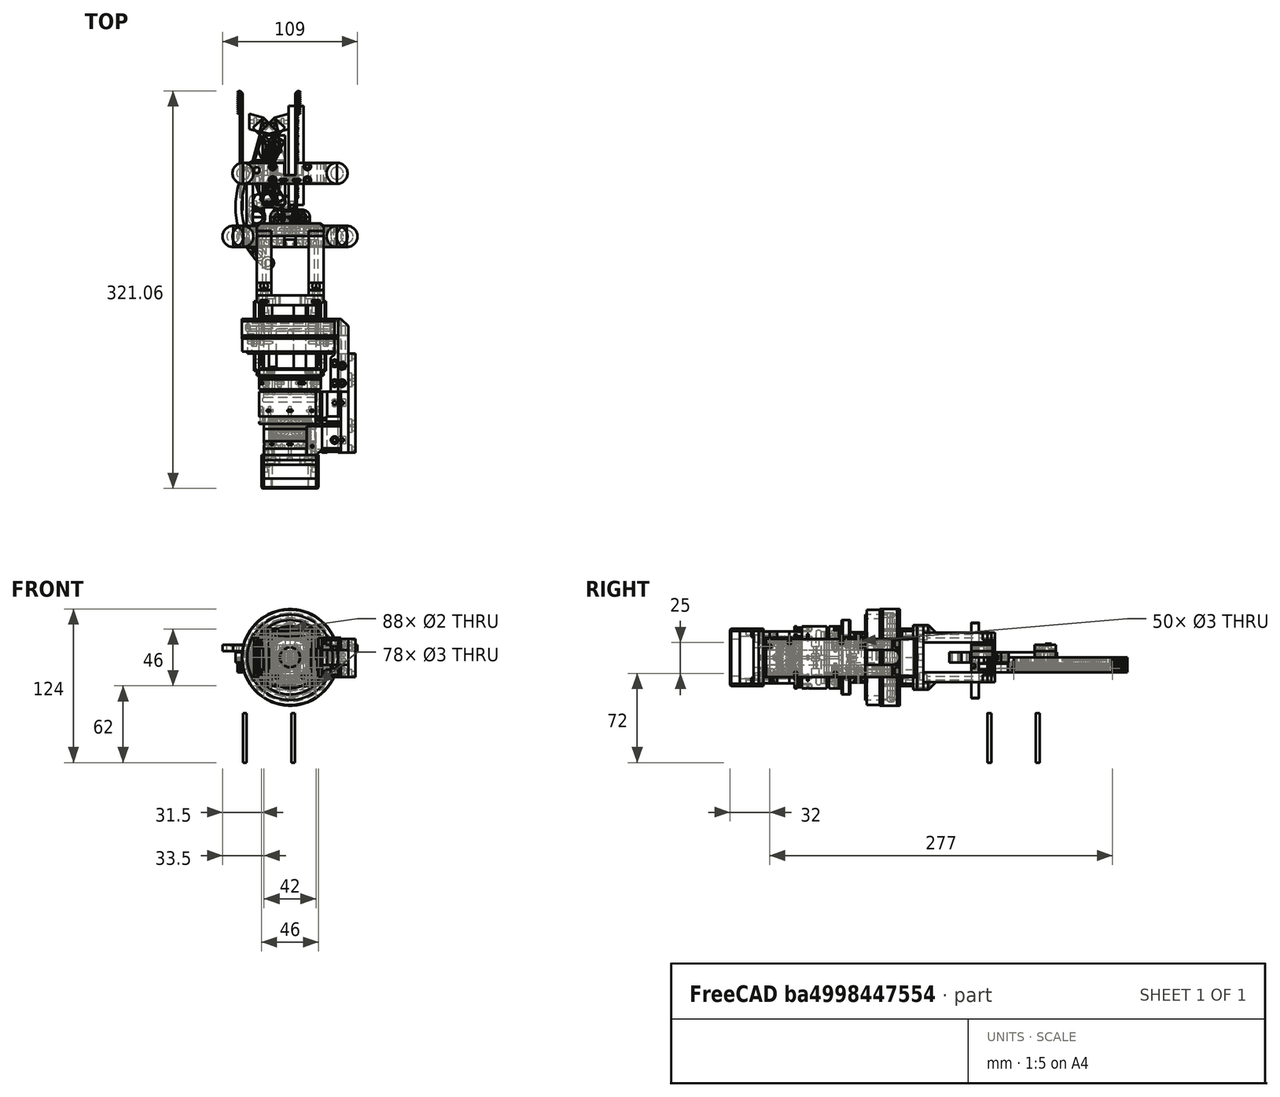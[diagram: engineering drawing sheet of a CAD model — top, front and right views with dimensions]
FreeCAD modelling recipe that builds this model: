
FCSTD DOCUMENT  (FreeCAD 0.19R24276 (Git))
Label: Wrist_001
License: All rights reserved
LicenseURL: http://en.wikipedia.org/wiki/All_rights_reserved
objects: Part::Cylinder×760, Part::Box×427, Part::Cut×422, Part::Compound×348, Part::Chamfer×68, Part::FeaturePython×42, Part::Fillet×32, Mesh::Feature×20, Part::Mirroring×8, Part::Torus×8, Part::Common×2
note: 2117 computed .brp shape members not serialized (recipe doc carries the construction recipe); baked Part::Feature solids carry a one-line shape summary decoded from their .brp

FEATURE [Part::Box] Box  label="Krychle"
  AttacherType = Attacher::AttachEngine3D
  Height = 10
  Length = 8
  Placement = pos=(-5,0,0) rot=(0,0,1;0rad)
  Width = 56
FEATURE [Part::Box] Box001  label="Krychle001"
  AttacherType = Attacher::AttachEngine3D
  Height = 10
  Length = 8
  Placement = pos=(5,0,0) rot=(0,0,1;0rad)
  Width = 56
FEATURE [Part::Box] Box002  label="Krychle002"
  AttacherType = Attacher::AttachEngine3D
  Height = 12
  Length = 16
  Placement = pos=(-13,24,-2) rot=(0,0,1;0rad)
  Width = 12
FEATURE [Part::Box] Box003  label="Krychle003"
  AttacherType = Attacher::AttachEngine3D
  Height = 12
  Length = 16
  Placement = pos=(-13,32,-2) rot=(0,0,-1;0.314159rad)
  Width = 30
FEATURE [Part::Box] Box004  label="Krychle004"
  AttacherType = Attacher::AttachEngine3D
  Height = 12
  Length = 30
  Placement = pos=(-13,24,-2) rot=(0,0,-1;1.25664rad)
  Width = 16
FEATURE [Part::Box] Box005  label="Krychle005"
  AttacherType = Attacher::AttachEngine3D
  Height = 12
  Length = 40
  Placement = pos=(-20,56,-2) rot=(0,0,1;0rad)
  Width = 20
FEATURE [Part::Cut] Cut
  Base = -> Box003
  Tool = -> Box005
FEATURE [Part::Box] Box006  label="Krychle006"
  AttacherType = Attacher::AttachEngine3D
  Height = 12
  Length = 40
  Placement = pos=(-20,-22,-2) rot=(0,0,1;0rad)
  Width = 20
FEATURE [Part::Cut] Cut001
  Base = -> Box004
  Tool = -> Box006
FEATURE [Part::Box] Box007  label="Krychle007"
  AttacherType = Attacher::AttachEngine3D
  Height = 12
  Length = 10
  Placement = pos=(5,-4,-2) rot=(0,0,1;0rad)
  Width = 56
FEATURE [Part::Box] Box008  label="Krychle008"
  AttacherType = Attacher::AttachEngine3D
  Height = 12
  Length = 8
  Placement = pos=(8,0,-2) rot=(0,0,1;0rad)
  Width = 56
FEATURE [Part::Cut] Cut002
  Base = -> Cut001
  Tool = -> Box007
FEATURE [Part::Cut] Cut003
  Base = -> Cut
  Tool = -> Box008
FEATURE [Part::Cylinder] Cylinder  label="Válec"
  Angle = 360
  AttacherType = Attacher::AttachEngine3D
  Height = 4
  Placement = pos=(-10,28,1) rot=(0,0,1;0rad)
  Radius = 5
FEATURE [Part::Cylinder] Cylinder001  label="Válec001"
  Angle = 360
  AttacherType = Attacher::AttachEngine3D
  Height = 5
  Placement = pos=(-10,28,5) rot=(0,0,1;0rad)
  Radius = 8
FEATURE [Part::Cut] Cut004
  Base = -> Cut003
  Tool = -> Cylinder
FEATURE [Part::Cylinder] Cylinder002  label="Válec002"
  Angle = 360
  AttacherType = Attacher::AttachEngine3D
  Height = 4
  Placement = pos=(-10,28,1) rot=(0,0,1;0rad)
  Radius = 5
FEATURE [Part::Cut] Cut005
  Base = -> Cut002
  Tool = -> Cylinder002
FEATURE [Part::Cylinder] Cylinder003  label="Válec003"
  Angle = 360
  AttacherType = Attacher::AttachEngine3D
  Height = 4
  Placement = pos=(-10,28,1) rot=(0,0,1;0rad)
  Radius = 5
FEATURE [Part::Cut] Cut006
  Base = -> Box002
  Tool = -> Cylinder003
FEATURE [Part::Box] Box009  label="Krychle009"
  AttacherType = Attacher::AttachEngine3D
  Height = 12
  Length = 8
  Placement = pos=(-4,16,-2) rot=(0,0,1;0rad)
  Width = 20
FEATURE [Part::Box] Box010  label="Krychle010"
  AttacherType = Attacher::AttachEngine3D
  Height = 12
  Length = 8
  Placement = pos=(-4,36,-2) rot=(0,0,-1;0.488692rad)
  Width = 10
FEATURE [Part::Box] Box011  label="Krychle011"
  AttacherType = Attacher::AttachEngine3D
  Height = 12
  Length = 8
  Placement = pos=(-4,40,-2) rot=(0,0,-1;0.558505rad)
  Width = 18
FEATURE [Part::Mirroring] mirror  label="Krychle011 (mirrored)"
  Base = (0,0,0)
  Normal = (1e-16,-1,0)
  Placement = pos=(0,56,0) rot=(0,0,1;0rad)
  Source = -> Box011
FEATURE [Part::Box] Box012  label="Krychle012"
  AttacherType = Attacher::AttachEngine3D
  Height = 12
  Length = 8
  Placement = pos=(2.5,35,-2) rot=(0,0,1;0.174533rad)
  Width = 10
FEATURE [Part::Box] Box013  label="Krychle013"
  AttacherType = Attacher::AttachEngine3D
  Height = 12
  Length = 8
  Placement = pos=(-4,16,-2) rot=(0,0,1;0rad)
  Width = 24
FEATURE [Part::Box] Box014  label="Krychle014"
  AttacherType = Attacher::AttachEngine3D
  Height = 12
  Length = 8
  Placement = pos=(-4,40,-2) rot=(0,0,-1;0.314159rad)
  Width = 10
FEATURE [Part::Box] Box015  label="Krychle015"
  AttacherType = Attacher::AttachEngine3D
  Height = 12
  Length = 8
  Placement = pos=(2.5,40,-2) rot=(0,0,1;0.349066rad)
  Width = 10
FEATURE [Part::Box] Box016  label="Krychle016"
  AttacherType = Attacher::AttachEngine3D
  Height = 12
  Length = 8
  Placement = pos=(-4,40,-2) rot=(0,0,-1;0.558505rad)
  Width = 18
FEATURE [Part::Mirroring] mirror001  label="Krychle011 (mirrored)001"
  Base = (0,0,0)
  Normal = (1e-16,-1,0)
  Placement = pos=(0,56,0) rot=(0,0,1;0rad)
  Source = -> Box016
FEATURE [Part::Compound] Compound
  Links = -> [Box013,Box014,mirror001,Box015,Box016]
FEATURE [Part::Cut] Cut007
  Base = -> Cut004
  Tool = -> Box009
FEATURE [Part::Cut] Cut008
  Base = -> Cut007
  Tool = -> Box010
FEATURE [Part::Cut] Cut009
  Base = -> Cut008
  Tool = -> Box012
FEATURE [Part::Box] Box017  label="Krychle017"
  AttacherType = Attacher::AttachEngine3D
  Height = 12
  Length = 8
  Placement = pos=(-4,40,-2) rot=(0,0,-1;0.698132rad)
  Width = 18
FEATURE [Part::Box] Box018  label="Krychle018"
  AttacherType = Attacher::AttachEngine3D
  Height = 12
  Length = 8
  Placement = pos=(2.5,40,-2) rot=(0,0,1;0.349066rad)
  Width = 10
FEATURE [Part::Box] Box019  label="Krychle019"
  AttacherType = Attacher::AttachEngine3D
  Height = 12
  Length = 8
  Placement = pos=(-4,40,-2) rot=(0,0,-1;0.314159rad)
  Width = 10
FEATURE [Part::Box] Box020  label="Krychle020"
  AttacherType = Attacher::AttachEngine3D
  Height = 12
  Length = 8
  Placement = pos=(-4,16,-2) rot=(0,0,1;0rad)
  Width = 24
FEATURE [Part::Mirroring] mirror002  label="Krychle011 (mirrored)002"
  Base = (0,0,0)
  Normal = (1e-16,-1,0)
  Placement = pos=(0,56,0) rot=(0,0,1;0rad)
  Source = -> Box017
FEATURE [Part::Cut] Cut010
  Base = -> Cut006
  Tool = -> Box020
FEATURE [Part::Cut] Cut011
  Base = -> Cut005
  Tool = -> mirror002
FEATURE [Part::Box] Box021  label="Krychle021"
  AttacherType = Attacher::AttachEngine3D
  Height = 12
  Length = 8
  Placement = pos=(-4,16,-2) rot=(0,0,1;0rad)
  Width = 24
FEATURE [Part::Cut] Cut012
  Base = -> Cut011
  Tool = -> Box021
FEATURE [Part::Box] Box022  label="Krychle022"
  AttacherType = Attacher::AttachEngine3D
  Height = 12
  Length = 8
  Placement = pos=(1,0,-2) rot=(0,0,1;0rad)
  Width = 40
FEATURE [Part::Cut] Cut013
  Base = -> Cut009
  Tool = -> Box022
FEATURE [Part::Cut] Cut014
  Base = -> Cut013
  Tool = -> Cylinder001
FEATURE [Part::Cylinder] Cylinder004  label="Válec004"
  Angle = 360
  AttacherType = Attacher::AttachEngine3D
  Height = 5
  Placement = pos=(-10,28,5) rot=(0,0,1;0rad)
  Radius = 8
FEATURE [Part::Cylinder] Cylinder005  label="Válec005"
  Angle = 360
  AttacherType = Attacher::AttachEngine3D
  Height = 5
  Placement = pos=(-10,28,5) rot=(0,0,1;0rad)
  Radius = 8
FEATURE [Part::Cut] Cut015
  Base = -> Cut012
  Tool = -> Cylinder004
FEATURE [Part::Cut] Cut016
  Base = -> Cut010
  Tool = -> Cylinder005
FEATURE [Part::Box] Box023  label="Krychle023"
  AttacherType = Attacher::AttachEngine3D
  Height = 5
  Length = 8
  Placement = pos=(-13,-2,5) rot=(0,0,1;0rad)
  Width = 24
FEATURE [Part::Cylinder] Cylinder006  label="Válec006"
  Angle = 360
  AttacherType = Attacher::AttachEngine3D
  Height = 20
  Placement = pos=(-10,28,1) rot=(0,0,1;0rad)
  Radius = 2.5
FEATURE [Part::Cut] Cut017
  Base = -> Cut015
  Tool = -> Box023
FEATURE [Part::Cylinder] Cylinder007  label="Válec007"
  Angle = 360
  AttacherType = Attacher::AttachEngine3D
  Height = 10
  Radius = 1.5
FEATURE [Part::Cylinder] Cylinder008  label="Válec008"
  Angle = 360
  AttacherType = Attacher::AttachEngine3D
  Height = 10
  Placement = pos=(0,50,3) rot=(0,1,0;1.5708rad)
  Radius = 1.5
FEATURE [Part::Box] Box024  label="Krychle024"
  AttacherType = Attacher::AttachEngine3D
  Height = 12
  Length = 13
  Placement = pos=(3,10,-2) rot=(0,0,1;0rad)
  Width = 32
FEATURE [Part::Cut] Cut018
  Base = -> Cut017
  Tool = -> Box024
FEATURE [Part::Cylinder] Cylinder009  label="Válec009"
  Angle = 360
  AttacherType = Attacher::AttachEngine3D
  Height = 4
  Placement = pos=(0,2,1) rot=(0,0,1;0rad)
  Radius = 5
FEATURE [Part::Cylinder] Cylinder010  label="Válec010"
  Angle = 360
  AttacherType = Attacher::AttachEngine3D
  Height = 5
  Placement = pos=(0,2,5) rot=(0,0,1;0rad)
  Radius = 7
FEATURE [Part::Cut] Cut019
  Base = -> Cut018
  Tool = -> Cylinder009
FEATURE [Part::Cut] Cut020
  Base = -> Cut019
  Tool = -> Cylinder010
FEATURE [Part::Cut] Cut021
  Base = -> Cut014
  Tool = -> Cylinder008
FEATURE [Part::Box] Box025  label="Krychle025"
  AttacherType = Attacher::AttachEngine3D
  Height = 12
  Length = 12
  Placement = pos=(-13,24,-2) rot=(0,0,1;0rad)
  Width = 12
FEATURE [Part::Cylinder] Cylinder011  label="Válec011"
  Angle = 360
  AttacherType = Attacher::AttachEngine3D
  Height = 4
  Placement = pos=(-10,30,1) rot=(0,0,1;0rad)
  Radius = 5
FEATURE [Part::Cylinder] Cylinder012  label="Válec012"
  Angle = 360
  AttacherType = Attacher::AttachEngine3D
  Height = 5
  Placement = pos=(-20,30,5) rot=(0,0,1;0rad)
  Radius = 16
FEATURE [Part::Compound] Compound001
  Links = -> [Cylinder011,Cylinder012]
FEATURE [Part::Cut] Cut022
  Base = -> Box025
  Tool = -> Compound001
FEATURE [Part::Box] Box026  label="Krychle026"
  AttacherType = Attacher::AttachEngine3D
  Height = 12
  Length = 12
  Placement = pos=(-13,36,-2) rot=(0,0,-1;0.261799rad)
  Width = 24
FEATURE [Part::Box] Box027  label="Krychle027"
  AttacherType = Attacher::AttachEngine3D
  Height = 12
  Length = 12
  Placement = pos=(-6.8,59.2,-2) rot=(0,0,-1;0.785398rad)
  Width = 16
FEATURE [Part::Box] Box028  label="Krychle028"
  AttacherType = Attacher::AttachEngine3D
  Height = 12
  Length = 12
  Placement = pos=(-4.1,-0.4,-2) rot=(0,0,1;0.349066rad)
  Width = 26
FEATURE [Part::Box] Box029  label="Krychle029"
  AttacherType = Attacher::AttachEngine3D
  Height = 12
  Length = 12
  Placement = pos=(4.5,70.5,-2) rot=(0,0,-1;1.309rad)
  Width = 12
FEATURE [Part::Box] Box030  label="Krychle030"
  AttacherType = Attacher::AttachEngine3D
  Height = 12
  Length = 12
  Placement = pos=(16,0,-2) rot=(0,0,1;0rad)
  Width = 80
FEATURE [Part::Cut] Cut023
  Base = -> Box029
  Tool = -> Box030
FEATURE [Part::Box] Box032  label="Krychle032"
  AttacherType = Attacher::AttachEngine3D
  Height = 12
  Length = 12
  Placement = pos=(16,0,-2) rot=(0,0,1;0rad)
  Width = 80
FEATURE [Part::Box] Box033  label="Krychle033"
  AttacherType = Attacher::AttachEngine3D
  Height = 12
  Length = 12
  Placement = pos=(11.4,-4.4,-2) rot=(0,0,1;1.309rad)
  Width = 18
FEATURE [Part::Cylinder] Cylinder013  label="Válec013"
  Angle = 360
  AttacherType = Attacher::AttachEngine3D
  Height = 7
  Placement = pos=(10,-10,-2) rot=(0,0,1;0rad)
  Radius = 7
FEATURE [Part::Box] Box034  label="Krychle034"
  AttacherType = Attacher::AttachEngine3D
  Height = 7
  Length = 12
  Placement = pos=(4,-10,-2) rot=(0,0,1;0rad)
  Width = 18
FEATURE [Part::Cylinder] Cylinder014  label="Válec014"
  Angle = 360
  AttacherType = Attacher::AttachEngine3D
  Height = 4
  Placement = pos=(10,-10,1) rot=(0,0,1;0rad)
  Radius = 5
FEATURE [Part::Cut] Cut024
  Base = -> Cylinder013
  Tool = -> Cylinder014
FEATURE [Part::Cylinder] Cylinder015  label="Válec015"
  Angle = 360
  AttacherType = Attacher::AttachEngine3D
  Height = 4
  Placement = pos=(10,-10,1) rot=(0,0,1;0rad)
  Radius = 5
FEATURE [Part::Cut] Cut025
  Base = -> Box034
  Tool = -> Cylinder015
FEATURE [Part::Fillet] Fillet
  Base = -> Cut025
  Edges = 1 edges r=4: [Edge16]
FEATURE [Part::Chamfer] Chamfer
  Base = -> Box033
  Edges = 2 edges r=4: [Edge1,Edge5]
FEATURE [Part::Cylinder] Cylinder016  label="Válec016"
  Angle = 360
  AttacherType = Attacher::AttachEngine3D
  Height = 5
  Placement = pos=(-20,30,5) rot=(0,0,1;0rad)
  Radius = 16
FEATURE [Part::Cylinder] Cylinder017  label="Válec017"
  Angle = 360
  AttacherType = Attacher::AttachEngine3D
  Height = 5
  Placement = pos=(-20,30,5) rot=(0,0,1;0rad)
  Radius = 16
FEATURE [Part::Cut] Cut026
  Base = -> Box028
  Tool = -> Cylinder016
FEATURE [Part::Cut] Cut027
  Base = -> Box026
  Tool = -> Cylinder017
FEATURE [Part::Fillet] Fillet001
  Base = -> Cut026
  Edges = 1 edges r=20: [Edge2]
FEATURE [Part::Fillet] Fillet002
  Base = -> Cut027
  Edges = 1 edges r=20: [Edge3]
FEATURE [Part::Fillet] Fillet004
  Base = -> Chamfer
  Edges = 1 edges r=4: [Edge4]
FEATURE [Part::Fillet] Fillet005
  Base = -> Fillet001
  Edges = 1 edges r=2: [Edge2]
FEATURE [Part::Fillet] Fillet006
  Base = -> Fillet004
  Edges = 1 edges r=3: [Edge2]
FEATURE [Part::Fillet] Fillet007
  Base = -> Fillet006
  Edges = 2 edges r=3: [Edge21,Edge23]
FEATURE [Part::Fillet] Fillet008
  Base = -> Fillet007
  Edges = 1 edges r=4: [Edge27]
FEATURE [Part::Box] Box037  label="Krychle037"
  AttacherType = Attacher::AttachEngine3D
  Height = 2
  Length = 6
  Placement = pos=(-2,11,4) rot=(0,0,1;0rad)
  Width = 6
FEATURE [Part::Cylinder] Cylinder020  label="Válec020"
  Angle = 360
  AttacherType = Attacher::AttachEngine3D
  Height = 12
  Placement = pos=(1,14,6) rot=(0,0,1;0rad)
  Radius = 1.5
FEATURE [Part::Cylinder] Cylinder021  label="Válec021"
  Angle = 360
  AttacherType = Attacher::AttachEngine3D
  Height = 4
  Placement = pos=(1,14,0) rot=(0,0,1;0rad)
  Radius = 1.5
FEATURE [Part::Compound] Compound002
  Links = -> [Box037,Cylinder020,Cylinder021]
  Placement = pos=(3.5,2,0) rot=(0,0,1;0.349066rad)
FEATURE [Part::Cylinder] Cylinder022  label="Válec022"
  Angle = 360
  AttacherType = Attacher::AttachEngine3D
  Height = 4
  Placement = pos=(1,14,0) rot=(0,0,1;0rad)
  Radius = 1.5
FEATURE [Part::Box] Box038  label="Krychle038"
  AttacherType = Attacher::AttachEngine3D
  Height = 2
  Length = 6
  Placement = pos=(-2,11,4) rot=(0,0,1;0rad)
  Width = 6
FEATURE [Part::Cylinder] Cylinder023  label="Válec023"
  Angle = 360
  AttacherType = Attacher::AttachEngine3D
  Height = 12
  Placement = pos=(1,14,6) rot=(0,0,1;0rad)
  Radius = 1.5
FEATURE [Part::Compound] Compound003
  Links = -> [Box038,Cylinder023,Cylinder022]
  Placement = pos=(-6.1,31,0) rot=(0,0,-1;0.261799rad)
FEATURE [Part::Cylinder] Cylinder024  label="Válec024"
  Angle = 360
  AttacherType = Attacher::AttachEngine3D
  Height = 4
  Placement = pos=(1,14,0) rot=(0,0,1;0rad)
  Radius = 1.5
FEATURE [Part::Box] Box039  label="Krychle039"
  AttacherType = Attacher::AttachEngine3D
  Height = 2
  Length = 6
  Placement = pos=(-2,11,4) rot=(0,0,1;0rad)
  Width = 6
FEATURE [Part::Cylinder] Cylinder025  label="Válec025"
  Angle = 360
  AttacherType = Attacher::AttachEngine3D
  Height = 12
  Placement = pos=(1,14,6) rot=(0,0,1;0rad)
  Radius = 1.5
FEATURE [Part::Compound] Compound004
  Links = -> [Box039,Cylinder025,Cylinder024]
  Placement = pos=(-2.9,-11.9,0) rot=(0,0,-1;0.261799rad)
FEATURE [Part::Cylinder] Cylinder026  label="Válec026"
  Angle = 360
  AttacherType = Attacher::AttachEngine3D
  Height = 4
  Placement = pos=(1,14,0) rot=(0,0,1;0rad)
  Radius = 1.5
FEATURE [Part::Box] Box040  label="Krychle040"
  AttacherType = Attacher::AttachEngine3D
  Height = 2
  Length = 6
  Placement = pos=(-2,11,4) rot=(0,0,1;0rad)
  Width = 6
FEATURE [Part::Cylinder] Cylinder027  label="Válec027"
  Angle = 360
  AttacherType = Attacher::AttachEngine3D
  Height = 12
  Placement = pos=(1,14,6) rot=(0,0,1;0rad)
  Radius = 1.5
FEATURE [Part::Compound] Compound005
  Links = -> [Box040,Cylinder027,Cylinder026]
  Placement = pos=(-2.9,-11.9,0) rot=(0,0,-1;0.261799rad)
FEATURE [Part::Cut] Cut028
  Base = -> Fillet008
  Tool = -> Compound004
FEATURE [Part::Cut] Cut029
  Base = -> Fillet005
  Tool = -> Compound002
FEATURE [Part::Cut] Cut030
  Base = -> Fillet002
  Tool = -> Compound003
FEATURE [Part::Cylinder] Cylinder028  label="Válec028"
  Angle = 360
  AttacherType = Attacher::AttachEngine3D
  Height = 4
  Placement = pos=(1,14,-0.1) rot=(0,0,1;0rad)
  Radius = 1.5
FEATURE [Part::Box] Box041  label="Krychle041"
  AttacherType = Attacher::AttachEngine3D
  Height = 2
  Length = 6
  Placement = pos=(-2,11,4) rot=(0,0,1;0rad)
  Width = 6
FEATURE [Part::Cylinder] Cylinder029  label="Válec029"
  Angle = 360
  AttacherType = Attacher::AttachEngine3D
  Height = 12
  Placement = pos=(1,14,6) rot=(0,0,1;0rad)
  Radius = 1.5
FEATURE [Part::Compound] Compound006
  Links = -> [Box041,Cylinder029,Cylinder028]
  Placement = pos=(12.1,54,0) rot=(0,0,1;0.785398rad)
FEATURE [Part::Cut] Cut031
  Base = -> Cut029
  Tool = -> Compound005
FEATURE [Part::Cylinder] Cylinder030  label="Válec030"
  Angle = 360
  AttacherType = Attacher::AttachEngine3D
  Height = 4
  Placement = pos=(1,14,-0.1) rot=(0,0,1;0rad)
  Radius = 1.5
FEATURE [Part::Box] Box042  label="Krychle042"
  AttacherType = Attacher::AttachEngine3D
  Height = 2
  Length = 6
  Placement = pos=(-2,11,4) rot=(0,0,1;0rad)
  Width = 6
FEATURE [Part::Cylinder] Cylinder031  label="Válec031"
  Angle = 360
  AttacherType = Attacher::AttachEngine3D
  Height = 12
  Placement = pos=(1,14,6) rot=(0,0,1;0rad)
  Radius = 1.5
FEATURE [Part::Compound] Compound007
  Links = -> [Box042,Cylinder031,Cylinder030]
  Placement = pos=(12.1,54,0) rot=(0,0,1;0.785398rad)
FEATURE [Part::Cut] Cut032
  Base = -> Cut023
  Tool = -> Compound006
FEATURE [Part::Cut] Cut033
  Base = -> Box027
  Tool = -> Compound007
FEATURE [Part::Cylinder] Cylinder032  label="Válec032"
  Angle = 360
  AttacherType = Attacher::AttachEngine3D
  Height = 12
  Placement = pos=(1,14,6) rot=(0,0,1;0rad)
  Radius = 1.5
FEATURE [Part::Box] Box043  label="Krychle043"
  AttacherType = Attacher::AttachEngine3D
  Height = 2
  Length = 6
  Placement = pos=(-2,11,4) rot=(0,0,1;0rad)
  Width = 6
FEATURE [Part::Cylinder] Cylinder033  label="Válec033"
  Angle = 360
  AttacherType = Attacher::AttachEngine3D
  Height = 4
  Placement = pos=(1,14,-0.1) rot=(0,0,1;0rad)
  Radius = 1.5
FEATURE [Part::Compound] Compound008
  Links = -> [Box043,Cylinder032,Cylinder033]
  Placement = pos=(6,53,2) rot=(0,1,0;1.5708rad)
FEATURE [Part::Box] Box044  label="Krychle044"
  AttacherType = Attacher::AttachEngine3D
  Height = 2
  Length = 6
  Placement = pos=(-2,11,4) rot=(0,0,1;0rad)
  Width = 6
FEATURE [Part::Cylinder] Cylinder034  label="Válec034"
  Angle = 360
  AttacherType = Attacher::AttachEngine3D
  Height = 4
  Placement = pos=(1,14,-0.1) rot=(0,0,1;0rad)
  Radius = 1.5
FEATURE [Part::Cylinder] Cylinder035  label="Válec035"
  Angle = 360
  AttacherType = Attacher::AttachEngine3D
  Height = 12
  Placement = pos=(1,14,6) rot=(0,0,1;0rad)
  Radius = 1.5
FEATURE [Part::Compound] Compound009
  Links = -> [Box044,Cylinder035,Cylinder034]
  Placement = pos=(6,53,2) rot=(0,1,0;1.5708rad)
FEATURE [Part::Cut] Cut034
  Base = -> Cut033
  Tool = -> Compound009
FEATURE [Part::Cut] Cut035
  Base = -> Cut032
  Tool = -> Compound008
FEATURE [Part::Cylinder] Cylinder036  label="Válec036"
  Angle = 360
  AttacherType = Attacher::AttachEngine3D
  Height = 5
  Placement = pos=(-20,30,5) rot=(0,0,1;0rad)
  Radius = 16
FEATURE [Part::Box] Box045  label="Krychle045"
  AttacherType = Attacher::AttachEngine3D
  Height = 12
  Length = 12
  Placement = pos=(-13,24,-2) rot=(0,0,1;0rad)
  Width = 12
FEATURE [Part::Cylinder] Cylinder037  label="Válec037"
  Angle = 360
  AttacherType = Attacher::AttachEngine3D
  Height = 4
  Placement = pos=(-10,30,1) rot=(0,0,1;0rad)
  Radius = 5
FEATURE [Part::Cylinder] Cylinder038  label="Válec038"
  Angle = 360
  AttacherType = Attacher::AttachEngine3D
  Height = 16
  Placement = pos=(1,14,1) rot=(0,0,1;0rad)
  Radius = 1.5
FEATURE [Part::Cylinder] Cylinder039  label="Válec039"
  Angle = 360
  AttacherType = Attacher::AttachEngine3D
  Height = 5
  Placement = pos=(-20,30,5) rot=(0,0,1;0rad)
  Radius = 16
FEATURE [Part::Box] Box046  label="Krychle046"
  AttacherType = Attacher::AttachEngine3D
  Height = 12
  Length = 12
  Placement = pos=(-6.8,59.2,-2) rot=(0,0,-1;0.785398rad)
  Width = 16
FEATURE [Part::Box] Box047  label="Krychle047"
  AttacherType = Attacher::AttachEngine3D
  Height = 2
  Length = 6
  Placement = pos=(-2,11,20) rot=(0,0,1;0rad)
  Width = 6
FEATURE [Part::Box] Box048  label="Krychle048"
  AttacherType = Attacher::AttachEngine3D
  Height = 12
  Length = 12
  Placement = pos=(-4.1,-0.4,-2) rot=(0,0,1;0.349066rad)
  Width = 26
FEATURE [Part::Box] Box049  label="Krychle049"
  AttacherType = Attacher::AttachEngine3D
  Height = 12
  Length = 12
  Placement = pos=(-13,36,-2) rot=(0,0,-1;0.261799rad)
  Width = 24
FEATURE [Part::Box] Box050  label="Krychle050"
  AttacherType = Attacher::AttachEngine3D
  Height = 12
  Length = 12
  Placement = pos=(4.5,70.5,-2) rot=(0,0,-1;1.309rad)
  Width = 12
FEATURE [Part::Cylinder] Cylinder040  label="Válec040"
  Angle = 360
  AttacherType = Attacher::AttachEngine3D
  Height = 4
  Placement = pos=(10,-10,1) rot=(0,0,1;0rad)
  Radius = 5
FEATURE [Part::Box] Box051  label="Krychle051"
  AttacherType = Attacher::AttachEngine3D
  Height = 12
  Length = 12
  Placement = pos=(11.4,-4.4,-2) rot=(0,0,1;1.309rad)
  Width = 18
FEATURE [Part::Chamfer] Chamfer001
  Base = -> Box051
  Edges = 2 edges r=4: [Edge1,Edge5]
FEATURE [Part::Fillet] Fillet010
  Base = -> Chamfer001
  Edges = 1 edges r=4: [Edge4]
FEATURE [Part::Box] Box052  label="Krychle052"
  AttacherType = Attacher::AttachEngine3D
  Height = 7
  Length = 12
  Placement = pos=(4,-10,-2) rot=(0,0,1;0rad)
  Width = 18
FEATURE [Part::Cylinder] Cylinder041  label="Válec041"
  Angle = 360
  AttacherType = Attacher::AttachEngine3D
  Height = 4
  Placement = pos=(10,-10,1) rot=(0,0,1;0rad)
  Radius = 5
FEATURE [Part::Cut] Cut036
  Base = -> Box052
  Tool = -> Cylinder041
FEATURE [Part::Box] Box053  label="Krychle053"
  AttacherType = Attacher::AttachEngine3D
  Height = 12
  Length = 12
  Placement = pos=(16,0,-2) rot=(0,0,1;0rad)
  Width = 80
FEATURE [Part::Cut] Cut037
  Base = -> Box050
  Tool = -> Box053
FEATURE [Part::Cylinder] Cylinder042  label="Válec042"
  Angle = 360
  AttacherType = Attacher::AttachEngine3D
  Height = 5
  Placement = pos=(-20,30,5) rot=(0,0,1;0rad)
  Radius = 16
FEATURE [Part::Cylinder] Cylinder043  label="Válec043"
  Angle = 360
  AttacherType = Attacher::AttachEngine3D
  Height = 7
  Placement = pos=(10,-10,-2) rot=(0,0,1;0rad)
  Radius = 7
FEATURE [Part::Cut] Cut038
  Base = -> Box048
  Tool = -> Cylinder042
FEATURE [Part::Fillet] Fillet011
  Base = -> Cut038
  Edges = 1 edges r=20: [Edge2]
FEATURE [Part::Cut] Cut039
  Base = -> Cylinder043
  Tool = -> Cylinder040
FEATURE [Part::Cut] Cut040
  Base = -> Box049
  Tool = -> Cylinder039
FEATURE [Part::Fillet] Fillet009
  Base = -> Cut040
  Edges = 1 edges r=20: [Edge3]
FEATURE [Part::Fillet] Fillet012
  Base = -> Cut036
  Edges = 1 edges r=4: [Edge16]
FEATURE [Part::Fillet] Fillet015
  Base = -> Fillet010
  Edges = 1 edges r=3: [Edge2]
FEATURE [Part::Fillet] Fillet014
  Base = -> Fillet015
  Edges = 2 edges r=3: [Edge21,Edge23]
FEATURE [Part::Fillet] Fillet013
  Base = -> Fillet014
  Edges = 1 edges r=4: [Edge27]
FEATURE [Part::Compound] Compound016
  Links = -> [Cylinder037,Cylinder036]
FEATURE [Part::Cut] Cut041
  Base = -> Box045
  Tool = -> Compound016
FEATURE [Part::Fillet] Fillet016
  Base = -> Fillet011
  Edges = 1 edges r=2: [Edge2]
FEATURE [Part::Cylinder] Cylinder044  label="Válec044"
  Angle = 360
  AttacherType = Attacher::AttachEngine3D
  Height = 3
  Placement = pos=(1,14,-2) rot=(0,0,1;0rad)
  Radius = 3
FEATURE [Part::Box] Box054  label="Krychle054"
  AttacherType = Attacher::AttachEngine3D
  Height = 2
  Length = 6
  Placement = pos=(-2,11,20) rot=(0,0,1;0rad)
  Width = 6
FEATURE [Part::Cylinder] Cylinder045  label="Válec045"
  Angle = 360
  AttacherType = Attacher::AttachEngine3D
  Height = 3
  Placement = pos=(1,14,-2) rot=(0,0,1;0rad)
  Radius = 3
FEATURE [Part::Cylinder] Cylinder046  label="Válec046"
  Angle = 360
  AttacherType = Attacher::AttachEngine3D
  Height = 3
  Placement = pos=(1,14,-2) rot=(0,0,1;0rad)
  Radius = 3
FEATURE [Part::Box] Box055  label="Krychle055"
  AttacherType = Attacher::AttachEngine3D
  Height = 2
  Length = 6
  Placement = pos=(-2,11,20) rot=(0,0,1;0rad)
  Width = 6
FEATURE [Part::Cylinder] Cylinder047  label="Válec047"
  Angle = 360
  AttacherType = Attacher::AttachEngine3D
  Height = 16
  Placement = pos=(1,14,1) rot=(0,0,1;0rad)
  Radius = 1.5
FEATURE [Part::Compound] Compound015
  Links = -> [Box055,Cylinder047,Cylinder045]
  Placement = pos=(-6.1,31,0) rot=(0,0,-1;0.261799rad)
FEATURE [Part::Cut] Cut043
  Base = -> Fillet009
  Tool = -> Compound015
FEATURE [Part::Cylinder] Cylinder048  label="Válec048"
  Angle = 360
  AttacherType = Attacher::AttachEngine3D
  Height = 3
  Placement = pos=(1,14,-2) rot=(0,0,1;0rad)
  Radius = 3
FEATURE [Part::Box] Box056  label="Krychle056"
  AttacherType = Attacher::AttachEngine3D
  Height = 2
  Length = 6
  Placement = pos=(-2,11,20) rot=(0,0,1;0rad)
  Width = 6
FEATURE [Part::Cylinder] Cylinder049  label="Válec049"
  Angle = 360
  AttacherType = Attacher::AttachEngine3D
  Height = 3
  Placement = pos=(1,14,-2) rot=(0,0,1;0rad)
  Radius = 3
FEATURE [Part::Box] Box057  label="Krychle057"
  AttacherType = Attacher::AttachEngine3D
  Height = 2
  Length = 6
  Placement = pos=(-2,11,20) rot=(0,0,1;0rad)
  Width = 6
FEATURE [Part::Cylinder] Cylinder050  label="Válec050"
  Angle = 360
  AttacherType = Attacher::AttachEngine3D
  Height = 16
  Placement = pos=(1,14,1) rot=(0,0,1;0rad)
  Radius = 1.5
FEATURE [Part::Compound] Compound011
  Links = -> [Box057,Cylinder050,Cylinder049]
  Placement = pos=(-2.9,-11.9,0) rot=(0,0,-1;0.261799rad)
FEATURE [Part::Cut] Cut044
  Base = -> Fillet013
  Tool = -> Compound011
FEATURE [Part::Cylinder] Cylinder051  label="Válec051"
  Angle = 360
  AttacherType = Attacher::AttachEngine3D
  Height = 16
  Placement = pos=(1,14,1) rot=(0,0,1;0rad)
  Radius = 1.5
FEATURE [Part::Compound] Compound014
  Links = -> [Box056,Cylinder051,Cylinder048]
  Placement = pos=(-2.9,-11.9,0) rot=(0,0,-1;0.261799rad)
FEATURE [Part::Cylinder] Cylinder052  label="Válec052"
  Angle = 360
  AttacherType = Attacher::AttachEngine3D
  Height = 16
  Placement = pos=(1,14,1) rot=(0,0,1;0rad)
  Radius = 1.5
FEATURE [Part::Compound] Compound012
  Links = -> [Box054,Cylinder052,Cylinder044]
  Placement = pos=(12.1,54,0) rot=(0,0,1;0.785398rad)
FEATURE [Part::Cylinder] Cylinder053  label="Válec053"
  Angle = 360
  AttacherType = Attacher::AttachEngine3D
  Height = 3
  Placement = pos=(1,14,-2) rot=(0,0,1;0rad)
  Radius = 3
FEATURE [Part::Box] Box058  label="Krychle058"
  AttacherType = Attacher::AttachEngine3D
  Height = 2
  Length = 6
  Placement = pos=(-2,11,20) rot=(0,0,1;0rad)
  Width = 6
FEATURE [Part::Cylinder] Cylinder054  label="Válec054"
  Angle = 360
  AttacherType = Attacher::AttachEngine3D
  Height = 16
  Placement = pos=(1,14,1) rot=(0,0,1;0rad)
  Radius = 1.5
FEATURE [Part::Compound] Compound013
  Links = -> [Box058,Cylinder054,Cylinder046]
  Placement = pos=(3.5,2,0) rot=(0,0,1;0.349066rad)
FEATURE [Part::Cut] Cut042
  Base = -> Fillet016
  Tool = -> Compound013
FEATURE [Part::Cut] Cut045
  Base = -> Cut042
  Tool = -> Compound014
FEATURE [Part::Cut] Cut047
  Base = -> Cut037
  Tool = -> Compound012
FEATURE [Part::Box] Box059  label="Krychle059"
  AttacherType = Attacher::AttachEngine3D
  Height = 2
  Length = 6
  Placement = pos=(-2,11,4) rot=(0,0,1;0rad)
  Width = 6
FEATURE [Part::Box] Box060  label="Krychle060"
  AttacherType = Attacher::AttachEngine3D
  Height = 2
  Length = 6
  Placement = pos=(-2,11,4) rot=(0,0,1;0rad)
  Width = 6
FEATURE [Part::Cylinder] Cylinder055  label="Válec055"
  Angle = 360
  AttacherType = Attacher::AttachEngine3D
  Height = 4
  Placement = pos=(1,14,-0.1) rot=(0,0,1;0rad)
  Radius = 1.5
FEATURE [Part::Cylinder] Cylinder056  label="Válec056"
  Angle = 360
  AttacherType = Attacher::AttachEngine3D
  Height = 4
  Placement = pos=(1,14,0) rot=(0,0,1;0rad)
  Radius = 1.5
FEATURE [Part::Cylinder] Cylinder057  label="Válec057"
  Angle = 360
  AttacherType = Attacher::AttachEngine3D
  Height = 12
  Placement = pos=(1,14,6) rot=(0,0,1;0rad)
  Radius = 1.5
FEATURE [Part::Cylinder] Cylinder058  label="Válec058"
  Angle = 360
  AttacherType = Attacher::AttachEngine3D
  Height = 12
  Placement = pos=(1,14,6) rot=(0,0,1;0rad)
  Radius = 1.5
FEATURE [Part::Compound] Compound018
  Links = -> [Box047,Cylinder038,Cylinder053]
  Placement = pos=(12.1,54,0) rot=(0,0,1;0.785398rad)
FEATURE [Part::Cut] Cut049
  Base = -> Box046
  Tool = -> Compound018
FEATURE [Part::Compound] Compound019
  Links = -> [Box060,Cylinder058,Cylinder055]
  Placement = pos=(6,53,2) rot=(0,1,0;1.5708rad)
FEATURE [Part::Cut] Cut048
  Base = -> Cut047
  Tool = -> Compound019
FEATURE [Part::Compound] Compound020
  Links = -> [Box059,Cylinder057,Cylinder056]
  Placement = pos=(6,53,2) rot=(0,1,0;1.5708rad)
FEATURE [Part::Cut] Cut046
  Base = -> Cut049
  Tool = -> Compound020
FEATURE [Part::Box] Box061  label="Krychle061"
  AttacherType = Attacher::AttachEngine3D
  Height = 2
  Length = 6
  Placement = pos=(-2,11,4) rot=(0,0,1;0rad)
  Width = 6
FEATURE [Part::Cylinder] Cylinder059  label="Válec059"
  Angle = 360
  AttacherType = Attacher::AttachEngine3D
  Height = 4
  Placement = pos=(1,14,-0.1) rot=(0,0,1;0rad)
  Radius = 1.5
FEATURE [Part::Cylinder] Cylinder060  label="Válec060"
  Angle = 360
  AttacherType = Attacher::AttachEngine3D
  Height = 12
  Placement = pos=(1,14,6) rot=(0,0,1;0rad)
  Radius = 1.5
FEATURE [Part::Compound] Compound022
  Links = -> [Box061,Cylinder060,Cylinder059]
  Placement = pos=(6,-14,2) rot=(0,1,0;1.5708rad)
FEATURE [Part::Cut] Cut050
  Base = -> Fillet
  Tool = -> Compound022
FEATURE [Part::Cylinder] Cylinder061  label="Válec061"
  Angle = 360
  AttacherType = Attacher::AttachEngine3D
  Height = 4
  Placement = pos=(1,14,-0.1) rot=(0,0,1;0rad)
  Radius = 1.5
FEATURE [Part::Cylinder] Cylinder062  label="Válec062"
  Angle = 360
  AttacherType = Attacher::AttachEngine3D
  Height = 12
  Placement = pos=(1,14,6) rot=(0,0,1;0rad)
  Radius = 1.5
FEATURE [Part::Box] Box062  label="Krychle062"
  AttacherType = Attacher::AttachEngine3D
  Height = 2
  Length = 6
  Placement = pos=(-2,11,4) rot=(0,0,1;0rad)
  Width = 6
FEATURE [Part::Compound] Compound023
  Links = -> [Box062,Cylinder062,Cylinder061]
  Placement = pos=(6,-14,2) rot=(0,1,0;1.5708rad)
FEATURE [Part::Cut] Cut051
  Base = -> Cut028
  Tool = -> Compound023
FEATURE [Part::Cylinder] Cylinder063  label="Válec063"
  Angle = 360
  AttacherType = Attacher::AttachEngine3D
  Height = 4
  Placement = pos=(1,14,-0.1) rot=(0,0,1;0rad)
  Radius = 1.5
FEATURE [Part::Cylinder] Cylinder064  label="Válec064"
  Angle = 360
  AttacherType = Attacher::AttachEngine3D
  Height = 12
  Placement = pos=(1,14,6) rot=(0,0,1;0rad)
  Radius = 1.5
FEATURE [Part::Box] Box063  label="Krychle063"
  AttacherType = Attacher::AttachEngine3D
  Height = 2
  Length = 6
  Placement = pos=(-2,11,4) rot=(0,0,1;0rad)
  Width = 6
FEATURE [Part::Compound] Compound024
  Links = -> [Box063,Cylinder064,Cylinder063]
  Placement = pos=(6,-14,2) rot=(0,1,0;1.5708rad)
FEATURE [Part::Compound] Compound025  label="revised_finger_lower"
  Links = -> [Cut051,Cut050,Cut035,Cut034,Cut031,Cut030,Cut024,Cut022]
FEATURE [Part::Cylinder] Cylinder065  label="Válec065"
  Angle = 360
  AttacherType = Attacher::AttachEngine3D
  Height = 12
  Placement = pos=(1,14,6) rot=(0,0,1;0rad)
  Radius = 1.5
FEATURE [Part::Box] Box064  label="Krychle064"
  AttacherType = Attacher::AttachEngine3D
  Height = 2
  Length = 6
  Placement = pos=(-2,11,4) rot=(0,0,1;0rad)
  Width = 6
FEATURE [Part::Cylinder] Cylinder066  label="Válec066"
  Angle = 360
  AttacherType = Attacher::AttachEngine3D
  Height = 4
  Placement = pos=(1,14,-0.1) rot=(0,0,1;0rad)
  Radius = 1.5
FEATURE [Part::Compound] Compound026
  Links = -> [Box064,Cylinder065,Cylinder066]
  Placement = pos=(6,-14,2) rot=(0,1,0;1.5708rad)
FEATURE [Part::Cut] Cut052
  Base = -> Fillet012
  Tool = -> Compound024
FEATURE [Part::Cut] Cut053
  Base = -> Cut044
  Tool = -> Compound026
FEATURE [Part::Compound] Compound027  label="revised_finger_upper"
  Links = -> [Cut039,Cut041,Cut043,Cut045,Cut046,Cut048,Cut052,Cut053]
FEATURE [Part::Cylinder] Cylinder067  label="Válec067"
  Angle = 360
  AttacherType = Attacher::AttachEngine3D
  Height = 8
  Placement = pos=(10,-10,6) rot=(0,0,1;0rad)
  Radius = 6
FEATURE [Part::Box] Box065  label="Krychle065"
  AttacherType = Attacher::AttachEngine3D
  Height = 4
  Length = 14
  Placement = pos=(10,-15,6) rot=(0,0,1;0rad)
  Width = 10
FEATURE [Part::Cylinder] Cylinder068  label="Válec068"
  Angle = 360
  AttacherType = Attacher::AttachEngine3D
  Height = 8
  Placement = pos=(24,-10,6) rot=(0,0,1;0rad)
  Radius = 5
FEATURE [Part::Box] Box066  label="Krychle066"
  AttacherType = Attacher::AttachEngine3D
  Height = 4
  Length = 14
  Placement = pos=(10,-15,10) rot=(0,0,1;0rad)
  Width = 10
FEATURE [Part::Box] Box067  label="Krychle067"
  AttacherType = Attacher::AttachEngine3D
  Height = 4
  Length = 12
  Placement = pos=(5,-24,6) rot=(0,0,1;0rad)
  Width = 14
FEATURE [Part::Box] Box068  label="Krychle068"
  AttacherType = Attacher::AttachEngine3D
  Height = 8
  Length = 26
  Placement = pos=(4,-15,6) rot=(0,0,1;0rad)
  Width = 5
FEATURE [Part::Box] Box069  label="Krychle069"
  AttacherType = Attacher::AttachEngine3D
  Height = 8
  Length = 54
  Placement = pos=(-10,-21,6) rot=(0,0,1;0rad)
  Width = 6
FEATURE [Part::Box] Box072  label="Krychle072"
  AttacherType = Attacher::AttachEngine3D
  Height = 8
  Length = 12
  Placement = pos=(-10,-73,22) rot=(0,0,1;0rad)
  Width = 52
FEATURE [Part::Box] Box073  label="Krychle073"
  AttacherType = Attacher::AttachEngine3D
  Height = 8
  Length = 12
  Placement = pos=(-10,-73,-10) rot=(0,0,1;0rad)
  Width = 52
FEATURE [Part::Box] Box074  label="Krychle074"
  AttacherType = Attacher::AttachEngine3D
  Height = 4
  Length = 12
  Placement = pos=(17,-24,10) rot=(0,0,1;0rad)
  Width = 14
FEATURE [Part::Box] Box075  label="Krychle075"
  AttacherType = Attacher::AttachEngine3D
  Height = 4
  Length = 12
  Placement = pos=(17,-24,6) rot=(0,0,1;0rad)
  Width = 14
FEATURE [Part::Box] Box076  label="Krychle076"
  AttacherType = Attacher::AttachEngine3D
  Height = 4
  Length = 14
  Placement = pos=(10,-15,6) rot=(0,0,1;0rad)
  Width = 10
FEATURE [Part::Cylinder] Cylinder069  label="Válec069"
  Angle = 360
  AttacherType = Attacher::AttachEngine3D
  Height = 8
  Placement = pos=(24,-10,6) rot=(0,0,1;0rad)
  Radius = 5
FEATURE [Part::Cut] Cut054
  Base = -> Box076
  Tool = -> Cylinder069
FEATURE [Part::Cut] Cut055
  Base = -> Cut054
  Tool = -> Box075
FEATURE [Part::Cylinder] Cylinder070  label="Válec070"
  Angle = 360
  AttacherType = Attacher::AttachEngine3D
  Height = 8
  Placement = pos=(24,-10,6) rot=(0,0,1;0rad)
  Radius = 6
FEATURE [Part::Box] Box077  label="Krychle077"
  AttacherType = Attacher::AttachEngine3D
  Height = 8
  Length = 14
  Placement = pos=(10,-15,6) rot=(0,0,1;0rad)
  Width = 11
FEATURE [Part::Box] Box078  label="Krychle078"
  AttacherType = Attacher::AttachEngine3D
  Height = 4
  Length = 4
  Placement = pos=(4,-14,8) rot=(0,0,1;0rad)
  Width = 1.4
FEATURE [Part::Cylinder] Cylinder071  label="Válec071"
  Angle = 360
  AttacherType = Attacher::AttachEngine3D
  Height = 12
  Placement = pos=(10,-10,4) rot=(0,0,1;0rad)
  Radius = 2.6
FEATURE [Part::Box] Box079  label="Krychle079"
  AttacherType = Attacher::AttachEngine3D
  Height = 4
  Length = 4
  Placement = pos=(15,-11,10) rot=(0,0,1;0rad)
  Width = 1.4
FEATURE [Part::Box] Box080  label="Krychle080"
  AttacherType = Attacher::AttachEngine3D
  Height = 4
  Length = 4
  Placement = pos=(15,-11,6) rot=(0,0,1;0rad)
  Width = 1.4
FEATURE [Part::Box] Box081  label="Krychle081"
  AttacherType = Attacher::AttachEngine3D
  Height = 4
  Length = 4
  Placement = pos=(26,-14,8) rot=(0,0,1;0rad)
  Width = 1.4
FEATURE [Part::Cylinder] Cylinder072  label="Válec072"
  Angle = 360
  AttacherType = Attacher::AttachEngine3D
  Height = 20
  Placement = pos=(3,-10,10) rot=(1,0,0;1.5708rad)
  Radius = 1
FEATURE [Part::Cylinder] Cylinder073  label="Válec073"
  Angle = 360
  AttacherType = Attacher::AttachEngine3D
  Height = 20
  Placement = pos=(31,-10,10) rot=(1,0,0;1.5708rad)
  Radius = 1
FEATURE [Part::Cylinder] Cylinder074  label="Válec074"
  Angle = 360
  AttacherType = Attacher::AttachEngine3D
  Height = 20
  Placement = pos=(17,-10,8) rot=(1,0,0;1.5708rad)
  Radius = 1
FEATURE [Part::Cylinder] Cylinder075  label="Válec075"
  Angle = 360
  AttacherType = Attacher::AttachEngine3D
  Height = 20
  Placement = pos=(17,-10,12) rot=(1,0,0;1.5708rad)
  Radius = 1
FEATURE [Part::Compound] Compound028
  Links = -> [Box072,Box073]
FEATURE [Part::Box] Box083  label="Krychle083"
  AttacherType = Attacher::AttachEngine3D
  Height = 8
  Length = 12
  Placement = pos=(-5,-73,-10) rot=(0,0,1;0rad)
  Width = 52
FEATURE [Part::Box] Box085  label="Krychle085"
  AttacherType = Attacher::AttachEngine3D
  Height = 8
  Length = 12
  Placement = pos=(-5,-73,22) rot=(0,0,1;0rad)
  Width = 52
FEATURE [Part::Compound] Compound029
  Links = -> [Box085,Box083]
  Placement = pos=(37,0,0) rot=(0,0,1;0rad)
FEATURE [Part::Cylinder] Cylinder076  label="Válec076"
  Angle = 360
  AttacherType = Attacher::AttachEngine3D
  Height = 2
  Placement = pos=(3,-10,10) rot=(1,0,0;1.5708rad)
  Radius = 2
FEATURE [Part::Cylinder] Cylinder077  label="Válec077"
  Angle = 360
  AttacherType = Attacher::AttachEngine3D
  Height = 2
  Placement = pos=(31,-10,10) rot=(1,0,0;1.5708rad)
  Radius = 2
FEATURE [Part::Cylinder] Cylinder078  label="Válec078"
  Angle = 360
  AttacherType = Attacher::AttachEngine3D
  Height = 2
  Placement = pos=(17,-10,8) rot=(1,0,0;1.5708rad)
  Radius = 2
FEATURE [Part::Cylinder] Cylinder079  label="Válec079"
  Angle = 360
  AttacherType = Attacher::AttachEngine3D
  Height = 2
  Placement = pos=(17,-10,12) rot=(1,0,0;1.5708rad)
  Radius = 2
FEATURE [Part::Compound] Compound030
  Links = -> [Cylinder072,Cylinder073,Cylinder074,Cylinder075]
FEATURE [Part::Compound] Compound031
  Links = -> [Cylinder076,Cylinder077,Cylinder078,Cylinder079]
  Placement = pos=(0,-9,0) rot=(0,0,1;0rad)
FEATURE [Part::Cut] Cut056
  Base = -> Box069
  Tool = -> Compound031
FEATURE [Part::Cut] Cut057
  Base = -> Cut056
  Tool = -> Compound030
FEATURE [Part::Compound] Compound033
  Links = -> [Compound028,Compound029]
FEATURE [Part::Cylinder] Cylinder084  label="Válec084"
  Angle = 360
  AttacherType = Attacher::AttachEngine3D
  Height = 10
  Placement = pos=(7,-10,-4) rot=(0,0,1;0rad)
  Radius = 8
FEATURE [Part::Cylinder] Cylinder085  label="Válec085"
  Angle = 360
  AttacherType = Attacher::AttachEngine3D
  Height = 10
  Placement = pos=(27,-10,-4) rot=(0,0,1;0rad)
  Radius = 8
FEATURE [Part::Box] Box086  label="Krychle086"
  AttacherType = Attacher::AttachEngine3D
  Height = 10
  Length = 54
  Placement = pos=(-10,-21,-4) rot=(0,0,1;0rad)
  Width = 6
FEATURE [Part::Box] Box087  label="Krychle087"
  AttacherType = Attacher::AttachEngine3D
  Height = 10
  Length = 54
  Placement = pos=(-10,-21,14) rot=(0,0,1;0rad)
  Width = 6
FEATURE [Part::Cylinder] Cylinder086  label="Válec086"
  Angle = 360
  AttacherType = Attacher::AttachEngine3D
  Height = 10
  Placement = pos=(7,-10,14) rot=(0,0,1;0rad)
  Radius = 8
FEATURE [Part::Cylinder] Cylinder087  label="Válec087"
  Angle = 360
  AttacherType = Attacher::AttachEngine3D
  Height = 10
  Placement = pos=(27,-10,14) rot=(0,0,1;0rad)
  Radius = 8
FEATURE [Part::Cut] Cut059
  Base = -> Box087
  Tool = -> Cylinder086
FEATURE [Part::Cut] Cut060
  Base = -> Cut059
  Tool = -> Cylinder087
FEATURE [Part::Cut] Cut061
  Base = -> Box086
  Tool = -> Cylinder084
FEATURE [Part::Cut] Cut062
  Base = -> Cut061
  Tool = -> Cylinder085
FEATURE [Part::Box] Box088  label="Krychle088"
  AttacherType = Attacher::AttachEngine3D
  Height = 6
  Length = 6
  Placement = pos=(-7,-41,-10) rot=(0,0,1;0rad)
  Width = 2
FEATURE [Part::Box] Box089  label="Krychle089"
  AttacherType = Attacher::AttachEngine3D
  Height = 6
  Length = 6
  Placement = pos=(35,-41,-10) rot=(0,0,1;0rad)
  Width = 2
FEATURE [Part::Box] Box090  label="Krychle090"
  AttacherType = Attacher::AttachEngine3D
  Height = 6
  Length = 6
  Placement = pos=(-7,-41,24) rot=(0,0,1;0rad)
  Width = 2
FEATURE [Part::Box] Box091  label="Krychle091"
  AttacherType = Attacher::AttachEngine3D
  Height = 6
  Length = 6
  Placement = pos=(35,-41,24) rot=(0,0,1;0rad)
  Width = 2
FEATURE [Part::Compound] Compound034
  Links = -> [Box088,Box089,Box090,Box091]
  Placement = pos=(0,-200,0) rot=(0,0,1;0rad)
FEATURE [Part::Cylinder] Cylinder088  label="Válec088"
  Angle = 360
  AttacherType = Attacher::AttachEngine3D
  Height = 20
  Placement = pos=(-5,-17,10) rot=(1,0,0;1.5708rad)
  Radius = 2.65
FEATURE [Part::Cylinder] Cylinder089  label="Válec089"
  Angle = 360
  AttacherType = Attacher::AttachEngine3D
  Height = 20
  Placement = pos=(39,-17,10) rot=(1,0,0;1.5708rad)
  Radius = 2.65
FEATURE [Part::Compound] Compound035
  Links = -> [Cylinder088,Cylinder089]
FEATURE [Part::Cut] Cut064
  Base = -> Cut057
  Tool = -> Compound035
FEATURE [Part::Cylinder] Cylinder090  label="Válec090"
  Angle = 360
  AttacherType = Attacher::AttachEngine3D
  Height = 50
  Placement = pos=(-5,-32,-7) rot=(1,0,0;1.5708rad)
  Radius = 1.5
FEATURE [Part::Cylinder] Cylinder091  label="Válec091"
  Angle = 360
  AttacherType = Attacher::AttachEngine3D
  Height = 50
  Placement = pos=(39,-32,27) rot=(1,0,0;1.5708rad)
  Radius = 1.5
FEATURE [Part::Cylinder] Cylinder092  label="Válec092"
  Angle = 360
  AttacherType = Attacher::AttachEngine3D
  Height = 50
  Placement = pos=(-5,-32,27) rot=(1,0,0;1.5708rad)
  Radius = 1.5
FEATURE [Part::Cylinder] Cylinder093  label="Válec093"
  Angle = 360
  AttacherType = Attacher::AttachEngine3D
  Height = 50
  Placement = pos=(39,-32,-7) rot=(1,0,0;1.5708rad)
  Radius = 1.5
FEATURE [Part::Compound] Compound036
  Links = -> [Cylinder092,Cylinder090,Cylinder091,Cylinder093]
  Placement = pos=(0,20,0) rot=(0,0,1;0rad)
FEATURE [Part::Compound] Compound037
  Links = -> [Cut060,Cut062]
FEATURE [Part::Cut] Cut065
  Base = -> Compound037
  Tool = -> Compound036
FEATURE [Part::Cylinder] Cylinder094  label="Válec094"
  Angle = 360
  AttacherType = Attacher::AttachEngine3D
  Height = 3
  Placement = pos=(-5,-32,-7) rot=(1,0,0;1.5708rad)
  Radius = 3
FEATURE [Part::Cylinder] Cylinder095  label="Válec095"
  Angle = 360
  AttacherType = Attacher::AttachEngine3D
  Height = 3
  Placement = pos=(39,-32,27) rot=(1,0,0;1.5708rad)
  Radius = 3
FEATURE [Part::Cylinder] Cylinder096  label="Válec096"
  Angle = 360
  AttacherType = Attacher::AttachEngine3D
  Height = 3
  Placement = pos=(39,-32,-7) rot=(1,0,0;1.5708rad)
  Radius = 3
FEATURE [Part::Cylinder] Cylinder097  label="Válec097"
  Angle = 360
  AttacherType = Attacher::AttachEngine3D
  Height = 3
  Placement = pos=(-5,-32,27) rot=(1,0,0;1.5708rad)
  Radius = 3
FEATURE [Part::Compound] Compound038
  Links = -> [Cylinder097,Cylinder094,Cylinder095,Cylinder096]
  Placement = pos=(0,17,0) rot=(0,0,1;0rad)
FEATURE [Part::Cut] Cut066
  Base = -> Cut065
  Tool = -> Compound038
FEATURE [Part::Cylinder] Cylinder098  label="Válec098"
  Angle = 360
  AttacherType = Attacher::AttachEngine3D
  Height = 3
  Placement = pos=(33,-32,0) rot=(1,0,0;1.5708rad)
  Radius = 3
FEATURE [Part::Cylinder] Cylinder099  label="Válec099"
  Angle = 360
  AttacherType = Attacher::AttachEngine3D
  Height = 3
  Placement = pos=(33,-32,20) rot=(1,0,0;1.5708rad)
  Radius = 3
FEATURE [Part::Cylinder] Cylinder100  label="Válec100"
  Angle = 360
  AttacherType = Attacher::AttachEngine3D
  Height = 3
  Placement = pos=(1,-32,0) rot=(1,0,0;1.5708rad)
  Radius = 3
FEATURE [Part::Cylinder] Cylinder101  label="Válec101"
  Angle = 360
  AttacherType = Attacher::AttachEngine3D
  Height = 3
  Placement = pos=(1,-32,20) rot=(1,0,0;1.5708rad)
  Radius = 3
FEATURE [Part::Compound] Compound039
  Links = -> [Cylinder101,Cylinder100,Cylinder099,Cylinder098]
  Placement = pos=(0,17,0) rot=(0,0,1;0rad)
FEATURE [Part::Cylinder] Cylinder102  label="Válec102"
  Angle = 360
  AttacherType = Attacher::AttachEngine3D
  Height = 12
  Placement = pos=(24,-10,4) rot=(0,0,1;0rad)
  Radius = 2.6
FEATURE [Part::Compound] Compound041
  Links = -> [Cylinder102,Cylinder071]
FEATURE [Part::Cylinder] Cylinder103  label="Válec103"
  Angle = 360
  AttacherType = Attacher::AttachEngine3D
  Height = 12
  Placement = pos=(10,-10,4) rot=(0,0,1;0rad)
  Radius = 2.6
FEATURE [Part::Cylinder] Cylinder104  label="Válec104"
  Angle = 360
  AttacherType = Attacher::AttachEngine3D
  Height = 12
  Placement = pos=(24,-10,4) rot=(0,0,1;0rad)
  Radius = 2.6
FEATURE [Part::Compound] Compound042
  Links = -> [Cylinder104,Cylinder103]
FEATURE [Part::Compound] Compound043
  Links = -> [Cylinder070,Cylinder067]
FEATURE [Part::Cut] Cut068
  Base = -> Compound043
  Tool = -> Compound042
FEATURE [Part::Cut] Cut069
  Base = -> Box077
  Tool = -> Compound041
FEATURE [Part::Compound] Compound044
  Links = -> [Box078,Box079,Box080,Box081]
FEATURE [Part::Box] Box092  label="Krychle092"
  AttacherType = Attacher::AttachEngine3D
  Height = 4
  Length = 4
  Placement = pos=(15,-11,10) rot=(0,0,1;0rad)
  Width = 1.4
FEATURE [Part::Box] Box093  label="Krychle093"
  AttacherType = Attacher::AttachEngine3D
  Height = 4
  Length = 4
  Placement = pos=(4,-14,8) rot=(0,0,1;0rad)
  Width = 1.4
FEATURE [Part::Box] Box094  label="Krychle094"
  AttacherType = Attacher::AttachEngine3D
  Height = 4
  Length = 4
  Placement = pos=(15,-11,6) rot=(0,0,1;0rad)
  Width = 1.4
FEATURE [Part::Box] Box095  label="Krychle095"
  AttacherType = Attacher::AttachEngine3D
  Height = 4
  Length = 4
  Placement = pos=(26,-14,8) rot=(0,0,1;0rad)
  Width = 1.4
FEATURE [Part::Compound] Compound045
  Links = -> [Box093,Box092,Box094,Box095]
FEATURE [Part::Cylinder] Cylinder105  label="Válec105"
  Angle = 360
  AttacherType = Attacher::AttachEngine3D
  Height = 20
  Placement = pos=(17,-6,8) rot=(1,0,0;1.5708rad)
  Radius = 1
FEATURE [Part::Cylinder] Cylinder106  label="Válec106"
  Angle = 360
  AttacherType = Attacher::AttachEngine3D
  Height = 20
  Placement = pos=(6,-10,10) rot=(1,0,0;1.5708rad)
  Radius = 1
FEATURE [Part::Cylinder] Cylinder107  label="Válec107"
  Angle = 360
  AttacherType = Attacher::AttachEngine3D
  Height = 20
  Placement = pos=(28,-10,10) rot=(1,0,0;1.5708rad)
  Radius = 1
FEATURE [Part::Cylinder] Cylinder108  label="Válec108"
  Angle = 360
  AttacherType = Attacher::AttachEngine3D
  Height = 20
  Placement = pos=(17,-6,12) rot=(1,0,0;1.5708rad)
  Radius = 1
FEATURE [Part::Compound] Compound046
  Links = -> [Cylinder106,Cylinder107,Cylinder105,Cylinder108]
FEATURE [Part::Cylinder] Cylinder109  label="Válec109"
  Angle = 360
  AttacherType = Attacher::AttachEngine3D
  Height = 20
  Placement = pos=(28,-10,10) rot=(1,0,0;1.5708rad)
  Radius = 1
FEATURE [Part::Cylinder] Cylinder110  label="Válec110"
  Angle = 360
  AttacherType = Attacher::AttachEngine3D
  Height = 20
  Placement = pos=(17,-10,12) rot=(1,0,0;1.5708rad)
  Radius = 1
FEATURE [Part::Cylinder] Cylinder111  label="Válec111"
  Angle = 360
  AttacherType = Attacher::AttachEngine3D
  Height = 20
  Placement = pos=(17,-10,8) rot=(1,0,0;1.5708rad)
  Radius = 1
FEATURE [Part::Cylinder] Cylinder112  label="Válec112"
  Angle = 360
  AttacherType = Attacher::AttachEngine3D
  Height = 20
  Placement = pos=(6,-10,10) rot=(1,0,0;1.5708rad)
  Radius = 1
FEATURE [Part::Compound] Compound047
  Links = -> [Cylinder112,Cylinder109,Cylinder111,Cylinder110]
FEATURE [Part::Cut] Cut070
  Base = -> Cut069
  Tool = -> Compound046
FEATURE [Part::Cut] Cut071
  Base = -> Cut068
  Tool = -> Compound047
FEATURE [Part::Cut] Cut072
  Base = -> Cut071
  Tool = -> Compound045
FEATURE [Part::Cut] Cut073
  Base = -> Cut070
  Tool = -> Compound044
FEATURE [Part::Cylinder] Cylinder113  label="Válec113"
  Angle = 360
  AttacherType = Attacher::AttachEngine3D
  Height = 20
  Placement = pos=(28,-10,10) rot=(1,0,0;1.5708rad)
  Radius = 1
FEATURE [Part::Cylinder] Cylinder114  label="Válec114"
  Angle = 360
  AttacherType = Attacher::AttachEngine3D
  Height = 20
  Placement = pos=(17,-6,12) rot=(1,0,0;1.5708rad)
  Radius = 1
FEATURE [Part::Cylinder] Cylinder115  label="Válec115"
  Angle = 360
  AttacherType = Attacher::AttachEngine3D
  Height = 20
  Placement = pos=(17,-6,8) rot=(1,0,0;1.5708rad)
  Radius = 1
FEATURE [Part::Cylinder] Cylinder116  label="Válec116"
  Angle = 360
  AttacherType = Attacher::AttachEngine3D
  Height = 20
  Placement = pos=(6,-10,10) rot=(1,0,0;1.5708rad)
  Radius = 1
FEATURE [Part::Compound] Compound048
  Links = -> [Cylinder116,Cylinder113,Cylinder115,Cylinder114]
FEATURE [Part::Box] Box096  label="Krychle096"
  AttacherType = Attacher::AttachEngine3D
  Height = 4
  Length = 4
  Placement = pos=(15,-11,10) rot=(0,0,1;0rad)
  Width = 1.4
FEATURE [Part::Box] Box097  label="Krychle097"
  AttacherType = Attacher::AttachEngine3D
  Height = 4
  Length = 4
  Placement = pos=(4,-14,8) rot=(0,0,1;0rad)
  Width = 1.4
FEATURE [Part::Box] Box098  label="Krychle098"
  AttacherType = Attacher::AttachEngine3D
  Height = 4
  Length = 4
  Placement = pos=(15,-11,6) rot=(0,0,1;0rad)
  Width = 1.4
FEATURE [Part::Box] Box099  label="Krychle099"
  AttacherType = Attacher::AttachEngine3D
  Height = 4
  Length = 4
  Placement = pos=(26,-14,8) rot=(0,0,1;0rad)
  Width = 1.4
FEATURE [Part::Compound] Compound049
  Links = -> [Box097,Box096,Box098,Box099]
FEATURE [Part::Cylinder] Cylinder117  label="Válec117"
  Angle = 360
  AttacherType = Attacher::AttachEngine3D
  Height = 12
  Placement = pos=(10,-10,4) rot=(0,0,1;0rad)
  Radius = 2.6
FEATURE [Part::Cylinder] Cylinder118  label="Válec118"
  Angle = 360
  AttacherType = Attacher::AttachEngine3D
  Height = 12
  Placement = pos=(24,-10,4) rot=(0,0,1;0rad)
  Radius = 2.6
FEATURE [Part::Compound] Compound050
  Links = -> [Cylinder118,Cylinder117]
FEATURE [Part::Cut] Cut074
  Base = -> Box068
  Tool = -> Compound050
FEATURE [Part::Cut] Cut075
  Base = -> Cut074
  Tool = -> Compound049
FEATURE [Part::Cut] Cut076
  Base = -> Cut075
  Tool = -> Compound048
FEATURE [Part::Box] Box100  label="Krychle100"
  AttacherType = Attacher::AttachEngine3D
  Height = 8
  Length = 26
  Placement = pos=(4,-21,6) rot=(0,0,1;0rad)
  Width = 6
FEATURE [Part::Cut] Cut077
  Base = -> Cut072
  Tool = -> Box100
FEATURE [Part::Compound] Compound051  label="wrist_holdo"
  Links = -> [Cut073,Cut076,Cut077]
FEATURE [Mesh::Feature] Mesh001  label="wrist_holdo (Meshed)"
FEATURE [Part::Cylinder] Cylinder119  label="Válec119"
  Angle = 360
  AttacherType = Attacher::AttachEngine3D
  Height = 4
  Placement = pos=(10,-10,1) rot=(0,0,1;0rad)
  Radius = 5
FEATURE [Part::Cylinder] Cylinder120  label="Válec120"
  Angle = 360
  AttacherType = Attacher::AttachEngine3D
  Height = 4
  Placement = pos=(-10,30,1) rot=(0,0,1;0rad)
  Radius = 5
FEATURE [Part::Cylinder] Cylinder121  label="Válec121"
  Angle = 360
  AttacherType = Attacher::AttachEngine3D
  Height = 5
  Placement = pos=(-20,30,5) rot=(0,0,1;0rad)
  Radius = 16
FEATURE [Part::Compound] Compound052
  Links = -> [Cylinder120,Cylinder121]
FEATURE [Part::Box] Box101  label="Krychle101"
  AttacherType = Attacher::AttachEngine3D
  Height = 12
  Length = 12
  Placement = pos=(-13,36,-2) rot=(0,0,-1;0.261799rad)
  Width = 24
FEATURE [Part::Box] Box102  label="Krychle102"
  AttacherType = Attacher::AttachEngine3D
  Height = 12
  Length = 12
  Placement = pos=(-13,24,-2) rot=(0,0,1;0rad)
  Width = 12
FEATURE [Part::Cut] Cut083
  Base = -> Box102
  Tool = -> Compound052
FEATURE [Part::Box] Box103  label="Krychle103"
  AttacherType = Attacher::AttachEngine3D
  Height = 12
  Length = 12
  Placement = pos=(-4.1,-0.4,-2) rot=(0,0,1;0.349066rad)
  Width = 26
FEATURE [Part::Box] Box104  label="Krychle104"
  AttacherType = Attacher::AttachEngine3D
  Height = 12
  Length = 12
  Placement = pos=(4.5,70.5,-2) rot=(0,0,-1;1.309rad)
  Width = 12
FEATURE [Part::Box] Box105  label="Krychle105"
  AttacherType = Attacher::AttachEngine3D
  Height = 12
  Length = 12
  Placement = pos=(-6.8,59.2,-2) rot=(0,0,-1;0.785398rad)
  Width = 16
FEATURE [Part::Box] Box106  label="Krychle106"
  AttacherType = Attacher::AttachEngine3D
  Height = 12
  Length = 12
  Placement = pos=(16,0,-2) rot=(0,0,1;0rad)
  Width = 80
FEATURE [Part::Cut] Cut084
  Base = -> Box104
  Tool = -> Box106
FEATURE [Part::Box] Box107  label="Krychle107"
  AttacherType = Attacher::AttachEngine3D
  Height = 12
  Length = 12
  Placement = pos=(11.4,-4.4,-2) rot=(0,0,1;1.309rad)
  Width = 18
FEATURE [Part::Chamfer] Chamfer008
  Base = -> Box107
  Edges = 2 edges r=4: [Edge1,Edge5]
FEATURE [Part::Fillet] Fillet022
  Base = -> Chamfer008
  Edges = 1 edges r=4: [Edge4]
FEATURE [Part::Fillet] Fillet017
  Base = -> Fillet022
  Edges = 1 edges r=3: [Edge2]
FEATURE [Part::Fillet] Fillet018
  Base = -> Fillet017
  Edges = 2 edges r=3: [Edge21,Edge23]
FEATURE [Part::Fillet] Fillet019
  Base = -> Fillet018
  Edges = 1 edges r=4: [Edge27]
FEATURE [Part::Cylinder] Cylinder122  label="Válec122"
  Angle = 360
  AttacherType = Attacher::AttachEngine3D
  Height = 7
  Placement = pos=(10,-10,-2) rot=(0,0,1;0rad)
  Radius = 7
FEATURE [Part::Box] Box108  label="Krychle108"
  AttacherType = Attacher::AttachEngine3D
  Height = 7
  Length = 12
  Placement = pos=(4,-10,-2) rot=(0,0,1;0rad)
  Width = 18
FEATURE [Part::Cut] Cut085
  Base = -> Box108
  Tool = -> Cylinder119
FEATURE [Part::Fillet] Fillet023
  Base = -> Cut085
  Edges = 1 edges r=4: [Edge16]
FEATURE [Part::Cylinder] Cylinder123  label="Válec123"
  Angle = 360
  AttacherType = Attacher::AttachEngine3D
  Height = 4
  Placement = pos=(10,-10,1) rot=(0,0,1;0rad)
  Radius = 5
FEATURE [Part::Cut] Cut080
  Base = -> Cylinder122
  Tool = -> Cylinder123
FEATURE [Part::Cylinder] Cylinder124  label="Válec124"
  Angle = 360
  AttacherType = Attacher::AttachEngine3D
  Height = 12
  Placement = pos=(1,14,6) rot=(0,0,1;0rad)
  Radius = 1.5
FEATURE [Part::Box] Box109  label="Krychle109"
  AttacherType = Attacher::AttachEngine3D
  Height = 2
  Length = 6
  Placement = pos=(-2,11,4) rot=(0,0,1;0rad)
  Width = 6
FEATURE [Part::Cylinder] Cylinder125  label="Válec125"
  Angle = 360
  AttacherType = Attacher::AttachEngine3D
  Height = 4
  Placement = pos=(1,14,0) rot=(0,0,1;0rad)
  Radius = 1.5
FEATURE [Part::Box] Box110  label="Krychle110"
  AttacherType = Attacher::AttachEngine3D
  Height = 2
  Length = 6
  Placement = pos=(-2,11,4) rot=(0,0,1;0rad)
  Width = 6
FEATURE [Part::Cylinder] Cylinder126  label="Válec126"
  Angle = 360
  AttacherType = Attacher::AttachEngine3D
  Height = 4
  Placement = pos=(1,14,-0.1) rot=(0,0,1;0rad)
  Radius = 1.5
FEATURE [Part::Cylinder] Cylinder127  label="Válec127"
  Angle = 360
  AttacherType = Attacher::AttachEngine3D
  Height = 12
  Placement = pos=(1,14,6) rot=(0,0,1;0rad)
  Radius = 1.5
FEATURE [Part::Cylinder] Cylinder128  label="Válec128"
  Angle = 360
  AttacherType = Attacher::AttachEngine3D
  Height = 4
  Placement = pos=(1,14,0) rot=(0,0,1;0rad)
  Radius = 1.5
FEATURE [Part::Cylinder] Cylinder129  label="Válec129"
  Angle = 360
  AttacherType = Attacher::AttachEngine3D
  Height = 12
  Placement = pos=(1,14,6) rot=(0,0,1;0rad)
  Radius = 1.5
FEATURE [Part::Box] Box111  label="Krychle111"
  AttacherType = Attacher::AttachEngine3D
  Height = 2
  Length = 6
  Placement = pos=(-2,11,4) rot=(0,0,1;0rad)
  Width = 6
FEATURE [Part::Cylinder] Cylinder130  label="Válec130"
  Angle = 360
  AttacherType = Attacher::AttachEngine3D
  Height = 4
  Placement = pos=(1,14,0) rot=(0,0,1;0rad)
  Radius = 1.5
FEATURE [Part::Cylinder] Cylinder131  label="Válec131"
  Angle = 360
  AttacherType = Attacher::AttachEngine3D
  Height = 12
  Placement = pos=(1,14,6) rot=(0,0,1;0rad)
  Radius = 1.5
FEATURE [Part::Box] Box112  label="Krychle112"
  AttacherType = Attacher::AttachEngine3D
  Height = 2
  Length = 6
  Placement = pos=(-2,11,4) rot=(0,0,1;0rad)
  Width = 6
FEATURE [Part::Cylinder] Cylinder132  label="Válec132"
  Angle = 360
  AttacherType = Attacher::AttachEngine3D
  Height = 4
  Placement = pos=(1,14,0) rot=(0,0,1;0rad)
  Radius = 1.5
FEATURE [Part::Cylinder] Cylinder133  label="Válec133"
  Angle = 360
  AttacherType = Attacher::AttachEngine3D
  Height = 5
  Placement = pos=(-20,30,5) rot=(0,0,1;0rad)
  Radius = 16
FEATURE [Part::Cut] Cut088
  Base = -> Box103
  Tool = -> Cylinder133
FEATURE [Part::Fillet] Fillet020
  Base = -> Cut088
  Edges = 1 edges r=20: [Edge2]
FEATURE [Part::Fillet] Fillet024
  Base = -> Fillet020
  Edges = 1 edges r=2: [Edge2]
FEATURE [Part::Box] Box113  label="Krychle113"
  AttacherType = Attacher::AttachEngine3D
  Height = 2
  Length = 6
  Placement = pos=(-2,11,4) rot=(0,0,1;0rad)
  Width = 6
FEATURE [Part::Cylinder] Cylinder134  label="Válec134"
  Angle = 360
  AttacherType = Attacher::AttachEngine3D
  Height = 5
  Placement = pos=(-20,30,5) rot=(0,0,1;0rad)
  Radius = 16
FEATURE [Part::Cut] Cut086
  Base = -> Box101
  Tool = -> Cylinder134
FEATURE [Part::Fillet] Fillet021
  Base = -> Cut086
  Edges = 1 edges r=20: [Edge3]
FEATURE [Part::Compound] Compound053
  Links = -> [Box113,Cylinder124,Cylinder132]
  Placement = pos=(-2.9,-11.9,0) rot=(0,0,-1;0.261799rad)
FEATURE [Part::Cut] Cut078
  Base = -> Fillet019
  Tool = -> Compound053
FEATURE [Part::Compound] Compound054
  Links = -> [Box110,Cylinder127,Cylinder125]
  Placement = pos=(-6.1,31,0) rot=(0,0,-1;0.261799rad)
FEATURE [Part::Cut] Cut081
  Base = -> Fillet021
  Tool = -> Compound054
FEATURE [Part::Compound] Compound057
  Links = -> [Box111,Cylinder129,Cylinder130]
  Placement = pos=(3.5,2,0) rot=(0,0,1;0.349066rad)
FEATURE [Part::Cut] Cut079
  Base = -> Fillet024
  Tool = -> Compound057
FEATURE [Part::Compound] Compound059
  Links = -> [Box109,Cylinder131,Cylinder128]
  Placement = pos=(-2.9,-11.9,0) rot=(0,0,-1;0.261799rad)
FEATURE [Part::Cut] Cut082
  Base = -> Cut079
  Tool = -> Compound059
FEATURE [Part::Cylinder] Cylinder135  label="Válec135"
  Angle = 360
  AttacherType = Attacher::AttachEngine3D
  Height = 12
  Placement = pos=(1,14,6) rot=(0,0,1;0rad)
  Radius = 1.5
FEATURE [Part::Cylinder] Cylinder136  label="Válec136"
  Angle = 360
  AttacherType = Attacher::AttachEngine3D
  Height = 4
  Placement = pos=(1,14,-0.1) rot=(0,0,1;0rad)
  Radius = 1.5
FEATURE [Part::Cylinder] Cylinder137  label="Válec137"
  Angle = 360
  AttacherType = Attacher::AttachEngine3D
  Height = 4
  Placement = pos=(1,14,-0.1) rot=(0,0,1;0rad)
  Radius = 1.5
FEATURE [Part::Cylinder] Cylinder138  label="Válec138"
  Angle = 360
  AttacherType = Attacher::AttachEngine3D
  Height = 12
  Placement = pos=(1,14,6) rot=(0,0,1;0rad)
  Radius = 1.5
FEATURE [Part::Box] Box114  label="Krychle114"
  AttacherType = Attacher::AttachEngine3D
  Height = 2
  Length = 6
  Placement = pos=(-2,11,4) rot=(0,0,1;0rad)
  Width = 6
FEATURE [Part::Cylinder] Cylinder139  label="Válec139"
  Angle = 360
  AttacherType = Attacher::AttachEngine3D
  Height = 12
  Placement = pos=(1,14,6) rot=(0,0,1;0rad)
  Radius = 1.5
FEATURE [Part::Compound] Compound058
  Links = -> [Box112,Cylinder139,Cylinder126]
  Placement = pos=(12.1,54,0) rot=(0,0,1;0.785398rad)
FEATURE [Part::Cut] Cut087
  Base = -> Cut084
  Tool = -> Compound058
FEATURE [Part::Cylinder] Cylinder140  label="Válec140"
  Angle = 360
  AttacherType = Attacher::AttachEngine3D
  Height = 12
  Placement = pos=(1,14,6) rot=(0,0,1;0rad)
  Radius = 1.5
FEATURE [Part::Box] Box115  label="Krychle115"
  AttacherType = Attacher::AttachEngine3D
  Height = 2
  Length = 6
  Placement = pos=(-2,11,4) rot=(0,0,1;0rad)
  Width = 6
FEATURE [Part::Compound] Compound060
  Links = -> [Box115,Cylinder135,Cylinder137]
  Placement = pos=(6,53,2) rot=(0,1,0;1.5708rad)
FEATURE [Part::Cylinder] Cylinder141  label="Válec141"
  Angle = 360
  AttacherType = Attacher::AttachEngine3D
  Height = 4
  Placement = pos=(1,14,-0.1) rot=(0,0,1;0rad)
  Radius = 1.5
FEATURE [Part::Compound] Compound055
  Links = -> [Box114,Cylinder140,Cylinder141]
  Placement = pos=(12.1,54,0) rot=(0,0,1;0.785398rad)
FEATURE [Part::Box] Box116  label="Krychle116"
  AttacherType = Attacher::AttachEngine3D
  Height = 2
  Length = 6
  Placement = pos=(-2,11,4) rot=(0,0,1;0rad)
  Width = 6
FEATURE [Part::Compound] Compound056
  Links = -> [Box116,Cylinder138,Cylinder136]
  Placement = pos=(6,53,2) rot=(0,1,0;1.5708rad)
FEATURE [Part::Cut] Cut090
  Base = -> Cut087
  Tool = -> Compound060
FEATURE [Part::Cut] Cut093
  Base = -> Box105
  Tool = -> Compound055
FEATURE [Part::Cut] Cut089
  Base = -> Cut093
  Tool = -> Compound056
FEATURE [Part::Cylinder] Cylinder142  label="Válec142"
  Angle = 360
  AttacherType = Attacher::AttachEngine3D
  Height = 4
  Placement = pos=(1,14,-0.1) rot=(0,0,1;0rad)
  Radius = 1.5
FEATURE [Part::Cylinder] Cylinder143  label="Válec143"
  Angle = 360
  AttacherType = Attacher::AttachEngine3D
  Height = 12
  Placement = pos=(1,14,6) rot=(0,0,1;0rad)
  Radius = 1.5
FEATURE [Part::Cylinder] Cylinder144  label="Válec144"
  Angle = 360
  AttacherType = Attacher::AttachEngine3D
  Height = 12
  Placement = pos=(1,14,6) rot=(0,0,1;0rad)
  Radius = 1.5
FEATURE [Part::Box] Box117  label="Krychle117"
  AttacherType = Attacher::AttachEngine3D
  Height = 2
  Length = 6
  Placement = pos=(-2,11,4) rot=(0,0,1;0rad)
  Width = 6
FEATURE [Part::Box] Box118  label="Krychle118"
  AttacherType = Attacher::AttachEngine3D
  Height = 2
  Length = 6
  Placement = pos=(-2,11,4) rot=(0,0,1;0rad)
  Width = 6
FEATURE [Part::Cylinder] Cylinder145  label="Válec145"
  Angle = 360
  AttacherType = Attacher::AttachEngine3D
  Height = 4
  Placement = pos=(1,14,-0.1) rot=(0,0,1;0rad)
  Radius = 1.5
FEATURE [Part::Compound] Compound062
  Links = -> [Box118,Cylinder144,Cylinder142]
  Placement = pos=(6,-14,2) rot=(0,1,0;1.5708rad)
FEATURE [Part::Cut] Cut091
  Base = -> Fillet023
  Tool = -> Compound062
FEATURE [Part::Compound] Compound063
  Links = -> [Box117,Cylinder143,Cylinder145]
  Placement = pos=(6,-14,2) rot=(0,1,0;1.5708rad)
FEATURE [Part::Cut] Cut092
  Base = -> Cut078
  Tool = -> Compound063
FEATURE [Part::Compound] Compound061  label="revised_finger_lower001"
  Links = -> [Cut092,Cut091,Cut090,Cut089,Cut082,Cut081,Cut080,Cut083]
FEATURE [Part::Mirroring] mirror003  label="revised_finger_lower_opposite"
  Base = (0,0,0)
  Normal = (1,0,0)
  Source = -> Compound061
FEATURE [Part::Box] Box119  label="Krychle119"
  AttacherType = Attacher::AttachEngine3D
  Height = 12
  Length = 12
  Placement = pos=(-13,24,-2) rot=(0,0,1;0rad)
  Width = 12
FEATURE [Part::Cylinder] Cylinder146  label="Válec146"
  Angle = 360
  AttacherType = Attacher::AttachEngine3D
  Height = 4
  Placement = pos=(-10,30,1) rot=(0,0,1;0rad)
  Radius = 5
FEATURE [Part::Cylinder] Cylinder147  label="Válec147"
  Angle = 360
  AttacherType = Attacher::AttachEngine3D
  Height = 5
  Placement = pos=(-20,30,5) rot=(0,0,1;0rad)
  Radius = 16
FEATURE [Part::Compound] Compound067
  Links = -> [Cylinder146,Cylinder147]
FEATURE [Part::Cylinder] Cylinder148  label="Válec148"
  Angle = 360
  AttacherType = Attacher::AttachEngine3D
  Height = 16
  Placement = pos=(1,14,1) rot=(0,0,1;0rad)
  Radius = 1.5
FEATURE [Part::Cylinder] Cylinder149  label="Válec149"
  Angle = 360
  AttacherType = Attacher::AttachEngine3D
  Height = 5
  Placement = pos=(-20,30,5) rot=(0,0,1;0rad)
  Radius = 16
FEATURE [Part::Box] Box120  label="Krychle120"
  AttacherType = Attacher::AttachEngine3D
  Height = 12
  Length = 12
  Placement = pos=(-6.8,59.2,-2) rot=(0,0,-1;0.785398rad)
  Width = 16
FEATURE [Part::Cut] Cut109
  Base = -> Box119
  Tool = -> Compound067
FEATURE [Part::Cylinder] Cylinder150  label="Válec150"
  Angle = 360
  AttacherType = Attacher::AttachEngine3D
  Height = 4
  Placement = pos=(10,-10,1) rot=(0,0,1;0rad)
  Radius = 5
FEATURE [Part::Box] Box121  label="Krychle121"
  AttacherType = Attacher::AttachEngine3D
  Height = 7
  Length = 12
  Placement = pos=(4,-10,-2) rot=(0,0,1;0rad)
  Width = 18
FEATURE [Part::Cut] Cut098
  Base = -> Box121
  Tool = -> Cylinder150
FEATURE [Part::Fillet] Fillet025
  Base = -> Cut098
  Edges = 1 edges r=4: [Edge16]
FEATURE [Part::Box] Box122  label="Krychle122"
  AttacherType = Attacher::AttachEngine3D
  Height = 12
  Length = 12
  Placement = pos=(4.5,70.5,-2) rot=(0,0,-1;1.309rad)
  Width = 12
FEATURE [Part::Cylinder] Cylinder151  label="Válec151"
  Angle = 360
  AttacherType = Attacher::AttachEngine3D
  Height = 3
  Placement = pos=(1,14,-2) rot=(0,0,1;0rad)
  Radius = 3
FEATURE [Part::Cylinder] Cylinder152  label="Válec152"
  Angle = 360
  AttacherType = Attacher::AttachEngine3D
  Height = 3
  Placement = pos=(1,14,-2) rot=(0,0,1;0rad)
  Radius = 3
FEATURE [Part::Cylinder] Cylinder153  label="Válec153"
  Angle = 360
  AttacherType = Attacher::AttachEngine3D
  Height = 7
  Placement = pos=(10,-10,-2) rot=(0,0,1;0rad)
  Radius = 7
FEATURE [Part::Box] Box123  label="Krychle123"
  AttacherType = Attacher::AttachEngine3D
  Height = 2
  Length = 6
  Placement = pos=(-2,11,20) rot=(0,0,1;0rad)
  Width = 6
FEATURE [Part::Box] Box124  label="Krychle124"
  AttacherType = Attacher::AttachEngine3D
  Height = 12
  Length = 12
  Placement = pos=(16,0,-2) rot=(0,0,1;0rad)
  Width = 80
FEATURE [Part::Cut] Cut108
  Base = -> Box122
  Tool = -> Box124
FEATURE [Part::Box] Box125  label="Krychle125"
  AttacherType = Attacher::AttachEngine3D
  Height = 2
  Length = 6
  Placement = pos=(-2,11,20) rot=(0,0,1;0rad)
  Width = 6
FEATURE [Part::Cylinder] Cylinder154  label="Válec154"
  Angle = 360
  AttacherType = Attacher::AttachEngine3D
  Height = 5
  Placement = pos=(-20,30,5) rot=(0,0,1;0rad)
  Radius = 16
FEATURE [Part::Box] Box126  label="Krychle126"
  AttacherType = Attacher::AttachEngine3D
  Height = 12
  Length = 12
  Placement = pos=(-13,36,-2) rot=(0,0,-1;0.261799rad)
  Width = 24
FEATURE [Part::Cut] Cut105
  Base = -> Box126
  Tool = -> Cylinder149
FEATURE [Part::Fillet] Fillet030
  Base = -> Cut105
  Edges = 1 edges r=20: [Edge3]
FEATURE [Part::Cylinder] Cylinder155  label="Válec155"
  Angle = 360
  AttacherType = Attacher::AttachEngine3D
  Height = 4
  Placement = pos=(10,-10,1) rot=(0,0,1;0rad)
  Radius = 5
FEATURE [Part::Cut] Cut107
  Base = -> Cylinder153
  Tool = -> Cylinder155
FEATURE [Part::Box] Box127  label="Krychle127"
  AttacherType = Attacher::AttachEngine3D
  Height = 12
  Length = 12
  Placement = pos=(11.4,-4.4,-2) rot=(0,0,1;1.309rad)
  Width = 18
FEATURE [Part::Chamfer] Chamfer009
  Base = -> Box127
  Edges = 2 edges r=4: [Edge1,Edge5]
FEATURE [Part::Fillet] Fillet028
  Base = -> Chamfer009
  Edges = 1 edges r=4: [Edge4]
FEATURE [Part::Fillet] Fillet027
  Base = -> Fillet028
  Edges = 1 edges r=3: [Edge2]
FEATURE [Part::Fillet] Fillet026
  Base = -> Fillet027
  Edges = 2 edges r=3: [Edge21,Edge23]
FEATURE [Part::Fillet] Fillet031
  Base = -> Fillet026
  Edges = 1 edges r=4: [Edge27]
FEATURE [Part::Cylinder] Cylinder156  label="Válec156"
  Angle = 360
  AttacherType = Attacher::AttachEngine3D
  Height = 3
  Placement = pos=(1,14,-2) rot=(0,0,1;0rad)
  Radius = 3
FEATURE [Part::Box] Box128  label="Krychle128"
  AttacherType = Attacher::AttachEngine3D
  Height = 2
  Length = 6
  Placement = pos=(-2,11,20) rot=(0,0,1;0rad)
  Width = 6
FEATURE [Part::Box] Box129  label="Krychle129"
  AttacherType = Attacher::AttachEngine3D
  Height = 12
  Length = 12
  Placement = pos=(-4.1,-0.4,-2) rot=(0,0,1;0.349066rad)
  Width = 26
FEATURE [Part::Cut] Cut094
  Base = -> Box129
  Tool = -> Cylinder154
FEATURE [Part::Fillet] Fillet032
  Base = -> Cut094
  Edges = 1 edges r=20: [Edge2]
FEATURE [Part::Fillet] Fillet029
  Base = -> Fillet032
  Edges = 1 edges r=2: [Edge2]
FEATURE [Part::Cylinder] Cylinder157  label="Válec157"
  Angle = 360
  AttacherType = Attacher::AttachEngine3D
  Height = 16
  Placement = pos=(1,14,1) rot=(0,0,1;0rad)
  Radius = 1.5
FEATURE [Part::Compound] Compound068
  Links = -> [Box123,Cylinder157,Cylinder151]
  Placement = pos=(12.1,54,0) rot=(0,0,1;0.785398rad)
FEATURE [Part::Cut] Cut100
  Base = -> Cut108
  Tool = -> Compound068
FEATURE [Part::Cylinder] Cylinder158  label="Válec158"
  Angle = 360
  AttacherType = Attacher::AttachEngine3D
  Height = 4
  Placement = pos=(1,14,-0.1) rot=(0,0,1;0rad)
  Radius = 1.5
FEATURE [Part::Cylinder] Cylinder159  label="Válec159"
  Angle = 360
  AttacherType = Attacher::AttachEngine3D
  Height = 3
  Placement = pos=(1,14,-2) rot=(0,0,1;0rad)
  Radius = 3
FEATURE [Part::Box] Box130  label="Krychle130"
  AttacherType = Attacher::AttachEngine3D
  Height = 2
  Length = 6
  Placement = pos=(-2,11,20) rot=(0,0,1;0rad)
  Width = 6
FEATURE [Part::Cylinder] Cylinder160  label="Válec160"
  Angle = 360
  AttacherType = Attacher::AttachEngine3D
  Height = 16
  Placement = pos=(1,14,1) rot=(0,0,1;0rad)
  Radius = 1.5
FEATURE [Part::Cylinder] Cylinder161  label="Válec161"
  Angle = 360
  AttacherType = Attacher::AttachEngine3D
  Height = 12
  Placement = pos=(1,14,6) rot=(0,0,1;0rad)
  Radius = 1.5
FEATURE [Part::Box] Box131  label="Krychle131"
  AttacherType = Attacher::AttachEngine3D
  Height = 2
  Length = 6
  Placement = pos=(-2,11,20) rot=(0,0,1;0rad)
  Width = 6
FEATURE [Part::Cylinder] Cylinder162  label="Válec162"
  Angle = 360
  AttacherType = Attacher::AttachEngine3D
  Height = 16
  Placement = pos=(1,14,1) rot=(0,0,1;0rad)
  Radius = 1.5
FEATURE [Part::Compound] Compound066
  Links = -> [Box131,Cylinder162,Cylinder159]
  Placement = pos=(-2.9,-11.9,0) rot=(0,0,-1;0.261799rad)
FEATURE [Part::Cylinder] Cylinder163  label="Válec163"
  Angle = 360
  AttacherType = Attacher::AttachEngine3D
  Height = 3
  Placement = pos=(1,14,-2) rot=(0,0,1;0rad)
  Radius = 3
FEATURE [Part::Compound] Compound070
  Links = -> [Box125,Cylinder148,Cylinder163]
  Placement = pos=(12.1,54,0) rot=(0,0,1;0.785398rad)
FEATURE [Part::Cut] Cut102
  Base = -> Box120
  Tool = -> Compound070
FEATURE [Part::Cylinder] Cylinder164  label="Válec164"
  Angle = 360
  AttacherType = Attacher::AttachEngine3D
  Height = 16
  Placement = pos=(1,14,1) rot=(0,0,1;0rad)
  Radius = 1.5
FEATURE [Part::Compound] Compound065
  Links = -> [Box128,Cylinder164,Cylinder152]
  Placement = pos=(-6.1,31,0) rot=(0,0,-1;0.261799rad)
FEATURE [Part::Cut] Cut095
  Base = -> Fillet030
  Tool = -> Compound065
FEATURE [Part::Box] Box132  label="Krychle132"
  AttacherType = Attacher::AttachEngine3D
  Height = 2
  Length = 6
  Placement = pos=(-2,11,20) rot=(0,0,1;0rad)
  Width = 6
FEATURE [Part::Compound] Compound064
  Links = -> [Box132,Cylinder160,Cylinder156]
  Placement = pos=(3.5,2,0) rot=(0,0,1;0.349066rad)
FEATURE [Part::Cut] Cut096
  Base = -> Fillet029
  Tool = -> Compound064
FEATURE [Part::Cut] Cut099
  Base = -> Cut096
  Tool = -> Compound066
FEATURE [Part::Box] Box133  label="Krychle133"
  AttacherType = Attacher::AttachEngine3D
  Height = 2
  Length = 6
  Placement = pos=(-2,11,4) rot=(0,0,1;0rad)
  Width = 6
FEATURE [Part::Box] Box134  label="Krychle134"
  AttacherType = Attacher::AttachEngine3D
  Height = 2
  Length = 6
  Placement = pos=(-2,11,4) rot=(0,0,1;0rad)
  Width = 6
FEATURE [Part::Cylinder] Cylinder165  label="Válec165"
  Angle = 360
  AttacherType = Attacher::AttachEngine3D
  Height = 4
  Placement = pos=(1,14,0) rot=(0,0,1;0rad)
  Radius = 1.5
FEATURE [Part::Cylinder] Cylinder166  label="Válec166"
  Angle = 360
  AttacherType = Attacher::AttachEngine3D
  Height = 3
  Placement = pos=(1,14,-2) rot=(0,0,1;0rad)
  Radius = 3
FEATURE [Part::Cylinder] Cylinder167  label="Válec167"
  Angle = 360
  AttacherType = Attacher::AttachEngine3D
  Height = 16
  Placement = pos=(1,14,1) rot=(0,0,1;0rad)
  Radius = 1.5
FEATURE [Part::Compound] Compound069
  Links = -> [Box130,Cylinder167,Cylinder166]
  Placement = pos=(-2.9,-11.9,0) rot=(0,0,-1;0.261799rad)
FEATURE [Part::Cut] Cut097
  Base = -> Fillet031
  Tool = -> Compound069
FEATURE [Part::Box] Box135  label="Krychle135"
  AttacherType = Attacher::AttachEngine3D
  Height = 2
  Length = 6
  Placement = pos=(-2,11,4) rot=(0,0,1;0rad)
  Width = 6
FEATURE [Part::Cylinder] Cylinder168  label="Válec168"
  Angle = 360
  AttacherType = Attacher::AttachEngine3D
  Height = 12
  Placement = pos=(1,14,6) rot=(0,0,1;0rad)
  Radius = 1.5
FEATURE [Part::Cylinder] Cylinder169  label="Válec169"
  Angle = 360
  AttacherType = Attacher::AttachEngine3D
  Height = 12
  Placement = pos=(1,14,6) rot=(0,0,1;0rad)
  Radius = 1.5
FEATURE [Part::Cylinder] Cylinder170  label="Válec170"
  Angle = 360
  AttacherType = Attacher::AttachEngine3D
  Height = 12
  Placement = pos=(1,14,6) rot=(0,0,1;0rad)
  Radius = 1.5
FEATURE [Part::Cylinder] Cylinder171  label="Válec171"
  Angle = 360
  AttacherType = Attacher::AttachEngine3D
  Height = 4
  Placement = pos=(1,14,-0.1) rot=(0,0,1;0rad)
  Radius = 1.5
FEATURE [Part::Box] Box136  label="Krychle136"
  AttacherType = Attacher::AttachEngine3D
  Height = 2
  Length = 6
  Placement = pos=(-2,11,4) rot=(0,0,1;0rad)
  Width = 6
FEATURE [Part::Cylinder] Cylinder172  label="Válec172"
  Angle = 360
  AttacherType = Attacher::AttachEngine3D
  Height = 4
  Placement = pos=(1,14,-0.1) rot=(0,0,1;0rad)
  Radius = 1.5
FEATURE [Part::Compound] Compound072
  Links = -> [Box134,Cylinder169,Cylinder158]
  Placement = pos=(6,53,2) rot=(0,1,0;1.5708rad)
FEATURE [Part::Cut] Cut101
  Base = -> Cut100
  Tool = -> Compound072
FEATURE [Part::Compound] Compound073
  Links = -> [Box133,Cylinder161,Cylinder165]
  Placement = pos=(6,53,2) rot=(0,1,0;1.5708rad)
FEATURE [Part::Cut] Cut104
  Base = -> Cut102
  Tool = -> Compound073
FEATURE [Part::Compound] Compound074
  Links = -> [Box136,Cylinder168,Cylinder172]
  Placement = pos=(6,-14,2) rot=(0,1,0;1.5708rad)
FEATURE [Part::Cut] Cut106
  Base = -> Cut097
  Tool = -> Compound074
FEATURE [Part::Compound] Compound075
  Links = -> [Box135,Cylinder170,Cylinder171]
  Placement = pos=(6,-14,2) rot=(0,1,0;1.5708rad)
FEATURE [Part::Cut] Cut103
  Base = -> Fillet025
  Tool = -> Compound075
FEATURE [Part::Compound] Compound071  label="revised_finger_upper001"
  Links = -> [Cut107,Cut109,Cut095,Cut099,Cut104,Cut101,Cut103,Cut106]
FEATURE [Part::Mirroring] mirror004  label="revised_finger_upper_opposite"
  Base = (0,0,0)
  Normal = (1,0,0)
  Source = -> Compound071
FEATURE [Mesh::Feature] Mesh002  label="revised_finger_lower_opposite (Meshed)"
FEATURE [Mesh::Feature] Mesh003  label="revised_finger_upper_opposite (Meshed)"
FEATURE [Mesh::Feature] Mesh  label="revised_finger_upper (Meshed)"
FEATURE [Mesh::Feature] Mesh004  label="revised_finger_lower (Meshed)"
FEATURE [Part::Box] Box137  label="Krychle137"
  AttacherType = Attacher::AttachEngine3D
  Height = 8
  Length = 5
  Placement = pos=(-18,-33,6) rot=(0,0,1;0rad)
  Width = 63
FEATURE [Part::Cylinder] Cylinder173  label="Válec173"
  Angle = 360
  AttacherType = Attacher::AttachEngine3D
  Height = 8
  Placement = pos=(-10,30,6) rot=(0,0,1;0rad)
  Radius = 5
FEATURE [Part::Cylinder] Cylinder174  label="Válec174"
  Angle = 360
  AttacherType = Attacher::AttachEngine3D
  Height = 12
  Placement = pos=(-13,30,4) rot=(0,0,1;0rad)
  Radius = 2.65
FEATURE [Part::Cylinder] Cylinder175  label="Válec175"
  Angle = 360
  AttacherType = Attacher::AttachEngine3D
  Height = 8
  Placement = pos=(-13,-25,6) rot=(0,0,1;0rad)
  Radius = 5
FEATURE [Part::Cylinder] Cylinder176  label="Válec176"
  Angle = 360
  AttacherType = Attacher::AttachEngine3D
  Height = 12
  Placement = pos=(-13,-33,4) rot=(0,0,1;0rad)
  Radius = 2.65
FEATURE [Part::Cylinder] Cylinder177  label="Válec177"
  Angle = 360
  AttacherType = Attacher::AttachEngine3D
  Height = 12
  Placement = pos=(-13,-25,4) rot=(0,0,1;0rad)
  Radius = 2.65
FEATURE [Part::Cylinder] Cylinder178  label="Válec178"
  Angle = 360
  AttacherType = Attacher::AttachEngine3D
  Height = 12
  Placement = pos=(-10,30,4) rot=(0,0,1;0rad)
  Radius = 2.65
FEATURE [Part::Cut] Cut110
  Base = -> Box137
  Tool = -> Cylinder174
FEATURE [Part::Cut] Cut111
  Base = -> Cylinder173
  Placement = pos=(-3,0,0) rot=(0,0,1;0rad)
  Tool = -> Cylinder178
FEATURE [Part::Cut] Cut112
  Base = -> Cylinder175
  Placement = pos=(0,-8,0) rot=(0,0,1;0rad)
  Tool = -> Cylinder177
FEATURE [Part::Cut] Cut113
  Base = -> Cut110
  Tool = -> Cylinder176
FEATURE [Part::Compound] Compound076  label="tahlo_lefto1"
  Links = -> [Cut111,Cut112]
FEATURE [Part::Cylinder] Cylinder180  label="Válec180"
  Angle = 360
  AttacherType = Attacher::AttachEngine3D
  Height = 4
  Placement = pos=(-13,-25,1) rot=(0,0,1;0rad)
  Radius = 5
FEATURE [Part::Cylinder] Cylinder181  label="Válec181"
  Angle = 360
  AttacherType = Attacher::AttachEngine3D
  Height = 4
  Placement = pos=(-29,-25.5,15) rot=(0,0,1;0rad)
  Radius = 5
FEATURE [Part::Cylinder] Cylinder182  label="Válec182"
  Angle = 360
  AttacherType = Attacher::AttachEngine3D
  Height = 5
  Placement = pos=(-29,-25.5,15) rot=(0,0,1;0rad)
  Radius = 8.5
FEATURE [Part::Cylinder] Cylinder183  label="Válec183"
  Angle = 360
  AttacherType = Attacher::AttachEngine3D
  Height = 5
  Placement = pos=(-13,-25,0) rot=(0,0,1;0rad)
  Radius = 7
FEATURE [Part::Box] Box138  label="Krychle138"
  AttacherType = Attacher::AttachEngine3D
  Height = 5
  Length = 92
  Placement = pos=(-29,-34,15) rot=(0,0,1;0rad)
  Width = 17
FEATURE [Part::Cylinder] Cylinder184  label="Válec184"
  Angle = 360
  AttacherType = Attacher::AttachEngine3D
  Height = 5
  Placement = pos=(63,-25.5,15) rot=(0,0,1;0rad)
  Radius = 8.5
FEATURE [Part::Box] Box139  label="Krychle139"
  AttacherType = Attacher::AttachEngine3D
  Height = 5
  Length = 72
  Placement = pos=(-19,-34,10) rot=(0,0,1;0rad)
  Width = 17
FEATURE [Part::Cylinder] Cylinder185  label="Válec185"
  Angle = 360
  AttacherType = Attacher::AttachEngine3D
  Height = 20
  Placement = pos=(-13,-17,10) rot=(1,0,0;1.5708rad)
  Radius = 5
FEATURE [Part::Cylinder] Cylinder186  label="Válec186"
  Angle = 360
  AttacherType = Attacher::AttachEngine3D
  Height = 20
  Placement = pos=(47,-17,10) rot=(1,0,0;1.5708rad)
  Radius = 5
FEATURE [Part::Compound] Compound077
  Links = -> [Cylinder185,Cylinder186]
FEATURE [Part::Cylinder] Cylinder187  label="Válec187"
  Angle = 360
  AttacherType = Attacher::AttachEngine3D
  Height = 17
  Placement = pos=(-13,-17,10) rot=(1,0,0;1.5708rad)
  Radius = 7
FEATURE [Part::Cylinder] Cylinder188  label="Válec188"
  Angle = 360
  AttacherType = Attacher::AttachEngine3D
  Height = 17
  Placement = pos=(47,-17,10) rot=(1,0,0;1.5708rad)
  Radius = 7
FEATURE [Part::Cylinder] Cylinder189  label="Válec189"
  Angle = 360
  AttacherType = Attacher::AttachEngine3D
  Height = 4
  Placement = pos=(63,-25.5,15) rot=(0,0,1;0rad)
  Radius = 5
FEATURE [Part::Cut] Cut114
  Base = -> Cylinder182
  Tool = -> Cylinder181
FEATURE [Part::Cut] Cut115
  Base = -> Cylinder184
  Tool = -> Cylinder189
FEATURE [Part::Cylinder] Cylinder190  label="Válec190"
  Angle = 360
  AttacherType = Attacher::AttachEngine3D
  Height = 4
  Placement = pos=(-29,-25.5,15) rot=(0,0,1;0rad)
  Radius = 5
FEATURE [Part::Cylinder] Cylinder191  label="Válec191"
  Angle = 360
  AttacherType = Attacher::AttachEngine3D
  Height = 4
  Placement = pos=(63,-25.5,15) rot=(0,0,1;0rad)
  Radius = 5
FEATURE [Part::Cut] Cut116
  Base = -> Box138
  Tool = -> Cylinder190
FEATURE [Part::Cut] Cut117
  Base = -> Cut116
  Tool = -> Cylinder191
FEATURE [Part::Cylinder] Cylinder192  label="Válec192"
  Angle = 360
  AttacherType = Attacher::AttachEngine3D
  Height = 20
  Placement = pos=(-13,-17,10) rot=(1,0,0;1.5708rad)
  Radius = 5
FEATURE [Part::Cylinder] Cylinder193  label="Válec193"
  Angle = 360
  AttacherType = Attacher::AttachEngine3D
  Height = 20
  Placement = pos=(47,-17,10) rot=(1,0,0;1.5708rad)
  Radius = 5
FEATURE [Part::Compound] Compound078
  Links = -> [Cylinder187,Cylinder188]
FEATURE [Part::Cut] Cut118
  Base = -> Compound078
  Tool = -> Compound077
FEATURE [Part::Compound] Compound079
  Links = -> [Cylinder192,Cylinder193]
FEATURE [Part::Cut] Cut119
  Base = -> Box139
  Tool = -> Compound079
FEATURE [Part::Box] Box140  label="Krychle140"
  AttacherType = Attacher::AttachEngine3D
  Height = 10
  Length = 80
  Placement = pos=(-20,-36,0) rot=(0,0,1;0rad)
  Width = 20
FEATURE [Part::Cut] Cut120
  Base = -> Cut118
  Tool = -> Box140
FEATURE [Part::Box] Box141  label="Krychle141"
  AttacherType = Attacher::AttachEngine3D
  Height = 5
  Length = 4
  Placement = pos=(-20,-34,10) rot=(0,0,1;0rad)
  Width = 17
FEATURE [Part::Box] Box142  label="Krychle142"
  AttacherType = Attacher::AttachEngine3D
  Height = 5
  Length = 4
  Placement = pos=(50,-34,10) rot=(0,0,1;0rad)
  Width = 17
FEATURE [Part::Compound] Compound080
  Links = -> [Box141,Box142]
FEATURE [Part::Cylinder] Cylinder194  label="Válec194"
  Angle = 360
  AttacherType = Attacher::AttachEngine3D
  Height = 20
  Placement = pos=(47,-17,10) rot=(1,0,0;1.5708rad)
  Radius = 5
FEATURE [Part::Cylinder] Cylinder195  label="Válec195"
  Angle = 360
  AttacherType = Attacher::AttachEngine3D
  Height = 20
  Placement = pos=(-13,-17,10) rot=(1,0,0;1.5708rad)
  Radius = 5
FEATURE [Part::Compound] Compound081
  Links = -> [Cylinder195,Cylinder194]
FEATURE [Part::Cut] Cut121
  Base = -> Compound080
  Tool = -> Compound081
FEATURE [Part::Cylinder] Cylinder196  label="Válec196"
  Angle = 360
  AttacherType = Attacher::AttachEngine3D
  Height = 15
  Placement = pos=(1,-18,10) rot=(1,0,0;1.5708rad)
  Radius = 5
FEATURE [Part::FeaturePython] Tube  # WARN: FeaturePython — macro-defined, semantics opaque (R4)
  AttacherType = Attacher::AttachEngine3D
  Height = 1
  InnerRadius = 3
  OuterRadius = 5
  Placement = pos=(-13,-17,10) rot=(1,0,0;1.5708rad)
FEATURE [Part::FeaturePython] Tube001  # WARN: FeaturePython — macro-defined, semantics opaque (R4)
  AttacherType = Attacher::AttachEngine3D
  Height = 1
  InnerRadius = 3
  OuterRadius = 5
  Placement = pos=(-13,-33,10) rot=(1,0,0;1.5708rad)
FEATURE [Part::FeaturePython] Tube002  # WARN: FeaturePython — macro-defined, semantics opaque (R4)
  AttacherType = Attacher::AttachEngine3D
  Height = 1
  InnerRadius = 3
  OuterRadius = 5
  Placement = pos=(47,-17,10) rot=(1,0,0;1.5708rad)
FEATURE [Part::FeaturePython] Tube003  # WARN: FeaturePython — macro-defined, semantics opaque (R4)
  AttacherType = Attacher::AttachEngine3D
  Height = 1
  InnerRadius = 3
  OuterRadius = 5
  Placement = pos=(47,-33,10) rot=(1,0,0;1.5708rad)
FEATURE [Part::Cylinder] Cylinder197  label="Válec197"
  Angle = 360
  AttacherType = Attacher::AttachEngine3D
  Height = 15
  Placement = pos=(-13,-18,10) rot=(1,0,0;1.5708rad)
  Radius = 5
FEATURE [Part::Box] Box143  label="Krychle143"
  AttacherType = Attacher::AttachEngine3D
  Height = 10
  Length = 80
  Placement = pos=(-20,-36,0) rot=(0,0,1;0rad)
  Width = 20
FEATURE [Part::Compound] Compound082
  Links = -> [Tube,Tube001,Tube002,Tube003]
FEATURE [Part::Cut] Cut122
  Base = -> Compound082
  Tool = -> Box143
FEATURE [Part::Box] Box144  label="Krychle144"
  AttacherType = Attacher::AttachEngine3D
  Height = 2
  Length = 6
  Placement = pos=(-6,-34,13) rot=(0,0,1;0rad)
  Width = 6
FEATURE [Part::Box] Box145  label="Krychle145"
  AttacherType = Attacher::AttachEngine3D
  Height = 2
  Length = 6
  Placement = pos=(-6,-23,13) rot=(0,0,1;0rad)
  Width = 6
FEATURE [Part::Box] Box146  label="Krychle146"
  AttacherType = Attacher::AttachEngine3D
  Height = 2
  Length = 6
  Placement = pos=(34,-34,13) rot=(0,0,1;0rad)
  Width = 6
FEATURE [Part::Box] Box147  label="Krychle147"
  AttacherType = Attacher::AttachEngine3D
  Height = 2
  Length = 6
  Placement = pos=(34,-23,13) rot=(0,0,1;0rad)
  Width = 6
FEATURE [Part::Cylinder] Cylinder198  label="Válec198"
  Angle = 360
  AttacherType = Attacher::AttachEngine3D
  Height = 10
  Placement = pos=(-3,-20,9) rot=(0,0,1;0rad)
  Radius = 1.5
FEATURE [Part::Cylinder] Cylinder199  label="Válec199"
  Angle = 360
  AttacherType = Attacher::AttachEngine3D
  Height = 10
  Placement = pos=(-3,-31,9) rot=(0,0,1;0rad)
  Radius = 1.5
FEATURE [Part::Cylinder] Cylinder200  label="Válec200"
  Angle = 360
  AttacherType = Attacher::AttachEngine3D
  Height = 10
  Placement = pos=(37,-20,9) rot=(0,0,1;0rad)
  Radius = 1.5
FEATURE [Part::Cylinder] Cylinder201  label="Válec201"
  Angle = 360
  AttacherType = Attacher::AttachEngine3D
  Height = 10
  Placement = pos=(37,-31,9) rot=(0,0,1;0rad)
  Radius = 1.5
FEATURE [Part::Compound] Compound083
  Links = -> [Cylinder198,Cylinder199,Cylinder200,Cylinder201]
FEATURE [Part::Compound] Compound084
  Links = -> [Box144,Box145,Box146,Box147]
FEATURE [Part::Box] Box148  label="Krychle148"
  AttacherType = Attacher::AttachEngine3D
  Height = 2
  Length = 6
  Placement = pos=(34,-34,13) rot=(0,0,1;0rad)
  Width = 6
FEATURE [Part::Box] Box149  label="Krychle149"
  AttacherType = Attacher::AttachEngine3D
  Height = 2
  Length = 6
  Placement = pos=(-6,-23,13) rot=(0,0,1;0rad)
  Width = 6
FEATURE [Part::Box] Box150  label="Krychle150"
  AttacherType = Attacher::AttachEngine3D
  Height = 2
  Length = 6
  Placement = pos=(-6,-34,13) rot=(0,0,1;0rad)
  Width = 6
FEATURE [Part::Box] Box151  label="Krychle151"
  AttacherType = Attacher::AttachEngine3D
  Height = 2
  Length = 6
  Placement = pos=(34,-23,13) rot=(0,0,1;0rad)
  Width = 6
FEATURE [Part::Compound] Compound085
  Links = -> [Box150,Box149,Box148,Box151]
FEATURE [Part::Cylinder] Cylinder202  label="Válec202"
  Angle = 360
  AttacherType = Attacher::AttachEngine3D
  Height = 10
  Placement = pos=(-3,-31,9) rot=(0,0,1;0rad)
  Radius = 1.5
FEATURE [Part::Cylinder] Cylinder203  label="Válec203"
  Angle = 360
  AttacherType = Attacher::AttachEngine3D
  Height = 10
  Placement = pos=(-3,-20,9) rot=(0,0,1;0rad)
  Radius = 1.5
FEATURE [Part::Cylinder] Cylinder204  label="Válec204"
  Angle = 360
  AttacherType = Attacher::AttachEngine3D
  Height = 10
  Placement = pos=(37,-20,9) rot=(0,0,1;0rad)
  Radius = 1.5
FEATURE [Part::Cylinder] Cylinder205  label="Válec205"
  Angle = 360
  AttacherType = Attacher::AttachEngine3D
  Height = 10
  Placement = pos=(37,-31,9) rot=(0,0,1;0rad)
  Radius = 1.5
FEATURE [Part::Compound] Compound086
  Links = -> [Cylinder203,Cylinder202,Cylinder204,Cylinder205]
FEATURE [Part::Cut] Cut123
  Base = -> Cut119
  Tool = -> Compound086
FEATURE [Part::Cut] Cut124
  Base = -> Cut117
  Tool = -> Compound083
FEATURE [Part::Cut] Cut125
  Base = -> Cut123
  Tool = -> Compound085
FEATURE [Part::Compound] Compound087  label="siroke_kluzno"
  Links = -> [Cut125,Cut124,Cut122,Cut121,Cut120,Cut115,Cut114]
FEATURE [Mesh::Feature] Mesh006  label="siroke_kluzno (Meshed)"
FEATURE [Part::Cylinder] Cylinder206  label="Válec206"
  Angle = 360
  AttacherType = Attacher::AttachEngine3D
  Height = 10
  Placement = pos=(17,-24,10) rot=(1,0,0;1.5708rad)
  Radius = 11
FEATURE [Part::Cylinder] Cylinder207  label="Válec207"
  Angle = 360
  AttacherType = Attacher::AttachEngine3D
  Height = 4
  Placement = pos=(-21,-25.5,15) rot=(0,0,1;0rad)
  Radius = 5
FEATURE [Part::Cylinder] Cylinder208  label="Válec208"
  Angle = 360
  AttacherType = Attacher::AttachEngine3D
  Height = 5
  Placement = pos=(-21,-25.5,15) rot=(0,0,1;0rad)
  Radius = 8.5
FEATURE [Part::Box] Box152  label="Krychle152"
  AttacherType = Attacher::AttachEngine3D
  Height = 5
  Length = 76
  Placement = pos=(-21,-34,15) rot=(0,0,1;0rad)
  Width = 17
FEATURE [Part::Cylinder] Cylinder209  label="Válec209"
  Angle = 360
  AttacherType = Attacher::AttachEngine3D
  Height = 5
  Placement = pos=(55,-25.5,15) rot=(0,0,1;0rad)
  Radius = 8.5
FEATURE [Part::Box] Box153  label="Krychle153"
  AttacherType = Attacher::AttachEngine3D
  Height = 5
  Length = 56
  Placement = pos=(-11,-34,10) rot=(0,0,1;0rad)
  Width = 17
FEATURE [Part::Cylinder] Cylinder210  label="Válec210"
  Angle = 360
  AttacherType = Attacher::AttachEngine3D
  Height = 20
  Placement = pos=(-5,-17,10) rot=(1,0,0;1.5708rad)
  Radius = 5.1
FEATURE [Part::Cylinder] Cylinder211  label="Válec211"
  Angle = 360
  AttacherType = Attacher::AttachEngine3D
  Height = 20
  Placement = pos=(39,-17,10) rot=(1,0,0;1.5708rad)
  Radius = 5.1
FEATURE [Part::Cylinder] Cylinder212  label="Válec212"
  Angle = 360
  AttacherType = Attacher::AttachEngine3D
  Height = 17
  Placement = pos=(-5,-17,10) rot=(1,0,0;1.5708rad)
  Radius = 7
FEATURE [Part::Cylinder] Cylinder213  label="Válec213"
  Angle = 360
  AttacherType = Attacher::AttachEngine3D
  Height = 17
  Placement = pos=(39,-17,10) rot=(1,0,0;1.5708rad)
  Radius = 7
FEATURE [Part::Cylinder] Cylinder214  label="Válec214"
  Angle = 360
  AttacherType = Attacher::AttachEngine3D
  Height = 4
  Placement = pos=(55,-25.5,15) rot=(0,0,1;0rad)
  Radius = 5
FEATURE [Part::Cylinder] Cylinder215  label="Válec215"
  Angle = 360
  AttacherType = Attacher::AttachEngine3D
  Height = 4
  Placement = pos=(-21,-25.5,15) rot=(0,0,1;0rad)
  Radius = 5
FEATURE [Part::Cylinder] Cylinder216  label="Válec216"
  Angle = 360
  AttacherType = Attacher::AttachEngine3D
  Height = 4
  Placement = pos=(55,-25.5,15) rot=(0,0,1;0rad)
  Radius = 5
FEATURE [Part::Cylinder] Cylinder217  label="Válec217"
  Angle = 360
  AttacherType = Attacher::AttachEngine3D
  Height = 20
  Placement = pos=(-5,-17,10) rot=(1,0,0;1.5708rad)
  Radius = 5.1
FEATURE [Part::Cylinder] Cylinder218  label="Válec218"
  Angle = 360
  AttacherType = Attacher::AttachEngine3D
  Height = 20
  Placement = pos=(39,-17,10) rot=(1,0,0;1.5708rad)
  Radius = 5.1
FEATURE [Part::Box] Box154  label="Krychle154"
  AttacherType = Attacher::AttachEngine3D
  Height = 10
  Length = 80
  Placement = pos=(-20,-36,0) rot=(0,0,1;0rad)
  Width = 20
FEATURE [Part::Box] Box155  label="Krychle155"
  AttacherType = Attacher::AttachEngine3D
  Height = 5
  Length = 4
  Placement = pos=(-12,-34,10) rot=(0,0,1;0rad)
  Width = 17
FEATURE [Part::Box] Box156  label="Krychle156"
  AttacherType = Attacher::AttachEngine3D
  Height = 5
  Length = 4
  Placement = pos=(42,-34,10) rot=(0,0,1;0rad)
  Width = 17
FEATURE [Part::Cylinder] Cylinder219  label="Válec219"
  Angle = 360
  AttacherType = Attacher::AttachEngine3D
  Height = 20
  Placement = pos=(39,-17,10) rot=(1,0,0;1.5708rad)
  Radius = 5.1
FEATURE [Part::Cylinder] Cylinder220  label="Válec220"
  Angle = 360
  AttacherType = Attacher::AttachEngine3D
  Height = 20
  Placement = pos=(-5,-17,10) rot=(1,0,0;1.5708rad)
  Radius = 5.1
FEATURE [Part::Compound] Compound088
  Links = -> [Cylinder210,Cylinder211]
FEATURE [Part::Compound] Compound089
  Links = -> [Cylinder212,Cylinder213]
FEATURE [Part::Compound] Compound090
  Links = -> [Cylinder217,Cylinder218]
FEATURE [Part::Compound] Compound091
  Links = -> [Box155,Box156]
FEATURE [Part::FeaturePython] Tube004  # WARN: FeaturePython — macro-defined, semantics opaque (R4)
  AttacherType = Attacher::AttachEngine3D
  Height = 1
  InnerRadius = 3
  OuterRadius = 5.1
  Placement = pos=(-5,-17,10) rot=(1,0,0;1.5708rad)
FEATURE [Part::FeaturePython] Tube005  # WARN: FeaturePython — macro-defined, semantics opaque (R4)
  AttacherType = Attacher::AttachEngine3D
  Height = 1
  InnerRadius = 3
  OuterRadius = 5.1
  Placement = pos=(-5,-33,10) rot=(1,0,0;1.5708rad)
FEATURE [Part::FeaturePython] Tube006  # WARN: FeaturePython — macro-defined, semantics opaque (R4)
  AttacherType = Attacher::AttachEngine3D
  Height = 1
  InnerRadius = 3
  OuterRadius = 5.1
  Placement = pos=(39,-17,10) rot=(1,0,0;1.5708rad)
FEATURE [Part::FeaturePython] Tube007  # WARN: FeaturePython — macro-defined, semantics opaque (R4)
  AttacherType = Attacher::AttachEngine3D
  Height = 1
  InnerRadius = 3
  OuterRadius = 5.1
  Placement = pos=(39,-33,10) rot=(1,0,0;1.5708rad)
FEATURE [Part::Cut] Cut126
  Base = -> Cylinder208
  Tool = -> Cylinder207
FEATURE [Part::Cut] Cut127
  Base = -> Cylinder209
  Tool = -> Cylinder214
FEATURE [Part::Cut] Cut128
  Base = -> Box152
  Tool = -> Cylinder215
FEATURE [Part::Cut] Cut129
  Base = -> Cut128
  Tool = -> Cylinder216
FEATURE [Part::Cut] Cut130
  Base = -> Compound089
  Tool = -> Compound088
FEATURE [Part::Cut] Cut131
  Base = -> Box153
  Tool = -> Compound090
FEATURE [Part::Cut] Cut132
  Base = -> Cut130
  Tool = -> Box154
FEATURE [Part::Compound] Compound092
  Links = -> [Cylinder220,Cylinder219]
FEATURE [Part::Cut] Cut133
  Base = -> Compound091
  Tool = -> Compound092
FEATURE [Part::Compound] Compound093
  Links = -> [Tube004,Tube005,Tube006,Tube007]
FEATURE [Part::Box] Box157  label="Krychle157"
  AttacherType = Attacher::AttachEngine3D
  Height = 10
  Length = 80
  Placement = pos=(-20,-36,0) rot=(0,0,1;0rad)
  Width = 20
FEATURE [Part::Cut] Cut134
  Base = -> Compound093
  Tool = -> Box157
FEATURE [Part::Cylinder] Cylinder221  label="Válec221"
  Angle = 360
  AttacherType = Attacher::AttachEngine3D
  Height = 10
  Placement = pos=(3,-20,9) rot=(0,0,1;0rad)
  Radius = 1.5
FEATURE [Part::Cylinder] Cylinder222  label="Válec222"
  Angle = 360
  AttacherType = Attacher::AttachEngine3D
  Height = 10
  Placement = pos=(3,-31,9) rot=(0,0,1;0rad)
  Radius = 1.5
FEATURE [Part::Cylinder] Cylinder223  label="Válec223"
  Angle = 360
  AttacherType = Attacher::AttachEngine3D
  Height = 10
  Placement = pos=(31,-20,9) rot=(0,0,1;0rad)
  Radius = 1.5
FEATURE [Part::Cylinder] Cylinder224  label="Válec224"
  Angle = 360
  AttacherType = Attacher::AttachEngine3D
  Height = 10
  Placement = pos=(31,-31,9) rot=(0,0,1;0rad)
  Radius = 1.5
FEATURE [Part::Compound] Compound094
  Links = -> [Cylinder221,Cylinder222,Cylinder223,Cylinder224]
FEATURE [Part::Box] Box158  label="Krychle158"
  AttacherType = Attacher::AttachEngine3D
  Height = 2
  Length = 6
  Placement = pos=(28,-34,13) rot=(0,0,1;0rad)
  Width = 6
FEATURE [Part::Box] Box159  label="Krychle159"
  AttacherType = Attacher::AttachEngine3D
  Height = 2
  Length = 6
  Placement = pos=(0,-23,13) rot=(0,0,1;0rad)
  Width = 6
FEATURE [Part::Box] Box160  label="Krychle160"
  AttacherType = Attacher::AttachEngine3D
  Height = 2
  Length = 6
  Placement = pos=(0,-34,13) rot=(0,0,1;0rad)
  Width = 6
FEATURE [Part::Box] Box161  label="Krychle161"
  AttacherType = Attacher::AttachEngine3D
  Height = 2
  Length = 6
  Placement = pos=(28,-23,13) rot=(0,0,1;0rad)
  Width = 6
FEATURE [Part::Compound] Compound095
  Links = -> [Box160,Box159,Box158,Box161]
FEATURE [Part::Cylinder] Cylinder225  label="Válec225"
  Angle = 360
  AttacherType = Attacher::AttachEngine3D
  Height = 10
  Placement = pos=(3,-31,9) rot=(0,0,1;0rad)
  Radius = 1.5
FEATURE [Part::Cylinder] Cylinder226  label="Válec226"
  Angle = 360
  AttacherType = Attacher::AttachEngine3D
  Height = 10
  Placement = pos=(3,-20,9) rot=(0,0,1;0rad)
  Radius = 1.5
FEATURE [Part::Cylinder] Cylinder227  label="Válec227"
  Angle = 360
  AttacherType = Attacher::AttachEngine3D
  Height = 10
  Placement = pos=(31,-20,9) rot=(0,0,1;0rad)
  Radius = 1.5
FEATURE [Part::Cylinder] Cylinder228  label="Válec228"
  Angle = 360
  AttacherType = Attacher::AttachEngine3D
  Height = 10
  Placement = pos=(31,-31,9) rot=(0,0,1;0rad)
  Radius = 1.5
FEATURE [Part::Compound] Compound096
  Links = -> [Cylinder226,Cylinder225,Cylinder227,Cylinder228]
FEATURE [Part::Cut] Cut135
  Base = -> Cut131
  Tool = -> Compound096
FEATURE [Part::Cut] Cut136
  Base = -> Cut129
  Tool = -> Compound094
FEATURE [Part::Cut] Cut137
  Base = -> Cut135
  Tool = -> Compound095
FEATURE [Part::Cylinder] Cylinder229  label="Válec229"
  Angle = 360
  AttacherType = Attacher::AttachEngine3D
  Height = 10
  Placement = pos=(3,-31,9) rot=(0,0,1;0rad)
  Radius = 1.5
FEATURE [Part::Cylinder] Cylinder230  label="Válec230"
  Angle = 360
  AttacherType = Attacher::AttachEngine3D
  Height = 10
  Placement = pos=(3,-20,9) rot=(0,0,1;0rad)
  Radius = 1.5
FEATURE [Part::Cylinder] Cylinder231  label="Válec231"
  Angle = 360
  AttacherType = Attacher::AttachEngine3D
  Height = 10
  Placement = pos=(31,-20,9) rot=(0,0,1;0rad)
  Radius = 1.5
FEATURE [Part::Cylinder] Cylinder232  label="Válec232"
  Angle = 360
  AttacherType = Attacher::AttachEngine3D
  Height = 10
  Placement = pos=(31,-31,9) rot=(0,0,1;0rad)
  Radius = 1.5
FEATURE [Part::Compound] Compound098
  Links = -> [Cylinder230,Cylinder229,Cylinder231,Cylinder232]
FEATURE [Part::Box] Box162  label="Krychle162"
  AttacherType = Attacher::AttachEngine3D
  Height = 2
  Length = 6
  Placement = pos=(28,-34,13) rot=(0,0,1;0rad)
  Width = 6
FEATURE [Part::Box] Box163  label="Krychle163"
  AttacherType = Attacher::AttachEngine3D
  Height = 2
  Length = 6
  Placement = pos=(0,-23,13) rot=(0,0,1;0rad)
  Width = 6
FEATURE [Part::Box] Box164  label="Krychle164"
  AttacherType = Attacher::AttachEngine3D
  Height = 2
  Length = 6
  Placement = pos=(0,-34,13) rot=(0,0,1;0rad)
  Width = 6
FEATURE [Part::Box] Box165  label="Krychle165"
  AttacherType = Attacher::AttachEngine3D
  Height = 2
  Length = 6
  Placement = pos=(28,-23,13) rot=(0,0,1;0rad)
  Width = 6
FEATURE [Part::Compound] Compound099
  Links = -> [Box164,Box163,Box162,Box165]
FEATURE [Part::Cut] Cut138
  Base = -> Cut132
  Tool = -> Compound098
FEATURE [Part::Cut] Cut139
  Base = -> Cut138
  Tool = -> Compound099
FEATURE [Part::Cylinder] Cylinder233  label="Válec233"
  Angle = 360
  AttacherType = Attacher::AttachEngine3D
  Height = 30
  Placement = pos=(11.5,-19,4.5) rot=(1,0,0;1.5708rad)
  Radius = 1.5
FEATURE [Part::Cylinder] Cylinder234  label="Válec234"
  Angle = 360
  AttacherType = Attacher::AttachEngine3D
  Height = 30
  Placement = pos=(22.5,-19,4.5) rot=(1,0,0;1.5708rad)
  Radius = 1.5
FEATURE [Part::Cylinder] Cylinder235  label="Válec235"
  Angle = 360
  AttacherType = Attacher::AttachEngine3D
  Height = 30
  Placement = pos=(11.5,-19,15.5) rot=(1,0,0;1.5708rad)
  Radius = 1.5
FEATURE [Part::Cylinder] Cylinder236  label="Válec236"
  Angle = 360
  AttacherType = Attacher::AttachEngine3D
  Height = 30
  Placement = pos=(22.5,-19,15.5) rot=(1,0,0;1.5708rad)
  Radius = 1.5
FEATURE [Part::Compound] Compound100
  Links = -> [Cylinder233,Cylinder234,Cylinder235,Cylinder236]
  Placement = pos=(0,9,0) rot=(0,0,1;0rad)
FEATURE [Part::Box] Box166  label="Krychle166"
  AttacherType = Attacher::AttachEngine3D
  Height = 8
  Length = 6
  Placement = pos=(8.5,-21,12) rot=(0,0,1;0rad)
  Width = 2
FEATURE [Part::Box] Box167  label="Krychle167"
  AttacherType = Attacher::AttachEngine3D
  Height = 8
  Length = 6
  Placement = pos=(19.5,-21,12) rot=(0,0,1;0rad)
  Width = 2
FEATURE [Part::Box] Box168  label="Krychle168"
  AttacherType = Attacher::AttachEngine3D
  Height = 8
  Length = 6
  Placement = pos=(8.5,-21,1) rot=(0,0,1;0rad)
  Width = 2
FEATURE [Part::Box] Box169  label="Krychle169"
  AttacherType = Attacher::AttachEngine3D
  Height = 8
  Length = 6
  Placement = pos=(19.5,-21,1) rot=(0,0,1;0rad)
  Width = 2
FEATURE [Part::Compound] Compound101
  Links = -> [Box166,Box167,Box168,Box169]
FEATURE [Part::Cylinder] Cylinder237  label="Válec237"
  Angle = 360
  AttacherType = Attacher::AttachEngine3D
  Height = 10
  Placement = pos=(17,-24,10) rot=(1,0,0;1.5708rad)
  Radius = 11
FEATURE [Part::Cut] Cut140
  Base = -> Cut137
  Tool = -> Cylinder206
FEATURE [Part::Cut] Cut141
  Base = -> Cut136
  Tool = -> Cylinder237
FEATURE [Part::Cylinder] Cylinder238  label="Válec238"
  Angle = 360
  AttacherType = Attacher::AttachEngine3D
  Height = 30
  Placement = pos=(22.5,-19,15.5) rot=(1,0,0;1.5708rad)
  Radius = 1.5
FEATURE [Part::Cylinder] Cylinder239  label="Válec239"
  Angle = 360
  AttacherType = Attacher::AttachEngine3D
  Height = 30
  Placement = pos=(22.5,-19,4.5) rot=(1,0,0;1.5708rad)
  Radius = 1.5
FEATURE [Part::Cylinder] Cylinder240  label="Válec240"
  Angle = 360
  AttacherType = Attacher::AttachEngine3D
  Height = 30
  Placement = pos=(11.5,-19,4.5) rot=(1,0,0;1.5708rad)
  Radius = 1.5
FEATURE [Part::Cylinder] Cylinder241  label="Válec241"
  Angle = 360
  AttacherType = Attacher::AttachEngine3D
  Height = 30
  Placement = pos=(11.5,-19,15.5) rot=(1,0,0;1.5708rad)
  Radius = 1.5
FEATURE [Part::Compound] Compound102
  Links = -> [Cylinder240,Cylinder239,Cylinder241,Cylinder238]
  Placement = pos=(0,9,0) rot=(0,0,1;0rad)
FEATURE [Part::Box] Box170  label="Krychle170"
  AttacherType = Attacher::AttachEngine3D
  Height = 8
  Length = 6
  Placement = pos=(8.5,-21,12) rot=(0,0,1;0rad)
  Width = 2
FEATURE [Part::Box] Box171  label="Krychle171"
  AttacherType = Attacher::AttachEngine3D
  Height = 8
  Length = 6
  Placement = pos=(19.5,-21,12) rot=(0,0,1;0rad)
  Width = 2
FEATURE [Part::Box] Box172  label="Krychle172"
  AttacherType = Attacher::AttachEngine3D
  Height = 8
  Length = 6
  Placement = pos=(19.5,-21,1) rot=(0,0,1;0rad)
  Width = 2
FEATURE [Part::Box] Box173  label="Krychle173"
  AttacherType = Attacher::AttachEngine3D
  Height = 8
  Length = 6
  Placement = pos=(8.5,-21,1) rot=(0,0,1;0rad)
  Width = 2
FEATURE [Part::Compound] Compound103
  Links = -> [Box170,Box171,Box173,Box172]
FEATURE [Part::Cut] Cut142
  Base = -> Cut140
  Tool = -> Compound101
FEATURE [Part::Cut] Cut143
  Base = -> Cut142
  Tool = -> Compound100
FEATURE [Part::Cut] Cut144
  Base = -> Cut141
  Tool = -> Compound102
FEATURE [Part::Cut] Cut145
  Base = -> Cut144
  Tool = -> Compound103
FEATURE [Part::Cut] Cut146
  Base = -> Cut144
  Tool = -> Compound103
FEATURE [Mesh::Feature] Mesh007  label="uzko_kluzno (Meshed)"
FEATURE [Part::Cylinder] Cylinder242  label="Válec242"
  Angle = 360
  AttacherType = Attacher::AttachEngine3D
  Height = 10
  Placement = pos=(17,-24,10) rot=(1,0,0;1.5708rad)
  Radius = 11
FEATURE [Part::Cylinder] Cylinder243  label="Válec243"
  Angle = 360
  AttacherType = Attacher::AttachEngine3D
  Height = 5
  Placement = pos=(55,-25.5,15) rot=(0,0,1;0rad)
  Radius = 8.5
FEATURE [Part::Cylinder] Cylinder244  label="Válec244"
  Angle = 360
  AttacherType = Attacher::AttachEngine3D
  Height = 5
  Placement = pos=(-21,-25.5,15) rot=(0,0,1;0rad)
  Radius = 8.5
FEATURE [Part::Cylinder] Cylinder245  label="Válec245"
  Angle = 360
  AttacherType = Attacher::AttachEngine3D
  Height = 4
  Placement = pos=(-21,-25.5,15) rot=(0,0,1;0rad)
  Radius = 5
FEATURE [Part::Box] Box174  label="Krychle174"
  AttacherType = Attacher::AttachEngine3D
  Height = 5
  Length = 76
  Placement = pos=(-21,-34,15) rot=(0,0,1;0rad)
  Width = 17
FEATURE [Part::Box] Box175  label="Krychle175"
  AttacherType = Attacher::AttachEngine3D
  Height = 5
  Length = 56
  Placement = pos=(-11,-34,10) rot=(0,0,1;0rad)
  Width = 17
FEATURE [Part::Cylinder] Cylinder246  label="Válec246"
  Angle = 360
  AttacherType = Attacher::AttachEngine3D
  Height = 20
  Placement = pos=(-5,-17,10) rot=(1,0,0;1.5708rad)
  Radius = 5
FEATURE [Part::Cylinder] Cylinder247  label="Válec247"
  Angle = 360
  AttacherType = Attacher::AttachEngine3D
  Height = 20
  Placement = pos=(39,-17,10) rot=(1,0,0;1.5708rad)
  Radius = 5
FEATURE [Part::Cylinder] Cylinder248  label="Válec248"
  Angle = 360
  AttacherType = Attacher::AttachEngine3D
  Height = 17
  Placement = pos=(-5,-17,10) rot=(1,0,0;1.5708rad)
  Radius = 7
FEATURE [Part::Cylinder] Cylinder249  label="Válec249"
  Angle = 360
  AttacherType = Attacher::AttachEngine3D
  Height = 17
  Placement = pos=(39,-17,10) rot=(1,0,0;1.5708rad)
  Radius = 7
FEATURE [Part::Cylinder] Cylinder250  label="Válec250"
  Angle = 360
  AttacherType = Attacher::AttachEngine3D
  Height = 4
  Placement = pos=(55,-25.5,15) rot=(0,0,1;0rad)
  Radius = 5
FEATURE [Part::Cylinder] Cylinder251  label="Válec251"
  Angle = 360
  AttacherType = Attacher::AttachEngine3D
  Height = 4
  Placement = pos=(55,-25.5,15) rot=(0,0,1;0rad)
  Radius = 5
FEATURE [Part::Cylinder] Cylinder252  label="Válec252"
  Angle = 360
  AttacherType = Attacher::AttachEngine3D
  Height = 20
  Placement = pos=(-5,-17,10) rot=(1,0,0;1.5708rad)
  Radius = 5
FEATURE [Part::Cylinder] Cylinder253  label="Válec253"
  Angle = 360
  AttacherType = Attacher::AttachEngine3D
  Height = 4
  Placement = pos=(-21,-25.5,15) rot=(0,0,1;0rad)
  Radius = 5
FEATURE [Part::Compound] Compound105
  Links = -> [Cylinder246,Cylinder247]
FEATURE [Part::Compound] Compound111
  Links = -> [Cylinder248,Cylinder249]
FEATURE [Part::Cut] Cut147
  Base = -> Cylinder244
  Tool = -> Cylinder245
FEATURE [Part::Cut] Cut148
  Base = -> Cylinder243
  Tool = -> Cylinder250
FEATURE [Part::Cut] Cut150
  Base = -> Compound111
  Tool = -> Compound105
FEATURE [Part::Cut] Cut153
  Base = -> Box174
  Tool = -> Cylinder253
FEATURE [Part::Cut] Cut149
  Base = -> Cut153
  Tool = -> Cylinder251
FEATURE [Part::Cylinder] Cylinder254  label="Válec254"
  Angle = 360
  AttacherType = Attacher::AttachEngine3D
  Height = 10
  Placement = pos=(31,-20,9) rot=(0,0,1;0rad)
  Radius = 1.5
FEATURE [Part::Box] Box176  label="Krychle176"
  AttacherType = Attacher::AttachEngine3D
  Height = 2
  Length = 6
  Placement = pos=(0,-23,13) rot=(0,0,1;0rad)
  Width = 6
FEATURE [Part::Box] Box177  label="Krychle177"
  AttacherType = Attacher::AttachEngine3D
  Height = 10
  Length = 80
  Placement = pos=(-20,-36,0) rot=(0,0,1;0rad)
  Width = 20
FEATURE [Part::Cylinder] Cylinder255  label="Válec255"
  Angle = 360
  AttacherType = Attacher::AttachEngine3D
  Height = 10
  Placement = pos=(3,-20,9) rot=(0,0,1;0rad)
  Radius = 1.5
FEATURE [Part::Cylinder] Cylinder256  label="Válec256"
  Angle = 360
  AttacherType = Attacher::AttachEngine3D
  Height = 10
  Placement = pos=(31,-20,9) rot=(0,0,1;0rad)
  Radius = 1.5
FEATURE [Part::Cylinder] Cylinder257  label="Válec257"
  Angle = 360
  AttacherType = Attacher::AttachEngine3D
  Height = 10
  Placement = pos=(3,-31,9) rot=(0,0,1;0rad)
  Radius = 1.5
FEATURE [Part::Cylinder] Cylinder258  label="Válec258"
  Angle = 360
  AttacherType = Attacher::AttachEngine3D
  Height = 10
  Placement = pos=(31,-20,9) rot=(0,0,1;0rad)
  Radius = 1.5
FEATURE [Part::Cylinder] Cylinder259  label="Válec259"
  Angle = 360
  AttacherType = Attacher::AttachEngine3D
  Height = 10
  Placement = pos=(3,-31,9) rot=(0,0,1;0rad)
  Radius = 1.5
FEATURE [Part::Cylinder] Cylinder260  label="Válec260"
  Angle = 360
  AttacherType = Attacher::AttachEngine3D
  Height = 20
  Placement = pos=(-5,-17,10) rot=(1,0,0;1.5708rad)
  Radius = 5
FEATURE [Part::Cylinder] Cylinder261  label="Válec261"
  Angle = 360
  AttacherType = Attacher::AttachEngine3D
  Height = 10
  Placement = pos=(3,-31,9) rot=(0,0,1;0rad)
  Radius = 1.5
FEATURE [Part::Cylinder] Cylinder262  label="Válec262"
  Angle = 360
  AttacherType = Attacher::AttachEngine3D
  Height = 10
  Placement = pos=(31,-31,9) rot=(0,0,1;0rad)
  Radius = 1.5
FEATURE [Part::Compound] Compound110
  Links = -> [Cylinder255,Cylinder261,Cylinder254,Cylinder262]
FEATURE [Part::Box] Box178  label="Krychle178"
  AttacherType = Attacher::AttachEngine3D
  Height = 5
  Length = 4
  Placement = pos=(42,-34,10) rot=(0,0,1;0rad)
  Width = 17
FEATURE [Part::Box] Box179  label="Krychle179"
  AttacherType = Attacher::AttachEngine3D
  Height = 10
  Length = 80
  Placement = pos=(-20,-36,0) rot=(0,0,1;0rad)
  Width = 20
FEATURE [Part::Cut] Cut152
  Base = -> Cut150
  Tool = -> Box179
FEATURE [Part::Box] Box180  label="Krychle180"
  AttacherType = Attacher::AttachEngine3D
  Height = 5
  Length = 4
  Placement = pos=(-12,-34,10) rot=(0,0,1;0rad)
  Width = 17
FEATURE [Part::Compound] Compound107
  Links = -> [Box180,Box178]
FEATURE [Part::Cylinder] Cylinder263  label="Válec263"
  Angle = 360
  AttacherType = Attacher::AttachEngine3D
  Height = 20
  Placement = pos=(39,-17,10) rot=(1,0,0;1.5708rad)
  Radius = 5
FEATURE [Part::Compound] Compound106
  Links = -> [Cylinder252,Cylinder263]
FEATURE [Part::Cut] Cut151
  Base = -> Box175
  Tool = -> Compound106
FEATURE [Part::Cylinder] Cylinder264  label="Válec264"
  Angle = 360
  AttacherType = Attacher::AttachEngine3D
  Height = 20
  Placement = pos=(39,-17,10) rot=(1,0,0;1.5708rad)
  Radius = 5
FEATURE [Part::Compound] Compound112
  Links = -> [Cylinder260,Cylinder264]
FEATURE [Part::Box] Box181  label="Krychle181"
  AttacherType = Attacher::AttachEngine3D
  Height = 2
  Length = 6
  Placement = pos=(28,-34,13) rot=(0,0,1;0rad)
  Width = 6
FEATURE [Part::Box] Box182  label="Krychle182"
  AttacherType = Attacher::AttachEngine3D
  Height = 2
  Length = 6
  Placement = pos=(26,-23,13) rot=(0,0,1;0rad)
  Width = 6
FEATURE [Part::Cylinder] Cylinder265  label="Válec265"
  Angle = 360
  AttacherType = Attacher::AttachEngine3D
  Height = 10
  Placement = pos=(3,-20,9) rot=(0,0,1;0rad)
  Radius = 1.5
FEATURE [Part::Box] Box183  label="Krychle183"
  AttacherType = Attacher::AttachEngine3D
  Height = 2
  Length = 6
  Placement = pos=(0,-34,13) rot=(0,0,1;0rad)
  Width = 6
FEATURE [Part::Compound] Compound109
  Links = -> [Box183,Box176,Box181,Box182]
  Placement = pos=(0,-100,0) rot=(0,0,1;0rad)
FEATURE [Part::Cylinder] Cylinder266  label="Válec266"
  Angle = 360
  AttacherType = Attacher::AttachEngine3D
  Height = 10
  Placement = pos=(31,-31,9) rot=(0,0,1;0rad)
  Radius = 1.5
FEATURE [Part::Cylinder] Cylinder267  label="Válec267"
  Angle = 360
  AttacherType = Attacher::AttachEngine3D
  Height = 10
  Placement = pos=(3,-20,9) rot=(0,0,1;0rad)
  Radius = 1.5
FEATURE [Part::Box] Box184  label="Krychle184"
  AttacherType = Attacher::AttachEngine3D
  Height = 2
  Length = 6
  Placement = pos=(0,-23,13) rot=(0,0,1;0rad)
  Width = 6
FEATURE [Part::Box] Box185  label="Krychle185"
  AttacherType = Attacher::AttachEngine3D
  Height = 2
  Length = 6
  Placement = pos=(28,-34,13) rot=(0,0,1;0rad)
  Width = 6
FEATURE [Part::Box] Box186  label="Krychle186"
  AttacherType = Attacher::AttachEngine3D
  Height = 2
  Length = 6
  Placement = pos=(26,-23,13) rot=(0,0,1;0rad)
  Width = 6
FEATURE [Part::Cylinder] Cylinder268  label="Válec268"
  Angle = 360
  AttacherType = Attacher::AttachEngine3D
  Height = 10
  Placement = pos=(31,-31,9) rot=(0,0,1;0rad)
  Radius = 1.5
FEATURE [Part::Box] Box187  label="Krychle187"
  AttacherType = Attacher::AttachEngine3D
  Height = 2
  Length = 6
  Placement = pos=(0,-34,13) rot=(0,0,1;0rad)
  Width = 6
FEATURE [Part::FeaturePython] Tube008  # WARN: FeaturePython — macro-defined, semantics opaque (R4)
  AttacherType = Attacher::AttachEngine3D
  Height = 1
  InnerRadius = 3
  OuterRadius = 5
  Placement = pos=(-5,-33,10) rot=(1,0,0;1.5708rad)
FEATURE [Part::FeaturePython] Tube009  # WARN: FeaturePython — macro-defined, semantics opaque (R4)
  AttacherType = Attacher::AttachEngine3D
  Height = 1
  InnerRadius = 3
  OuterRadius = 5
  Placement = pos=(39,-17,10) rot=(1,0,0;1.5708rad)
FEATURE [Part::FeaturePython] Tube010  # WARN: FeaturePython — macro-defined, semantics opaque (R4)
  AttacherType = Attacher::AttachEngine3D
  Height = 1
  InnerRadius = 3
  OuterRadius = 5
  Placement = pos=(39,-33,10) rot=(1,0,0;1.5708rad)
FEATURE [Part::FeaturePython] Tube011  # WARN: FeaturePython — macro-defined, semantics opaque (R4)
  AttacherType = Attacher::AttachEngine3D
  Height = 1
  InnerRadius = 3
  OuterRadius = 5
  Placement = pos=(-5,-17,10) rot=(1,0,0;1.5708rad)
FEATURE [Part::Compound] Compound108
  Links = -> [Tube011,Tube008,Tube009,Tube010]
FEATURE [Part::Cut] Cut156
  Base = -> Cut149
  Tool = -> Compound110
FEATURE [Part::Cut] Cut157
  Base = -> Compound107
  Tool = -> Compound112
FEATURE [Part::Cut] Cut158
  Base = -> Compound108
  Tool = -> Box177
FEATURE [Part::Compound] Compound113
  Links = -> [Cylinder265,Cylinder259,Cylinder256,Cylinder266]
FEATURE [Part::Cut] Cut160
  Base = -> Cut151
  Tool = -> Compound113
FEATURE [Part::Cut] Cut155
  Base = -> Cut160
  Tool = -> Compound109
FEATURE [Part::Compound] Compound114
  Links = -> [Box187,Box184,Box185,Box186]
  Placement = pos=(0,-100,0) rot=(0,0,1;0rad)
FEATURE [Part::Compound] Compound115
  Links = -> [Cylinder267,Cylinder257,Cylinder258,Cylinder268]
FEATURE [Part::Cut] Cut159
  Base = -> Cut152
  Tool = -> Compound115
FEATURE [Part::Cut] Cut154
  Base = -> Cut159
  Tool = -> Compound114
FEATURE [Part::Box] Box188  label="Krychle188"
  AttacherType = Attacher::AttachEngine3D
  Height = 8
  Length = 6
  Placement = pos=(8.5,-21,12) rot=(0,0,1;0rad)
  Width = 2
FEATURE [Part::Cylinder] Cylinder269  label="Válec269"
  Angle = 360
  AttacherType = Attacher::AttachEngine3D
  Height = 30
  Placement = pos=(22.5,-19,15.5) rot=(1,0,0;1.5708rad)
  Radius = 1.5
FEATURE [Part::Box] Box189  label="Krychle189"
  AttacherType = Attacher::AttachEngine3D
  Height = 8
  Length = 6
  Placement = pos=(19.5,-21,1) rot=(0,0,1;0rad)
  Width = 2
FEATURE [Part::Box] Box190  label="Krychle190"
  AttacherType = Attacher::AttachEngine3D
  Height = 8
  Length = 6
  Placement = pos=(8.5,-21,12) rot=(0,0,1;0rad)
  Width = 2
FEATURE [Part::Box] Box191  label="Krychle191"
  AttacherType = Attacher::AttachEngine3D
  Height = 8
  Length = 6
  Placement = pos=(19.5,-21,12) rot=(0,0,1;0rad)
  Width = 2
FEATURE [Part::Cylinder] Cylinder270  label="Válec270"
  Angle = 360
  AttacherType = Attacher::AttachEngine3D
  Height = 30
  Placement = pos=(22.5,-19,4.5) rot=(1,0,0;1.5708rad)
  Radius = 1.5
FEATURE [Part::Cylinder] Cylinder271  label="Válec271"
  Angle = 360
  AttacherType = Attacher::AttachEngine3D
  Height = 30
  Placement = pos=(11.5,-19,4.5) rot=(1,0,0;1.5708rad)
  Radius = 1.5
FEATURE [Part::Box] Box192  label="Krychle192"
  AttacherType = Attacher::AttachEngine3D
  Height = 8
  Length = 6
  Placement = pos=(19.5,-21,12) rot=(0,0,1;0rad)
  Width = 2
FEATURE [Part::Cylinder] Cylinder272  label="Válec272"
  Angle = 360
  AttacherType = Attacher::AttachEngine3D
  Height = 10
  Placement = pos=(17,-24,10) rot=(1,0,0;1.5708rad)
  Radius = 11
FEATURE [Part::Cylinder] Cylinder273  label="Válec273"
  Angle = 360
  AttacherType = Attacher::AttachEngine3D
  Height = 30
  Placement = pos=(11.5,-19,4.5) rot=(1,0,0;1.5708rad)
  Radius = 1.5
FEATURE [Part::Cylinder] Cylinder274  label="Válec274"
  Angle = 360
  AttacherType = Attacher::AttachEngine3D
  Height = 30
  Placement = pos=(11.5,-19,15.5) rot=(1,0,0;1.5708rad)
  Radius = 1.5
FEATURE [Part::Compound] Compound116
  Links = -> [Cylinder273,Cylinder270,Cylinder274,Cylinder269]
  Placement = pos=(0,9,0) rot=(0,0,1;0rad)
FEATURE [Part::Box] Box193  label="Krychle193"
  AttacherType = Attacher::AttachEngine3D
  Height = 8
  Length = 6
  Placement = pos=(19.5,-21,1) rot=(0,0,1;0rad)
  Width = 2
FEATURE [Part::Cylinder] Cylinder275  label="Válec275"
  Angle = 360
  AttacherType = Attacher::AttachEngine3D
  Height = 30
  Placement = pos=(11.5,-19,15.5) rot=(1,0,0;1.5708rad)
  Radius = 1.5
FEATURE [Part::Cylinder] Cylinder276  label="Válec276"
  Angle = 360
  AttacherType = Attacher::AttachEngine3D
  Height = 30
  Placement = pos=(22.5,-19,4.5) rot=(1,0,0;1.5708rad)
  Radius = 1.5
FEATURE [Part::Box] Box194  label="Krychle194"
  AttacherType = Attacher::AttachEngine3D
  Height = 8
  Length = 6
  Placement = pos=(8.5,-21,1) rot=(0,0,1;0rad)
  Width = 2
FEATURE [Part::Compound] Compound118
  Links = -> [Box188,Box191,Box194,Box193]
FEATURE [Part::Cylinder] Cylinder277  label="Válec277"
  Angle = 360
  AttacherType = Attacher::AttachEngine3D
  Height = 30
  Placement = pos=(22.5,-19,15.5) rot=(1,0,0;1.5708rad)
  Radius = 1.5
FEATURE [Part::Compound] Compound117
  Links = -> [Cylinder271,Cylinder276,Cylinder275,Cylinder277]
  Placement = pos=(0,9,0) rot=(0,0,1;0rad)
FEATURE [Part::Box] Box195  label="Krychle195"
  AttacherType = Attacher::AttachEngine3D
  Height = 8
  Length = 6
  Placement = pos=(8.5,-21,1) rot=(0,0,1;0rad)
  Width = 2
FEATURE [Part::Cut] Cut163
  Base = -> Cut156
  Tool = -> Cylinder272
FEATURE [Part::Cut] Cut164
  Base = -> Cut163
  Tool = -> Compound117
FEATURE [Part::Cut] Cut166
  Base = -> Cut155
  Tool = -> Cylinder242
FEATURE [Part::Cut] Cut161
  Base = -> Cut166
  Tool = -> Compound118
FEATURE [Part::Cut] Cut165
  Base = -> Cut161
  Tool = -> Compound116
FEATURE [Part::Compound] Compound120
  Links = -> [Box190,Box192,Box195,Box189]
FEATURE [Part::Cut] Cut162
  Base = -> Cut164
  Tool = -> Compound120
FEATURE [Part::Cut] Cut167
  Base = -> Cut164
  Tool = -> Compound120
FEATURE [Part::Cylinder] Cylinder278  label="Válec278"
  Angle = 360
  AttacherType = Attacher::AttachEngine3D
  Height = 3
  Placement = pos=(31,-20,9) rot=(0,0,1;0rad)
  Radius = 3
FEATURE [Part::Cylinder] Cylinder279  label="Válec279"
  Angle = 360
  AttacherType = Attacher::AttachEngine3D
  Height = 3
  Placement = pos=(3,-31,9) rot=(0,0,1;0rad)
  Radius = 3
FEATURE [Part::Cylinder] Cylinder280  label="Válec280"
  Angle = 360
  AttacherType = Attacher::AttachEngine3D
  Height = 3
  Placement = pos=(3,-20,9) rot=(0,0,1;0rad)
  Radius = 3
FEATURE [Part::Cylinder] Cylinder281  label="Válec281"
  Angle = 360
  AttacherType = Attacher::AttachEngine3D
  Height = 3
  Placement = pos=(31,-31,9) rot=(0,0,1;0rad)
  Radius = 3
FEATURE [Part::Compound] Compound121
  Links = -> [Cylinder280,Cylinder279,Cylinder278,Cylinder281]
  Placement = pos=(0,0,8) rot=(0,0,1;0rad)
FEATURE [Part::Cylinder] Cylinder282  label="Válec282"
  Angle = 360
  AttacherType = Attacher::AttachEngine3D
  Height = 20
  Placement = pos=(17,-14,10) rot=(1,0,0;1.5708rad)
  Radius = 5
FEATURE [Part::Cylinder] Cylinder283  label="Válec283"
  Angle = 360
  AttacherType = Attacher::AttachEngine3D
  Height = 20
  Placement = pos=(17,-14,10) rot=(1,0,0;1.5708rad)
  Radius = 5
FEATURE [Part::Cut] Cut168
  Base = -> Cut143
  Tool = -> Cylinder282
FEATURE [Part::Cylinder] Cylinder284  label="Válec284"
  Angle = 360
  AttacherType = Attacher::AttachEngine3D
  Height = 2
  Placement = pos=(17,-22,10) rot=(1,0,0;1.5708rad)
  Radius = 5.25
FEATURE [Part::Cylinder] Cylinder285  label="Válec285"
  Angle = 360
  AttacherType = Attacher::AttachEngine3D
  Height = 2
  Placement = pos=(17,-22,10) rot=(1,0,0;1.5708rad)
  Radius = 5.25
FEATURE [Part::Cut] Cut169
  Base = -> Cut168
  Tool = -> Cylinder284
FEATURE [Part::Cut] Cut170
  Base = -> Cut145
  Tool = -> Cylinder285
FEATURE [Part::Cut] Cut171
  Base = -> Cut162
  Tool = -> Compound121
FEATURE [Part::Cylinder] Cylinder286  label="Válec286"
  Angle = 360
  AttacherType = Attacher::AttachEngine3D
  Height = 2
  Placement = pos=(17,-22,10) rot=(1,0,0;1.5708rad)
  Radius = 5.25
FEATURE [Part::Cut] Cut172
  Base = -> Cut165
  Tool = -> Cylinder283
FEATURE [Part::Cylinder] Cylinder287  label="Válec287"
  Angle = 360
  AttacherType = Attacher::AttachEngine3D
  Height = 2
  Placement = pos=(17,-22,10) rot=(1,0,0;1.5708rad)
  Radius = 5.25
FEATURE [Part::Cut] Cut173
  Base = -> Cut172
  Tool = -> Cylinder287
FEATURE [Part::Cut] Cut174
  Base = -> Cut171
  Tool = -> Cylinder286
FEATURE [Part::Compound] Compound124  label="oppo_uzko"
  Links = -> [Cut173,Cut174,Cut157,Cut158,Cut147,Cut148,Cut154]
FEATURE [Part::Mirroring] mirror005  label="uzko_kluzno_oppo"
  Base = (0,0,0)
  Normal = (1e-16,-1,0)
  Source = -> Compound124
FEATURE [Mesh::Feature] Mesh009  label="uzko_kluzno_oppo (Meshed)"
FEATURE [Part::Compound] Compound125  label="tahlo_lefto"
  Links = -> [Cut113,Compound076]
FEATURE [Mesh::Feature] Mesh010  label="tahlo_lefto (Meshed)"
FEATURE [Part::FeaturePython] Tube012  # WARN: FeaturePython — macro-defined, semantics opaque (R4)
  AttacherType = Attacher::AttachEngine3D
  Height = 8
  InnerRadius = 59
  OuterRadius = 64
  Placement = pos=(37,-1.5,6) rot=(0,0,1;0rad)
FEATURE [Part::Cylinder] Cylinder288  label="Válec288"
  Angle = 360
  AttacherType = Attacher::AttachEngine3D
  Height = 12
  Placement = pos=(-13,30,4) rot=(0,0,1;0rad)
  Radius = 2.65
FEATURE [Part::Cylinder] Cylinder289  label="Válec289"
  Angle = 360
  AttacherType = Attacher::AttachEngine3D
  Height = 12
  Placement = pos=(-13,-33,4) rot=(0,0,1;0rad)
  Radius = 2.65
FEATURE [Part::Compound] Compound126
  Links = -> [Cylinder288,Cylinder289]
FEATURE [Part::Cut] Cut175
  Base = -> Tube012
  Tool = -> Compound126
FEATURE [Part::Cylinder] Cylinder290  label="Válec290"
  Angle = 360
  AttacherType = Attacher::AttachEngine3D
  Height = 8
  Placement = pos=(-10,30,6) rot=(0,0,1;0rad)
  Radius = 5
FEATURE [Part::Cylinder] Cylinder291  label="Válec291"
  Angle = 360
  AttacherType = Attacher::AttachEngine3D
  Height = 8
  Placement = pos=(-13,-25,6) rot=(0,0,1;0rad)
  Radius = 5
FEATURE [Part::Cylinder] Cylinder292  label="Válec292"
  Angle = 360
  AttacherType = Attacher::AttachEngine3D
  Height = 12
  Placement = pos=(-10,30,4) rot=(0,0,1;0rad)
  Radius = 2.65
FEATURE [Part::Cut] Cut176
  Base = -> Cylinder290
  Placement = pos=(-3,0,0) rot=(0,0,1;0rad)
  Tool = -> Cylinder292
FEATURE [Part::Cylinder] Cylinder293  label="Válec293"
  Angle = 360
  AttacherType = Attacher::AttachEngine3D
  Height = 12
  Placement = pos=(-13,-25,4) rot=(0,0,1;0rad)
  Radius = 2.65
FEATURE [Part::Cut] Cut177
  Base = -> Cylinder291
  Placement = pos=(0,-8,0) rot=(0,0,1;0rad)
  Tool = -> Cylinder293
FEATURE [Part::Compound] Compound127  label="tahlo_lefto002"
  Links = -> [Cut176,Cut177]
FEATURE [Part::Box] Box196  label="Krychle196"
  AttacherType = Attacher::AttachEngine3D
  Height = 20
  Length = 100
  Placement = pos=(36,0,0) rot=(0,0,1;1.01229rad)
  Width = 100
FEATURE [Part::Box] Box197  label="Krychle197"
  AttacherType = Attacher::AttachEngine3D
  Height = 20
  Length = 100
  Placement = pos=(36,0,0) rot=(0,0,1;3.73501rad)
  Width = 100
FEATURE [Part::Box] Box198  label="Krychle198"
  AttacherType = Attacher::AttachEngine3D
  Height = 20
  Length = 100
  Placement = pos=(36,0,0) rot=(0,0,-1;1.16937rad)
  Width = 100
FEATURE [Part::Box] Box199  label="Krychle199"
  AttacherType = Attacher::AttachEngine3D
  Height = 20
  Length = 100
  Placement = pos=(36,0,0) rot=(0,0,-1;0.401426rad)
  Width = 100
FEATURE [Part::Cut] Cut178
  Base = -> Cut175
  Tool = -> Box196
FEATURE [Part::Cut] Cut179
  Base = -> Cut178
  Tool = -> Box199
FEATURE [Part::Cut] Cut180
  Base = -> Cut179
  Tool = -> Box198
FEATURE [Part::Cut] Cut181
  Base = -> Cut180
  Tool = -> Box197
FEATURE [Part::Compound] Compound128  label="tahlo_pruzo"
  Links = -> [Cut181,Compound127]
FEATURE [Part::FeaturePython] Tube013  # WARN: FeaturePython — macro-defined, semantics opaque (R4)
  AttacherType = Attacher::AttachEngine3D
  Height = 8
  InnerRadius = 59
  OuterRadius = 64
  Placement = pos=(37,-1.5,6) rot=(0,0,1;0rad)
FEATURE [Part::Box] Box200  label="Krychle200"
  AttacherType = Attacher::AttachEngine3D
  Height = 20
  Length = 100
  Placement = pos=(36,0,0) rot=(0,0,-1;1.16937rad)
  Width = 100
FEATURE [Part::Cylinder] Cylinder294  label="Válec294"
  Angle = 360
  AttacherType = Attacher::AttachEngine3D
  Height = 8
  Placement = pos=(-10,30,6) rot=(0,0,1;0rad)
  Radius = 5
FEATURE [Part::Box] Box201  label="Krychle201"
  AttacherType = Attacher::AttachEngine3D
  Height = 20
  Length = 100
  Placement = pos=(36,0,0) rot=(0,0,1;3.89208rad)
  Width = 100
FEATURE [Part::Cylinder] Cylinder295  label="Válec295"
  Angle = 360
  AttacherType = Attacher::AttachEngine3D
  Height = 8
  Placement = pos=(-13,-25,6) rot=(0,0,1;0rad)
  Radius = 5
FEATURE [Part::Box] Box202  label="Krychle202"
  AttacherType = Attacher::AttachEngine3D
  Height = 20
  Length = 100
  Placement = pos=(36,0,0) rot=(0,0,-1;0.401426rad)
  Width = 100
FEATURE [Part::Cylinder] Cylinder296  label="Válec296"
  Angle = 360
  AttacherType = Attacher::AttachEngine3D
  Height = 12
  Placement = pos=(-10,30,4) rot=(0,0,1;0rad)
  Radius = 2.65
FEATURE [Part::Cylinder] Cylinder297  label="Válec297"
  Angle = 360
  AttacherType = Attacher::AttachEngine3D
  Height = 12
  Placement = pos=(-13,-25,4) rot=(0,0,1;0rad)
  Radius = 2.65
FEATURE [Part::Box] Box203  label="Krychle203"
  AttacherType = Attacher::AttachEngine3D
  Height = 20
  Length = 100
  Placement = pos=(36,0,0) rot=(0,0,1;1.01229rad)
  Width = 100
FEATURE [Part::Cylinder] Cylinder298  label="Válec298"
  Angle = 360
  AttacherType = Attacher::AttachEngine3D
  Height = 12
  Placement = pos=(-13,30,4) rot=(0,0,1;0rad)
  Radius = 2.65
FEATURE [Part::Cylinder] Cylinder299  label="Válec299"
  Angle = 360
  AttacherType = Attacher::AttachEngine3D
  Height = 12
  Placement = pos=(-8,-40,4) rot=(0,0,1;0rad)
  Radius = 2.65
FEATURE [Part::Compound] Compound129
  Links = -> [Cylinder298,Cylinder299]
FEATURE [Part::Cut] Cut183
  Base = -> Tube013
  Tool = -> Compound129
FEATURE [Part::Cut] Cut182
  Base = -> Cut183
  Tool = -> Box203
FEATURE [Part::Cut] Cut184
  Base = -> Cylinder294
  Placement = pos=(-3,0,0) rot=(0,0,1;0rad)
  Tool = -> Cylinder296
FEATURE [Part::Cut] Cut185
  Base = -> Cut182
  Tool = -> Box202
FEATURE [Part::Cut] Cut186
  Base = -> Cut185
  Tool = -> Box200
FEATURE [Part::Cut] Cut187
  Base = -> Cut186
  Tool = -> Box201
FEATURE [Part::Cut] Cut188
  Base = -> Cylinder295
  Placement = pos=(5,-15,0) rot=(0,0,1;0rad)
  Tool = -> Cylinder297
FEATURE [Part::Compound] Compound131  label="tahlo_lefto003"
  Links = -> [Cut184,Cut188]
FEATURE [Part::Compound] Compound130  label="tahlo_pruzo_delso"
  Links = -> [Cut187,Compound131]
FEATURE [Mesh::Feature] Mesh011  label="tahlo_pruzo_delso (Meshed)"
FEATURE [Part::Box] Box204  label="Krychle204"
  AttacherType = Attacher::AttachEngine3D
  Height = 6
  Length = 54
  Placement = pos=(-10,-25,24) rot=(0,0,1;0rad)
  Width = 10
FEATURE [Part::Box] Box205  label="Krychle205"
  AttacherType = Attacher::AttachEngine3D
  Height = 6
  Length = 54
  Placement = pos=(-10,-25,-10) rot=(0,0,1;0rad)
  Width = 10
FEATURE [Part::Cylinder] Cylinder080  label="Válec080"
  Angle = 360
  AttacherType = Attacher::AttachEngine3D
  Height = 50
  Placement = pos=(1,-32,20) rot=(1,0,0;1.5708rad)
  Radius = 1.5
FEATURE [Part::Cylinder] Cylinder081  label="Válec081"
  Angle = 360
  AttacherType = Attacher::AttachEngine3D
  Height = 50
  Placement = pos=(1,-32,0) rot=(1,0,0;1.5708rad)
  Radius = 1.5
FEATURE [Part::Cylinder] Cylinder082  label="Válec082"
  Angle = 360
  AttacherType = Attacher::AttachEngine3D
  Height = 50
  Placement = pos=(33,-32,20) rot=(1,0,0;1.5708rad)
  Radius = 1.5
FEATURE [Part::Cylinder] Cylinder083  label="Válec083"
  Angle = 360
  AttacherType = Attacher::AttachEngine3D
  Height = 50
  Placement = pos=(33,-32,0) rot=(1,0,0;1.5708rad)
  Radius = 1.5
FEATURE [Part::Compound] Compound032
  Links = -> [Cylinder080,Cylinder081,Cylinder082,Cylinder083]
  Placement = pos=(0,20,0) rot=(0,0,1;0rad)
FEATURE [Part::Cut] Cut058
  Base = -> Compound033
  Tool = -> Compound032
FEATURE [Part::Cut] Cut063
  Base = -> Cut058
  Tool = -> Compound034
FEATURE [Part::Cut] Cut067
  Base = -> Cut063
  Tool = -> Compound039
FEATURE [Part::Cylinder] Cylinder300  label="Válec300"
  Angle = 360
  AttacherType = Attacher::AttachEngine3D
  Height = 80
  Placement = pos=(38,-32,-7) rot=(1,0,0;1.5708rad)
  Radius = 1.5
FEATURE [Part::Cylinder] Cylinder301  label="Válec301"
  Angle = 360
  AttacherType = Attacher::AttachEngine3D
  Height = 80
  Placement = pos=(-4,-32,27) rot=(1,0,0;1.5708rad)
  Radius = 1.5
FEATURE [Part::Cylinder] Cylinder302  label="Válec302"
  Angle = 360
  AttacherType = Attacher::AttachEngine3D
  Height = 80
  Placement = pos=(-4,-32,-7) rot=(1,0,0;1.5708rad)
  Radius = 1.5
FEATURE [Part::Cylinder] Cylinder303  label="Válec303"
  Angle = 360
  AttacherType = Attacher::AttachEngine3D
  Height = 80
  Placement = pos=(38,-32,27) rot=(1,0,0;1.5708rad)
  Radius = 1.5
FEATURE [Part::Compound] Compound132
  Links = -> [Cylinder301,Cylinder302,Cylinder303,Cylinder300]
  Placement = pos=(0,20,0) rot=(0,0,1;0rad)
FEATURE [Part::Cut] Cut189
  Base = -> Cut067
  Tool = -> Compound132
FEATURE [Part::Cylinder] Cylinder304  label="Válec304"
  Angle = 360
  AttacherType = Attacher::AttachEngine3D
  Height = 3
  Placement = pos=(38,-32,27) rot=(1,0,0;1.5708rad)
  Radius = 3
FEATURE [Part::Cylinder] Cylinder305  label="Válec305"
  Angle = 360
  AttacherType = Attacher::AttachEngine3D
  Height = 3
  Placement = pos=(-4,-32,-7) rot=(1,0,0;1.5708rad)
  Radius = 3
FEATURE [Part::Cylinder] Cylinder306  label="Válec306"
  Angle = 360
  AttacherType = Attacher::AttachEngine3D
  Height = 3
  Placement = pos=(-4,-32,27) rot=(1,0,0;1.5708rad)
  Radius = 3
FEATURE [Part::Cylinder] Cylinder307  label="Válec307"
  Angle = 360
  AttacherType = Attacher::AttachEngine3D
  Height = 3
  Placement = pos=(38,-32,-7) rot=(1,0,0;1.5708rad)
  Radius = 3
FEATURE [Part::Compound] Compound133
  Links = -> [Cylinder306,Cylinder305,Cylinder304,Cylinder307]
  Placement = pos=(0,17,0) rot=(0,0,1;0rad)
FEATURE [Part::Cylinder] Cylinder308  label="Válec308"
  Angle = 360
  AttacherType = Attacher::AttachEngine3D
  Height = 50
  Placement = pos=(38,-32,-7) rot=(1,0,0;1.5708rad)
  Radius = 1.5
FEATURE [Part::Cylinder] Cylinder309  label="Válec309"
  Angle = 360
  AttacherType = Attacher::AttachEngine3D
  Height = 50
  Placement = pos=(-4,-32,27) rot=(1,0,0;1.5708rad)
  Radius = 1.5
FEATURE [Part::Cylinder] Cylinder310  label="Válec310"
  Angle = 360
  AttacherType = Attacher::AttachEngine3D
  Height = 50
  Placement = pos=(-4,-32,-7) rot=(1,0,0;1.5708rad)
  Radius = 1.5
FEATURE [Part::Cylinder] Cylinder311  label="Válec311"
  Angle = 360
  AttacherType = Attacher::AttachEngine3D
  Height = 50
  Placement = pos=(38,-32,27) rot=(1,0,0;1.5708rad)
  Radius = 1.5
FEATURE [Part::Compound] Compound134
  Links = -> [Cylinder309,Cylinder310,Cylinder311,Cylinder308]
  Placement = pos=(0,20,0) rot=(0,0,1;0rad)
FEATURE [Part::Compound] Compound135
  Links = -> [Box204,Box205]
FEATURE [Part::Cut] Cut190
  Base = -> Compound135
  Tool = -> Compound134
FEATURE [Part::Cut] Cut191
  Base = -> Cut190
  Tool = -> Compound133
FEATURE [Part::Chamfer] Chamfer013
  Base = -> Cut066
  Edges = 2 edges r=4: [Edge25,Edge53]
FEATURE [Part::Chamfer] Chamfer014
  Base = -> Cut064
  Edges = 1 edges r=4: [Edge22]
FEATURE [Part::Chamfer] Chamfer015
  Base = -> Chamfer013
  Edges = 2 edges r=4: [Edge23,Edge57]
FEATURE [Part::Chamfer] Chamfer016
  Base = -> Chamfer014
  Edges = 1 edges r=4: [Edge9]
FEATURE [Part::FeaturePython] Tube014  # WARN: FeaturePython — macro-defined, semantics opaque (R4)
  AttacherType = Attacher::AttachEngine3D
  Height = 8
  InnerRadius = 59
  OuterRadius = 64
  Placement = pos=(37,-1.5,6) rot=(0,0,1;0rad)
FEATURE [Part::Cylinder] Cylinder312  label="Válec312"
  Angle = 360
  AttacherType = Attacher::AttachEngine3D
  Height = 8
  Placement = pos=(-13,-25,6) rot=(0,0,1;0rad)
  Radius = 5
FEATURE [Part::Cylinder] Cylinder313  label="Válec313"
  Angle = 360
  AttacherType = Attacher::AttachEngine3D
  Height = 12
  Placement = pos=(-13,-25,4) rot=(0,0,1;0rad)
  Radius = 2.65
FEATURE [Part::Cut] Cut198
  Base = -> Cylinder312
  Placement = pos=(12,-22,0) rot=(0,0,1;0rad)
  Tool = -> Cylinder313
FEATURE [Part::Cylinder] Cylinder314  label="Válec314"
  Angle = 360
  AttacherType = Attacher::AttachEngine3D
  Height = 12
  Placement = pos=(-10,30,4) rot=(0,0,1;0rad)
  Radius = 2.65
FEATURE [Part::Box] Box206  label="Krychle206"
  AttacherType = Attacher::AttachEngine3D
  Height = 20
  Length = 100
  Placement = pos=(36,0,0) rot=(0,0,1;1.01229rad)
  Width = 100
FEATURE [Part::Box] Box207  label="Krychle207"
  AttacherType = Attacher::AttachEngine3D
  Height = 20
  Length = 100
  Placement = pos=(36,0,0) rot=(0,0,-1;1.16937rad)
  Width = 100
FEATURE [Part::Cylinder] Cylinder315  label="Válec315"
  Angle = 360
  AttacherType = Attacher::AttachEngine3D
  Height = 12
  Placement = pos=(-1,-47,4) rot=(0,0,1;0rad)
  Radius = 2.65
FEATURE [Part::Box] Box208  label="Krychle208"
  AttacherType = Attacher::AttachEngine3D
  Height = 20
  Length = 100
  Placement = pos=(36,0,0) rot=(0,0,1;4.04916rad)
  Width = 100
FEATURE [Part::Box] Box209  label="Krychle209"
  AttacherType = Attacher::AttachEngine3D
  Height = 20
  Length = 100
  Placement = pos=(36,0,0) rot=(0,0,-1;0.401426rad)
  Width = 100
FEATURE [Part::Cylinder] Cylinder316  label="Válec316"
  Angle = 360
  AttacherType = Attacher::AttachEngine3D
  Height = 12
  Placement = pos=(-13,30,4) rot=(0,0,1;0rad)
  Radius = 2.65
FEATURE [Part::Compound] Compound139
  Links = -> [Cylinder316,Cylinder315]
FEATURE [Part::Cut] Cut196
  Base = -> Tube014
  Tool = -> Compound139
FEATURE [Part::Cut] Cut193
  Base = -> Cut196
  Tool = -> Box206
FEATURE [Part::Cut] Cut194
  Base = -> Cut193
  Tool = -> Box209
FEATURE [Part::Cut] Cut192
  Base = -> Cut194
  Tool = -> Box207
FEATURE [Part::Cut] Cut195
  Base = -> Cut192
  Tool = -> Box208
FEATURE [Part::Cylinder] Cylinder317  label="Válec317"
  Angle = 360
  AttacherType = Attacher::AttachEngine3D
  Height = 8
  Placement = pos=(-10,30,6) rot=(0,0,1;0rad)
  Radius = 5
FEATURE [Part::Cut] Cut197
  Base = -> Cylinder317
  Placement = pos=(-3,0,0) rot=(0,0,1;0rad)
  Tool = -> Cylinder314
FEATURE [Part::Compound] Compound137  label="tahlo_lefto004"
  Links = -> [Cut197,Cut198]
FEATURE [Part::Compound] Compound138  label="tahlo_pruzo_superdelso"
  Links = -> [Cut195,Compound137]
FEATURE [Mesh::Feature] Mesh013  label="tahlo_pruzo_superdelso (Meshed)"
FEATURE [Part::FeaturePython] Tube015  # WARN: FeaturePython — macro-defined, semantics opaque (R4)
  AttacherType = Attacher::AttachEngine3D
  Height = 8
  InnerRadius = 58
  OuterRadius = 64
  Placement = pos=(37,-1.5,6) rot=(0,0,1;0rad)
FEATURE [Part::Cylinder] Cylinder318  label="Válec318"
  Angle = 360
  AttacherType = Attacher::AttachEngine3D
  Height = 8
  Placement = pos=(-13,-25,6) rot=(0,0,1;0rad)
  Radius = 5
FEATURE [Part::Cylinder] Cylinder319  label="Válec319"
  Angle = 360
  AttacherType = Attacher::AttachEngine3D
  Height = 12
  Placement = pos=(-13,-25,4) rot=(0,0,1;0rad)
  Radius = 2.65
FEATURE [Part::Cut] Cut205
  Base = -> Cylinder318
  Placement = pos=(5,-15,0) rot=(0,0,1;0rad)
  Tool = -> Cylinder319
FEATURE [Part::Cylinder] Cylinder320  label="Válec320"
  Angle = 360
  AttacherType = Attacher::AttachEngine3D
  Height = 12
  Placement = pos=(-10,30,4) rot=(0,0,1;0rad)
  Radius = 2.65
FEATURE [Part::Box] Box210  label="Krychle210"
  AttacherType = Attacher::AttachEngine3D
  Height = 20
  Length = 100
  Placement = pos=(36,0,0) rot=(0,0,1;1.01229rad)
  Width = 100
FEATURE [Part::Box] Box211  label="Krychle211"
  AttacherType = Attacher::AttachEngine3D
  Height = 20
  Length = 100
  Placement = pos=(36,0,0) rot=(0,0,-1;1.16937rad)
  Width = 100
FEATURE [Part::Cylinder] Cylinder321  label="Válec321"
  Angle = 360
  AttacherType = Attacher::AttachEngine3D
  Height = 12
  Placement = pos=(-8,-40,4) rot=(0,0,1;0rad)
  Radius = 2.65
FEATURE [Part::Box] Box212  label="Krychle212"
  AttacherType = Attacher::AttachEngine3D
  Height = 20
  Length = 100
  Placement = pos=(36,0,0) rot=(0,0,1;3.89208rad)
  Width = 100
FEATURE [Part::Box] Box213  label="Krychle213"
  AttacherType = Attacher::AttachEngine3D
  Height = 20
  Length = 100
  Placement = pos=(36,0,0) rot=(0,0,-1;0.401426rad)
  Width = 100
FEATURE [Part::Cylinder] Cylinder322  label="Válec322"
  Angle = 360
  AttacherType = Attacher::AttachEngine3D
  Height = 12
  Placement = pos=(-13,30,4) rot=(0,0,1;0rad)
  Radius = 2.65
FEATURE [Part::Compound] Compound142
  Links = -> [Cylinder322,Cylinder321]
FEATURE [Part::Cut] Cut203
  Base = -> Tube015
  Tool = -> Compound142
FEATURE [Part::Cut] Cut200
  Base = -> Cut203
  Tool = -> Box210
FEATURE [Part::Cut] Cut201
  Base = -> Cut200
  Tool = -> Box213
FEATURE [Part::Cut] Cut199
  Base = -> Cut201
  Tool = -> Box211
FEATURE [Part::Cut] Cut202
  Base = -> Cut199
  Tool = -> Box212
FEATURE [Part::Cylinder] Cylinder323  label="Válec323"
  Angle = 360
  AttacherType = Attacher::AttachEngine3D
  Height = 8
  Placement = pos=(-10,30,6) rot=(0,0,1;0rad)
  Radius = 5
FEATURE [Part::Cut] Cut204
  Base = -> Cylinder323
  Placement = pos=(-3,0,0) rot=(0,0,1;0rad)
  Tool = -> Cylinder320
FEATURE [Part::Compound] Compound140  label="tahlo_lefto005"
  Links = -> [Cut204,Cut205]
FEATURE [Part::Compound] Compound141  label="tahlo_pruzo_delso_silo"
  Links = -> [Cut202,Compound140]
FEATURE [Mesh::Feature] Mesh014  label="tahlo_pruzo_delso_silo (Meshed)"
FEATURE [Part::Cylinder] Cylinder324  label="Válec324"
  Angle = 360
  AttacherType = Attacher::AttachEngine3D
  Height = 20
  Placement = pos=(39,-17,10) rot=(1,0,0;1.5708rad)
  Radius = 5.1
FEATURE [Part::Cylinder] Cylinder325  label="Válec325"
  Angle = 360
  AttacherType = Attacher::AttachEngine3D
  Height = 20
  Placement = pos=(-5,-17,10) rot=(1,0,0;1.5708rad)
  Radius = 5.1
FEATURE [Part::Compound] Compound143
  Links = -> [Cylinder325,Cylinder324]
FEATURE [Part::Cut] Cut206
  Base = -> Cut146
  Tool = -> Compound143
FEATURE [Part::Compound] Compound144  label="uzko_kluzno_modi"
  Links = -> [Cut167,Cut126,Cut127,Cut133,Cut134,Cut206,Cut169]
FEATURE [Mesh::Feature] Mesh015  label="uzko_kluzno_modi (Meshed)"
FEATURE [Part::Chamfer] Chamfer017
  Base = -> Cut191
  Edges = 2 edges r=3: [Edge3,Edge43]
FEATURE [Part::Chamfer] Chamfer018
  Base = -> Chamfer017
  Edges = 2 edges r=3: [Edge28,Edge73]
FEATURE [Part::Box] Box084  label="Krychle084"
  AttacherType = Attacher::AttachEngine3D
  Height = 2
  Length = 8
  Placement = pos=(18.5,20.5,-55) rot=(0,0,1;0rad)
  Width = 6
FEATURE [Part::Box] Box214  label="Krychle214"
  AttacherType = Attacher::AttachEngine3D
  Height = 2
  Length = 8
  Placement = pos=(-24.5,-22.5,-55) rot=(0,0,1;0rad)
  Width = 6
FEATURE [Part::Box] Box215  label="Krychle215"
  AttacherType = Attacher::AttachEngine3D
  Height = 2
  Length = 8
  Placement = pos=(-26.5,20.5,-55) rot=(0,0,1;0rad)
  Width = 6
FEATURE [Part::Box] Box082  label="Krychle082"
  AttacherType = Attacher::AttachEngine3D
  Height = 2
  Length = 8
  Placement = pos=(16.5,-22.5,-55) rot=(0,0,1;0rad)
  Width = 6
FEATURE [Part::Box] Box216  label="Krychle216"
  AttacherType = Attacher::AttachEngine3D
  Height = 11
  Length = 34
  Placement = pos=(-17,-17,-73) rot=(0,0,1;0rad)
  Width = 34
FEATURE [Part::Cylinder] Cylinder326  label="Válec326"
  Angle = 360
  AttacherType = Attacher::AttachEngine3D
  Height = 3
  Placement = pos=(15.5,-15.5,-54) rot=(0,0,1;0rad)
  Radius = 3
FEATURE [Part::Cylinder] Cylinder327  label="Válec327"
  Angle = 360
  AttacherType = Attacher::AttachEngine3D
  Height = 20
  Placement = pos=(15.5,-15.5,-68) rot=(0,0,1;0rad)
  Radius = 1.5
FEATURE [Part::Box] Box217  label="Krychle217"
  AttacherType = Attacher::AttachEngine3D
  Height = 8
  Length = 42.3
  Placement = pos=(-21.15,-21.15,-70) rot=(0,0,1;0rad)
  Width = 42.3
FEATURE [Part::Cylinder] Cylinder328  label="Válec328"
  Angle = 360
  AttacherType = Attacher::AttachEngine3D
  Height = 20
  Placement = pos=(10.48,15.75,-50) rot=(0,0,1;0rad)
  Radius = 1.5
FEATURE [Part::Box] Box218  label="Krychle218"
  AttacherType = Attacher::AttachEngine3D
  Height = 11
  Length = 46.3
  Placement = pos=(-23.15,-23.15,-73) rot=(0,0,1;0rad)
  Width = 46.3
FEATURE [Part::Cylinder] Cylinder329  label="Válec329"
  Angle = 360
  AttacherType = Attacher::AttachEngine3D
  Height = 3
  Placement = pos=(15.5,15.5,-54) rot=(0,0,1;0rad)
  Radius = 3
FEATURE [Part::Cylinder] Cylinder330  label="Válec330"
  Angle = 360
  AttacherType = Attacher::AttachEngine3D
  Height = 20
  Placement = pos=(-10.48,15.75,-50) rot=(0,0,1;0rad)
  Radius = 1.5
FEATURE [Part::Cylinder] Cylinder331  label="Válec331"
  Angle = 360
  AttacherType = Attacher::AttachEngine3D
  Height = 20
  Placement = pos=(15.5,-15.5,-68) rot=(0,0,1;0rad)
  Radius = 1.5
FEATURE [Part::Box] Box219  label="Krychle219"
  AttacherType = Attacher::AttachEngine3D
  Height = 8
  Length = 54
  Placement = pos=(-27,-26,-24) rot=(0,0,1;0rad)
  Width = 52
FEATURE [Part::Cylinder] Cylinder332  label="Válec332"
  Angle = 360
  AttacherType = Attacher::AttachEngine3D
  Height = 3
  Placement = pos=(-15.5,15.5,-54) rot=(0,0,1;0rad)
  Radius = 3
FEATURE [Part::Box] Box220  label="Krychle220"
  AttacherType = Attacher::AttachEngine3D
  Height = 2
  Length = 8
  Placement = pos=(-24.5,-22.5,-55) rot=(0,0,1;0rad)
  Width = 6
FEATURE [Part::Cut] Cut211
  Base = -> Box218
  Placement = pos=(0,0,7) rot=(0,0,1;0rad)
  Tool = -> Box216
FEATURE [Part::Compound] Compound147
  Links = -> [Cylinder330,Cylinder328]
  Placement = pos=(0,0,-10) rot=(0,0,1;0rad)
FEATURE [Part::Compound] Compound150
  Links = -> [Box084,Box215,Box082,Box214]
  Placement = pos=(0,0,-200) rot=(0,0,1;0rad)
FEATURE [Part::Box] Box221  label="Krychle221"
  AttacherType = Attacher::AttachEngine3D
  Height = 20
  Length = 29
  Placement = pos=(-14.5,0,-75) rot=(0,0,1;0rad)
  Width = 45.5
FEATURE [Part::Cylinder] Cylinder333  label="Válec333"
  Angle = 360
  AttacherType = Attacher::AttachEngine3D
  Height = 20
  Placement = pos=(-15.5,15.5,-68) rot=(0,0,1;0rad)
  Radius = 1.5
FEATURE [Part::Cylinder] Cylinder334  label="Válec334"
  Angle = 360
  AttacherType = Attacher::AttachEngine3D
  Height = 20
  Placement = pos=(15.5,15.5,-68) rot=(0,0,1;0rad)
  Radius = 1.5
FEATURE [Part::Cylinder] Cylinder335  label="Válec335"
  Angle = 360
  AttacherType = Attacher::AttachEngine3D
  Height = 3
  Placement = pos=(-15.5,-15.5,-54) rot=(0,0,1;0rad)
  Radius = 3
FEATURE [Part::Compound] Compound097
  Links = -> [Cylinder335,Cylinder326,Cylinder332,Cylinder329]
FEATURE [Part::Cylinder] Cylinder336  label="Válec336"
  Angle = 360
  AttacherType = Attacher::AttachEngine3D
  Height = 20
  Placement = pos=(-21,23,-28) rot=(0,0,1;0rad)
  Radius = 1.5
FEATURE [Part::Box] Box222  label="Krychle222"
  AttacherType = Attacher::AttachEngine3D
  Height = 8
  Length = 46.3
  Placement = pos=(-23.15,-23.15,-70) rot=(0,0,1;0rad)
  Width = 46.3
FEATURE [Part::Cut] Cut207
  Base = -> Box222
  Placement = pos=(0,0,-4) rot=(0,0,1;0rad)
  Tool = -> Box217
FEATURE [Part::Cut] Cut212
  Base = -> Cut207
  Tool = -> Box221
FEATURE [Part::Cylinder] Cylinder337  label="Válec337"
  Angle = 360
  AttacherType = Attacher::AttachEngine3D
  Height = 20
  Placement = pos=(21,23,-28) rot=(0,0,1;0rad)
  Radius = 1.5
FEATURE [Part::Box] Box223  label="Krychle223"
  AttacherType = Attacher::AttachEngine3D
  Height = 2
  Length = 8
  Placement = pos=(16.5,-22.5,-55) rot=(0,0,1;0rad)
  Width = 6
FEATURE [Part::Box] Box224  label="Krychle224"
  AttacherType = Attacher::AttachEngine3D
  Height = 2
  Length = 8
  Placement = pos=(16.5,16.5,-55) rot=(0,0,1;0rad)
  Width = 6
FEATURE [Part::Cylinder] Cylinder338  label="Válec338"
  Angle = 360
  AttacherType = Attacher::AttachEngine3D
  Height = 20
  Placement = pos=(15.5,15.5,-68) rot=(0,0,1;0rad)
  Radius = 1.5
FEATURE [Part::Box] Box225  label="Krychle225"
  AttacherType = Attacher::AttachEngine3D
  Height = 20
  Length = 29
  Placement = pos=(-14.5,0,-75) rot=(0,0,1;0rad)
  Width = 45.5
FEATURE [Part::Box] Box226  label="Krychle226"
  AttacherType = Attacher::AttachEngine3D
  Height = 2
  Length = 8
  Placement = pos=(-24.5,16.5,-55) rot=(0,0,1;0rad)
  Width = 6
FEATURE [Part::Compound] Compound146
  Links = -> [Box224,Box226,Box223,Box220]
  Placement = pos=(0,0,10) rot=(0,0,1;0rad)
FEATURE [Part::Cylinder] Cylinder339  label="Válec339"
  Angle = 360
  AttacherType = Attacher::AttachEngine3D
  Height = 20
  Placement = pos=(-15.5,-15.5,-68) rot=(0,0,1;0rad)
  Radius = 1.5
FEATURE [Part::Cylinder] Cylinder340  label="Válec340"
  Angle = 360
  AttacherType = Attacher::AttachEngine3D
  Height = 20
  Placement = pos=(21,-23,-28) rot=(0,0,1;0rad)
  Radius = 1.5
FEATURE [Part::Cylinder] Cylinder341  label="Válec341"
  Angle = 360
  AttacherType = Attacher::AttachEngine3D
  Height = 20
  Placement = pos=(-15.5,-15.5,-68) rot=(0,0,1;0rad)
  Radius = 1.5
FEATURE [Part::Compound] Compound151
  Links = -> [Cylinder334,Cylinder333,Cylinder331,Cylinder341]
FEATURE [Part::Cut] Cut208
  Base = -> Cut211
  Tool = -> Compound151
FEATURE [Part::Cut] Cut209
  Base = -> Cut208
  Tool = -> Box225
FEATURE [Part::Cylinder] Cylinder342  label="Válec342"
  Angle = 360
  AttacherType = Attacher::AttachEngine3D
  Height = 20
  Placement = pos=(-15.5,15.5,-68) rot=(0,0,1;0rad)
  Radius = 1.5
FEATURE [Part::Compound] Compound153
  Links = -> [Cylinder338,Cylinder342,Cylinder327,Cylinder339]
  Placement = pos=(0,0,4) rot=(0,0,1;0rad)
FEATURE [Part::Cylinder] Cylinder343  label="Válec343"
  Angle = 360
  AttacherType = Attacher::AttachEngine3D
  Height = 8
  Placement = pos=(-15.15,15.15,-74) rot=(0,0,1;0rad)
  Radius = 6
FEATURE [Part::Box] Box227  label="Krychle227"
  AttacherType = Attacher::AttachEngine3D
  Height = 8
  Length = 7
  Placement = pos=(-22,15,-74) rot=(0,0,1;0rad)
  Width = 7
FEATURE [Part::Cylinder] Cylinder344  label="Válec344"
  Angle = 360
  AttacherType = Attacher::AttachEngine3D
  Height = 20
  Placement = pos=(19.5,19.5,-28) rot=(0,0,1;0rad)
  Radius = 1.5
FEATURE [Part::Cylinder] Cylinder345  label="Válec345"
  Angle = 360
  AttacherType = Attacher::AttachEngine3D
  Height = 50
  Placement = pos=(0,0,-29) rot=(0,0,1;0rad)
  Radius = 8
FEATURE [Part::Cut] Cut214
  Base = -> Box219
  Tool = -> Cylinder345
FEATURE [Part::Cylinder] Cylinder346  label="Válec346"
  Angle = 360
  AttacherType = Attacher::AttachEngine3D
  Height = 20
  Placement = pos=(-19.5,-19.5,-28) rot=(0,0,1;0rad)
  Radius = 1.5
FEATURE [Part::Cylinder] Cylinder347  label="Válec347"
  Angle = 360
  AttacherType = Attacher::AttachEngine3D
  Height = 20
  Placement = pos=(-19.5,19.5,-28) rot=(0,0,1;0rad)
  Radius = 1.5
FEATURE [Part::Cylinder] Cylinder348  label="Válec348"
  Angle = 360
  AttacherType = Attacher::AttachEngine3D
  Height = 20
  Placement = pos=(-21,-23,-28) rot=(0,0,1;0rad)
  Radius = 1.5
FEATURE [Part::Compound] Compound152
  Links = -> [Cylinder348,Cylinder337,Cylinder336,Cylinder340]
FEATURE [Part::Cut] Cut213
  Base = -> Cut214
  Tool = -> Compound152
FEATURE [Part::Compound] Compound155
  Links = -> [Cut213]
  Placement = pos=(0,0,-30) rot=(0,0,1;0rad)
FEATURE [Part::Cut] Cut215
  Base = -> Compound155
  Tool = -> Compound146
FEATURE [Part::Cut] Cut210
  Base = -> Cut215
  Tool = -> Compound147
FEATURE [Part::Cut] Cut216
  Base = -> Cut210
  Tool = -> Compound153
FEATURE [Part::Cylinder] Cylinder349  label="Válec349"
  Angle = 360
  AttacherType = Attacher::AttachEngine3D
  Height = 20
  Placement = pos=(19.5,-19.5,-28) rot=(0,0,1;0rad)
  Radius = 1.5
FEATURE [Part::Compound] Compound148
  Links = -> [Cylinder346,Cylinder347,Cylinder349,Cylinder344]
  Placement = pos=(0,0,-33) rot=(0,0,1;0rad)
FEATURE [Part::Cut] Cut217
  Base = -> Cut216
  Placement = pos=(17,-127,10) rot=(1,0,0;1.5708rad)
  Tool = -> Compound097
FEATURE [Part::Cut] Cut218
  Base = -> Box227
  Placement = pos=(0,0,0) rot=(0,0,1;3.14159rad)
  Tool = -> Cylinder343
FEATURE [Part::Cut] Cut219
  Base = -> Box227
  Placement = pos=(0,0,0) rot=(0,0,-1;1.5708rad)
  Tool = -> Cylinder343
FEATURE [Part::Cut] Cut220
  Base = -> Cut209
  Tool = -> Compound150
FEATURE [Part::Cut] Cut221
  Base = -> Box227
  Placement = pos=(0,0,0) rot=(0,0,1;1.5708rad)
  Tool = -> Cylinder343
FEATURE [Part::Cut] Cut222
  Base = -> Cut220
  Placement = pos=(17,-24,10) rot=(-1,0,0;1.5708rad)
  Tool = -> Compound148
FEATURE [Part::Cut] Cut223
  Base = -> Box227
  Tool = -> Cylinder343
FEATURE [Part::Compound] Compound149
  Links = -> [Cut223,Cut221,Cut218,Cut219]
FEATURE [Part::Cylinder] Cylinder350  label="Válec350"
  Angle = 360
  AttacherType = Attacher::AttachEngine3D
  Height = 40
  Placement = pos=(-19.5,19.5,-28) rot=(0,0,1;0rad)
  Radius = 1.5
FEATURE [Part::Cylinder] Cylinder351  label="Válec351"
  Angle = 360
  AttacherType = Attacher::AttachEngine3D
  Height = 40
  Placement = pos=(19.5,-19.5,-28) rot=(0,0,1;0rad)
  Radius = 1.5
FEATURE [Part::Cylinder] Cylinder352  label="Válec352"
  Angle = 360
  AttacherType = Attacher::AttachEngine3D
  Height = 40
  Placement = pos=(19.5,19.5,-28) rot=(0,0,1;0rad)
  Radius = 1.5
FEATURE [Part::Cylinder] Cylinder353  label="Válec353"
  Angle = 360
  AttacherType = Attacher::AttachEngine3D
  Height = 40
  Placement = pos=(-19.5,-19.5,-28) rot=(0,0,1;0rad)
  Radius = 1.5
FEATURE [Part::Compound] Compound156
  Links = -> [Cylinder353,Cylinder350,Cylinder351,Cylinder352]
  Placement = pos=(0,0,-47) rot=(0,0,1;0rad)
FEATURE [Part::Cylinder] Cylinder354  label="Válec354"
  Angle = 360
  AttacherType = Attacher::AttachEngine3D
  Height = 6
  Placement = pos=(21,23,-28) rot=(0,0,1;0rad)
  Radius = 3
FEATURE [Part::Cylinder] Cylinder355  label="Válec355"
  Angle = 360
  AttacherType = Attacher::AttachEngine3D
  Height = 6
  Placement = pos=(-21,23,-28) rot=(0,0,1;0rad)
  Radius = 3
FEATURE [Part::Cylinder] Cylinder356  label="Válec356"
  Angle = 360
  AttacherType = Attacher::AttachEngine3D
  Height = 6
  Placement = pos=(21,-23,-28) rot=(0,0,1;0rad)
  Radius = 3
FEATURE [Part::Cylinder] Cylinder357  label="Válec357"
  Angle = 360
  AttacherType = Attacher::AttachEngine3D
  Height = 6
  Placement = pos=(-21,-23,-28) rot=(0,0,1;0rad)
  Radius = 3
FEATURE [Part::Compound] Compound157
  Links = -> [Cylinder357,Cylinder354,Cylinder355,Cylinder356]
  Placement = pos=(17,-91,10) rot=(1,0,0;1.5708rad)
FEATURE [Part::Box] Box228  label="Krychle228"
  AttacherType = Attacher::AttachEngine3D
  Height = 6
  Length = 12
  Placement = pos=(-10,-73,-16) rot=(0,0,1;0rad)
  Width = 4
FEATURE [Part::Box] Box230  label="Krychle230"
  AttacherType = Attacher::AttachEngine3D
  Height = 6
  Length = 12
  Placement = pos=(-10,-69,-16) rot=(0,0,1;0rad)
  Width = 6
FEATURE [Part::Chamfer] Chamfer019
  Base = -> Box230
  Edges = 1 edges r=5.6: [Edge11]
FEATURE [Part::Compound] Compound158
  Links = -> [Box228,Chamfer019]
FEATURE [Part::Box] Box231  label="Krychle231"
  AttacherType = Attacher::AttachEngine3D
  Height = 6
  Length = 12
  Placement = pos=(-10,-73,-16) rot=(0,0,1;0rad)
  Width = 4
FEATURE [Part::Box] Box232  label="Krychle232"
  AttacherType = Attacher::AttachEngine3D
  Height = 6
  Length = 12
  Placement = pos=(-10,-69,-16) rot=(0,0,1;0rad)
  Width = 6
FEATURE [Part::Chamfer] Chamfer020
  Base = -> Box232
  Edges = 1 edges r=5.6: [Edge11]
FEATURE [Part::Compound] Compound159
  Links = -> [Box231,Chamfer020]
  Placement = pos=(42,0,0) rot=(0,0,1;0rad)
FEATURE [Part::Box] Box233  label="Krychle233"
  AttacherType = Attacher::AttachEngine3D
  Height = 6
  Length = 12
  Placement = pos=(-10,-73,30) rot=(0,0,1;0rad)
  Width = 4
FEATURE [Part::Box] Box234  label="Krychle234"
  AttacherType = Attacher::AttachEngine3D
  Height = 6
  Length = 12
  Placement = pos=(-10,-69,30) rot=(0,0,1;0rad)
  Width = 6
FEATURE [Part::Chamfer] Chamfer021
  Base = -> Box234
  Edges = 1 edges r=5.6: [Edge12]
FEATURE [Part::Compound] Compound160
  Links = -> [Box233,Chamfer021]
FEATURE [Part::Box] Box235  label="Krychle235"
  AttacherType = Attacher::AttachEngine3D
  Height = 6
  Length = 12
  Placement = pos=(-10,-69,30) rot=(0,0,1;0rad)
  Width = 6
FEATURE [Part::Box] Box236  label="Krychle236"
  AttacherType = Attacher::AttachEngine3D
  Height = 6
  Length = 12
  Placement = pos=(-10,-73,30) rot=(0,0,1;0rad)
  Width = 4
FEATURE [Part::Chamfer] Chamfer022
  Base = -> Box235
  Edges = 1 edges r=5.6: [Edge12]
FEATURE [Part::Compound] Compound161
  Links = -> [Box236,Chamfer022]
  Placement = pos=(42,0,0) rot=(0,0,1;0rad)
FEATURE [Part::Compound] Compound162
  Links = -> [Compound158,Compound161,Compound160,Compound159]
FEATURE [Part::Cut] Cut224
  Base = -> Compound162
  Tool = -> Compound157
FEATURE [Part::Cylinder] Cylinder358  label="Válec358"
  Angle = 360
  AttacherType = Attacher::AttachEngine3D
  Height = 10
  Placement = pos=(21,23,-28) rot=(0,0,1;0rad)
  Radius = 1.5
FEATURE [Part::Cylinder] Cylinder359  label="Válec359"
  Angle = 360
  AttacherType = Attacher::AttachEngine3D
  Height = 10
  Placement = pos=(-21,23,-28) rot=(0,0,1;0rad)
  Radius = 1.5
FEATURE [Part::Cylinder] Cylinder360  label="Válec360"
  Angle = 360
  AttacherType = Attacher::AttachEngine3D
  Height = 10
  Placement = pos=(21,-23,-28) rot=(0,0,1;0rad)
  Radius = 1.5
FEATURE [Part::Cylinder] Cylinder361  label="Válec361"
  Angle = 360
  AttacherType = Attacher::AttachEngine3D
  Height = 10
  Placement = pos=(-21,-23,-28) rot=(0,0,1;0rad)
  Radius = 1.5
FEATURE [Part::Compound] Compound163
  Links = -> [Cylinder361,Cylinder358,Cylinder359,Cylinder360]
  Placement = pos=(17,-95,10) rot=(1,0,0;1.5708rad)
FEATURE [Part::Cut] Cut225
  Base = -> Cut224
  Tool = -> Compound163
FEATURE [Part::Cylinder] Cylinder362  label="Válec362"
  Angle = 360
  AttacherType = Attacher::AttachEngine3D
  Height = 3
  Placement = pos=(38,-32,-7) rot=(1,0,0;1.5708rad)
  Radius = 3
FEATURE [Part::Cylinder] Cylinder363  label="Válec363"
  Angle = 360
  AttacherType = Attacher::AttachEngine3D
  Height = 3
  Placement = pos=(38,-32,27) rot=(1,0,0;1.5708rad)
  Radius = 3
FEATURE [Part::Cylinder] Cylinder364  label="Válec364"
  Angle = 360
  AttacherType = Attacher::AttachEngine3D
  Height = 3
  Placement = pos=(-4,-32,27) rot=(1,0,0;1.5708rad)
  Radius = 3
FEATURE [Part::Cylinder] Cylinder365  label="Válec365"
  Angle = 360
  AttacherType = Attacher::AttachEngine3D
  Height = 3
  Placement = pos=(-4,-32,-7) rot=(1,0,0;1.5708rad)
  Radius = 3
FEATURE [Part::Compound] Compound164
  Links = -> [Cylinder364,Cylinder365,Cylinder363,Cylinder362]
  Placement = pos=(0,-38,0) rot=(0,0,1;0rad)
FEATURE [Part::Cut] Cut226
  Base = -> Cut189
  Tool = -> Compound164
FEATURE [Part::Cylinder] Cylinder366  label="Válec366"
  Angle = 360
  AttacherType = Attacher::AttachEngine3D
  Height = 10
  Placement = pos=(21,23,-28) rot=(0,0,1;0rad)
  Radius = 1.5
FEATURE [Part::Cylinder] Cylinder367  label="Válec367"
  Angle = 360
  AttacherType = Attacher::AttachEngine3D
  Height = 10
  Placement = pos=(-21,23,-28) rot=(0,0,1;0rad)
  Radius = 1.5
FEATURE [Part::Cylinder] Cylinder368  label="Válec368"
  Angle = 360
  AttacherType = Attacher::AttachEngine3D
  Height = 10
  Placement = pos=(21,-23,-28) rot=(0,0,1;0rad)
  Radius = 1.5
FEATURE [Part::Cylinder] Cylinder369  label="Válec369"
  Angle = 360
  AttacherType = Attacher::AttachEngine3D
  Height = 10
  Placement = pos=(-21,-23,-28) rot=(0,0,1;0rad)
  Radius = 1.5
FEATURE [Part::Compound] Compound166
  Links = -> [Cylinder369,Cylinder366,Cylinder367,Cylinder368]
  Placement = pos=(17,-95,10) rot=(1,0,0;1.5708rad)
FEATURE [Part::Box] Box237  label="Krychle237"
  AttacherType = Attacher::AttachEngine3D
  Height = 2
  Length = 6
  Placement = pos=(25,19,-55) rot=(0,0,1;0rad)
  Width = 8
FEATURE [Part::Box] Box238  label="Krychle238"
  AttacherType = Attacher::AttachEngine3D
  Height = 2
  Length = 6
  Placement = pos=(-17,-25,-55) rot=(0,0,1;0rad)
  Width = 8
FEATURE [Part::Box] Box239  label="Krychle239"
  AttacherType = Attacher::AttachEngine3D
  Height = 2
  Length = 6
  Placement = pos=(-17,19,-55) rot=(0,0,1;0rad)
  Width = 8
FEATURE [Part::Box] Box240  label="Krychle240"
  AttacherType = Attacher::AttachEngine3D
  Height = 2
  Length = 6
  Placement = pos=(25,-25,-55) rot=(0,0,1;0rad)
  Width = 8
FEATURE [Part::Compound] Compound167
  Links = -> [Box237,Box239,Box240,Box238]
  Placement = pos=(10,-24,11) rot=(-1,0,0;1.5708rad)
FEATURE [Part::Compound] Compound168
  Links = -> [Compound149,Cut212]
  Placement = pos=(17,-24,10) rot=(-1,0,0;1.5708rad)
FEATURE [Part::Compound] Compound169
  Links = -> [Cut222,Compound168]
  Placement = pos=(34,-2,20) rot=(0,1,0;3.14159rad)
FEATURE [Part::Cut] Cut227
  Base = -> Cut217
  Tool = -> Compound167
FEATURE [Part::Chamfer] Chamfer023
  Base = -> Cut227
  Edges = 1 edges r=3: [Edge17]
FEATURE [Part::Chamfer] Chamfer024
  Base = -> Chamfer023
  Edges = 1 edges r=3: [Edge33]
FEATURE [Part::Cylinder] Cylinder370  label="Válec370"
  Angle = 360
  AttacherType = Attacher::AttachEngine3D
  Height = 6
  Placement = pos=(0,0,39) rot=(0,0,1;0rad)
  Radius = 30
FEATURE [Part::Box] Box241  label="Krychle241"
  AttacherType = Attacher::AttachEngine3D
  Height = 20
  Length = 42.3
  Placement = pos=(-21.15,-38.15,45) rot=(0,0,1;0rad)
  Width = 80
FEATURE [Part::Cylinder] Cylinder371  label="Válec371"
  Angle = 360
  AttacherType = Attacher::AttachEngine3D
  Height = 14
  Placement = pos=(0,0,45) rot=(0,0,1;0rad)
  Radius = 30
FEATURE [Part::Cut] Cut228
  Base = -> Cylinder371
  Placement = pos=(0,0,3) rot=(0,0,1;0rad)
  Tool = -> Box241
FEATURE [Part::Cylinder] Cylinder372  label="Válec372"
  Angle = 360
  AttacherType = Attacher::AttachEngine3D
  Height = 60
  Placement = pos=(-20.3253,-8.41904,34) rot=(0,0,1;1.96349rad)
  Radius = 1.5
FEATURE [Part::Cylinder] Cylinder373  label="Válec373"
  Angle = 360
  AttacherType = Attacher::AttachEngine3D
  Height = 60
  Placement = pos=(20.3253,8.41904,34) rot=(0,0,-1;1.1781rad)
  Radius = 1.5
FEATURE [Part::Cylinder] Cylinder374  label="Válec374"
  Angle = 360
  AttacherType = Attacher::AttachEngine3D
  Height = 60
  Placement = pos=(-8.41904,20.3253,34) rot=(0,0,1;0.392699rad)
  Radius = 1.5
FEATURE [Part::Cylinder] Cylinder375  label="Válec375"
  Angle = 360
  AttacherType = Attacher::AttachEngine3D
  Height = 60
  Placement = pos=(8.41904,-20.3253,34) rot=(0,0,1;3.53429rad)
  Radius = 1.5
FEATURE [Part::Compound] Compound170
  Links = -> [Cylinder374,Cylinder372,Cylinder375,Cylinder373]
  Placement = pos=(0,0,0) rot=(0,0,1;0.392699rad)
FEATURE [Part::Cylinder] Cylinder376  label="Válec376"
  Angle = 360
  AttacherType = Attacher::AttachEngine3D
  Height = 3
  Placement = pos=(-20.3253,-8.41904,34) rot=(0,0,1;1.96349rad)
  Radius = 3
FEATURE [Part::Cylinder] Cylinder377  label="Válec377"
  Angle = 360
  AttacherType = Attacher::AttachEngine3D
  Height = 3
  Placement = pos=(8.41904,-20.3253,34) rot=(0,0,1;3.53429rad)
  Radius = 3
FEATURE [Part::Cylinder] Cylinder378  label="Válec378"
  Angle = 360
  AttacherType = Attacher::AttachEngine3D
  Height = 3
  Placement = pos=(20.3253,8.41904,34) rot=(0,0,-1;1.1781rad)
  Radius = 3
FEATURE [Part::Cylinder] Cylinder379  label="Válec379"
  Angle = 360
  AttacherType = Attacher::AttachEngine3D
  Height = 3
  Placement = pos=(-8.41904,20.3253,34) rot=(0,0,1;0.392699rad)
  Radius = 3
FEATURE [Part::Compound] Compound171
  Links = -> [Cylinder379,Cylinder376,Cylinder377,Cylinder378]
  Placement = pos=(0,0,8) rot=(0,0,1;0.392699rad)
FEATURE [Part::Cut] Cut229
  Base = -> Cylinder370
  Placement = pos=(0,0,3) rot=(0,0,1;0rad)
  Tool = -> Compound171
FEATURE [Part::Cut] Cut230
  Base = -> Cut229
  Tool = -> Compound170
FEATURE [Part::Box] Box242  label="Krychle242"
  AttacherType = Attacher::AttachEngine3D
  Height = 20
  Length = 10
  Placement = pos=(-35,-38.15,45) rot=(0,0,1;0rad)
  Width = 80
FEATURE [Part::Box] Box243  label="Krychle243"
  AttacherType = Attacher::AttachEngine3D
  Height = 20
  Length = 10
  Placement = pos=(25,-38.15,45) rot=(0,0,1;0rad)
  Width = 80
FEATURE [Part::Compound] Compound104
  Links = -> [Box242,Box243]
FEATURE [Part::Cut] Cut231
  Base = -> Cut228
  Tool = -> Compound104
FEATURE [Part::Box] Box244  label="Krychle244"
  AttacherType = Attacher::AttachEngine3D
  Height = 6
  Length = 2
  Placement = pos=(-24,8,52) rot=(0,0,1;0rad)
  Width = 14
FEATURE [Part::Box] Box245  label="Krychle245"
  AttacherType = Attacher::AttachEngine3D
  Height = 6
  Length = 2
  Placement = pos=(-24,-22,52) rot=(0,0,1;0rad)
  Width = 14
FEATURE [Part::Box] Box246  label="Krychle246"
  AttacherType = Attacher::AttachEngine3D
  Height = 6
  Length = 2
  Placement = pos=(22,8,52) rot=(0,0,1;0rad)
  Width = 14
FEATURE [Part::Box] Box247  label="Krychle247"
  AttacherType = Attacher::AttachEngine3D
  Height = 6
  Length = 2
  Placement = pos=(22,-20,52) rot=(0,0,1;0rad)
  Width = 14
FEATURE [Part::Cylinder] Cylinder380  label="Válec380"
  Angle = 360
  AttacherType = Attacher::AttachEngine3D
  Height = 10
  Placement = pos=(-28,12,55) rot=(0,1,0;1.5708rad)
  Radius = 1.5
FEATURE [Part::Cylinder] Cylinder381  label="Válec381"
  Angle = 360
  AttacherType = Attacher::AttachEngine3D
  Height = 10
  Placement = pos=(-28,-12,55) rot=(0,1,0;1.5708rad)
  Radius = 1.5
FEATURE [Part::Cylinder] Cylinder382  label="Válec382"
  Angle = 360
  AttacherType = Attacher::AttachEngine3D
  Height = 10
  Placement = pos=(18,12,55) rot=(0,1,0;1.5708rad)
  Radius = 1.5
FEATURE [Part::Cylinder] Cylinder383  label="Válec383"
  Angle = 360
  AttacherType = Attacher::AttachEngine3D
  Height = 10
  Placement = pos=(18,-12,55) rot=(0,1,0;1.5708rad)
  Radius = 1.5
FEATURE [Part::Compound] Compound172
  Links = -> [Cylinder380,Cylinder381,Cylinder382,Cylinder383]
FEATURE [Part::Box] Box248  label="Krychle248"
  AttacherType = Attacher::AttachEngine3D
  Height = 20
  Length = 10
  Placement = pos=(-35,-38.15,45) rot=(0,0,1;0rad)
  Width = 80
FEATURE [Part::Box] Box249  label="Krychle249"
  AttacherType = Attacher::AttachEngine3D
  Height = 20
  Length = 10
  Placement = pos=(25,-38.15,45) rot=(0,0,1;0rad)
  Width = 80
FEATURE [Part::Cylinder] Cylinder384  label="Válec384"
  Angle = 360
  AttacherType = Attacher::AttachEngine3D
  Height = 20
  Placement = pos=(0,0,37) rot=(0,0,1;0rad)
  Radius = 16
FEATURE [Part::Compound] Compound173
  Links = -> [Box244,Box245,Box246,Box247]
FEATURE [Part::Compound] Compound174
  Links = -> [Box248,Box249]
  Placement = pos=(0,0,-8) rot=(0,0,1;0rad)
FEATURE [Part::Cut] Cut232
  Base = -> Cut230
  Tool = -> Compound174
FEATURE [Part::Cut] Cut233
  Base = -> Cut231
  Tool = -> Compound172
FEATURE [Part::Cut] Cut234
  Base = -> Cut233
  Tool = -> Compound173
FEATURE [Part::Compound] Compound175
  Links = -> [Cut232,Cut234]
FEATURE [Part::Chamfer] Chamfer025
  Base = -> Compound175
  Edges = 2 edges r=1.2: [Edge54,Edge89]
FEATURE [Part::Chamfer] Chamfer010
  Base = -> Chamfer025
  Edges = 2 edges r=1.2: [Edge8,Edge85]
FEATURE [Part::Cut] Cut235  label="gearovina-mini_aktuator-part-A"
  Base = -> Chamfer010
  Placement = pos=(17,-180,10) rot=(-1,0,0;1.5708rad)
  Tool = -> Cylinder384
FEATURE [Part::Box] Box250  label="Krychle250"
  AttacherType = Attacher::AttachEngine3D
  Height = 32
  Length = 4
  Placement = pos=(-12,-134,-6) rot=(0,0,1;0rad)
  Width = 56
FEATURE [Part::Cylinder] Cylinder385  label="Válec385"
  Angle = 360
  AttacherType = Attacher::AttachEngine3D
  Height = 16
  Placement = pos=(-28,12,55) rot=(0,1,0;1.5708rad)
  Radius = 1.5
FEATURE [Part::Cylinder] Cylinder386  label="Válec386"
  Angle = 360
  AttacherType = Attacher::AttachEngine3D
  Height = 16
  Placement = pos=(-28,-12,55) rot=(0,1,0;1.5708rad)
  Radius = 1.5
FEATURE [Part::Cylinder] Cylinder387  label="Válec387"
  Angle = 360
  AttacherType = Attacher::AttachEngine3D
  Height = 16
  Placement = pos=(18,12,55) rot=(0,1,0;1.5708rad)
  Radius = 1.5
FEATURE [Part::Cylinder] Cylinder388  label="Válec388"
  Angle = 360
  AttacherType = Attacher::AttachEngine3D
  Height = 16
  Placement = pos=(18,-12,55) rot=(0,1,0;1.5708rad)
  Radius = 1.5
FEATURE [Part::Compound] Compound176
  Links = -> [Cylinder385,Cylinder386,Cylinder387,Cylinder388]
  Placement = pos=(14,-71,10) rot=(1,0,0;1.5708rad)
FEATURE [Part::Box] Box251  label="Krychle251"
  AttacherType = Attacher::AttachEngine3D
  Height = 32
  Length = 2
  Placement = pos=(-8,-100,-6) rot=(0,0,1;0rad)
  Width = 20
FEATURE [Part::Box] Box252  label="Krychle252"
  AttacherType = Attacher::AttachEngine3D
  Height = 32
  Length = 2
  Placement = pos=(40,-100,-6) rot=(0,0,1;0rad)
  Width = 20
FEATURE [Part::Chamfer] Chamfer026
  Base = -> Compound169
  Edges = 2 edges r=2: [Edge3,Edge135]
FEATURE [Part::Chamfer] Chamfer027
  Base = -> Chamfer026
  Edges = 2 edges r=2: [Edge55,Edge110]
FEATURE [Part::Chamfer] Chamfer028
  Base = -> Chamfer027
  Edges = 4 edges r=2: [Edge27,Edge33,Edge93,Edge99]
FEATURE [Part::Cylinder] Cylinder389  label="Válec389"
  Angle = 360
  AttacherType = Attacher::AttachEngine3D
  Height = 20
  Placement = pos=(-5.5,-17,10) rot=(1,0,0;1.5708rad)
  Radius = 2.65
FEATURE [Part::Cylinder] Cylinder390  label="Válec390"
  Angle = 360
  AttacherType = Attacher::AttachEngine3D
  Height = 20
  Placement = pos=(39.5,-17,10) rot=(1,0,0;1.5708rad)
  Radius = 2.65
FEATURE [Part::Compound] Compound178
  Links = -> [Cylinder389,Cylinder390]
  Placement = pos=(0,-40,0) rot=(0,0,1;0rad)
FEATURE [Part::Cut] Cut236
  Base = -> Chamfer024
  Tool = -> Compound178
FEATURE [Part::Box] Box254  label="Krychle254"
  AttacherType = Attacher::AttachEngine3D
  Height = 10
  Length = 10
  Placement = pos=(20,-133,0) rot=(0,0,1;0rad)
  Width = 52
FEATURE [Part::FeaturePython] Tube016  label="podlozka_standard-5mm"  # WARN: FeaturePython — macro-defined, semantics opaque (R4)
  AttacherType = Attacher::AttachEngine3D
  Height = 1
  InnerRadius = 2.75
  OuterRadius = 4
  Placement = pos=(0,-200,0) rot=(0,0,1;0rad)
FEATURE [Part::Box] Box253  label="Krychle253"
  AttacherType = Attacher::AttachEngine3D
  Height = 32
  Length = 4
  Placement = pos=(42,-134,-6) rot=(0,0,1;0rad)
  Width = 56
FEATURE [Part::Compound] Compound177
  Links = -> [Box250,Box251,Box252,Box253]
FEATURE [Part::Cut] Cut237
  Base = -> Compound177
  Tool = -> Compound176
FEATURE [Part::Chamfer] Chamfer029
  Base = -> Cut237
  Edges = 1 edges r=2: [Edge4]
FEATURE [Part::Chamfer] Chamfer030
  Base = -> Chamfer029
  Edges = 1 edges r=2: [Edge59]
FEATURE [Part::Chamfer] Chamfer031
  Base = -> Chamfer030
  Edges = 2 edges r=3: [Edge16,Edge23]
FEATURE [Part::Chamfer] Chamfer032
  Base = -> Chamfer031
  Edges = 2 edges r=1: [Edge25,Edge27]
FEATURE [Part::Chamfer] Chamfer033
  Base = -> Chamfer032
  Edges = 2 edges r=1: [Edge33,Edge46]
FEATURE [Part::Compound] Compound179  label="grip_moto_hold"
  Links = -> [Chamfer033,Cut236,Chamfer028]
FEATURE [Part::Box] Box255  label="Krychle255"
  AttacherType = Attacher::AttachEngine3D
  Height = 2
  Length = 6
  Placement = pos=(-2,11,4) rot=(0,0,1;0rad)
  Width = 6
FEATURE [Part::Cylinder] Cylinder391  label="Válec391"
  Angle = 360
  AttacherType = Attacher::AttachEngine3D
  Height = 4
  Placement = pos=(1,14,-0.1) rot=(0,0,1;0rad)
  Radius = 1.5
FEATURE [Part::Cylinder] Cylinder392  label="Válec392"
  Angle = 360
  AttacherType = Attacher::AttachEngine3D
  Height = 12
  Placement = pos=(1,14,6) rot=(0,0,1;0rad)
  Radius = 1.5
FEATURE [Part::Compound] Compound180
  Links = -> [Box255,Cylinder392,Cylinder391]
  Placement = pos=(6,73,2) rot=(0,1,0;1.5708rad)
FEATURE [Part::Cylinder] Cylinder393  label="Válec393"
  Angle = 360
  AttacherType = Attacher::AttachEngine3D
  Height = 12
  Placement = pos=(1,14,6) rot=(0,0,1;0rad)
  Radius = 1.5
FEATURE [Part::Cylinder] Cylinder394  label="Válec394"
  Angle = 360
  AttacherType = Attacher::AttachEngine3D
  Height = 4
  Placement = pos=(1,14,-0.1) rot=(0,0,1;0rad)
  Radius = 1.5
FEATURE [Part::Box] Box256  label="Krychle256"
  AttacherType = Attacher::AttachEngine3D
  Height = 2
  Length = 6
  Placement = pos=(-2,11,4) rot=(0,0,1;0rad)
  Width = 6
FEATURE [Part::Compound] Compound181
  Links = -> [Box256,Cylinder393,Cylinder394]
  Placement = pos=(6,-14,2) rot=(0,1,0;1.5708rad)
FEATURE [Part::FeaturePython] involuterack  # WARN: FeaturePython — macro-defined, semantics opaque (R4)
  AttacherType = Attacher::AttachEngine3D
  Placement = pos=(23,6,-2) rot=(0,0,1;0rad)
  add_endings = true
  beta = 0
  clearance = 0.25
  double_helix = false
  head = 0
  height = 12
  module = 0.5
  pressure_angle = 20
  properties_from_tool = true
  simplified = false
  teeth = 44
  thickness = 1
  transverse_pitch = 1.5708
  version = 0.0.3
FEATURE [Part::Box] Box257  label="Krychle257"
  AttacherType = Attacher::AttachEngine3D
  Height = 12
  Length = 1
  Placement = pos=(21.4,-4.5,-2) rot=(0,0,1;0rad)
  Width = 10
FEATURE [Part::Box] Box258  label="Krychle258"
  AttacherType = Attacher::AttachEngine3D
  Height = 12
  Length = 1
  Placement = pos=(21.4,-4.5,-2) rot=(0,0,1;0rad)
  Width = 94
FEATURE [Part::Box] Box259  label="Krychle259"
  AttacherType = Attacher::AttachEngine3D
  Height = 12
  Length = 2
  Placement = pos=(21.4,80,-2) rot=(0,0,1;0rad)
  Width = 19
FEATURE [Part::Cut] Cut238
  Base = -> Box257
  Tool = -> Compound181
FEATURE [Part::Cut] Cut239
  Base = -> Box259
  Tool = -> Compound180
FEATURE [Part::Cylinder] Cylinder396  label="Válec396"
  Angle = 360
  AttacherType = Attacher::AttachEngine3D
  Height = 3
  Placement = pos=(1,14,6) rot=(0,0,1;0rad)
  Radius = 3
FEATURE [Part::Compound] Compound182
  Links = -> [Cylinder396]
  Placement = pos=(11,-14,2) rot=(0,1,0;1.5708rad)
FEATURE [Part::Cylinder] Cylinder397  label="Válec397"
  Angle = 360
  AttacherType = Attacher::AttachEngine3D
  Height = 3
  Placement = pos=(1,14,6) rot=(0,0,1;0rad)
  Radius = 3
FEATURE [Part::Compound] Compound183
  Links = -> [Cylinder397]
  Placement = pos=(16.5,73,2) rot=(0,1,0;1.5708rad)
FEATURE [Part::Cut] Cut240
  Base = -> Cut239
  Tool = -> Compound183
FEATURE [Part::FeaturePython] involuterack001  # WARN: FeaturePython — macro-defined, semantics opaque (R4)
  AttacherType = Attacher::AttachEngine3D
  Placement = pos=(25,81,-2) rot=(0,0,1;0rad)
  add_endings = true
  beta = 0
  clearance = 0.25
  double_helix = false
  head = 0
  height = 12
  module = 0.5
  pressure_angle = 20
  properties_from_tool = true
  simplified = false
  teeth = 12
  thickness = 1
  transverse_pitch = 1.5708
  version = 0.0.3
FEATURE [Part::Cylinder] Cylinder398  label="Válec398"
  Angle = 360
  AttacherType = Attacher::AttachEngine3D
  Height = 3
  Placement = pos=(1,14,6) rot=(0,0,1;0rad)
  Radius = 3
FEATURE [Part::Compound] Compound184
  Links = -> [Cylinder398]
  Placement = pos=(16.5,73,2) rot=(0,1,0;1.5708rad)
FEATURE [Part::Cut] Cut241
  Base = -> involuterack001
  Placement = pos=(0,-7,0) rot=(0,0,1;0rad)
  Tool = -> Compound184
FEATURE [Part::Chamfer] Chamfer034
  Base = -> Cut240
  Edges = 1 edges r=1.9: [Edge4]
  Placement = pos=(0,-7,0) rot=(0,0,1;0rad)
FEATURE [Part::Compound] Compound185  label="finger_zubo"
  Links = -> [Cut238,involuterack,Cut241,Chamfer034]
FEATURE [Part::Cylinder] Cylinder399  label="Válec399"
  Angle = 360
  AttacherType = Attacher::AttachEngine3D
  Height = 8
  Placement = pos=(7,-10,6) rot=(0,0,1;0rad)
  Radius = 6
FEATURE [Part::Box] Box260  label="Krychle260"
  AttacherType = Attacher::AttachEngine3D
  Height = 8
  Length = 32
  Placement = pos=(1,-16,6) rot=(0,0,1;0rad)
  Width = 6
FEATURE [Part::Cylinder] Cylinder400  label="Válec400"
  Angle = 360
  AttacherType = Attacher::AttachEngine3D
  Height = 8
  Placement = pos=(27,-10,6) rot=(0,0,1;0rad)
  Radius = 6
FEATURE [Part::Box] Box261  label="Krychle261"
  AttacherType = Attacher::AttachEngine3D
  Height = 4
  Length = 5
  Placement = pos=(1,-14,8) rot=(0,0,1;0rad)
  Width = 1.4
FEATURE [Part::Cylinder] Cylinder401  label="Válec401"
  Angle = 360
  AttacherType = Attacher::AttachEngine3D
  Height = 12
  Placement = pos=(7,-10,4) rot=(0,0,1;0rad)
  Radius = 2.65
FEATURE [Part::Box] Box262  label="Krychle262"
  AttacherType = Attacher::AttachEngine3D
  Height = 8
  Length = 20
  Placement = pos=(7,-16,6) rot=(0,0,1;0rad)
  Width = 12
FEATURE [Part::Box] Box263  label="Krychle263"
  AttacherType = Attacher::AttachEngine3D
  Height = 4
  Length = 4
  Placement = pos=(15,-11,10) rot=(0,0,1;0rad)
  Width = 1.4
FEATURE [Part::Box] Box264  label="Krychle264"
  AttacherType = Attacher::AttachEngine3D
  Height = 4
  Length = 5
  Placement = pos=(28,-14,8) rot=(0,0,1;0rad)
  Width = 1.4
FEATURE [Part::Box] Box265  label="Krychle265"
  AttacherType = Attacher::AttachEngine3D
  Height = 4
  Length = 4
  Placement = pos=(15,-11,6) rot=(0,0,1;0rad)
  Width = 1.4
FEATURE [Part::Compound] Compound187
  Links = -> [Box261,Box263,Box265,Box264]
FEATURE [Part::Compound] Compound190
  Links = -> [Cylinder400,Cylinder399]
FEATURE [Part::Cylinder] Cylinder402  label="Válec402"
  Angle = 360
  AttacherType = Attacher::AttachEngine3D
  Height = 20
  Placement = pos=(17,-6,8) rot=(1,0,0;1.5708rad)
  Radius = 1
FEATURE [Part::Cylinder] Cylinder403  label="Válec403"
  Angle = 360
  AttacherType = Attacher::AttachEngine3D
  Height = 20
  Placement = pos=(17,-10,12) rot=(1,0,0;1.5708rad)
  Radius = 1
FEATURE [Part::Box] Box266  label="Krychle266"
  AttacherType = Attacher::AttachEngine3D
  Height = 4
  Length = 5
  Placement = pos=(1,-14,8) rot=(0,0,1;0rad)
  Width = 1.4
FEATURE [Part::Box] Box267  label="Krychle267"
  AttacherType = Attacher::AttachEngine3D
  Height = 4
  Length = 5
  Placement = pos=(28,-14,8) rot=(0,0,1;0rad)
  Width = 1.4
FEATURE [Part::Cylinder] Cylinder404  label="Válec404"
  Angle = 360
  AttacherType = Attacher::AttachEngine3D
  Height = 12
  Placement = pos=(27,-10,4) rot=(0,0,1;0rad)
  Radius = 2.65
FEATURE [Part::Cylinder] Cylinder405  label="Válec405"
  Angle = 360
  AttacherType = Attacher::AttachEngine3D
  Height = 20
  Placement = pos=(17,-6,12) rot=(1,0,0;1.5708rad)
  Radius = 1
FEATURE [Part::Cylinder] Cylinder406  label="Válec406"
  Angle = 360
  AttacherType = Attacher::AttachEngine3D
  Height = 20
  Placement = pos=(3,-10,10) rot=(1,0,0;1.5708rad)
  Radius = 1
FEATURE [Part::Cylinder] Cylinder407  label="Válec407"
  Angle = 360
  AttacherType = Attacher::AttachEngine3D
  Height = 20
  Placement = pos=(17,-6,12) rot=(1,0,0;1.5708rad)
  Radius = 1
FEATURE [Part::Cylinder] Cylinder408  label="Válec408"
  Angle = 360
  AttacherType = Attacher::AttachEngine3D
  Height = 12
  Placement = pos=(7,-10,4) rot=(0,0,1;0rad)
  Radius = 2.65
FEATURE [Part::Compound] Compound196
  Links = -> [Cylinder404,Cylinder408]
FEATURE [Part::Cut] Cut244
  Base = -> Compound190
  Tool = -> Compound196
FEATURE [Part::Box] Box268  label="Krychle268"
  AttacherType = Attacher::AttachEngine3D
  Height = 4
  Length = 4
  Placement = pos=(15,-11,10) rot=(0,0,1;0rad)
  Width = 1.4
FEATURE [Part::Box] Box269  label="Krychle269"
  AttacherType = Attacher::AttachEngine3D
  Height = 4
  Length = 4
  Placement = pos=(15,-11,6) rot=(0,0,1;0rad)
  Width = 1.4
FEATURE [Part::Compound] Compound191
  Links = -> [Box266,Box268,Box269,Box267]
FEATURE [Part::Cylinder] Cylinder409  label="Válec409"
  Angle = 360
  AttacherType = Attacher::AttachEngine3D
  Height = 12
  Placement = pos=(27,-10,4) rot=(0,0,1;0rad)
  Radius = 2.65
FEATURE [Part::Compound] Compound189
  Links = -> [Cylinder409,Cylinder401]
FEATURE [Part::Cut] Cut247
  Base = -> Box262
  Tool = -> Compound189
FEATURE [Part::Cylinder] Cylinder410  label="Válec410"
  Angle = 360
  AttacherType = Attacher::AttachEngine3D
  Height = 20
  Placement = pos=(31,-10,10) rot=(1,0,0;1.5708rad)
  Radius = 1
FEATURE [Part::Compound] Compound192
  Links = -> [Cylinder406,Cylinder410,Cylinder402,Cylinder405]
FEATURE [Part::Cut] Cut249
  Base = -> Cut247
  Tool = -> Compound192
FEATURE [Part::Cut] Cut242
  Base = -> Cut249
  Tool = -> Compound187
FEATURE [Part::Cylinder] Cylinder411  label="Válec411"
  Angle = 360
  AttacherType = Attacher::AttachEngine3D
  Height = 20
  Placement = pos=(31,-10,10) rot=(1,0,0;1.5708rad)
  Radius = 1
FEATURE [Part::Cylinder] Cylinder412  label="Válec412"
  Angle = 360
  AttacherType = Attacher::AttachEngine3D
  Height = 20
  Placement = pos=(3,-10,10) rot=(1,0,0;1.5708rad)
  Radius = 1
FEATURE [Part::Box] Box270  label="Krychle270"
  AttacherType = Attacher::AttachEngine3D
  Height = 4
  Length = 5
  Placement = pos=(1,-14,8) rot=(0,0,1;0rad)
  Width = 1.4
FEATURE [Part::Cylinder] Cylinder413  label="Válec413"
  Angle = 360
  AttacherType = Attacher::AttachEngine3D
  Height = 20
  Placement = pos=(31,-10,10) rot=(1,0,0;1.5708rad)
  Radius = 1
FEATURE [Part::Box] Box271  label="Krychle271"
  AttacherType = Attacher::AttachEngine3D
  Height = 4
  Length = 4
  Placement = pos=(15,-11,6) rot=(0,0,1;0rad)
  Width = 1.4
FEATURE [Part::Cylinder] Cylinder414  label="Válec414"
  Angle = 360
  AttacherType = Attacher::AttachEngine3D
  Height = 20
  Placement = pos=(17,-10,8) rot=(1,0,0;1.5708rad)
  Radius = 1
FEATURE [Part::Compound] Compound193
  Links = -> [Cylinder412,Cylinder411,Cylinder414,Cylinder403]
FEATURE [Part::Cut] Cut248
  Base = -> Cut244
  Tool = -> Compound193
FEATURE [Part::Cut] Cut250
  Base = -> Cut248
  Tool = -> Compound191
FEATURE [Part::Cylinder] Cylinder415  label="Válec415"
  Angle = 360
  AttacherType = Attacher::AttachEngine3D
  Height = 20
  Placement = pos=(3,-10,10) rot=(1,0,0;1.5708rad)
  Radius = 1
FEATURE [Part::Box] Box272  label="Krychle272"
  AttacherType = Attacher::AttachEngine3D
  Height = 4
  Length = 4
  Placement = pos=(15,-11,10) rot=(0,0,1;0rad)
  Width = 1.4
FEATURE [Part::Box] Box273  label="Krychle273"
  AttacherType = Attacher::AttachEngine3D
  Height = 4
  Length = 5
  Placement = pos=(28,-14,8) rot=(0,0,1;0rad)
  Width = 1.4
FEATURE [Part::Compound] Compound188
  Links = -> [Box270,Box272,Box271,Box273]
FEATURE [Part::Cylinder] Cylinder416  label="Válec416"
  Angle = 360
  AttacherType = Attacher::AttachEngine3D
  Height = 12
  Placement = pos=(7,-10,4) rot=(0,0,1;0rad)
  Radius = 2.65
FEATURE [Part::Cylinder] Cylinder417  label="Válec417"
  Angle = 360
  AttacherType = Attacher::AttachEngine3D
  Height = 20
  Placement = pos=(17,-6,8) rot=(1,0,0;1.5708rad)
  Radius = 1
FEATURE [Part::Compound] Compound194
  Links = -> [Cylinder415,Cylinder413,Cylinder417,Cylinder407]
FEATURE [Part::Box] Box274  label="Krychle274"
  AttacherType = Attacher::AttachEngine3D
  Height = 8
  Length = 32
  Placement = pos=(1,-21,6) rot=(0,0,1;0rad)
  Width = 6
FEATURE [Part::Cut] Cut251
  Base = -> Cut250
  Tool = -> Box274
FEATURE [Part::Cylinder] Cylinder418  label="Válec418"
  Angle = 360
  AttacherType = Attacher::AttachEngine3D
  Height = 12
  Placement = pos=(27,-10,4) rot=(0,0,1;0rad)
  Radius = 2.65
FEATURE [Part::Compound] Compound195
  Links = -> [Cylinder418,Cylinder416]
FEATURE [Part::Cut] Cut245
  Base = -> Box260
  Tool = -> Compound195
FEATURE [Part::Cut] Cut246
  Base = -> Cut245
  Tool = -> Compound188
FEATURE [Part::Cut] Cut243
  Base = -> Cut246
  Tool = -> Compound194
FEATURE [Part::Compound] Compound186  label="wrist_holdo_wider"
  Links = -> [Cut242,Cut243,Cut251]
FEATURE [Part::Cylinder] Cylinder419  label="Válec419"
  Angle = 360
  AttacherType = Attacher::AttachEngine3D
  Height = 32
  Placement = pos=(7,-10,-6) rot=(0,0,1;0rad)
  Radius = 8
FEATURE [Part::Cylinder] Cylinder420  label="Válec420"
  Angle = 360
  AttacherType = Attacher::AttachEngine3D
  Height = 32
  Placement = pos=(27,-10,-6) rot=(0,0,1;0rad)
  Radius = 8
FEATURE [Part::Compound] Compound197
  Links = -> [Cylinder419,Cylinder420]
FEATURE [Part::Cut] Cut252
  Base = -> Chamfer018
  Tool = -> Compound197
FEATURE [Part::Box] Box275  label="Krychle275"
  AttacherType = Attacher::AttachEngine3D
  Height = 12
  Length = 1
  Placement = pos=(21.4,-4.5,-2) rot=(0,0,1;0rad)
  Width = 10
FEATURE [Part::Box] Box276  label="Krychle276"
  AttacherType = Attacher::AttachEngine3D
  Height = 12
  Length = 2
  Placement = pos=(21.4,80,-2) rot=(0,0,1;0rad)
  Width = 19
FEATURE [Part::Cylinder] Cylinder421  label="Válec421"
  Angle = 360
  AttacherType = Attacher::AttachEngine3D
  Height = 3
  Placement = pos=(1,14,6) rot=(0,0,1;0rad)
  Radius = 3
FEATURE [Part::Compound] Compound202
  Links = -> [Cylinder421]
  Placement = pos=(16.5,73,2) rot=(0,1,0;1.5708rad)
FEATURE [Part::Cylinder] Cylinder422  label="Válec422"
  Angle = 360
  AttacherType = Attacher::AttachEngine3D
  Height = 3
  Placement = pos=(1,14,6) rot=(0,0,1;0rad)
  Radius = 3
FEATURE [Part::Compound] Compound200
  Links = -> [Cylinder422]
  Placement = pos=(16.5,73,2) rot=(0,1,0;1.5708rad)
FEATURE [Part::Cylinder] Cylinder423  label="Válec423"
  Angle = 360
  AttacherType = Attacher::AttachEngine3D
  Height = 12
  Placement = pos=(1,14,6) rot=(0,0,1;0rad)
  Radius = 1.5
FEATURE [Part::Cylinder] Cylinder424  label="Válec424"
  Angle = 360
  AttacherType = Attacher::AttachEngine3D
  Height = 4
  Placement = pos=(1,14,-0.1) rot=(0,0,1;0rad)
  Radius = 1.5
FEATURE [Part::Cylinder] Cylinder425  label="Válec425"
  Angle = 360
  AttacherType = Attacher::AttachEngine3D
  Height = 4
  Placement = pos=(1,14,-0.1) rot=(0,0,1;0rad)
  Radius = 1.5
FEATURE [Part::Box] Box277  label="Krychle277"
  AttacherType = Attacher::AttachEngine3D
  Height = 2
  Length = 6
  Placement = pos=(-2,11,4) rot=(0,0,1;0rad)
  Width = 6
FEATURE [Part::Compound] Compound199
  Links = -> [Box277,Cylinder423,Cylinder425]
  Placement = pos=(6,73,2) rot=(0,1,0;1.5708rad)
FEATURE [Part::Cut] Cut256
  Base = -> Box276
  Tool = -> Compound199
FEATURE [Part::Cut] Cut253
  Base = -> Cut256
  Tool = -> Compound200
FEATURE [Part::Chamfer] Chamfer035
  Base = -> Cut253
  Edges = 1 edges r=1.9: [Edge4]
  Placement = pos=(0,-7,0) rot=(0,0,1;0rad)
FEATURE [Part::Cylinder] Cylinder426  label="Válec426"
  Angle = 360
  AttacherType = Attacher::AttachEngine3D
  Height = 12
  Placement = pos=(1,14,6) rot=(0,0,1;0rad)
  Radius = 1.5
FEATURE [Part::Box] Box278  label="Krychle278"
  AttacherType = Attacher::AttachEngine3D
  Height = 2
  Length = 6
  Placement = pos=(-2,11,4) rot=(0,0,1;0rad)
  Width = 6
FEATURE [Part::Compound] Compound201
  Links = -> [Box278,Cylinder426,Cylinder424]
  Placement = pos=(6,-14,2) rot=(0,1,0;1.5708rad)
FEATURE [Part::Cut] Cut255
  Base = -> Box275
  Tool = -> Compound201
FEATURE [Part::FeaturePython] involuterack002  # WARN: FeaturePython — macro-defined, semantics opaque (R4)
  AttacherType = Attacher::AttachEngine3D
  Placement = pos=(23,-44,-2) rot=(0,0,1;0rad)
  add_endings = true
  beta = 75
  clearance = 0.25
  double_helix = false
  head = 0
  height = 12
  module = 0.5
  pressure_angle = 20
  properties_from_tool = true
  simplified = false
  teeth = 44
  thickness = 1
  transverse_pitch = 6.06909
  version = 0.0.3
FEATURE [Part::FeaturePython] involuterack003  # WARN: FeaturePython — macro-defined, semantics opaque (R4)
  AttacherType = Attacher::AttachEngine3D
  Placement = pos=(25,81,-2) rot=(0,0,1;0rad)
  add_endings = true
  beta = 0
  clearance = 0.25
  double_helix = false
  head = 0
  height = 12
  module = 0.5
  pressure_angle = 20
  properties_from_tool = true
  simplified = false
  teeth = 12
  thickness = 1
  transverse_pitch = 1.5708
  version = 0.0.3
FEATURE [Part::Cut] Cut254
  Base = -> involuterack003
  Placement = pos=(0,-7,0) rot=(0,0,1;0rad)
  Tool = -> Compound202
FEATURE [Part::Box] Box279  label="Krychle279"
  AttacherType = Attacher::AttachEngine3D
  Height = 12
  Length = 6
  Placement = pos=(19.4,75.5,-2) rot=(0,0,1;0rad)
  Width = 200
FEATURE [Part::Box] Box280  label="Krychle280"
  AttacherType = Attacher::AttachEngine3D
  Height = 12
  Length = 6
  Placement = pos=(19.4,-84.5,-2) rot=(0,0,1;0rad)
  Width = 90
FEATURE [Part::Compound] Compound204
  Links = -> [Box279,Box280]
FEATURE [Part::Cut] Cut257
  Base = -> involuterack002
  Tool = -> Compound204
FEATURE [Part::Compound] Compound205  label="finger_zubo_sikmo"
  Links = -> [Chamfer035,Cut254,Cut255,Cut257]
FEATURE [Part::FeaturePython] involuterack004  # WARN: FeaturePython — macro-defined, semantics opaque (R4)
  AttacherType = Attacher::AttachEngine3D
  Placement = pos=(25,81,-2) rot=(0,0,1;0rad)
  add_endings = true
  beta = 0
  clearance = 0.25
  double_helix = false
  head = 0
  height = 12
  module = 0.5
  pressure_angle = 20
  properties_from_tool = true
  simplified = false
  teeth = 12
  thickness = 1
  transverse_pitch = 1.5708
  version = 0.0.3
FEATURE [Part::Box] Box281  label="Krychle281"
  AttacherType = Attacher::AttachEngine3D
  Height = 12
  Length = 2
  Placement = pos=(21.4,80,-2) rot=(0,0,1;0rad)
  Width = 19
FEATURE [Part::Cylinder] Cylinder427  label="Válec427"
  Angle = 360
  AttacherType = Attacher::AttachEngine3D
  Height = 12
  Placement = pos=(1,14,6) rot=(0,0,1;0rad)
  Radius = 1.5
FEATURE [Part::Box] Box282  label="Krychle282"
  AttacherType = Attacher::AttachEngine3D
  Height = 2
  Length = 6
  Placement = pos=(-2,11,4) rot=(0,0,1;0rad)
  Width = 6
FEATURE [Part::Cylinder] Cylinder428  label="Válec428"
  Angle = 360
  AttacherType = Attacher::AttachEngine3D
  Height = 4
  Placement = pos=(1,14,-0.1) rot=(0,0,1;0rad)
  Radius = 1.5
FEATURE [Part::Box] Box283  label="Krychle283"
  AttacherType = Attacher::AttachEngine3D
  Height = 12
  Length = 1
  Placement = pos=(21.4,-4.5,-2) rot=(0,0,1;0rad)
  Width = 10
FEATURE [Part::Cylinder] Cylinder429  label="Válec429"
  Angle = 360
  AttacherType = Attacher::AttachEngine3D
  Height = 3
  Placement = pos=(1,14,6) rot=(0,0,1;0rad)
  Radius = 3
FEATURE [Part::Cylinder] Cylinder430  label="Válec430"
  Angle = 360
  AttacherType = Attacher::AttachEngine3D
  Height = 3
  Placement = pos=(1,14,6) rot=(0,0,1;0rad)
  Radius = 3
FEATURE [Part::Cylinder] Cylinder431  label="Válec431"
  Angle = 360
  AttacherType = Attacher::AttachEngine3D
  Height = 4
  Placement = pos=(1,14,-0.1) rot=(0,0,1;0rad)
  Radius = 1.5
FEATURE [Part::Cylinder] Cylinder432  label="Válec432"
  Angle = 360
  AttacherType = Attacher::AttachEngine3D
  Height = 12
  Placement = pos=(1,14,6) rot=(0,0,1;0rad)
  Radius = 1.5
FEATURE [Part::Box] Box284  label="Krychle284"
  AttacherType = Attacher::AttachEngine3D
  Height = 2
  Length = 6
  Placement = pos=(-2,11,4) rot=(0,0,1;0rad)
  Width = 6
FEATURE [Part::Box] Box285  label="Krychle285"
  AttacherType = Attacher::AttachEngine3D
  Height = 12
  Length = 6
  Placement = pos=(19.4,75.5,-2) rot=(0,0,1;0rad)
  Width = 200
FEATURE [Part::Box] Box286  label="Krychle286"
  AttacherType = Attacher::AttachEngine3D
  Height = 12
  Length = 6
  Placement = pos=(19.4,-84.5,-2) rot=(0,0,1;0rad)
  Width = 90
FEATURE [Part::FeaturePython] involuterack005  # WARN: FeaturePython — macro-defined, semantics opaque (R4)
  AttacherType = Attacher::AttachEngine3D
  Placement = pos=(23,-44,-2) rot=(0,0,1;0rad)
  add_endings = true
  beta = 75
  clearance = 0.25
  double_helix = false
  head = 0
  height = 12
  module = 0.5
  pressure_angle = 20
  properties_from_tool = true
  simplified = false
  teeth = 44
  thickness = 1
  transverse_pitch = 6.06909
  version = 0.0.3
FEATURE [Part::Compound] Compound206
  Links = -> [Box285,Box286]
FEATURE [Part::Cut] Cut262
  Base = -> involuterack005
  Tool = -> Compound206
FEATURE [Part::Compound] Compound208
  Links = -> [Box284,Cylinder432,Cylinder428]
  Placement = pos=(6,-14,2) rot=(0,1,0;1.5708rad)
FEATURE [Part::Cut] Cut260
  Base = -> Box283
  Tool = -> Compound208
FEATURE [Part::Compound] Compound209
  Links = -> [Box282,Cylinder427,Cylinder431]
  Placement = pos=(6,73,2) rot=(0,1,0;1.5708rad)
FEATURE [Part::Cut] Cut261
  Base = -> Box281
  Tool = -> Compound209
FEATURE [Part::Compound] Compound210
  Links = -> [Cylinder430]
  Placement = pos=(16.5,73,2) rot=(0,1,0;1.5708rad)
FEATURE [Part::Cut] Cut258
  Base = -> Cut261
  Tool = -> Compound210
FEATURE [Part::Chamfer] Chamfer036
  Base = -> Cut258
  Edges = 1 edges r=1.9: [Edge4]
  Placement = pos=(0,-7,0) rot=(0,0,1;0rad)
FEATURE [Part::Compound] Compound211
  Links = -> [Cylinder429]
  Placement = pos=(16.5,73,2) rot=(0,1,0;1.5708rad)
FEATURE [Part::Cut] Cut259
  Base = -> involuterack004
  Placement = pos=(0,-7,0) rot=(0,0,1;0rad)
  Tool = -> Compound211
FEATURE [Part::Compound] Compound207  label="finger_zubo_sikmo001"
  Links = -> [Chamfer036,Cut259,Cut260,Cut262]
FEATURE [Part::Mirroring] mirror006  label="finger_zubo_sikmo_oppo"
  Base = (0,0,0)
  Normal = (1,0,0)
  Source = -> Compound207
FEATURE [Part::Box] Box287  label="Krychle287"
  AttacherType = Attacher::AttachEngine3D
  Height = 12
  Length = 1
  Placement = pos=(21.4,-4.5,-2) rot=(0,0,1;0rad)
  Width = 10
FEATURE [Part::Box] Box288  label="Krychle288"
  AttacherType = Attacher::AttachEngine3D
  Height = 12
  Length = 2
  Placement = pos=(21.4,80,-2) rot=(0,0,1;0rad)
  Width = 19
FEATURE [Part::Cylinder] Cylinder433  label="Válec433"
  Angle = 360
  AttacherType = Attacher::AttachEngine3D
  Height = 3
  Placement = pos=(1,14,6) rot=(0,0,1;0rad)
  Radius = 3
FEATURE [Part::Compound] Compound215
  Links = -> [Cylinder433]
  Placement = pos=(16.5,73,2) rot=(0,1,0;1.5708rad)
FEATURE [Part::Cylinder] Cylinder434  label="Válec434"
  Angle = 360
  AttacherType = Attacher::AttachEngine3D
  Height = 3
  Placement = pos=(1,14,6) rot=(0,0,1;0rad)
  Radius = 3
FEATURE [Part::Compound] Compound213
  Links = -> [Cylinder434]
  Placement = pos=(16.5,73,2) rot=(0,1,0;1.5708rad)
FEATURE [Part::Cylinder] Cylinder435  label="Válec435"
  Angle = 360
  AttacherType = Attacher::AttachEngine3D
  Height = 12
  Placement = pos=(1,14,6) rot=(0,0,1;0rad)
  Radius = 1.5
FEATURE [Part::Cylinder] Cylinder436  label="Válec436"
  Angle = 360
  AttacherType = Attacher::AttachEngine3D
  Height = 4
  Placement = pos=(1,14,-0.1) rot=(0,0,1;0rad)
  Radius = 1.5
FEATURE [Part::Cylinder] Cylinder437  label="Válec437"
  Angle = 360
  AttacherType = Attacher::AttachEngine3D
  Height = 4
  Placement = pos=(1,14,-0.1) rot=(0,0,1;0rad)
  Radius = 1.5
FEATURE [Part::Box] Box289  label="Krychle289"
  AttacherType = Attacher::AttachEngine3D
  Height = 2
  Length = 6
  Placement = pos=(-2,11,4) rot=(0,0,1;0rad)
  Width = 6
FEATURE [Part::Compound] Compound212
  Links = -> [Box289,Cylinder435,Cylinder437]
  Placement = pos=(6,73,2) rot=(0,1,0;1.5708rad)
FEATURE [Part::Cut] Cut266
  Base = -> Box288
  Tool = -> Compound212
FEATURE [Part::Cut] Cut263
  Base = -> Cut266
  Tool = -> Compound213
FEATURE [Part::Chamfer] Chamfer037
  Base = -> Cut263
  Edges = 1 edges r=1.9: [Edge4]
  Placement = pos=(0,-7,0) rot=(0,0,1;0rad)
FEATURE [Part::Cylinder] Cylinder438  label="Válec438"
  Angle = 360
  AttacherType = Attacher::AttachEngine3D
  Height = 12
  Placement = pos=(1,14,6) rot=(0,0,1;0rad)
  Radius = 1.5
FEATURE [Part::Box] Box290  label="Krychle290"
  AttacherType = Attacher::AttachEngine3D
  Height = 2
  Length = 6
  Placement = pos=(-2,11,4) rot=(0,0,1;0rad)
  Width = 6
FEATURE [Part::Compound] Compound214
  Links = -> [Box290,Cylinder438,Cylinder436]
  Placement = pos=(6,-14,2) rot=(0,1,0;1.5708rad)
FEATURE [Part::Cut] Cut265
  Base = -> Box287
  Tool = -> Compound214
FEATURE [Part::FeaturePython] involuterack006  # WARN: FeaturePython — macro-defined, semantics opaque (R4)
  AttacherType = Attacher::AttachEngine3D
  Placement = pos=(23,6,-2) rot=(0,0,1;0rad)
  add_endings = true
  beta = 0
  clearance = 0.25
  double_helix = false
  head = 0
  height = 12
  module = 0.5
  pressure_angle = 20
  properties_from_tool = true
  simplified = false
  teeth = 44
  thickness = 1
  transverse_pitch = 1.5708
  version = 0.0.3
FEATURE [Part::FeaturePython] involuterack007  # WARN: FeaturePython — macro-defined, semantics opaque (R4)
  AttacherType = Attacher::AttachEngine3D
  Placement = pos=(25,81,-2) rot=(0,0,1;0rad)
  add_endings = true
  beta = 0
  clearance = 0.25
  double_helix = false
  head = 0
  height = 12
  module = 0.5
  pressure_angle = 20
  properties_from_tool = true
  simplified = false
  teeth = 12
  thickness = 1
  transverse_pitch = 1.5708
  version = 0.0.3
FEATURE [Part::Cut] Cut264
  Base = -> involuterack007
  Placement = pos=(0,-7,0) rot=(0,0,1;0rad)
  Tool = -> Compound215
FEATURE [Part::Compound] Compound216  label="finger_zubo001"
  Links = -> [Cut265,involuterack006,Cut264,Chamfer037]
FEATURE [Part::Mirroring] mirror007  label="finger_zubo_oppo"
  Base = (0,0,0)
  Normal = (1,0,0)
  Source = -> Compound216
FEATURE [Mesh::Feature] Mesh020  label="finger_zubo_sikmo_oppo (Meshed)"
FEATURE [Mesh::Feature] Mesh021  label="wrist_holdo_wider (Meshed)"
FEATURE [Part::Cylinder] Cylinder439  label="Válec439"
  Angle = 360
  AttacherType = Attacher::AttachEngine3D
  Height = 20
  Placement = pos=(31,-10,10) rot=(1,0,0;1.5708rad)
  Radius = 1
FEATURE [Part::Box] Box291  label="Krychle291"
  AttacherType = Attacher::AttachEngine3D
  Height = 8
  Length = 54
  Placement = pos=(-10,-21,6) rot=(0,0,1;0rad)
  Width = 6
FEATURE [Part::Cylinder] Cylinder440  label="Válec440"
  Angle = 360
  AttacherType = Attacher::AttachEngine3D
  Height = 20
  Placement = pos=(3,-10,10) rot=(1,0,0;1.5708rad)
  Radius = 1
FEATURE [Part::Cylinder] Cylinder441  label="Válec441"
  Angle = 360
  AttacherType = Attacher::AttachEngine3D
  Height = 20
  Placement = pos=(17,-10,8) rot=(1,0,0;1.5708rad)
  Radius = 1
FEATURE [Part::Cylinder] Cylinder442  label="Válec442"
  Angle = 360
  AttacherType = Attacher::AttachEngine3D
  Height = 20
  Placement = pos=(17,-10,12) rot=(1,0,0;1.5708rad)
  Radius = 1
FEATURE [Part::Compound] Compound218
  Links = -> [Cylinder440,Cylinder439,Cylinder441,Cylinder442]
FEATURE [Part::Cylinder] Cylinder443  label="Válec443"
  Angle = 360
  AttacherType = Attacher::AttachEngine3D
  Height = 2
  Placement = pos=(31,-10,10) rot=(1,0,0;1.5708rad)
  Radius = 2
FEATURE [Part::Cylinder] Cylinder444  label="Válec444"
  Angle = 360
  AttacherType = Attacher::AttachEngine3D
  Height = 2
  Placement = pos=(17,-10,12) rot=(1,0,0;1.5708rad)
  Radius = 2
FEATURE [Part::Cylinder] Cylinder445  label="Válec445"
  Angle = 360
  AttacherType = Attacher::AttachEngine3D
  Height = 2
  Placement = pos=(3,-10,10) rot=(1,0,0;1.5708rad)
  Radius = 2
FEATURE [Part::Cylinder] Cylinder446  label="Válec446"
  Angle = 360
  AttacherType = Attacher::AttachEngine3D
  Height = 2
  Placement = pos=(17,-10,8) rot=(1,0,0;1.5708rad)
  Radius = 2
FEATURE [Part::Compound] Compound217
  Links = -> [Cylinder445,Cylinder443,Cylinder446,Cylinder444]
  Placement = pos=(0,-9,0) rot=(0,0,1;0rad)
FEATURE [Part::Cut] Cut267
  Base = -> Box291
  Tool = -> Compound217
FEATURE [Part::Cut] Cut268
  Base = -> Cut267
  Tool = -> Compound218
FEATURE [Part::Cylinder] Cylinder447  label="Válec447"
  Angle = 360
  AttacherType = Attacher::AttachEngine3D
  Height = 20
  Placement = pos=(-5,-17,10) rot=(1,0,0;1.5708rad)
  Radius = 2.65
FEATURE [Part::Cylinder] Cylinder448  label="Válec448"
  Angle = 360
  AttacherType = Attacher::AttachEngine3D
  Height = 20
  Placement = pos=(39,-17,10) rot=(1,0,0;1.5708rad)
  Radius = 2.65
FEATURE [Part::Compound] Compound219
  Links = -> [Cylinder447,Cylinder448]
FEATURE [Part::Cut] Cut269
  Base = -> Cut268
  Tool = -> Compound219
FEATURE [Part::Box] Box292  label="Krychle292"
  AttacherType = Attacher::AttachEngine3D
  Height = 10
  Length = 54
  Placement = pos=(-10,-21,14) rot=(0,0,1;0rad)
  Width = 6
FEATURE [Part::Cylinder] Cylinder449  label="Válec449"
  Angle = 360
  AttacherType = Attacher::AttachEngine3D
  Height = 10
  Placement = pos=(27,-10,-4) rot=(0,0,1;0rad)
  Radius = 8
FEATURE [Part::Cylinder] Cylinder450  label="Válec450"
  Angle = 360
  AttacherType = Attacher::AttachEngine3D
  Height = 10
  Placement = pos=(7,-10,14) rot=(0,0,1;0rad)
  Radius = 8
FEATURE [Part::Cut] Cut273
  Base = -> Box292
  Tool = -> Cylinder450
FEATURE [Part::Cylinder] Cylinder451  label="Válec451"
  Angle = 360
  AttacherType = Attacher::AttachEngine3D
  Height = 10
  Placement = pos=(7,-10,-4) rot=(0,0,1;0rad)
  Radius = 8
FEATURE [Part::Cylinder] Cylinder452  label="Válec452"
  Angle = 360
  AttacherType = Attacher::AttachEngine3D
  Height = 10
  Placement = pos=(27,-10,14) rot=(0,0,1;0rad)
  Radius = 8
FEATURE [Part::Cut] Cut271
  Base = -> Cut273
  Tool = -> Cylinder452
FEATURE [Part::Box] Box293  label="Krychle293"
  AttacherType = Attacher::AttachEngine3D
  Height = 10
  Length = 54
  Placement = pos=(-10,-21,-4) rot=(0,0,1;0rad)
  Width = 6
FEATURE [Part::Cut] Cut272
  Base = -> Box293
  Tool = -> Cylinder451
FEATURE [Part::Cut] Cut270
  Base = -> Cut272
  Tool = -> Cylinder449
FEATURE [Part::Compound] Compound222
  Links = -> [Cut271,Cut270]
FEATURE [Part::Cylinder] Cylinder453  label="Válec453"
  Angle = 360
  AttacherType = Attacher::AttachEngine3D
  Height = 50
  Placement = pos=(-5,-32,-7) rot=(1,0,0;1.5708rad)
  Radius = 1.5
FEATURE [Part::Cylinder] Cylinder454  label="Válec454"
  Angle = 360
  AttacherType = Attacher::AttachEngine3D
  Height = 3
  Placement = pos=(-5,-32,27) rot=(1,0,0;1.5708rad)
  Radius = 3
FEATURE [Part::Cylinder] Cylinder455  label="Válec455"
  Angle = 360
  AttacherType = Attacher::AttachEngine3D
  Height = 50
  Placement = pos=(39,-32,27) rot=(1,0,0;1.5708rad)
  Radius = 1.5
FEATURE [Part::Cylinder] Cylinder456  label="Válec456"
  Angle = 360
  AttacherType = Attacher::AttachEngine3D
  Height = 3
  Placement = pos=(-5,-32,-7) rot=(1,0,0;1.5708rad)
  Radius = 3
FEATURE [Part::Cylinder] Cylinder457  label="Válec457"
  Angle = 360
  AttacherType = Attacher::AttachEngine3D
  Height = 50
  Placement = pos=(39,-32,-7) rot=(1,0,0;1.5708rad)
  Radius = 1.5
FEATURE [Part::Cylinder] Cylinder458  label="Válec458"
  Angle = 360
  AttacherType = Attacher::AttachEngine3D
  Height = 3
  Placement = pos=(39,-32,27) rot=(1,0,0;1.5708rad)
  Radius = 3
FEATURE [Part::Cylinder] Cylinder459  label="Válec459"
  Angle = 360
  AttacherType = Attacher::AttachEngine3D
  Height = 3
  Placement = pos=(39,-32,-7) rot=(1,0,0;1.5708rad)
  Radius = 3
FEATURE [Part::Compound] Compound221
  Links = -> [Cylinder454,Cylinder456,Cylinder458,Cylinder459]
  Placement = pos=(0,17,0) rot=(0,0,1;0rad)
FEATURE [Part::Cylinder] Cylinder460  label="Válec460"
  Angle = 360
  AttacherType = Attacher::AttachEngine3D
  Height = 50
  Placement = pos=(-5,-32,27) rot=(1,0,0;1.5708rad)
  Radius = 1.5
FEATURE [Part::Compound] Compound220
  Links = -> [Cylinder460,Cylinder453,Cylinder455,Cylinder457]
  Placement = pos=(0,20,0) rot=(0,0,1;0rad)
FEATURE [Part::Cut] Cut275
  Base = -> Compound222
  Tool = -> Compound220
FEATURE [Part::Cut] Cut274
  Base = -> Cut275
  Tool = -> Compound221
FEATURE [Part::Chamfer] Chamfer038
  Base = -> Cut269
  Edges = 1 edges r=2: [Edge22]
FEATURE [Part::Chamfer] Chamfer039
  Base = -> Cut274
  Edges = 2 edges r=2: [Edge25,Edge53]
FEATURE [Part::Chamfer] Chamfer040
  Base = -> Chamfer038
  Edges = 1 edges r=2: [Edge9]
FEATURE [Part::Chamfer] Chamfer041
  Base = -> Chamfer038
  Edges = 1 edges r=2: [Edge9]
FEATURE [Part::Chamfer] Chamfer042
  Base = -> Chamfer039
  Edges = 2 edges r=2: [Edge23,Edge57]
FEATURE [Part::Compound] Compound223  label="tabular_wristo_wider"
  Links = -> [Chamfer040,Chamfer042,Cut252,Cut226,Cut225]
FEATURE [Part::Cylinder] Cylinder461  label="Válec461"
  Angle = 360
  AttacherType = Attacher::AttachEngine3D
  Height = 6
  Placement = pos=(17,-24,10) rot=(1,0,0;1.5708rad)
  Radius = 10
FEATURE [Part::Cylinder] Cylinder462  label="Válec462"
  Angle = 360
  AttacherType = Attacher::AttachEngine3D
  Height = 30
  Placement = pos=(11.5,-19,4.5) rot=(1,0,0;1.5708rad)
  Radius = 1.5
FEATURE [Part::Cylinder] Cylinder463  label="Válec463"
  Angle = 360
  AttacherType = Attacher::AttachEngine3D
  Height = 30
  Placement = pos=(11.5,-19,15.5) rot=(1,0,0;1.5708rad)
  Radius = 1.5
FEATURE [Part::Cylinder] Cylinder464  label="Válec464"
  Angle = 360
  AttacherType = Attacher::AttachEngine3D
  Height = 30
  Placement = pos=(22.5,-19,4.5) rot=(1,0,0;1.5708rad)
  Radius = 1.5
FEATURE [Part::Cylinder] Cylinder465  label="Válec465"
  Angle = 360
  AttacherType = Attacher::AttachEngine3D
  Height = 30
  Placement = pos=(22.5,-19,15.5) rot=(1,0,0;1.5708rad)
  Radius = 1.5
FEATURE [Part::Compound] Compound224
  Links = -> [Cylinder462,Cylinder464,Cylinder463,Cylinder465]
  Placement = pos=(0,9,0) rot=(0,0,1;0rad)
FEATURE [Part::Cylinder] Cylinder466  label="Válec466"
  Angle = 360
  AttacherType = Attacher::AttachEngine3D
  Height = 6
  Placement = pos=(17,-24,10) rot=(1,0,0;1.5708rad)
  Radius = 5.5
FEATURE [Part::Cylinder] Cylinder467  label="Válec467"
  Angle = 360
  AttacherType = Attacher::AttachEngine3D
  Height = 3
  Placement = pos=(11.5,-19,4.5) rot=(1,0,0;1.5708rad)
  Radius = 3
FEATURE [Part::Cylinder] Cylinder468  label="Válec468"
  Angle = 360
  AttacherType = Attacher::AttachEngine3D
  Height = 3
  Placement = pos=(22.5,-19,4.5) rot=(1,0,0;1.5708rad)
  Radius = 3
FEATURE [Part::Cylinder] Cylinder469  label="Válec469"
  Angle = 360
  AttacherType = Attacher::AttachEngine3D
  Height = 3
  Placement = pos=(11.5,-19,15.5) rot=(1,0,0;1.5708rad)
  Radius = 3
FEATURE [Part::Cylinder] Cylinder470  label="Válec470"
  Angle = 360
  AttacherType = Attacher::AttachEngine3D
  Height = 3
  Placement = pos=(22.5,-19,15.5) rot=(1,0,0;1.5708rad)
  Radius = 3
FEATURE [Part::Compound] Compound225
  Links = -> [Cylinder467,Cylinder468,Cylinder469,Cylinder470]
  Placement = pos=(0,-5,0) rot=(0,0,1;0rad)
FEATURE [Part::Box] Box294  label="Krychle294"
  AttacherType = Attacher::AttachEngine3D
  Height = 8
  Length = 26
  Placement = pos=(-17,-30,6) rot=(0,0,1;0rad)
  Width = 6
FEATURE [Part::Box] Box295  label="Krychle295"
  AttacherType = Attacher::AttachEngine3D
  Height = 8
  Length = 26
  Placement = pos=(25,-30,6) rot=(0,0,1;0rad)
  Width = 6
FEATURE [Part::Cylinder] Cylinder471  label="Válec471"
  Angle = 360
  AttacherType = Attacher::AttachEngine3D
  Height = 6
  Placement = pos=(17,-24,10) rot=(1,0,0;1.5708rad)
  Radius = 28
FEATURE [Part::Cut] Cut276
  Base = -> Cylinder461
  Tool = -> Cylinder466
FEATURE [Part::Cut] Cut277
  Base = -> Cut276
  Tool = -> Compound224
FEATURE [Part::Cut] Cut278
  Base = -> Cut277
  Tool = -> Compound225
FEATURE [Part::Cylinder] Cylinder472  label="Válec472"
  Angle = 360
  AttacherType = Attacher::AttachEngine3D
  Height = 6
  Placement = pos=(17,-24,10) rot=(1,0,0;1.5708rad)
  Radius = 33
FEATURE [Part::Common] Common
  Base = -> Box294
  Tool = -> Cylinder471
FEATURE [Part::Common] Common001
  Base = -> Box295
  Tool = -> Cylinder472
FEATURE [Part::Compound] Compound226  label="ufo_doraznik"
  Links = -> [Cut278,Common,Common001]
  Placement = pos=(27,-58,27) rot=(0.707107,0,-0.707107;3.14159rad)
FEATURE [Mesh::Feature] Mesh022  label="ufo_doraznik (Meshed)"
FEATURE [Mesh::Feature] Mesh023  label="grip_moto_hold (Meshed)"
FEATURE [Part::FeaturePython] Tube017  # WARN: FeaturePython — macro-defined, semantics opaque (R4)
  AttacherType = Attacher::AttachEngine3D
  Height = 12
  InnerRadius = 27
  OuterRadius = 34
  Placement = pos=(17,-92,10) rot=(1,0,0;1.5708rad)
FEATURE [Part::Box] Box296  label="Krychle296"
  AttacherType = Attacher::AttachEngine3D
  Height = 2
  Length = 8
  Placement = pos=(16.5,-22.5,-55) rot=(0,0,1;0rad)
  Width = 6
FEATURE [Part::Box] Box297  label="Krychle297"
  AttacherType = Attacher::AttachEngine3D
  Height = 2
  Length = 8
  Placement = pos=(18.5,20.5,-55) rot=(0,0,1;0rad)
  Width = 6
FEATURE [Part::Box] Box298  label="Krychle298"
  AttacherType = Attacher::AttachEngine3D
  Height = 2
  Length = 8
  Placement = pos=(-24.5,-22.5,-55) rot=(0,0,1;0rad)
  Width = 6
FEATURE [Part::Box] Box299  label="Krychle299"
  AttacherType = Attacher::AttachEngine3D
  Height = 2
  Length = 8
  Placement = pos=(-26.5,20.5,-55) rot=(0,0,1;0rad)
  Width = 6
FEATURE [Part::Box] Box300  label="Krychle300"
  AttacherType = Attacher::AttachEngine3D
  Height = 8
  Length = 42.3
  Placement = pos=(-21.15,-21.15,-70) rot=(0,0,1;0rad)
  Width = 42.3
FEATURE [Part::Cylinder] Cylinder473  label="Válec473"
  Angle = 360
  AttacherType = Attacher::AttachEngine3D
  Height = 3
  Placement = pos=(15.5,15.5,-54) rot=(0,0,1;0rad)
  Radius = 3
FEATURE [Part::Box] Box301  label="Krychle301"
  AttacherType = Attacher::AttachEngine3D
  Height = 20
  Length = 29
  Placement = pos=(-14.5,0,-75) rot=(0,0,1;0rad)
  Width = 45.5
FEATURE [Part::Box] Box302  label="Krychle302"
  AttacherType = Attacher::AttachEngine3D
  Height = 8
  Length = 54
  Placement = pos=(-27,-26,-24) rot=(0,0,1;0rad)
  Width = 52
FEATURE [Part::Box] Box303  label="Krychle303"
  AttacherType = Attacher::AttachEngine3D
  Height = 2
  Length = 8
  Placement = pos=(-24.5,-22.5,-55) rot=(0,0,1;0rad)
  Width = 6
FEATURE [Part::Cylinder] Cylinder474  label="Válec474"
  Angle = 360
  AttacherType = Attacher::AttachEngine3D
  Height = 20
  Placement = pos=(-15.5,15.5,-68) rot=(0,0,1;0rad)
  Radius = 1.5
FEATURE [Part::Cylinder] Cylinder475  label="Válec475"
  Angle = 360
  AttacherType = Attacher::AttachEngine3D
  Height = 20
  Placement = pos=(15.5,-15.5,-68) rot=(0,0,1;0rad)
  Radius = 1.5
FEATURE [Part::Box] Box304  label="Krychle304"
  AttacherType = Attacher::AttachEngine3D
  Height = 20
  Length = 29
  Placement = pos=(-14.5,0,-75) rot=(0,0,1;0rad)
  Width = 45.5
FEATURE [Part::Cylinder] Cylinder476  label="Válec476"
  Angle = 360
  AttacherType = Attacher::AttachEngine3D
  Height = 20
  Placement = pos=(21,23,-28) rot=(0,0,1;0rad)
  Radius = 1.5
FEATURE [Part::Cylinder] Cylinder477  label="Válec477"
  Angle = 360
  AttacherType = Attacher::AttachEngine3D
  Height = 3
  Placement = pos=(-15.5,15.5,-54) rot=(0,0,1;0rad)
  Radius = 3
FEATURE [Part::Cylinder] Cylinder478  label="Válec478"
  Angle = 360
  AttacherType = Attacher::AttachEngine3D
  Height = 3
  Placement = pos=(-15.5,-15.5,-54) rot=(0,0,1;0rad)
  Radius = 3
FEATURE [Part::Cylinder] Cylinder479  label="Válec479"
  Angle = 360
  AttacherType = Attacher::AttachEngine3D
  Height = 20
  Placement = pos=(15.5,-15.5,-68) rot=(0,0,1;0rad)
  Radius = 1.5
FEATURE [Part::Cylinder] Cylinder480  label="Válec480"
  Angle = 360
  AttacherType = Attacher::AttachEngine3D
  Height = 20
  Placement = pos=(10.48,15.75,-50) rot=(0,0,1;0rad)
  Radius = 1.5
FEATURE [Part::Cylinder] Cylinder481  label="Válec481"
  Angle = 360
  AttacherType = Attacher::AttachEngine3D
  Height = 20
  Placement = pos=(15.5,15.5,-68) rot=(0,0,1;0rad)
  Radius = 1.5
FEATURE [Part::Box] Box305  label="Krychle305"
  AttacherType = Attacher::AttachEngine3D
  Height = 11
  Length = 34
  Placement = pos=(-17,-17,-73) rot=(0,0,1;0rad)
  Width = 34
FEATURE [Part::Cylinder] Cylinder482  label="Válec482"
  Angle = 360
  AttacherType = Attacher::AttachEngine3D
  Height = 3
  Placement = pos=(15.5,-15.5,-54) rot=(0,0,1;0rad)
  Radius = 3
FEATURE [Part::Box] Box306  label="Krychle306"
  AttacherType = Attacher::AttachEngine3D
  Height = 11
  Length = 46.3
  Placement = pos=(-23.15,-23.15,-73) rot=(0,0,1;0rad)
  Width = 46.3
FEATURE [Part::Cylinder] Cylinder483  label="Válec483"
  Angle = 360
  AttacherType = Attacher::AttachEngine3D
  Height = 20
  Placement = pos=(-10.48,15.75,-50) rot=(0,0,1;0rad)
  Radius = 1.5
FEATURE [Part::Compound] Compound228
  Links = -> [Cylinder483,Cylinder480]
  Placement = pos=(0,0,-10) rot=(0,0,1;0rad)
FEATURE [Part::Box] Box307  label="Krychle307"
  AttacherType = Attacher::AttachEngine3D
  Height = 2
  Length = 8
  Placement = pos=(16.5,-22.5,-55) rot=(0,0,1;0rad)
  Width = 6
FEATURE [Part::Box] Box308  label="Krychle308"
  AttacherType = Attacher::AttachEngine3D
  Height = 8
  Length = 46.3
  Placement = pos=(-23.15,-23.15,-70) rot=(0,0,1;0rad)
  Width = 46.3
FEATURE [Part::Cylinder] Cylinder484  label="Válec484"
  Angle = 360
  AttacherType = Attacher::AttachEngine3D
  Height = 20
  Placement = pos=(15.5,15.5,-68) rot=(0,0,1;0rad)
  Radius = 1.5
FEATURE [Part::Cylinder] Cylinder485  label="Válec485"
  Angle = 360
  AttacherType = Attacher::AttachEngine3D
  Height = 20
  Placement = pos=(-21,23,-28) rot=(0,0,1;0rad)
  Radius = 1.5
FEATURE [Part::Box] Box309  label="Krychle309"
  AttacherType = Attacher::AttachEngine3D
  Height = 2
  Length = 8
  Placement = pos=(16.5,16.5,-55) rot=(0,0,1;0rad)
  Width = 6
FEATURE [Part::Box] Box310  label="Krychle310"
  AttacherType = Attacher::AttachEngine3D
  Height = 2
  Length = 8
  Placement = pos=(-24.5,16.5,-55) rot=(0,0,1;0rad)
  Width = 6
FEATURE [Part::Compound] Compound227
  Links = -> [Box309,Box310,Box307,Box303]
  Placement = pos=(0,0,10) rot=(0,0,1;0rad)
FEATURE [Part::Cylinder] Cylinder486  label="Válec486"
  Angle = 360
  AttacherType = Attacher::AttachEngine3D
  Height = 20
  Placement = pos=(-15.5,-15.5,-68) rot=(0,0,1;0rad)
  Radius = 1.5
FEATURE [Part::Cylinder] Cylinder487  label="Válec487"
  Angle = 360
  AttacherType = Attacher::AttachEngine3D
  Height = 20
  Placement = pos=(21,-23,-28) rot=(0,0,1;0rad)
  Radius = 1.5
FEATURE [Part::Cylinder] Cylinder488  label="Válec488"
  Angle = 360
  AttacherType = Attacher::AttachEngine3D
  Height = 20
  Placement = pos=(-15.5,-15.5,-68) rot=(0,0,1;0rad)
  Radius = 1.5
FEATURE [Part::Cylinder] Cylinder489  label="Válec489"
  Angle = 360
  AttacherType = Attacher::AttachEngine3D
  Height = 20
  Placement = pos=(-15.5,15.5,-68) rot=(0,0,1;0rad)
  Radius = 1.5
FEATURE [Part::Box] Box311  label="Krychle311"
  AttacherType = Attacher::AttachEngine3D
  Height = 8
  Length = 7
  Placement = pos=(-22,15,-74) rot=(0,0,1;0rad)
  Width = 7
FEATURE [Part::Cylinder] Cylinder490  label="Válec490"
  Angle = 360
  AttacherType = Attacher::AttachEngine3D
  Height = 8
  Placement = pos=(-15.15,15.15,-74) rot=(0,0,1;0rad)
  Radius = 6
FEATURE [Part::Cut] Cut282
  Base = -> Box311
  Placement = pos=(0,0,0) rot=(0,0,1;3.14159rad)
  Tool = -> Cylinder490
FEATURE [Part::Cut] Cut283
  Base = -> Box308
  Placement = pos=(0,0,-4) rot=(0,0,1;0rad)
  Tool = -> Box300
FEATURE [Part::Cut] Cut286
  Base = -> Cut283
  Tool = -> Box301
FEATURE [Part::Cut] Cut288
  Base = -> Box306
  Placement = pos=(0,0,7) rot=(0,0,1;0rad)
  Tool = -> Box305
FEATURE [Part::Cut] Cut294
  Base = -> Box311
  Placement = pos=(0,0,0) rot=(0,0,1;1.5708rad)
  Tool = -> Cylinder490
FEATURE [Part::Cut] Cut295
  Base = -> Box311
  Placement = pos=(0,0,0) rot=(0,0,-1;1.5708rad)
  Tool = -> Cylinder490
FEATURE [Part::Cut] Cut296
  Base = -> Box311
  Tool = -> Cylinder490
FEATURE [Part::Compound] Compound230
  Links = -> [Cylinder478,Cylinder482,Cylinder477,Cylinder473]
FEATURE [Part::Compound] Compound233
  Links = -> [Cut296,Cut294,Cut282,Cut295]
FEATURE [Part::Compound] Compound229
  Links = -> [Compound233,Cut286]
  Placement = pos=(17,-24,10) rot=(-1,0,0;1.5708rad)
FEATURE [Part::Compound] Compound234
  Links = -> [Cylinder484,Cylinder474,Cylinder475,Cylinder488]
FEATURE [Part::Cut] Cut279
  Base = -> Cut288
  Tool = -> Compound234
FEATURE [Part::Cut] Cut284
  Base = -> Cut279
  Tool = -> Box304
FEATURE [Part::Compound] Compound235
  Links = -> [Box297,Box299,Box296,Box298]
  Placement = pos=(0,0,-200) rot=(0,0,1;0rad)
FEATURE [Part::Cut] Cut293
  Base = -> Cut284
  Tool = -> Compound235
FEATURE [Part::Compound] Compound237
  Links = -> [Cylinder481,Cylinder489,Cylinder479,Cylinder486]
  Placement = pos=(0,0,4) rot=(0,0,1;0rad)
FEATURE [Part::Cylinder] Cylinder491  label="Válec491"
  Angle = 360
  AttacherType = Attacher::AttachEngine3D
  Height = 20
  Placement = pos=(19.5,19.5,-28) rot=(0,0,1;0rad)
  Radius = 1.5
FEATURE [Part::Cylinder] Cylinder492  label="Válec492"
  Angle = 360
  AttacherType = Attacher::AttachEngine3D
  Height = 20
  Placement = pos=(-19.5,19.5,-28) rot=(0,0,1;0rad)
  Radius = 1.5
FEATURE [Part::Cylinder] Cylinder493  label="Válec493"
  Angle = 360
  AttacherType = Attacher::AttachEngine3D
  Height = 20
  Placement = pos=(-19.5,-19.5,-28) rot=(0,0,1;0rad)
  Radius = 1.5
FEATURE [Part::Cylinder] Cylinder494  label="Válec494"
  Angle = 360
  AttacherType = Attacher::AttachEngine3D
  Height = 20
  Placement = pos=(19.5,-19.5,-28) rot=(0,0,1;0rad)
  Radius = 1.5
FEATURE [Part::Compound] Compound232
  Links = -> [Cylinder493,Cylinder492,Cylinder494,Cylinder491]
  Placement = pos=(0,0,-33) rot=(0,0,1;0rad)
FEATURE [Part::Cut] Cut292
  Base = -> Cut293
  Placement = pos=(17,-24,10) rot=(-1,0,0;1.5708rad)
  Tool = -> Compound232
FEATURE [Part::Compound] Compound239
  Links = -> [Cut292,Compound229]
  Placement = pos=(34,-2,20) rot=(0,1,0;3.14159rad)
FEATURE [Part::Chamfer] Chamfer046
  Base = -> Compound239
  Edges = 2 edges r=2: [Edge3,Edge135]
FEATURE [Part::Chamfer] Chamfer044
  Base = -> Chamfer046
  Edges = 2 edges r=2: [Edge55,Edge110]
FEATURE [Part::Chamfer] Chamfer045
  Base = -> Chamfer044
  Edges = 4 edges r=2: [Edge27,Edge33,Edge93,Edge99]
FEATURE [Part::Cylinder] Cylinder495  label="Válec495"
  Angle = 360
  AttacherType = Attacher::AttachEngine3D
  Height = 50
  Placement = pos=(0,0,-29) rot=(0,0,1;0rad)
  Radius = 8
FEATURE [Part::Cut] Cut280
  Base = -> Box302
  Tool = -> Cylinder495
FEATURE [Part::Cylinder] Cylinder496  label="Válec496"
  Angle = 360
  AttacherType = Attacher::AttachEngine3D
  Height = 20
  Placement = pos=(-21,-23,-28) rot=(0,0,1;0rad)
  Radius = 1.5
FEATURE [Part::Compound] Compound236
  Links = -> [Cylinder496,Cylinder476,Cylinder485,Cylinder487]
FEATURE [Part::Cut] Cut287
  Base = -> Cut280
  Tool = -> Compound236
FEATURE [Part::Compound] Compound231
  Links = -> [Cut287]
  Placement = pos=(0,0,-30) rot=(0,0,1;0rad)
FEATURE [Part::Cut] Cut289
  Base = -> Compound231
  Tool = -> Compound227
FEATURE [Part::Cut] Cut285
  Base = -> Cut289
  Tool = -> Compound228
FEATURE [Part::Cut] Cut281
  Base = -> Cut285
  Tool = -> Compound237
FEATURE [Part::Cut] Cut290
  Base = -> Cut281
  Placement = pos=(17,-127,10) rot=(1,0,0;1.5708rad)
  Tool = -> Compound230
FEATURE [Part::Box] Box312  label="Krychle312"
  AttacherType = Attacher::AttachEngine3D
  Height = 2
  Length = 6
  Placement = pos=(25,19,-55) rot=(0,0,1;0rad)
  Width = 8
FEATURE [Part::Box] Box313  label="Krychle313"
  AttacherType = Attacher::AttachEngine3D
  Height = 2
  Length = 6
  Placement = pos=(-17,-25,-55) rot=(0,0,1;0rad)
  Width = 8
FEATURE [Part::Box] Box314  label="Krychle314"
  AttacherType = Attacher::AttachEngine3D
  Height = 2
  Length = 6
  Placement = pos=(-17,19,-55) rot=(0,0,1;0rad)
  Width = 8
FEATURE [Part::Box] Box315  label="Krychle315"
  AttacherType = Attacher::AttachEngine3D
  Height = 2
  Length = 6
  Placement = pos=(25,-25,-55) rot=(0,0,1;0rad)
  Width = 8
FEATURE [Part::Compound] Compound238
  Links = -> [Box312,Box314,Box315,Box313]
  Placement = pos=(10,-24,11) rot=(-1,0,0;1.5708rad)
FEATURE [Part::Cut] Cut291
  Base = -> Cut290
  Tool = -> Compound238
FEATURE [Part::Chamfer] Chamfer043
  Base = -> Cut291
  Edges = 1 edges r=3: [Edge17]
FEATURE [Part::Chamfer] Chamfer048
  Base = -> Chamfer043
  Edges = 1 edges r=3: [Edge33]
FEATURE [Part::Cylinder] Cylinder501  label="Válec501"
  Angle = 360
  AttacherType = Attacher::AttachEngine3D
  Height = 20
  Placement = pos=(39.5,-17,10) rot=(1,0,0;1.5708rad)
  Radius = 2.65
FEATURE [Part::Cylinder] Cylinder502  label="Válec502"
  Angle = 360
  AttacherType = Attacher::AttachEngine3D
  Height = 20
  Placement = pos=(-5.5,-17,10) rot=(1,0,0;1.5708rad)
  Radius = 2.65
FEATURE [Part::Compound] Compound241
  Links = -> [Cylinder502,Cylinder501]
  Placement = pos=(0,-40,0) rot=(0,0,1;0rad)
FEATURE [Part::Cut] Cut297
  Base = -> Chamfer048
  Tool = -> Compound241
FEATURE [Part::Box] Box320  label="Krychle320"
  AttacherType = Attacher::AttachEngine3D
  Height = 32
  Length = 4
  Placement = pos=(-12,-134,-6) rot=(0,0,1;0rad)
  Width = 56
FEATURE [Part::Cylinder] Cylinder503  label="Válec503"
  Angle = 360
  AttacherType = Attacher::AttachEngine3D
  Height = 16
  Placement = pos=(-28,12,55) rot=(0,1,0;1.5708rad)
  Radius = 1.5
FEATURE [Part::Cylinder] Cylinder504  label="Válec504"
  Angle = 360
  AttacherType = Attacher::AttachEngine3D
  Height = 16
  Placement = pos=(-28,-12,55) rot=(0,1,0;1.5708rad)
  Radius = 1.5
FEATURE [Part::Cylinder] Cylinder505  label="Válec505"
  Angle = 360
  AttacherType = Attacher::AttachEngine3D
  Height = 16
  Placement = pos=(18,-12,55) rot=(0,1,0;1.5708rad)
  Radius = 1.5
FEATURE [Part::Box] Box321  label="Krychle321"
  AttacherType = Attacher::AttachEngine3D
  Height = 32
  Length = 2
  Placement = pos=(40,-100,-6) rot=(0,0,1;0rad)
  Width = 20
FEATURE [Part::Cylinder] Cylinder506  label="Válec506"
  Angle = 360
  AttacherType = Attacher::AttachEngine3D
  Height = 16
  Placement = pos=(18,12,55) rot=(0,1,0;1.5708rad)
  Radius = 1.5
FEATURE [Part::Compound] Compound244
  Links = -> [Cylinder503,Cylinder504,Cylinder506,Cylinder505]
  Placement = pos=(14,-71,10) rot=(1,0,0;1.5708rad)
FEATURE [Part::Box] Box322  label="Krychle322"
  AttacherType = Attacher::AttachEngine3D
  Height = 32
  Length = 4
  Placement = pos=(42,-134,-6) rot=(0,0,1;0rad)
  Width = 56
FEATURE [Part::Box] Box323  label="Krychle323"
  AttacherType = Attacher::AttachEngine3D
  Height = 32
  Length = 2
  Placement = pos=(-8,-100,-6) rot=(0,0,1;0rad)
  Width = 20
FEATURE [Part::Compound] Compound245
  Links = -> [Box320,Box323,Box321,Box322]
FEATURE [Part::Cut] Cut299
  Base = -> Compound245
  Tool = -> Compound244
FEATURE [Part::Box] Box324  label="Krychle324"
  AttacherType = Attacher::AttachEngine3D
  Height = 32
  Length = 5.85
  Placement = pos=(-10,-138,-6) rot=(0,0,1;0rad)
  Width = 60
FEATURE [Part::Box] Box325  label="Krychle325"
  AttacherType = Attacher::AttachEngine3D
  Height = 32
  Length = 5.85
  Placement = pos=(38.15,-138,-6) rot=(0,0,1;0rad)
  Width = 60
FEATURE [Part::Cylinder] Cylinder507  label="Válec507"
  Angle = 360
  AttacherType = Attacher::AttachEngine3D
  Height = 16
  Placement = pos=(18,-9,64) rot=(0,1,0;1.5708rad)
  Radius = 1.5
FEATURE [Part::Cylinder] Cylinder508  label="Válec508"
  Angle = 360
  AttacherType = Attacher::AttachEngine3D
  Height = 16
  Placement = pos=(18,9,64) rot=(0,1,0;1.5708rad)
  Radius = 1.5
FEATURE [Part::Cylinder] Cylinder509  label="Válec509"
  Angle = 360
  AttacherType = Attacher::AttachEngine3D
  Height = 16
  Placement = pos=(-28,9,64) rot=(0,1,0;1.5708rad)
  Radius = 1.5
FEATURE [Part::Cylinder] Cylinder510  label="Válec510"
  Angle = 360
  AttacherType = Attacher::AttachEngine3D
  Height = 16
  Placement = pos=(-28,-9,64) rot=(0,1,0;1.5708rad)
  Radius = 1.5
FEATURE [Part::Compound] Compound246
  Links = -> [Cylinder509,Cylinder510,Cylinder508,Cylinder507]
  Placement = pos=(14,-71,10) rot=(1,0,0;1.5708rad)
FEATURE [Part::Compound] Compound247
  Links = -> [Box324,Box325]
FEATURE [Part::Cut] Cut300
  Base = -> Compound247
  Tool = -> Compound246
FEATURE [Part::Box] Box326  label="Krychle326"
  AttacherType = Attacher::AttachEngine3D
  Height = 32
  Length = 5.85
  Placement = pos=(-10,-134,-6) rot=(0,0,1;0rad)
  Width = 56
FEATURE [Part::Box] Box327  label="Krychle327"
  AttacherType = Attacher::AttachEngine3D
  Height = 32
  Length = 5.85
  Placement = pos=(38.15,-134,-6) rot=(0,0,1;0rad)
  Width = 56
FEATURE [Part::Compound] Compound248
  Links = -> [Box326,Box327]
FEATURE [Part::Chamfer] Chamfer049
  Base = -> Cut300
  Edges = 2 edges r=2: [Edge29,Edge31]
FEATURE [Part::Chamfer] Chamfer050
  Base = -> Chamfer049
  Edges = 2 edges r=2: [Edge26,Edge28]
FEATURE [Part::Chamfer] Chamfer051
  Base = -> Compound248
  Edges = 2 edges r=2: [Edge2,Edge4]
FEATURE [Part::Chamfer] Chamfer052
  Base = -> Chamfer051
  Edges = 2 edges r=2: [Edge24,Edge26]
FEATURE [Part::Cut] Cut301
  Base = -> Tube017
  Tool = -> Chamfer052
FEATURE [Part::Box] Box328  label="Krychle328"
  AttacherType = Attacher::AttachEngine3D
  Height = 20
  Length = 29
  Placement = pos=(-14.5,0,-75) rot=(0,0,1;0rad)
  Width = 45.5
FEATURE [Part::Box] Box329  label="Krychle329"
  AttacherType = Attacher::AttachEngine3D
  Height = 8
  Length = 42.3
  Placement = pos=(-21.15,-21.15,-70) rot=(0,0,1;0rad)
  Width = 42.3
FEATURE [Part::Box] Box330  label="Krychle330"
  AttacherType = Attacher::AttachEngine3D
  Height = 8
  Length = 46.3
  Placement = pos=(-23.15,-23.15,-70) rot=(0,0,1;0rad)
  Width = 46.3
FEATURE [Part::Box] Box331  label="Krychle331"
  AttacherType = Attacher::AttachEngine3D
  Height = 8
  Length = 7
  Placement = pos=(-22,15,-74) rot=(0,0,1;0rad)
  Width = 7
FEATURE [Part::Cylinder] Cylinder511  label="Válec511"
  Angle = 360
  AttacherType = Attacher::AttachEngine3D
  Height = 8
  Placement = pos=(-15.15,15.15,-74) rot=(0,0,1;0rad)
  Radius = 6
FEATURE [Part::Cut] Cut302
  Base = -> Box331
  Placement = pos=(0,0,0) rot=(0,0,1;1.5708rad)
  Tool = -> Cylinder511
FEATURE [Part::Cut] Cut303
  Base = -> Box330
  Placement = pos=(0,0,-4) rot=(0,0,1;0rad)
  Tool = -> Box329
FEATURE [Part::Cut] Cut304
  Base = -> Box331
  Placement = pos=(0,0,0) rot=(0,0,-1;1.5708rad)
  Tool = -> Cylinder511
FEATURE [Part::Cut] Cut305
  Base = -> Box331
  Tool = -> Cylinder511
FEATURE [Part::Cut] Cut306
  Base = -> Cut303
  Tool = -> Box328
FEATURE [Part::Cut] Cut307
  Base = -> Box331
  Placement = pos=(0,0,0) rot=(0,0,1;3.14159rad)
  Tool = -> Cylinder511
FEATURE [Part::Compound] Compound250
  Links = -> [Cut305,Cut302,Cut307,Cut304]
FEATURE [Part::Compound] Compound249
  Links = -> [Compound250,Cut306]
  Placement = pos=(17,-24,10) rot=(-1,0,0;1.5708rad)
FEATURE [Part::Box] Box332  label="Krychle332"
  AttacherType = Attacher::AttachEngine3D
  Height = 12
  Length = 46.3
  Placement = pos=(-23.15,-23.15,-70) rot=(0,0,1;0rad)
  Width = 46.3
FEATURE [Part::Box] Box333  label="Krychle333"
  AttacherType = Attacher::AttachEngine3D
  Height = 12
  Length = 42.3
  Placement = pos=(-21.15,-21.15,-70) rot=(0,0,1;0rad)
  Width = 42.3
FEATURE [Part::Cut] Cut308
  Base = -> Box332
  Placement = pos=(17,-32,10) rot=(-1,0,0;1.5708rad)
  Tool = -> Box333
FEATURE [Part::Box] Box334  label="Krychle334"
  AttacherType = Attacher::AttachEngine3D
  Height = 12
  Length = 7
  Placement = pos=(-22,15,-74) rot=(0,0,1;0rad)
  Width = 7
FEATURE [Part::Cylinder] Cylinder512  label="Válec512"
  Angle = 360
  AttacherType = Attacher::AttachEngine3D
  Height = 12
  Placement = pos=(-15.15,15.15,-74) rot=(0,0,1;0rad)
  Radius = 6
FEATURE [Part::Cut] Cut309
  Base = -> Box334
  Placement = pos=(0,0,0) rot=(0,0,1;1.5708rad)
  Tool = -> Cylinder512
FEATURE [Part::Cut] Cut310
  Base = -> Box334
  Placement = pos=(0,0,0) rot=(0,0,-1;1.5708rad)
  Tool = -> Cylinder512
FEATURE [Part::Cut] Cut311
  Base = -> Box334
  Tool = -> Cylinder512
FEATURE [Part::Cut] Cut312
  Base = -> Box334
  Placement = pos=(0,0,0) rot=(0,0,1;3.14159rad)
  Tool = -> Cylinder512
FEATURE [Part::Compound] Compound251
  Links = -> [Cut311,Cut309,Cut312,Cut310]
  Placement = pos=(17,-28,10) rot=(-1,0,0;1.5708rad)
FEATURE [Part::Box] Box335  label="Krychle335"
  AttacherType = Attacher::AttachEngine3D
  Height = 36
  Length = 7.85
  Placement = pos=(-10,-134,-8) rot=(0,0,1;0rad)
  Width = 56
FEATURE [Part::Box] Box336  label="Krychle336"
  AttacherType = Attacher::AttachEngine3D
  Height = 36
  Length = 7.85
  Placement = pos=(36.15,-134,-8) rot=(0,0,1;0rad)
  Width = 56
FEATURE [Part::Compound] Compound253
  Links = -> [Box335,Box336]
FEATURE [Part::Box] Box337  label="Krychle337"
  AttacherType = Attacher::AttachEngine3D
  Height = 36
  Length = 7.85
  Placement = pos=(36.15,-134,-8) rot=(0,0,1;0rad)
  Width = 56
FEATURE [Part::Box] Box338  label="Krychle338"
  AttacherType = Attacher::AttachEngine3D
  Height = 36
  Length = 7.85
  Placement = pos=(-10,-134,-8) rot=(0,0,1;0rad)
  Width = 56
FEATURE [Part::Compound] Compound254
  Links = -> [Box338,Box337]
FEATURE [Part::Cut] Cut313
  Base = -> Compound251
  Tool = -> Compound253
FEATURE [Part::Cut] Cut314
  Base = -> Cut308
  Tool = -> Compound254
FEATURE [Part::Compound] Compound255
  Links = -> [Cut313,Cut314]
  Placement = pos=(0,-2,0) rot=(0,0,1;0rad)
FEATURE [Part::Torus] Torus  label="Anuloid"
  Angle1 = -180
  Angle2 = 180
  Angle3 = 360
  AttacherType = Attacher::AttachEngine3D
  Placement = pos=(17,-98,10) rot=(1,0,0;1.5708rad)
  Radius1 = 33.8
  Radius2 = 2
FEATURE [Part::Cut] Cut315
  Base = -> Cut301
  Tool = -> Torus
FEATURE [Part::Torus] Torus001  label="Anuloid001"
  Angle1 = -180
  Angle2 = 180
  Angle3 = 360
  AttacherType = Attacher::AttachEngine3D
  Placement = pos=(17,-98,10) rot=(1,0,0;1.5708rad)
  Radius1 = 33.8
  Radius2 = 2
FEATURE [Part::Cut] Cut316
  Base = -> Compound255
  Placement = pos=(0,-2,0) rot=(0,0,1;0rad)
  Tool = -> Torus001
FEATURE [Part::FeaturePython] Tube018  # WARN: FeaturePython — macro-defined, semantics opaque (R4)
  AttacherType = Attacher::AttachEngine3D
  Height = 11.5
  InnerRadius = 34.5
  OuterRadius = 39
  Placement = pos=(17,-92,10) rot=(1,0,0;1.5708rad)
FEATURE [Part::Torus] Torus002  label="Anuloid002"
  Angle1 = -180
  Angle2 = 180
  Angle3 = 360
  AttacherType = Attacher::AttachEngine3D
  Placement = pos=(17,-98,10) rot=(1,0,0;1.5708rad)
  Radius1 = 34
  Radius2 = 2
FEATURE [Part::Cut] Cut317
  Base = -> Tube018
  Tool = -> Torus002
FEATURE [Part::Torus] Torus003  label="Anuloid003"
  Angle1 = -180
  Angle2 = 180
  Angle3 = 360
  AttacherType = Attacher::AttachEngine3D
  Placement = pos=(0,0,23.5) rot=(0,0,1;0rad)
  Radius1 = 20
  Radius2 = 2.2
FEATURE [Part::FeaturePython] Tube019  # WARN: FeaturePython — macro-defined, semantics opaque (R4)
  AttacherType = Attacher::AttachEngine3D
  Height = 20
  InnerRadius = 21
  OuterRadius = 25
  Placement = pos=(0,0,10) rot=(0,0,1;0rad)
FEATURE [Part::Cut] Cut322
  Base = -> Tube019
  Tool = -> Torus003
FEATURE [Part::Cylinder] Cylinder513  label="Válec513"
  Angle = 360
  AttacherType = Attacher::AttachEngine3D
  Height = 10
  Placement = pos=(-23,0,8) rot=(0,0,1;1.5708rad)
  Radius = 1
FEATURE [Part::Box] Box339  label="Krychle339"
  AttacherType = Attacher::AttachEngine3D
  Height = 1.4
  Length = 4
  Placement = pos=(16.2635,-13.435,14) rot=(0,0,1;3.92699rad)
  Width = 4
FEATURE [Part::Cylinder] Cylinder514  label="Válec514"
  Angle = 360
  AttacherType = Attacher::AttachEngine3D
  Height = 10
  Placement = pos=(23,1.1e-14,8) rot=(0,0,-1;1.5708rad)
  Radius = 1
FEATURE [Part::Cylinder] Cylinder515  label="Válec515"
  Angle = 360
  AttacherType = Attacher::AttachEngine3D
  Height = 10
  Placement = pos=(4e-15,-23,8) rot=(0,0,1;3.14159rad)
  Radius = 1
FEATURE [Part::Cylinder] Cylinder516  label="Válec516"
  Angle = 360
  AttacherType = Attacher::AttachEngine3D
  Height = 10
  Placement = pos=(0,23,8) rot=(0,0,1;0rad)
  Radius = 1
FEATURE [Part::Cylinder] Cylinder517  label="Válec517"
  Angle = 360
  AttacherType = Attacher::AttachEngine3D
  Height = 10
  Placement = pos=(16.26,16.26,8) rot=(0,0,-1;0.785398rad)
  Radius = 1
FEATURE [Part::Box] Box340  label="Krychle340"
  AttacherType = Attacher::AttachEngine3D
  Height = 1.4
  Length = 4
  Placement = pos=(2,-21,14) rot=(0,0,1;3.14159rad)
  Width = 4
FEATURE [Part::Cylinder] Cylinder518  label="Válec518"
  Angle = 360
  AttacherType = Attacher::AttachEngine3D
  Height = 10
  Placement = pos=(-16.26,-16.26,8) rot=(0,0,1;2.35619rad)
  Radius = 1
FEATURE [Part::Cylinder] Cylinder519  label="Válec519"
  Angle = 360
  AttacherType = Attacher::AttachEngine3D
  Height = 10
  Placement = pos=(16.26,-16.26,8) rot=(0,0,1;3.92699rad)
  Radius = 1
FEATURE [Part::Cylinder] Cylinder520  label="Válec520"
  Angle = 360
  AttacherType = Attacher::AttachEngine3D
  Height = 10
  Placement = pos=(20,0,23.5) rot=(0,0,1;0rad)
  Radius = 2.2
FEATURE [Part::Cylinder] Cylinder521  label="Válec521"
  Angle = 360
  AttacherType = Attacher::AttachEngine3D
  Height = 10
  Placement = pos=(-16.26,16.26,8) rot=(0,0,1;0.785398rad)
  Radius = 1
FEATURE [Part::Compound] Compound256
  Links = -> [Cylinder516,Cylinder517,Cylinder514,Cylinder515,Cylinder519,Cylinder518,Cylinder521,Cylinder513]
FEATURE [Part::Box] Box341  label="Krychle341"
  AttacherType = Attacher::AttachEngine3D
  Height = 1.4
  Length = 4
  Placement = pos=(-2,21,14) rot=(0,0,1;0rad)
  Width = 4
FEATURE [Part::Box] Box342  label="Krychle342"
  AttacherType = Attacher::AttachEngine3D
  Height = 1.4
  Length = 4
  Placement = pos=(-16.2635,13.435,14) rot=(0,0,1;0.785398rad)
  Width = 4
FEATURE [Part::Box] Box343  label="Krychle343"
  AttacherType = Attacher::AttachEngine3D
  Height = 1.4
  Length = 4
  Placement = pos=(-21,-2,14) rot=(0,0,1;1.5708rad)
  Width = 4
FEATURE [Part::Box] Box344  label="Krychle344"
  AttacherType = Attacher::AttachEngine3D
  Height = 1.4
  Length = 4
  Placement = pos=(-13.435,-16.2635,14) rot=(0,0,1;2.35619rad)
  Width = 4
FEATURE [Part::Box] Box345  label="Krychle345"
  AttacherType = Attacher::AttachEngine3D
  Height = 1.4
  Length = 4
  Placement = pos=(21,2,14) rot=(0,0,-1;1.5708rad)
  Width = 4
FEATURE [Part::Box] Box346  label="Krychle346"
  AttacherType = Attacher::AttachEngine3D
  Height = 1.4
  Length = 4
  Placement = pos=(13.435,16.2635,14) rot=(0,0,-1;0.785398rad)
  Width = 4
FEATURE [Part::Compound] Compound269
  Links = -> [Box341,Box342,Box343,Box344,Box340,Box339,Box345,Box346]
FEATURE [Part::Cut] Cut321
  Base = -> Cut322
  Tool = -> Compound269
FEATURE [Part::Cut] Cut319
  Base = -> Cut321
  Tool = -> Compound256
FEATURE [Part::Cut] Cut318  label="gearovina-mini_loziskovina"
  Base = -> Cut319
  Tool = -> Cylinder520
FEATURE [Part::FeaturePython] Tube020  # WARN: FeaturePython — macro-defined, semantics opaque (R4)
  AttacherType = Attacher::AttachEngine3D
  Height = 6
  InnerRadius = 20
  OuterRadius = 25
  Placement = pos=(0,0,4) rot=(0,0,1;0rad)
FEATURE [Part::FeaturePython] Tube021  # WARN: FeaturePython — macro-defined, semantics opaque (R4)
  AttacherType = Attacher::AttachEngine3D
  Height = 6
  InnerRadius = 17
  OuterRadius = 21
  Placement = pos=(0,0,-16) rot=(0,0,1;0rad)
FEATURE [Part::Box] Box347  label="Krychle347"
  AttacherType = Attacher::AttachEngine3D
  Height = 6
  Length = 4
  Placement = pos=(10,17,5) rot=(0,0,1;0rad)
  Width = 1.4
FEATURE [Part::Box] Box348  label="Krychle348"
  AttacherType = Attacher::AttachEngine3D
  Height = 6
  Length = 4
  Placement = pos=(-14,17,5) rot=(0,0,1;0rad)
  Width = 1.4
FEATURE [Part::Compound] Compound268
  Links = -> [Box347,Box348]
FEATURE [Part::Cylinder] Cylinder522  label="Válec522"
  Angle = 360
  AttacherType = Attacher::AttachEngine3D
  Height = 10
  Placement = pos=(-16.2635,16.2635,4) rot=(0,0,1;0.785398rad)
  Radius = 1
FEATURE [Part::Cylinder] Cylinder523  label="Válec523"
  Angle = 360
  AttacherType = Attacher::AttachEngine3D
  Height = 10
  Placement = pos=(16.2635,16.2635,4) rot=(0,0,-1;0.785398rad)
  Radius = 1
FEATURE [Part::Cylinder] Cylinder524  label="Válec524"
  Angle = 360
  AttacherType = Attacher::AttachEngine3D
  Height = 10
  Placement = pos=(0,23,4) rot=(0,0,1;0rad)
  Radius = 1
FEATURE [Part::Cylinder] Cylinder525  label="Válec525"
  Angle = 360
  AttacherType = Attacher::AttachEngine3D
  Height = 10
  Placement = pos=(16.2635,-16.2635,4) rot=(0,0,1;3.92699rad)
  Radius = 1
FEATURE [Part::Cylinder] Cylinder526  label="Válec526"
  Angle = 360
  AttacherType = Attacher::AttachEngine3D
  Height = 10
  Placement = pos=(-23,-1e-15,4) rot=(0,0,1;1.5708rad)
  Radius = 1
FEATURE [Part::Cylinder] Cylinder527  label="Válec527"
  Angle = 360
  AttacherType = Attacher::AttachEngine3D
  Height = 10
  Placement = pos=(-16.2635,-16.2635,4) rot=(0,0,1;2.35619rad)
  Radius = 1
FEATURE [Part::Cylinder] Cylinder528  label="Válec528"
  Angle = 360
  AttacherType = Attacher::AttachEngine3D
  Height = 10
  Placement = pos=(12,25,8) rot=(1,0,0;1.5708rad)
  Radius = 1
FEATURE [Part::Cylinder] Cylinder529  label="Válec529"
  Angle = 360
  AttacherType = Attacher::AttachEngine3D
  Height = 2
  Placement = pos=(0,23,4) rot=(0,0,1;0rad)
  Radius = 2
FEATURE [Part::Cylinder] Cylinder530  label="Válec530"
  Angle = 360
  AttacherType = Attacher::AttachEngine3D
  Height = 2
  Placement = pos=(-16.2635,-16.2635,4) rot=(0,0,1;2.35619rad)
  Radius = 2
FEATURE [Part::Cylinder] Cylinder531  label="Válec531"
  Angle = 360
  AttacherType = Attacher::AttachEngine3D
  Height = 10
  Placement = pos=(23,1.1e-14,4) rot=(0,0,-1;1.5708rad)
  Radius = 1
FEATURE [Part::Cylinder] Cylinder532  label="Válec532"
  Angle = 360
  AttacherType = Attacher::AttachEngine3D
  Height = 2
  Placement = pos=(-23,-1e-15,4) rot=(0,0,1;1.5708rad)
  Radius = 2
FEATURE [Part::Cylinder] Cylinder533  label="Válec533"
  Angle = 360
  AttacherType = Attacher::AttachEngine3D
  Height = 10
  Placement = pos=(-12,25,8) rot=(1,0,0;1.5708rad)
  Radius = 1
FEATURE [Part::Compound] Compound267
  Links = -> [Cylinder528,Cylinder533]
FEATURE [Part::Cylinder] Cylinder534  label="Válec534"
  Angle = 360
  AttacherType = Attacher::AttachEngine3D
  Height = 2
  Placement = pos=(4e-15,-23,4) rot=(0,0,1;3.14159rad)
  Radius = 2
FEATURE [Part::Box] Box036  label="Krychle036"
  AttacherType = Attacher::AttachEngine3D
  Height = 1.4
  Length = 4
  Placement = pos=(-13.435,10.6066,-13) rot=(0,0,1;0.785398rad)
  Width = 4
FEATURE [Part::Box] Box035  label="Krychle035"
  AttacherType = Attacher::AttachEngine3D
  Height = 1.4
  Length = 4
  Placement = pos=(-2,17,-13) rot=(0,0,1;0rad)
  Width = 4
FEATURE [Part::Box] Box349  label="Krychle349"
  AttacherType = Attacher::AttachEngine3D
  Height = 1.4
  Length = 4
  Placement = pos=(10.6066,13.435,-13) rot=(0,0,-1;0.785398rad)
  Width = 4
FEATURE [Part::Cylinder] Cylinder535  label="Válec535"
  Angle = 360
  AttacherType = Attacher::AttachEngine3D
  Height = 2
  Placement = pos=(-16.2635,16.2635,4) rot=(0,0,1;0.785398rad)
  Radius = 2
FEATURE [Part::Box] Box350  label="Krychle350"
  AttacherType = Attacher::AttachEngine3D
  Height = 1.4
  Length = 4
  Placement = pos=(-10.6066,-13.435,-13) rot=(0,0,1;2.35619rad)
  Width = 4
FEATURE [Part::Cylinder] Cylinder536  label="Válec536"
  Angle = 360
  AttacherType = Attacher::AttachEngine3D
  Height = 10
  Placement = pos=(0,19,-20) rot=(0,0,1;0rad)
  Radius = 1
FEATURE [Part::Cylinder] Cylinder537  label="Válec537"
  Angle = 360
  AttacherType = Attacher::AttachEngine3D
  Height = 2
  Placement = pos=(23,1.1e-14,4) rot=(0,0,-1;1.5708rad)
  Radius = 2
FEATURE [Part::Box] Box351  label="Krychle351"
  AttacherType = Attacher::AttachEngine3D
  Height = 1.4
  Length = 4
  Placement = pos=(-17,-2,-13) rot=(0,0,1;1.5708rad)
  Width = 4
FEATURE [Part::Box] Box352  label="Krychle352"
  AttacherType = Attacher::AttachEngine3D
  Height = 1.4
  Length = 4
  Placement = pos=(13.435,-10.6066,-13) rot=(0,0,1;3.92699rad)
  Width = 4
FEATURE [Part::Cylinder] Cylinder538  label="Válec538"
  Angle = 360
  AttacherType = Attacher::AttachEngine3D
  Height = 10
  Placement = pos=(-13.435,13.435,-20) rot=(0,0,1;0.785398rad)
  Radius = 1
FEATURE [Part::Cylinder] Cylinder539  label="Válec539"
  Angle = 360
  AttacherType = Attacher::AttachEngine3D
  Height = 10
  Placement = pos=(-19,-1e-15,-20) rot=(0,0,1;1.5708rad)
  Radius = 1
FEATURE [Part::Cylinder] Cylinder540  label="Válec540"
  Angle = 360
  AttacherType = Attacher::AttachEngine3D
  Height = 2
  Placement = pos=(16.2635,-16.2635,4) rot=(0,0,1;3.92699rad)
  Radius = 2
FEATURE [Part::Cylinder] Cylinder541  label="Válec541"
  Angle = 360
  AttacherType = Attacher::AttachEngine3D
  Height = 2
  Placement = pos=(16.2635,16.2635,4) rot=(0,0,-1;0.785398rad)
  Radius = 2
FEATURE [Part::Compound] Compound264
  Links = -> [Cylinder529,Cylinder535,Cylinder532,Cylinder530,Cylinder534,Cylinder540,Cylinder537,Cylinder541]
FEATURE [Part::Cut] Cut320
  Base = -> Tube020
  Tool = -> Compound264
FEATURE [Part::Box] Box353  label="Krychle353"
  AttacherType = Attacher::AttachEngine3D
  Height = 1.4
  Length = 4
  Placement = pos=(2,-17,-13) rot=(0,0,1;3.14159rad)
  Width = 4
FEATURE [Part::Cylinder] Cylinder542  label="Válec542"
  Angle = 360
  AttacherType = Attacher::AttachEngine3D
  Height = 10
  Placement = pos=(4e-15,-23,4) rot=(0,0,1;3.14159rad)
  Radius = 1
FEATURE [Part::Compound] Compound257
  Links = -> [Cylinder524,Cylinder522,Cylinder526,Cylinder527,Cylinder542,Cylinder525,Cylinder531,Cylinder523]
FEATURE [Part::Cut] Cut327
  Base = -> Cut320
  Tool = -> Compound257
FEATURE [Part::Cut] Cut331
  Base = -> Cut327
  Tool = -> Compound268
FEATURE [Part::Cylinder] Cylinder543  label="Válec543"
  Angle = 360
  AttacherType = Attacher::AttachEngine3D
  Height = 16
  Placement = pos=(4,18,-14) rot=(0,1,0;1.5708rad)
  Radius = 1
FEATURE [Part::Box] Box354  label="Krychle354"
  AttacherType = Attacher::AttachEngine3D
  Height = 1.4
  Length = 4
  Placement = pos=(17,2,-13) rot=(0,0,-1;1.5708rad)
  Width = 4
FEATURE [Part::Compound] Compound260
  Links = -> [Box035,Box036,Box351,Box350,Box353,Box352,Box354,Box349]
FEATURE [Part::Cut] Cut328
  Base = -> Tube021
  Tool = -> Compound260
FEATURE [Part::Cylinder] Cylinder544  label="Válec544"
  Angle = 360
  AttacherType = Attacher::AttachEngine3D
  Height = 10
  Placement = pos=(-13.435,-13.435,-20) rot=(0,0,1;2.35619rad)
  Radius = 1
FEATURE [Part::Cylinder] Cylinder545  label="Válec545"
  Angle = 360
  AttacherType = Attacher::AttachEngine3D
  Height = 10
  Radius = 21
FEATURE [Part::Cylinder] Cylinder546  label="Válec546"
  Angle = 360
  AttacherType = Attacher::AttachEngine3D
  Height = 10
  Placement = pos=(19,8e-15,-20) rot=(0,0,-1;1.5708rad)
  Radius = 1
FEATURE [Part::Cylinder] Cylinder547  label="Válec547"
  Angle = 360
  AttacherType = Attacher::AttachEngine3D
  Height = 10
  Placement = pos=(-12,25,8) rot=(1,0,0;1.5708rad)
  Radius = 1
FEATURE [Part::Box] Box355  label="Krychle355"
  AttacherType = Attacher::AttachEngine3D
  Height = 6
  Length = 4
  Placement = pos=(-14,17,5) rot=(0,0,1;0rad)
  Width = 1.4
FEATURE [Part::Box] Box356  label="Krychle356"
  AttacherType = Attacher::AttachEngine3D
  Height = 4
  Length = 1.4
  Placement = pos=(-7.4,15,-16) rot=(0,0,1;0rad)
  Width = 6
FEATURE [Part::Cylinder] Cylinder548  label="Válec548"
  Angle = 360
  AttacherType = Attacher::AttachEngine3D
  Height = 10
  Placement = pos=(13.435,13.435,-20) rot=(0,0,-1;0.785398rad)
  Radius = 1
FEATURE [Part::Cylinder] Cylinder549  label="Válec549"
  Angle = 360
  AttacherType = Attacher::AttachEngine3D
  Height = 10
  Placement = pos=(6e-15,-19,-20) rot=(0,0,1;3.14159rad)
  Radius = 1
FEATURE [Part::Cylinder] Cylinder550  label="Válec550"
  Angle = 360
  AttacherType = Attacher::AttachEngine3D
  Height = 10
  Placement = pos=(13.435,-13.435,-20) rot=(0,0,1;3.92699rad)
  Radius = 1
FEATURE [Part::Compound] Compound265
  Links = -> [Cylinder536,Cylinder538,Cylinder539,Cylinder544,Cylinder549,Cylinder550,Cylinder546,Cylinder548]
FEATURE [Part::Cut] Cut326
  Base = -> Cut328
  Tool = -> Compound265
FEATURE [Part::Box] Box357  label="Krychle357"
  AttacherType = Attacher::AttachEngine3D
  Height = 6
  Length = 4
  Placement = pos=(10,17,5) rot=(0,0,1;0rad)
  Width = 1.4
FEATURE [Part::Compound] Compound259
  Links = -> [Box357,Box355]
FEATURE [Part::Cylinder] Cylinder551  label="Válec551"
  Angle = 360
  AttacherType = Attacher::AttachEngine3D
  Height = 10
  Placement = pos=(12,25,8) rot=(1,0,0;1.5708rad)
  Radius = 1
FEATURE [Part::Compound] Compound261
  Links = -> [Cylinder551,Cylinder547]
FEATURE [Part::Cut] Cut324
  Base = -> Cut331
  Tool = -> Compound261
FEATURE [Part::Cylinder] Cylinder552  label="Válec552"
  Angle = 360
  AttacherType = Attacher::AttachEngine3D
  Height = 10
  Radius = 21
FEATURE [Part::Cylinder] Cylinder553  label="Válec553"
  Angle = 360
  AttacherType = Attacher::AttachEngine3D
  Height = 16
  Placement = pos=(-20,18,-14) rot=(0,1,0;1.5708rad)
  Radius = 1
FEATURE [Part::Compound] Compound263
  Links = -> [Cylinder553,Cylinder543]
FEATURE [Part::Box] Box358  label="Krychle358"
  AttacherType = Attacher::AttachEngine3D
  Height = 4
  Length = 1.4
  Placement = pos=(6,15,-16) rot=(0,0,1;0rad)
  Width = 6
FEATURE [Part::Compound] Compound266
  Links = -> [Box356,Box358]
FEATURE [Part::Cut] Cut330
  Base = -> Cut326
  Tool = -> Compound266
FEATURE [Part::Cut] Cut333
  Base = -> Cut330
  Tool = -> Compound263
FEATURE [Part::FeaturePython] wormgear039  # WARN: FeaturePython — macro-defined, semantics opaque (R4)
  AttacherType = Attacher::AttachEngine3D
  Placement = pos=(0,0,0) rot=(0,0,1;1.13796rad)
  beta = 36.4444
  clearance = 0.25
  diameter = 32.5
  head = 0
  height = 12
  module = 0.8
  pressure_angle = 20
  reverse_pitch = false
  teeth = 30
  version = 0.0.3
FEATURE [Part::Cut] Cut329
  Base = -> Cylinder552
  Placement = pos=(0,0,-10) rot=(0,0,1;0rad)
  Tool = -> wormgear039
FEATURE [Part::FeaturePython] wormgear040  # WARN: FeaturePython — macro-defined, semantics opaque (R4)
  AttacherType = Attacher::AttachEngine3D
  Placement = pos=(0,0,0) rot=(0,0,1;1.13446rad)
  beta = 36.4444
  clearance = 0.25
  diameter = 32.5
  head = 0
  height = 12
  module = 0.8
  pressure_angle = 20
  reverse_pitch = true
  teeth = 30
  version = 0.0.3
FEATURE [Part::Cut] Cut323
  Base = -> Cylinder545
  Tool = -> wormgear040
FEATURE [Part::Compound] Compound258  label="gearovina-mini_okruh001"
  Links = -> [Cut329,Cut323]
FEATURE [Part::Cut] Cut325
  Base = -> Compound258
  Tool = -> Compound259
FEATURE [Part::Cut] Cut332
  Base = -> Cut325
  Tool = -> Compound267
FEATURE [Part::Compound] Compound262  label="gearovina-mini_superokruh"
  Links = -> [Cut324,Cut333,Cut332]
FEATURE [Part::FeaturePython] Tube032  # WARN: FeaturePython — macro-defined, semantics opaque (R4)
  AttacherType = Attacher::AttachEngine3D
  Height = 6
  InnerRadius = 17
  OuterRadius = 21
  Placement = pos=(0,0,-22) rot=(0,0,1;0rad)
FEATURE [Part::Cylinder] Cylinder554  label="Válec554"
  Angle = 360
  AttacherType = Attacher::AttachEngine3D
  Height = 10
  Placement = pos=(-13.44,13.44,-24) rot=(0,0,1;0.785398rad)
  Radius = 1
FEATURE [Part::Box] Box359  label="Krychle359"
  AttacherType = Attacher::AttachEngine3D
  Height = 4
  Length = 46.3
  Placement = pos=(-23.15,-23.15,-25) rot=(0,0,1;0rad)
  Width = 46.3
FEATURE [Part::Cylinder] Cylinder555  label="Válec555"
  Angle = 360
  AttacherType = Attacher::AttachEngine3D
  Height = 10
  Placement = pos=(19,8e-15,-24) rot=(0,0,-1;1.5708rad)
  Radius = 1
FEATURE [Part::Cylinder] Cylinder179  label="Válec179"
  Angle = 360
  AttacherType = Attacher::AttachEngine3D
  Height = 2
  Placement = pos=(-13.44,13.44,-22) rot=(0,0,1;0.785398rad)
  Radius = 2
FEATURE [Part::Cylinder] Cylinder556  label="Válec556"
  Angle = 360
  AttacherType = Attacher::AttachEngine3D
  Height = 10
  Placement = pos=(-19,0,-24) rot=(0,0,1;1.5708rad)
  Radius = 1
FEATURE [Part::Cylinder] Cylinder557  label="Válec557"
  Angle = 360
  AttacherType = Attacher::AttachEngine3D
  Height = 10
  Placement = pos=(-13.44,-13.44,-24) rot=(0,0,1;2.35619rad)
  Radius = 1
FEATURE [Part::Cylinder] Cylinder558  label="Válec558"
  Angle = 360
  AttacherType = Attacher::AttachEngine3D
  Height = 10
  Placement = pos=(0,19,-24) rot=(0,0,1;0rad)
  Radius = 1
FEATURE [Part::Cylinder] Cylinder559  label="Válec559"
  Angle = 360
  AttacherType = Attacher::AttachEngine3D
  Height = 10
  Placement = pos=(6e-15,-19,-24) rot=(0,0,1;3.14159rad)
  Radius = 1
FEATURE [Part::Cylinder] Cylinder560  label="Válec560"
  Angle = 360
  AttacherType = Attacher::AttachEngine3D
  Height = 10
  Placement = pos=(13.44,-13.44,-24) rot=(0,0,1;3.92699rad)
  Radius = 1
FEATURE [Part::Cylinder] Cylinder561  label="Válec561"
  Angle = 360
  AttacherType = Attacher::AttachEngine3D
  Height = 10
  Placement = pos=(13.44,13.44,-24) rot=(0,0,-1;0.785398rad)
  Radius = 1
FEATURE [Part::Compound] Compound278
  Links = -> [Cylinder558,Cylinder554,Cylinder556,Cylinder557,Cylinder559,Cylinder560,Cylinder555,Cylinder561]
FEATURE [Part::Cylinder] Cylinder562  label="Válec562"
  Angle = 360
  AttacherType = Attacher::AttachEngine3D
  Height = 2
  Placement = pos=(-19,0,-22) rot=(0,0,1;1.5708rad)
  Radius = 2
FEATURE [Part::Cylinder] Cylinder563  label="Válec563"
  Angle = 360
  AttacherType = Attacher::AttachEngine3D
  Height = 2
  Placement = pos=(6e-15,-19,-22) rot=(0,0,1;3.14159rad)
  Radius = 2
FEATURE [Part::Cylinder] Cylinder564  label="Válec564"
  Angle = 360
  AttacherType = Attacher::AttachEngine3D
  Height = 2
  Placement = pos=(0,19,-22) rot=(0,0,1;0rad)
  Radius = 2
FEATURE [Part::Cylinder] Cylinder565  label="Válec565"
  Angle = 360
  AttacherType = Attacher::AttachEngine3D
  Height = 2
  Placement = pos=(13.44,-13.44,-22) rot=(0,0,1;3.92699rad)
  Radius = 2
FEATURE [Part::Cylinder] Cylinder566  label="Válec566"
  Angle = 360
  AttacherType = Attacher::AttachEngine3D
  Height = 2
  Placement = pos=(13.44,13.44,-22) rot=(0,0,-1;0.785398rad)
  Radius = 2
FEATURE [Part::Cylinder] Cylinder567  label="Válec567"
  Angle = 360
  AttacherType = Attacher::AttachEngine3D
  Height = 2
  Placement = pos=(19,8e-15,-22) rot=(0,0,-1;1.5708rad)
  Radius = 2
FEATURE [Part::Cylinder] Cylinder568  label="Válec568"
  Angle = 360
  AttacherType = Attacher::AttachEngine3D
  Height = 2
  Placement = pos=(-13.44,-13.44,-22) rot=(0,0,1;2.35619rad)
  Radius = 2
FEATURE [Part::Compound] Compound279
  Links = -> [Cylinder564,Cylinder179,Cylinder562,Cylinder568,Cylinder563,Cylinder565,Cylinder567,Cylinder566]
  Placement = pos=(0,0,-3) rot=(0,0,1;0rad)
FEATURE [Part::Cut] Cut334
  Base = -> Box359
  Tool = -> Compound279
FEATURE [Part::Cut] Cut343
  Base = -> Cut334
  Tool = -> Compound278
FEATURE [Part::Cylinder] Cylinder569  label="Válec569"
  Angle = 360
  AttacherType = Attacher::AttachEngine3D
  Height = 10
  Placement = pos=(-19,0,-24) rot=(0,0,1;1.5708rad)
  Radius = 1
FEATURE [Part::FeaturePython] Tube033  # WARN: FeaturePython — macro-defined, semantics opaque (R4)
  AttacherType = Attacher::AttachEngine3D
  Height = 4
  InnerRadius = 17
  OuterRadius = 21
  Placement = pos=(0,0,28) rot=(0,0,1;0rad)
FEATURE [Part::FeaturePython] Tube034  # WARN: FeaturePython — macro-defined, semantics opaque (R4)
  AttacherType = Attacher::AttachEngine3D
  Height = 8
  InnerRadius = 17
  OuterRadius = 25
  Placement = pos=(0,0,32) rot=(0,0,1;0rad)
FEATURE [Part::Cylinder] Cylinder570  label="Válec570"
  Angle = 360
  AttacherType = Attacher::AttachEngine3D
  Height = 10
  Placement = pos=(6e-15,-19,-24) rot=(0,0,1;3.14159rad)
  Radius = 1
FEATURE [Part::Cylinder] Cylinder571  label="Válec571"
  Angle = 360
  AttacherType = Attacher::AttachEngine3D
  Height = 3
  Placement = pos=(19,19,-24) rot=(0,0,1;0rad)
  Radius = 3
FEATURE [Part::Cylinder] Cylinder572  label="Válec572"
  Angle = 360
  AttacherType = Attacher::AttachEngine3D
  Height = 10
  Placement = pos=(-13.44,13.44,-24) rot=(0,0,1;0.785398rad)
  Radius = 1
FEATURE [Part::Cylinder] Cylinder573  label="Válec573"
  Angle = 360
  AttacherType = Attacher::AttachEngine3D
  Height = 10
  Placement = pos=(-13.44,-13.44,-24) rot=(0,0,1;2.35619rad)
  Radius = 1
FEATURE [Part::Cylinder] Cylinder574  label="Válec574"
  Angle = 360
  AttacherType = Attacher::AttachEngine3D
  Height = 10
  Placement = pos=(13.44,-13.44,-24) rot=(0,0,1;3.92699rad)
  Radius = 1
FEATURE [Part::Cylinder] Cylinder575  label="Válec575"
  Angle = 360
  AttacherType = Attacher::AttachEngine3D
  Height = 10
  Placement = pos=(0,19,-24) rot=(0,0,1;0rad)
  Radius = 1
FEATURE [Part::Cylinder] Cylinder576  label="Válec576"
  Angle = 360
  AttacherType = Attacher::AttachEngine3D
  Height = 50
  Placement = pos=(0,0,-29) rot=(0,0,1;0rad)
  Radius = 8
FEATURE [Part::Cut] Cut337
  Base = -> Cut343
  Tool = -> Cylinder576
FEATURE [Part::Cylinder] Cylinder577  label="Válec577"
  Angle = 360
  AttacherType = Attacher::AttachEngine3D
  Height = 3
  Placement = pos=(-19,-19,-24) rot=(0,0,1;0rad)
  Radius = 3
FEATURE [Part::Cylinder] Cylinder578  label="Válec578"
  Angle = 360
  AttacherType = Attacher::AttachEngine3D
  Height = 10
  Placement = pos=(-19.5,-19.5,-28) rot=(0,0,1;0rad)
  Radius = 1.5
FEATURE [Part::Cylinder] Cylinder579  label="Válec579"
  Angle = 360
  AttacherType = Attacher::AttachEngine3D
  Height = 10
  Placement = pos=(13.44,13.44,-24) rot=(0,0,-1;0.785398rad)
  Radius = 1
FEATURE [Part::Cylinder] Cylinder580  label="Válec580"
  Angle = 360
  AttacherType = Attacher::AttachEngine3D
  Height = 10
  Placement = pos=(-19.5,19.5,-28) rot=(0,0,1;0rad)
  Radius = 1.5
FEATURE [Part::Cylinder] Cylinder581  label="Válec581"
  Angle = 360
  AttacherType = Attacher::AttachEngine3D
  Height = 10
  Placement = pos=(19.5,-19.5,-28) rot=(0,0,1;0rad)
  Radius = 1.5
FEATURE [Part::Cylinder] Cylinder582  label="Válec582"
  Angle = 360
  AttacherType = Attacher::AttachEngine3D
  Height = 10
  Placement = pos=(19.5,19.5,-28) rot=(0,0,1;0rad)
  Radius = 1.5
FEATURE [Part::Compound] Compound271
  Links = -> [Cylinder578,Cylinder580,Cylinder581,Cylinder582]
FEATURE [Part::Cut] Cut335
  Base = -> Cut337
  Tool = -> Compound271
FEATURE [Part::Cylinder] Cylinder583  label="Válec583"
  Angle = 360
  AttacherType = Attacher::AttachEngine3D
  Height = 10
  Placement = pos=(19,8e-15,-24) rot=(0,0,-1;1.5708rad)
  Radius = 1
FEATURE [Part::Compound] Compound270
  Links = -> [Cylinder575,Cylinder572,Cylinder569,Cylinder573,Cylinder570,Cylinder574,Cylinder583,Cylinder579]
FEATURE [Part::Cut] Cut339
  Base = -> Tube032
  Tool = -> Compound270
FEATURE [Part::Cylinder] Cylinder584  label="Válec584"
  Angle = 360
  AttacherType = Attacher::AttachEngine3D
  Height = 3
  Placement = pos=(19,-19,-24) rot=(0,0,1;0rad)
  Radius = 3
FEATURE [Part::Cylinder] Cylinder585  label="Válec585"
  Angle = 360
  AttacherType = Attacher::AttachEngine3D
  Height = 3
  Placement = pos=(-19,19,-24) rot=(0,0,1;0rad)
  Radius = 3
FEATURE [Part::Compound] Compound272
  Links = -> [Cylinder577,Cylinder584,Cylinder585,Cylinder571]
  Placement = pos=(0,0,4) rot=(0,0,1;0rad)
FEATURE [Part::Cut] Cut344
  Base = -> Cut335
  Tool = -> Compound272
FEATURE [Part::Compound] Compound273
  Links = -> [Cut344,Cut339]
FEATURE [Part::Chamfer] Chamfer053
  Base = -> Compound273
  Edges = 2 edges r=2: [Edge1,Edge3]
FEATURE [Part::Chamfer] Chamfer054  label="gearovina-mini_motor-holder-A"
  Base = -> Chamfer053
  Edges = 2 edges r=2: [Edge43,Edge44]
FEATURE [Part::Cylinder] Cylinder586  label="Válec586"
  Angle = 360
  AttacherType = Attacher::AttachEngine3D
  Height = 20
  Placement = pos=(13.08,-13.08,26) rot=(0,0,1;3.92699rad)
  Radius = 1
FEATURE [Part::Cylinder] Cylinder587  label="Válec587"
  Angle = 360
  AttacherType = Attacher::AttachEngine3D
  Height = 20
  Placement = pos=(13.08,-13.08,26) rot=(0,0,1;3.92699rad)
  Radius = 1
FEATURE [Part::Cylinder] Cylinder588  label="Válec588"
  Angle = 360
  AttacherType = Attacher::AttachEngine3D
  Height = 20
  Placement = pos=(-13.08,-13.08,26) rot=(0,0,1;2.35619rad)
  Radius = 1
FEATURE [Part::Cylinder] Cylinder589  label="Válec589"
  Angle = 360
  AttacherType = Attacher::AttachEngine3D
  Height = 20
  Placement = pos=(6e-15,-18.5,26) rot=(0,0,1;3.14159rad)
  Radius = 1
FEATURE [Part::Cylinder] Cylinder590  label="Válec590"
  Angle = 360
  AttacherType = Attacher::AttachEngine3D
  Height = 20
  Placement = pos=(-18.5,0,26) rot=(0,0,1;1.5708rad)
  Radius = 1
FEATURE [Part::Cylinder] Cylinder591  label="Válec591"
  Angle = 360
  AttacherType = Attacher::AttachEngine3D
  Height = 20
  Placement = pos=(-13.08,13.08,26) rot=(0,0,1;0.785398rad)
  Radius = 1
FEATURE [Part::Cylinder] Cylinder592  label="Válec592"
  Angle = 360
  AttacherType = Attacher::AttachEngine3D
  Height = 20
  Placement = pos=(0,18.5,26) rot=(0,0,1;0rad)
  Radius = 1
FEATURE [Part::Cylinder] Cylinder593  label="Válec593"
  Angle = 360
  AttacherType = Attacher::AttachEngine3D
  Height = 20
  Placement = pos=(-13.08,-13.08,26) rot=(0,0,1;2.35619rad)
  Radius = 1
FEATURE [Part::Cylinder] Cylinder594  label="Válec594"
  Angle = 360
  AttacherType = Attacher::AttachEngine3D
  Height = 20
  Placement = pos=(18.5,8e-15,26) rot=(0,0,-1;1.5708rad)
  Radius = 1
FEATURE [Part::Cylinder] Cylinder595  label="Válec595"
  Angle = 360
  AttacherType = Attacher::AttachEngine3D
  Height = 20
  Placement = pos=(13.08,13.08,26) rot=(0,0,-1;0.785398rad)
  Radius = 1
FEATURE [Part::Cylinder] Cylinder596  label="Válec596"
  Angle = 360
  AttacherType = Attacher::AttachEngine3D
  Height = 20
  Placement = pos=(0,18.5,26) rot=(0,0,1;0rad)
  Radius = 1
FEATURE [Part::Cylinder] Cylinder597  label="Válec597"
  Angle = 360
  AttacherType = Attacher::AttachEngine3D
  Height = 20
  Placement = pos=(13.08,13.08,26) rot=(0,0,-1;0.785398rad)
  Radius = 1
FEATURE [Part::Cylinder] Cylinder598  label="Válec598"
  Angle = 360
  AttacherType = Attacher::AttachEngine3D
  Height = 20
  Placement = pos=(-13.08,13.08,26) rot=(0,0,1;0.785398rad)
  Radius = 1
FEATURE [Part::Cylinder] Cylinder599  label="Válec599"
  Angle = 360
  AttacherType = Attacher::AttachEngine3D
  Height = 20
  Placement = pos=(18.5,8e-15,26) rot=(0,0,-1;1.5708rad)
  Radius = 1
FEATURE [Part::Compound] Compound274
  Links = -> [Cylinder592,Cylinder591,Cylinder590,Cylinder588,Cylinder589,Cylinder587,Cylinder599,Cylinder595]
FEATURE [Part::Cut] Cut340
  Base = -> Tube033
  Tool = -> Compound274
FEATURE [Part::Cylinder] Cylinder600  label="Válec600"
  Angle = 360
  AttacherType = Attacher::AttachEngine3D
  Height = 20
  Placement = pos=(6e-15,-18.5,26) rot=(0,0,1;3.14159rad)
  Radius = 1
FEATURE [Part::Cylinder] Cylinder601  label="Válec601"
  Angle = 360
  AttacherType = Attacher::AttachEngine3D
  Height = 20
  Placement = pos=(-18.5,0,26) rot=(0,0,1;1.5708rad)
  Radius = 1
FEATURE [Part::Compound] Compound275
  Links = -> [Cylinder596,Cylinder598,Cylinder601,Cylinder593,Cylinder600,Cylinder586,Cylinder594,Cylinder597]
FEATURE [Part::Cylinder] Cylinder602  label="Válec602"
  Angle = 360
  AttacherType = Attacher::AttachEngine3D
  Height = 2
  Placement = pos=(-18.5,0,26) rot=(0,0,1;1.5708rad)
  Radius = 2
FEATURE [Part::Cylinder] Cylinder603  label="Válec603"
  Angle = 360
  AttacherType = Attacher::AttachEngine3D
  Height = 2
  Placement = pos=(-13.08,13.08,26) rot=(0,0,1;0.785398rad)
  Radius = 2
FEATURE [Part::Cylinder] Cylinder604  label="Válec604"
  Angle = 360
  AttacherType = Attacher::AttachEngine3D
  Height = 2
  Placement = pos=(-13.08,-13.08,26) rot=(0,0,1;2.35619rad)
  Radius = 2
FEATURE [Part::Cylinder] Cylinder605  label="Válec605"
  Angle = 360
  AttacherType = Attacher::AttachEngine3D
  Height = 2
  Placement = pos=(13.08,13.08,26) rot=(0,0,-1;0.785398rad)
  Radius = 2
FEATURE [Part::Cylinder] Cylinder606  label="Válec606"
  Angle = 360
  AttacherType = Attacher::AttachEngine3D
  Height = 2
  Placement = pos=(6e-15,-18.5,26) rot=(0,0,1;3.14159rad)
  Radius = 2
FEATURE [Part::Cylinder] Cylinder607  label="Válec607"
  Angle = 360
  AttacherType = Attacher::AttachEngine3D
  Height = 2
  Placement = pos=(6e-15,-18.5,26) rot=(0,0,1;3.14159rad)
  Radius = 2
FEATURE [Part::Cylinder] Cylinder608  label="Válec608"
  Angle = 360
  AttacherType = Attacher::AttachEngine3D
  Height = 60
  Placement = pos=(-8.41904,20.3253,34) rot=(0,0,1;0.392699rad)
  Radius = 1.5
FEATURE [Part::Cylinder] Cylinder609  label="Válec609"
  Angle = 360
  AttacherType = Attacher::AttachEngine3D
  Height = 2
  Placement = pos=(-18.5,0,26) rot=(0,0,1;1.5708rad)
  Radius = 2
FEATURE [Part::Cylinder] Cylinder610  label="Válec610"
  Angle = 360
  AttacherType = Attacher::AttachEngine3D
  Height = 2
  Placement = pos=(13.08,13.08,26) rot=(0,0,-1;0.785398rad)
  Radius = 2
FEATURE [Part::Box] Box360  label="Krychle360"
  AttacherType = Attacher::AttachEngine3D
  Height = 2
  Length = 6
  Placement = pos=(-16.4057,-10.0426,36) rot=(0,0,1;1.96349rad)
  Width = 6
FEATURE [Part::Cylinder] Cylinder611  label="Válec611"
  Angle = 360
  AttacherType = Attacher::AttachEngine3D
  Height = 2
  Placement = pos=(18.5,8e-15,26) rot=(0,0,-1;1.5708rad)
  Radius = 2
FEATURE [Part::Cylinder] Cylinder612  label="Válec612"
  Angle = 360
  AttacherType = Attacher::AttachEngine3D
  Height = 60
  Placement = pos=(-8.41904,20.3253,34) rot=(0,0,1;0.392699rad)
  Radius = 1.5
FEATURE [Part::Cylinder] Cylinder613  label="Válec613"
  Angle = 360
  AttacherType = Attacher::AttachEngine3D
  Height = 2
  Placement = pos=(-13.08,13.08,26) rot=(0,0,1;0.785398rad)
  Radius = 2
FEATURE [Part::Cylinder] Cylinder614  label="Válec614"
  Angle = 360
  AttacherType = Attacher::AttachEngine3D
  Height = 2
  Placement = pos=(0,18.5,26) rot=(0,0,1;0rad)
  Radius = 2
FEATURE [Part::Cylinder] Cylinder615  label="Válec615"
  Angle = 360
  AttacherType = Attacher::AttachEngine3D
  Height = 2
  Placement = pos=(13.08,-13.08,26) rot=(0,0,1;3.92699rad)
  Radius = 2
FEATURE [Part::Cylinder] Cylinder616  label="Válec616"
  Angle = 360
  AttacherType = Attacher::AttachEngine3D
  Height = 2
  Placement = pos=(18.5,8e-15,26) rot=(0,0,-1;1.5708rad)
  Radius = 2
FEATURE [Part::Compound] Compound276
  Links = -> [Cylinder614,Cylinder603,Cylinder602,Cylinder604,Cylinder606,Cylinder615,Cylinder616,Cylinder605]
  Placement = pos=(0,0,14) rot=(0,0,1;0rad)
FEATURE [Part::Cut] Cut336
  Base = -> Tube034
  Tool = -> Compound276
FEATURE [Part::Cut] Cut338
  Base = -> Cut336
  Tool = -> Compound275
FEATURE [Part::Cylinder] Cylinder617  label="Válec617"
  Angle = 360
  AttacherType = Attacher::AttachEngine3D
  Height = 2
  Placement = pos=(0,0,40) rot=(0,0,1;0rad)
  Radius = 25
FEATURE [Part::Cylinder] Cylinder618  label="Válec618"
  Angle = 360
  AttacherType = Attacher::AttachEngine3D
  Height = 2
  Placement = pos=(0,18.5,26) rot=(0,0,1;0rad)
  Radius = 2
FEATURE [Part::Cylinder] Cylinder619  label="Válec619"
  Angle = 360
  AttacherType = Attacher::AttachEngine3D
  Height = 2
  Placement = pos=(13.08,-13.08,26) rot=(0,0,1;3.92699rad)
  Radius = 2
FEATURE [Part::Cylinder] Cylinder620  label="Válec620"
  Angle = 360
  AttacherType = Attacher::AttachEngine3D
  Height = 2
  Placement = pos=(-13.08,-13.08,26) rot=(0,0,1;2.35619rad)
  Radius = 2
FEATURE [Part::Compound] Compound277
  Links = -> [Cylinder618,Cylinder613,Cylinder609,Cylinder620,Cylinder607,Cylinder619,Cylinder611,Cylinder610]
  Placement = pos=(0,0,14) rot=(0,0,1;0rad)
FEATURE [Part::Cut] Cut341
  Base = -> Cylinder617
  Tool = -> Compound277
FEATURE [Part::Cylinder] Cylinder621  label="Válec621"
  Angle = 360
  AttacherType = Attacher::AttachEngine3D
  Height = 60
  Placement = pos=(8.41904,-20.3253,34) rot=(0,0,1;3.53429rad)
  Radius = 1.5
FEATURE [Part::Cylinder] Cylinder622  label="Válec622"
  Angle = 360
  AttacherType = Attacher::AttachEngine3D
  Height = 60
  Placement = pos=(20.3253,8.41904,34) rot=(0,0,-1;1.1781rad)
  Radius = 1.5
FEATURE [Part::Cylinder] Cylinder623  label="Válec623"
  Angle = 360
  AttacherType = Attacher::AttachEngine3D
  Height = 60
  Placement = pos=(-20.3253,-8.41904,34) rot=(0,0,1;1.96349rad)
  Radius = 1.5
FEATURE [Part::Box] Box361  label="Krychle361"
  AttacherType = Attacher::AttachEngine3D
  Height = 2
  Length = 6
  Placement = pos=(-10.0426,16.4057,36) rot=(0,0,1;0.392699rad)
  Width = 6
FEATURE [Part::Box] Box362  label="Krychle362"
  AttacherType = Attacher::AttachEngine3D
  Height = 2
  Length = 6
  Placement = pos=(10.0426,-16.4057,36) rot=(0,0,1;3.53429rad)
  Width = 6
FEATURE [Part::Box] Box363  label="Krychle363"
  AttacherType = Attacher::AttachEngine3D
  Height = 2
  Length = 6
  Placement = pos=(16.4057,10.0426,36) rot=(0,0,-1;1.1781rad)
  Width = 6
FEATURE [Part::Cylinder] Cylinder624  label="Válec624"
  Angle = 360
  AttacherType = Attacher::AttachEngine3D
  Height = 60
  Placement = pos=(20.3253,8.41904,34) rot=(0,0,-1;1.1781rad)
  Radius = 1.5
FEATURE [Part::Cylinder] Cylinder625  label="Válec625"
  Angle = 360
  AttacherType = Attacher::AttachEngine3D
  Height = 60
  Placement = pos=(-20.3253,-8.41904,34) rot=(0,0,1;1.96349rad)
  Radius = 1.5
FEATURE [Part::Cylinder] Cylinder626  label="Válec626"
  Angle = 360
  AttacherType = Attacher::AttachEngine3D
  Height = 60
  Placement = pos=(8.41904,-20.3253,34) rot=(0,0,1;3.53429rad)
  Radius = 1.5
FEATURE [Part::Compound] Compound280
  Links = -> [Cylinder608,Cylinder623,Cylinder621,Cylinder622]
FEATURE [Part::Cut] Cut342
  Base = -> Cut341
  Tool = -> Compound280
FEATURE [Part::Compound] Compound281
  Links = -> [Box363,Box362,Box360,Box361]
FEATURE [Part::Compound] Compound294
  Links = -> [Cylinder612,Cylinder625,Cylinder626,Cylinder624]
FEATURE [Part::Cut] Cut348
  Base = -> Cut338
  Tool = -> Compound294
FEATURE [Part::Cut] Cut349
  Base = -> Cut348
  Tool = -> Compound281
FEATURE [Part::Compound] Compound282  label="gearovina-mini_aktuarni-holder"
  Links = -> [Cut340,Cut342,Cut349]
FEATURE [Part::Cylinder] Cylinder627  label="Válec627"
  Angle = 360
  AttacherType = Attacher::AttachEngine3D
  Height = 3
  Placement = pos=(15.5,-15.5,-54) rot=(0,0,1;0rad)
  Radius = 3
FEATURE [Part::Box] Box364  label="Krychle364"
  AttacherType = Attacher::AttachEngine3D
  Height = 2
  Length = 8
  Placement = pos=(16.5,16.5,-55) rot=(0,0,1;0rad)
  Width = 6
FEATURE [Part::Cylinder] Cylinder628  label="Válec628"
  Angle = 360
  AttacherType = Attacher::AttachEngine3D
  Height = 3
  Placement = pos=(15.5,15.5,-54) rot=(0,0,1;0rad)
  Radius = 3
FEATURE [Part::Cylinder] Cylinder629  label="Válec629"
  Angle = 360
  AttacherType = Attacher::AttachEngine3D
  Height = 3
  Placement = pos=(-15.5,15.5,-54) rot=(0,0,1;0rad)
  Radius = 3
FEATURE [Part::Box] Box365  label="Krychle365"
  AttacherType = Attacher::AttachEngine3D
  Height = 2
  Length = 8
  Placement = pos=(16.5,-22.5,-55) rot=(0,0,1;0rad)
  Width = 6
FEATURE [Part::Box] Box366  label="Krychle366"
  AttacherType = Attacher::AttachEngine3D
  Height = 2
  Length = 8
  Placement = pos=(-24.5,16.5,-55) rot=(0,0,1;0rad)
  Width = 6
FEATURE [Part::Box] Box367  label="Krychle367"
  AttacherType = Attacher::AttachEngine3D
  Height = 2
  Length = 8
  Placement = pos=(-24.5,-22.5,-55) rot=(0,0,1;0rad)
  Width = 6
FEATURE [Part::Compound] Compound283
  Links = -> [Box364,Box366,Box365,Box367]
  Placement = pos=(0,0,-2) rot=(0,0,1;0rad)
FEATURE [Part::Box] Box368  label="Krychle368"
  AttacherType = Attacher::AttachEngine3D
  Height = 11
  Length = 34
  Placement = pos=(-17,-17,-73) rot=(0,0,1;0rad)
  Width = 34
FEATURE [Part::Box] Box369  label="Krychle369"
  AttacherType = Attacher::AttachEngine3D
  Height = 11
  Length = 46.3
  Placement = pos=(-23.15,-23.15,-73) rot=(0,0,1;0rad)
  Width = 46.3
FEATURE [Part::Cut] Cut345
  Base = -> Box369
  Placement = pos=(0,0,7) rot=(0,0,1;0rad)
  Tool = -> Box368
FEATURE [Part::Cylinder] Cylinder630  label="Válec630"
  Angle = 360
  AttacherType = Attacher::AttachEngine3D
  Height = 20
  Placement = pos=(-10.48,15.75,-50) rot=(0,0,1;0rad)
  Radius = 1.5
FEATURE [Part::Cylinder] Cylinder631  label="Válec631"
  Angle = 360
  AttacherType = Attacher::AttachEngine3D
  Height = 20
  Placement = pos=(10.48,15.75,-50) rot=(0,0,1;0rad)
  Radius = 1.5
FEATURE [Part::Compound] Compound288
  Links = -> [Cylinder630,Cylinder631]
  Placement = pos=(0,0,-10) rot=(0,0,1;0rad)
FEATURE [Part::Cylinder] Cylinder632  label="Válec632"
  Angle = 360
  AttacherType = Attacher::AttachEngine3D
  Height = 20
  Placement = pos=(15.5,-15.5,-68) rot=(0,0,1;0rad)
  Radius = 1.5
FEATURE [Part::Box] Box370  label="Krychle370"
  AttacherType = Attacher::AttachEngine3D
  Height = 8
  Length = 42.3
  Placement = pos=(-21.15,-21.15,-70) rot=(0,0,1;0rad)
  Width = 42.3
FEATURE [Part::Cylinder] Cylinder633  label="Válec633"
  Angle = 360
  AttacherType = Attacher::AttachEngine3D
  Height = 20
  Placement = pos=(15.5,-15.5,-68) rot=(0,0,1;0rad)
  Radius = 1.5
FEATURE [Part::Cylinder] Cylinder634  label="Válec634"
  Angle = 360
  AttacherType = Attacher::AttachEngine3D
  Height = 20
  Placement = pos=(-15.5,15.5,-68) rot=(0,0,1;0rad)
  Radius = 1.5
FEATURE [Part::Cylinder] Cylinder635  label="Válec635"
  Angle = 360
  AttacherType = Attacher::AttachEngine3D
  Height = 20
  Placement = pos=(15.5,15.5,-68) rot=(0,0,1;0rad)
  Radius = 1.5
FEATURE [Part::Cylinder] Cylinder636  label="Válec636"
  Angle = 360
  AttacherType = Attacher::AttachEngine3D
  Height = 20
  Placement = pos=(15.5,15.5,-68) rot=(0,0,1;0rad)
  Radius = 1.5
FEATURE [Part::Cylinder] Cylinder637  label="Válec637"
  Angle = 360
  AttacherType = Attacher::AttachEngine3D
  Height = 20
  Placement = pos=(-15.5,15.5,-68) rot=(0,0,1;0rad)
  Radius = 1.5
FEATURE [Part::Cylinder] Cylinder638  label="Válec638"
  Angle = 360
  AttacherType = Attacher::AttachEngine3D
  Height = 10
  Placement = pos=(19.5,19.5,-28) rot=(0,0,1;0rad)
  Radius = 1.5
FEATURE [Part::Box] Box371  label="Krychle371"
  AttacherType = Attacher::AttachEngine3D
  Height = 2
  Length = 8
  Placement = pos=(16.5,-22.5,-55) rot=(0,0,1;0rad)
  Width = 6
FEATURE [Part::Cylinder] Cylinder639  label="Válec639"
  Angle = 360
  AttacherType = Attacher::AttachEngine3D
  Height = 10
  Placement = pos=(-19.5,-19.5,-28) rot=(0,0,1;0rad)
  Radius = 1.5
FEATURE [Part::Box] Box372  label="Krychle372"
  AttacherType = Attacher::AttachEngine3D
  Height = 20
  Length = 29
  Placement = pos=(-14.5,0,-75) rot=(0,0,1;0rad)
  Width = 45.5
FEATURE [Part::Box] Box373  label="Krychle373"
  AttacherType = Attacher::AttachEngine3D
  Height = 20
  Length = 29
  Placement = pos=(-14.5,0,-75) rot=(0,0,1;0rad)
  Width = 45.5
FEATURE [Part::Cylinder] Cylinder640  label="Válec640"
  Angle = 360
  AttacherType = Attacher::AttachEngine3D
  Height = 20
  Placement = pos=(-15.5,-15.5,-68) rot=(0,0,1;0rad)
  Radius = 1.5
FEATURE [Part::Compound] Compound284
  Links = -> [Cylinder636,Cylinder634,Cylinder633,Cylinder640]
FEATURE [Part::Cut] Cut353
  Base = -> Cut345
  Tool = -> Compound284
FEATURE [Part::Box] Box374  label="Krychle374"
  AttacherType = Attacher::AttachEngine3D
  Height = 2
  Length = 8
  Placement = pos=(-24.5,-22.5,-55) rot=(0,0,1;0rad)
  Width = 6
FEATURE [Part::Box] Box375  label="Krychle375"
  AttacherType = Attacher::AttachEngine3D
  Height = 4
  Length = 46.3
  Placement = pos=(-23.15,-23.15,-25) rot=(0,0,1;0rad)
  Width = 46.3
FEATURE [Part::Cylinder] Cylinder641  label="Válec641"
  Angle = 360
  AttacherType = Attacher::AttachEngine3D
  Height = 10
  Placement = pos=(19.5,-19.5,-28) rot=(0,0,1;0rad)
  Radius = 1.5
FEATURE [Part::Box] Box376  label="Krychle376"
  AttacherType = Attacher::AttachEngine3D
  Height = 8
  Length = 46.3
  Placement = pos=(-23.15,-23.15,-70) rot=(0,0,1;0rad)
  Width = 46.3
FEATURE [Part::Cut] Cut352
  Base = -> Box376
  Placement = pos=(0,0,-4) rot=(0,0,1;0rad)
  Tool = -> Box370
FEATURE [Part::Cut] Cut350
  Base = -> Cut352
  Tool = -> Box373
FEATURE [Part::Cylinder] Cylinder642  label="Válec642"
  Angle = 360
  AttacherType = Attacher::AttachEngine3D
  Height = 10
  Placement = pos=(-19.5,19.5,-28) rot=(0,0,1;0rad)
  Radius = 1.5
FEATURE [Part::Compound] Compound285
  Links = -> [Cylinder639,Cylinder642,Cylinder641,Cylinder638]
FEATURE [Part::Box] Box377  label="Krychle377"
  AttacherType = Attacher::AttachEngine3D
  Height = 2
  Length = 8
  Placement = pos=(-24.5,16.5,-55) rot=(0,0,1;0rad)
  Width = 6
FEATURE [Part::Cylinder] Cylinder643  label="Válec643"
  Angle = 360
  AttacherType = Attacher::AttachEngine3D
  Height = 3
  Placement = pos=(-15.5,-15.5,-54) rot=(0,0,1;0rad)
  Radius = 3
FEATURE [Part::Compound] Compound291
  Links = -> [Cylinder643,Cylinder627,Cylinder629,Cylinder628]
FEATURE [Part::Box] Box378  label="Krychle378"
  AttacherType = Attacher::AttachEngine3D
  Height = 2
  Length = 8
  Placement = pos=(16.5,16.5,-55) rot=(0,0,1;0rad)
  Width = 6
FEATURE [Part::Compound] Compound287
  Links = -> [Box378,Box377,Box371,Box374]
  Placement = pos=(0,0,10) rot=(0,0,1;0rad)
FEATURE [Part::Cylinder] Cylinder644  label="Válec644"
  Angle = 360
  AttacherType = Attacher::AttachEngine3D
  Height = 20
  Placement = pos=(-15.5,-15.5,-68) rot=(0,0,1;0rad)
  Radius = 1.5
FEATURE [Part::Compound] Compound289
  Links = -> [Cylinder635,Cylinder637,Cylinder632,Cylinder644]
FEATURE [Part::Cylinder] Cylinder645  label="Válec645"
  Angle = 360
  AttacherType = Attacher::AttachEngine3D
  Height = 50
  Placement = pos=(0,0,-29) rot=(0,0,1;0rad)
  Radius = 8
FEATURE [Part::Cut] Cut346
  Base = -> Box375
  Tool = -> Cylinder645
FEATURE [Part::Cut] Cut354
  Base = -> Cut346
  Tool = -> Compound285
FEATURE [Part::Compound] Compound286
  Links = -> [Cut354]
  Placement = pos=(0,0,-30) rot=(0,0,1;0rad)
FEATURE [Part::Cut] Cut351
  Base = -> Compound286
  Tool = -> Compound287
FEATURE [Part::Cylinder] Cylinder646  label="Válec646"
  Angle = 360
  AttacherType = Attacher::AttachEngine3D
  Height = 20
  Placement = pos=(-19.5,19.5,-28) rot=(0,0,1;0rad)
  Radius = 1.5
FEATURE [Part::Cylinder] Cylinder647  label="Válec647"
  Angle = 360
  AttacherType = Attacher::AttachEngine3D
  Height = 20
  Placement = pos=(19.5,19.5,-28) rot=(0,0,1;0rad)
  Radius = 1.5
FEATURE [Part::Cylinder] Cylinder648  label="Válec648"
  Angle = 360
  AttacherType = Attacher::AttachEngine3D
  Height = 20
  Placement = pos=(-19.5,-19.5,-28) rot=(0,0,1;0rad)
  Radius = 1.5
FEATURE [Part::Cut] Cut367
  Base = -> Cut353
  Tool = -> Box372
FEATURE [Part::Cut] Cut355
  Base = -> Cut367
  Tool = -> Compound283
FEATURE [Part::Cut] Cut370
  Base = -> Cut351
  Tool = -> Compound288
FEATURE [Part::Cut] Cut347
  Base = -> Cut370
  Tool = -> Compound289
FEATURE [Part::Cut] Cut363
  Base = -> Cut347
  Tool = -> Compound291
FEATURE [Part::Cylinder] Cylinder649  label="Válec649"
  Angle = 360
  AttacherType = Attacher::AttachEngine3D
  Height = 3
  Placement = pos=(8.41904,-20.3253,34) rot=(0,0,1;3.53429rad)
  Radius = 3
FEATURE [Part::Box] Box379  label="Krychle379"
  AttacherType = Attacher::AttachEngine3D
  Height = 20
  Length = 10
  Placement = pos=(25,-38.15,45) rot=(0,0,1;0rad)
  Width = 80
FEATURE [Part::Cylinder] Cylinder650  label="Válec650"
  Angle = 360
  AttacherType = Attacher::AttachEngine3D
  Height = 60
  Placement = pos=(8.41904,-20.3253,34) rot=(0,0,1;3.53429rad)
  Radius = 1.5
FEATURE [Part::Box] Box380  label="Krychle380"
  AttacherType = Attacher::AttachEngine3D
  Height = 20
  Length = 10
  Placement = pos=(-35,-38.15,45) rot=(0,0,1;0rad)
  Width = 80
FEATURE [Part::Cylinder] Cylinder651  label="Válec651"
  Angle = 360
  AttacherType = Attacher::AttachEngine3D
  Height = 3
  Placement = pos=(-20.3253,-8.41904,34) rot=(0,0,1;1.96349rad)
  Radius = 3
FEATURE [Part::Cylinder] Cylinder652  label="Válec652"
  Angle = 360
  AttacherType = Attacher::AttachEngine3D
  Height = 10
  Placement = pos=(-28,12,55) rot=(0,1,0;1.5708rad)
  Radius = 1.5
FEATURE [Part::Box] Box381  label="Krychle381"
  AttacherType = Attacher::AttachEngine3D
  Height = 20
  Length = 42.3
  Placement = pos=(-21.15,-38.15,45) rot=(0,0,1;0rad)
  Width = 80
FEATURE [Part::Cylinder] Cylinder653  label="Válec653"
  Angle = 360
  AttacherType = Attacher::AttachEngine3D
  Height = 14
  Placement = pos=(0,0,45) rot=(0,0,1;0rad)
  Radius = 30
FEATURE [Part::Cut] Cut366
  Base = -> Cylinder653
  Placement = pos=(0,0,3) rot=(0,0,1;0rad)
  Tool = -> Box381
FEATURE [Part::Cylinder] Cylinder654  label="Válec654"
  Angle = 360
  AttacherType = Attacher::AttachEngine3D
  Height = 60
  Placement = pos=(-20.3253,-8.41904,34) rot=(0,0,1;1.96349rad)
  Radius = 1.5
FEATURE [Part::Cylinder] Cylinder655  label="Válec655"
  Angle = 360
  AttacherType = Attacher::AttachEngine3D
  Height = 6
  Placement = pos=(0,0,39) rot=(0,0,1;0rad)
  Radius = 30
FEATURE [Part::Cylinder] Cylinder656  label="Válec656"
  Angle = 360
  AttacherType = Attacher::AttachEngine3D
  Height = 60
  Placement = pos=(20.3253,8.41904,34) rot=(0,0,-1;1.1781rad)
  Radius = 1.5
FEATURE [Part::Cylinder] Cylinder657  label="Válec657"
  Angle = 360
  AttacherType = Attacher::AttachEngine3D
  Height = 20
  Placement = pos=(19.5,-19.5,-28) rot=(0,0,1;0rad)
  Radius = 1.5
FEATURE [Part::Compound] Compound290
  Links = -> [Cylinder648,Cylinder646,Cylinder657,Cylinder647]
  Placement = pos=(0,0,-33) rot=(0,0,1;0rad)
FEATURE [Part::Cut] Cut362
  Base = -> Cut355
  Tool = -> Compound290
FEATURE [Part::Cylinder] Cylinder658  label="Válec658"
  Angle = 360
  AttacherType = Attacher::AttachEngine3D
  Height = 60
  Placement = pos=(-8.41904,20.3253,34) rot=(0,0,1;0.392699rad)
  Radius = 1.5
FEATURE [Part::Cylinder] Cylinder659  label="Válec659"
  Angle = 360
  AttacherType = Attacher::AttachEngine3D
  Height = 3
  Placement = pos=(20.3253,8.41904,34) rot=(0,0,-1;1.1781rad)
  Radius = 3
FEATURE [Part::Box] Box382  label="Krychle382"
  AttacherType = Attacher::AttachEngine3D
  Height = 8
  Length = 7
  Placement = pos=(-22,15,-74) rot=(0,0,1;0rad)
  Width = 7
FEATURE [Part::Cylinder] Cylinder660  label="Válec660"
  Angle = 360
  AttacherType = Attacher::AttachEngine3D
  Height = 8
  Placement = pos=(-15.15,15.15,-74) rot=(0,0,1;0rad)
  Radius = 6
FEATURE [Part::Cut] Cut356
  Base = -> Box382
  Placement = pos=(0,0,0) rot=(0,0,1;3.14159rad)
  Tool = -> Cylinder660
FEATURE [Part::Cut] Cut360
  Base = -> Box382
  Placement = pos=(0,0,0) rot=(0,0,1;1.5708rad)
  Tool = -> Cylinder660
FEATURE [Part::Cut] Cut364
  Base = -> Box382
  Tool = -> Cylinder660
FEATURE [Part::Cut] Cut365
  Base = -> Box382
  Placement = pos=(0,0,0) rot=(0,0,-1;1.5708rad)
  Tool = -> Cylinder660
FEATURE [Part::Compound] Compound292
  Links = -> [Cut364,Cut360,Cut356,Cut365]
FEATURE [Part::Compound] Compound293
  Links = -> [Cut350,Cut363,Cut362,Compound292]
FEATURE [Part::Cylinder] Cylinder661  label="Válec661"
  Angle = 360
  AttacherType = Attacher::AttachEngine3D
  Height = 3
  Placement = pos=(-8.41904,20.3253,34) rot=(0,0,1;0.392699rad)
  Radius = 3
FEATURE [Part::Box] Box383  label="Krychle383"
  AttacherType = Attacher::AttachEngine3D
  Height = 6
  Length = 2
  Placement = pos=(-24,8,52) rot=(0,0,1;0rad)
  Width = 14
FEATURE [Part::Box] Box384  label="Krychle384"
  AttacherType = Attacher::AttachEngine3D
  Height = 6
  Length = 2
  Placement = pos=(-24,-22,52) rot=(0,0,1;0rad)
  Width = 14
FEATURE [Part::Box] Box385  label="Krychle385"
  AttacherType = Attacher::AttachEngine3D
  Height = 6
  Length = 2
  Placement = pos=(22,8,52) rot=(0,0,1;0rad)
  Width = 14
FEATURE [Part::Box] Box386  label="Krychle386"
  AttacherType = Attacher::AttachEngine3D
  Height = 6
  Length = 2
  Placement = pos=(22,-20,52) rot=(0,0,1;0rad)
  Width = 14
FEATURE [Part::Cylinder] Cylinder662  label="Válec662"
  Angle = 360
  AttacherType = Attacher::AttachEngine3D
  Height = 20
  Placement = pos=(0,0,37) rot=(0,0,1;0rad)
  Radius = 16
FEATURE [Part::Cylinder] Cylinder663  label="Válec663"
  Angle = 360
  AttacherType = Attacher::AttachEngine3D
  Height = 10
  Placement = pos=(18,12,55) rot=(0,1,0;1.5708rad)
  Radius = 1.5
FEATURE [Part::Box] Box387  label="Krychle387"
  AttacherType = Attacher::AttachEngine3D
  Height = 20
  Length = 10
  Placement = pos=(-35,-38.15,45) rot=(0,0,1;0rad)
  Width = 80
FEATURE [Part::Box] Box388  label="Krychle388"
  AttacherType = Attacher::AttachEngine3D
  Height = 20
  Length = 10
  Placement = pos=(25,-38.15,45) rot=(0,0,1;0rad)
  Width = 80
FEATURE [Part::Cylinder] Cylinder664  label="Válec664"
  Angle = 360
  AttacherType = Attacher::AttachEngine3D
  Height = 10
  Placement = pos=(-28,-12,55) rot=(0,1,0;1.5708rad)
  Radius = 1.5
FEATURE [Part::Cylinder] Cylinder665  label="Válec665"
  Angle = 360
  AttacherType = Attacher::AttachEngine3D
  Height = 10
  Placement = pos=(18,-12,55) rot=(0,1,0;1.5708rad)
  Radius = 1.5
FEATURE [Part::Compound] Compound295
  Links = -> [Cylinder652,Cylinder664,Cylinder663,Cylinder665]
FEATURE [Part::Compound] Compound296
  Links = -> [Box383,Box384,Box385,Box386]
FEATURE [Part::Compound] Compound297
  Links = -> [Cylinder658,Cylinder654,Cylinder650,Cylinder656]
  Placement = pos=(0,0,0) rot=(0,0,1;0.392699rad)
FEATURE [Part::Compound] Compound298
  Links = -> [Cylinder661,Cylinder651,Cylinder649,Cylinder659]
  Placement = pos=(0,0,8) rot=(0,0,1;0.392699rad)
FEATURE [Part::Cut] Cut357
  Base = -> Cylinder655
  Placement = pos=(0,0,3) rot=(0,0,1;0rad)
  Tool = -> Compound298
FEATURE [Part::Cut] Cut361
  Base = -> Cut357
  Tool = -> Compound297
FEATURE [Part::Compound] Compound300
  Links = -> [Box380,Box379]
FEATURE [Part::Cut] Cut368
  Base = -> Cut366
  Tool = -> Compound300
FEATURE [Part::Cut] Cut358
  Base = -> Cut368
  Tool = -> Compound295
FEATURE [Part::Cut] Cut371
  Base = -> Cut358
  Tool = -> Compound296
FEATURE [Part::Chamfer] Chamfer006
  Base = -> Compound293
  Edges = 9 edges r=2: [Edge1,Edge6,Edge29,Edge37,Edge42,Edge58,Edge105,Edge162,Edge181]
FEATURE [Part::Chamfer] Chamfer007
  Base = -> Chamfer006
  Edges = 3 edges r=2: [Edge4,Edge49,Edge115]
FEATURE [Part::Chamfer] Chamfer056  label="gearovina-mini_motor-holder-B"
  Base = -> Chamfer007
  Edges = 5 edges r=0.9: [Edge3,Edge24,Edge25,Edge27,Edge29]
  Placement = pos=(0,0,26) rot=(0,0,1;0rad)
FEATURE [Part::Compound] Compound301
  Links = -> [Box387,Box388]
  Placement = pos=(0,0,-8) rot=(0,0,1;0rad)
FEATURE [Part::Cut] Cut369
  Base = -> Cut361
  Tool = -> Compound301
FEATURE [Part::Compound] Compound299
  Links = -> [Cut369,Cut371]
FEATURE [Part::Chamfer] Chamfer055
  Base = -> Compound299
  Edges = 2 edges r=1.2: [Edge54,Edge89]
FEATURE [Part::Chamfer] Chamfer057
  Base = -> Chamfer055
  Edges = 2 edges r=1.2: [Edge8,Edge85]
FEATURE [Part::Cut] Cut359  label="gearovina-mini_aktuator-part-A001"
  Base = -> Chamfer057
  Tool = -> Cylinder662
FEATURE [Part::Compound] Compound302  label="gearovina_mini_actuator"
  Links = -> [Cut318,Compound262,Chamfer054,Compound282,Cut359,Chamfer056]
  Placement = pos=(17,-181,10) rot=(-1,0,0;1.5708rad)
FEATURE [Part::Cylinder] Cylinder2151  label="Válec2151"
  Angle = 360
  AttacherType = Attacher::AttachEngine3D
  Height = 25
  Placement = pos=(0,0,-21) rot=(0,0,1;0rad)
  Radius = 21
FEATURE [Part::Box] Box832  label="Krychle831"
  AttacherType = Attacher::AttachEngine3D
  Height = 27
  Length = 46.3
  Placement = pos=(-23.15,-23.15,-48) rot=(0,0,1;0rad)
  Width = 46.3
FEATURE [Part::Cylinder] Cylinder2155  label="Válec2155"
  Angle = 360
  AttacherType = Attacher::AttachEngine3D
  Height = 5
  Placement = pos=(9,28,21) rot=(0,1,0;1.5708rad)
  Radius = 3
FEATURE [Part::Box] Box830  label="Krychle829"
  AttacherType = Attacher::AttachEngine3D
  Height = 25
  Length = 10
  Placement = pos=(6,13,-21) rot=(0,0,1;0rad)
  Width = 14
FEATURE [Part::Box] Box831  label="Krychle830"
  AttacherType = Attacher::AttachEngine3D
  Height = 25
  Length = 10
  Placement = pos=(-16,13,-21) rot=(0,0,1;0rad)
  Width = 14
FEATURE [Part::Compound] Compound961
  Links = -> [Box831,Box830]
  Placement = pos=(48,-38,10) rot=(0.57735,0.57735,-0.57735;2.0944rad)
FEATURE [Part::Cylinder] Cylinder2154  label="Válec2154"
  Angle = 360
  AttacherType = Attacher::AttachEngine3D
  Height = 5
  Placement = pos=(-14,28,21) rot=(0,1,0;1.5708rad)
  Radius = 3
FEATURE [Part::Cylinder] Cylinder2161  label="Válec2161"
  Angle = 360
  AttacherType = Attacher::AttachEngine3D
  Height = 50
  Placement = pos=(-12,56,8) rot=(1,0,0;1.5708rad)
  Radius = 1
FEATURE [Part::Cylinder] Cylinder2157  label="Válec2157"
  Angle = 360
  AttacherType = Attacher::AttachEngine3D
  Height = 2
  Placement = pos=(14,18,-14) rot=(0,1,0;1.5708rad)
  Radius = 2
FEATURE [Part::Cylinder] Cylinder2163  label="Válec2163"
  Angle = 360
  AttacherType = Attacher::AttachEngine3D
  Height = 16
  Placement = pos=(-20,18,-14) rot=(0,1,0;1.5708rad)
  Radius = 1
FEATURE [Part::Cylinder] Cylinder2166  label="Válec2166"
  Angle = 360
  AttacherType = Attacher::AttachEngine3D
  Height = 20
  Placement = pos=(0,28,-39) rot=(0,1,0;1.5708rad)
  Radius = 1.5
FEATURE [Part::Cylinder] Cylinder2164  label="Válec2164"
  Angle = 360
  AttacherType = Attacher::AttachEngine3D
  Height = 5
  Placement = pos=(9,28,-39) rot=(0,1,0;1.5708rad)
  Radius = 3
FEATURE [Part::Cylinder] Cylinder2165  label="Válec2165"
  Angle = 360
  AttacherType = Attacher::AttachEngine3D
  Height = 50
  Placement = pos=(12,56,8) rot=(1,0,0;1.5708rad)
  Radius = 1
FEATURE [Part::Compound] Compound965
  Links = -> [Cylinder2165,Cylinder2161]
FEATURE [Part::Cylinder] Cylinder2168  label="Válec2168"
  Angle = 360
  AttacherType = Attacher::AttachEngine3D
  Height = 5
  Placement = pos=(-14,28,-39) rot=(0,1,0;1.5708rad)
  Radius = 3
FEATURE [Part::Cylinder] Cylinder2167  label="Válec2167"
  Angle = 360
  AttacherType = Attacher::AttachEngine3D
  Height = 20
  Placement = pos=(-22,28,21) rot=(0,1,0;1.5708rad)
  Radius = 1.5
FEATURE [Part::Cylinder] Cylinder2153  label="Válec2153"
  Angle = 360
  AttacherType = Attacher::AttachEngine3D
  Height = 16
  Placement = pos=(4,18,-14) rot=(0,1,0;1.5708rad)
  Radius = 1
FEATURE [Part::Compound] Compound967
  Links = -> [Cylinder2163,Cylinder2153]
FEATURE [Part::Cylinder] Cylinder2158  label="Válec2158"
  Angle = 360
  AttacherType = Attacher::AttachEngine3D
  Height = 20
  Placement = pos=(-22,28,-9) rot=(0,1,0;1.5708rad)
  Radius = 1.5
FEATURE [Part::Cylinder] Cylinder2159  label="Válec2159"
  Angle = 360
  AttacherType = Attacher::AttachEngine3D
  Height = 20
  Placement = pos=(-12,49,8) rot=(1,0,0;1.5708rad)
  Radius = 2
FEATURE [Part::Cylinder] Cylinder2162  label="Válec2162"
  Angle = 360
  AttacherType = Attacher::AttachEngine3D
  Height = 2
  Placement = pos=(-16,18,-14) rot=(0,1,0;1.5708rad)
  Radius = 2
FEATURE [Part::Compound] Compound969
  Links = -> [Cylinder2162,Cylinder2157]
FEATURE [Part::Cylinder] Cylinder2160  label="Válec2160"
  Angle = 360
  AttacherType = Attacher::AttachEngine3D
  Height = 20
  Placement = pos=(12,49,8) rot=(1,0,0;1.5708rad)
  Radius = 2
FEATURE [Part::Compound] Compound964
  Links = -> [Cylinder2160,Cylinder2159]
FEATURE [Part::Cylinder] Cylinder2152  label="Válec2152"
  Angle = 360
  AttacherType = Attacher::AttachEngine3D
  Height = 5
  Placement = pos=(-14,28,-9) rot=(0,1,0;1.5708rad)
  Radius = 3
FEATURE [Part::Compound] Compound963
  Links = -> [Cylinder2152,Cylinder2168,Cylinder2154]
  Placement = pos=(0,8,0) rot=(0,0,1;0rad)
FEATURE [Part::Cylinder] Cylinder2174  label="Válec2174"
  Angle = 360
  AttacherType = Attacher::AttachEngine3D
  Height = 34
  Placement = pos=(42,0,10) rot=(0,1,0;1.5708rad)
  Radius = 40
FEATURE [Part::Cylinder] Cylinder2156  label="Válec2156"
  Angle = 360
  AttacherType = Attacher::AttachEngine3D
  Height = 26
  Placement = pos=(0,0,4) rot=(0,0,1;0rad)
  Radius = 25
FEATURE [Part::Compound] Compound972
  Links = -> [Box832,Cylinder2151,Cylinder2156]
FEATURE [Part::Box] Box834  label="Krychle833"
  AttacherType = Attacher::AttachEngine3D
  Height = 51
  Length = 8
  Placement = pos=(-14,13,-21) rot=(0,0,1;0rad)
  Width = 28
FEATURE [Part::Cylinder] Cylinder2169  label="Válec2169"
  Angle = 360
  AttacherType = Attacher::AttachEngine3D
  Height = 5
  Placement = pos=(9,28,-9) rot=(0,1,0;1.5708rad)
  Radius = 3
FEATURE [Part::Compound] Compound962
  Links = -> [Cylinder2169,Cylinder2164,Cylinder2155]
  Placement = pos=(0,8,0) rot=(0,0,1;0rad)
FEATURE [Part::Cylinder] Cylinder2178  label="Válec2178"
  Angle = 360
  AttacherType = Attacher::AttachEngine3D
  Height = 7
  Placement = pos=(-14,28,-9) rot=(0,1,0;1.5708rad)
  Radius = 3
FEATURE [Part::Box] Box837  label="Krychle836"
  AttacherType = Attacher::AttachEngine3D
  Height = 25
  Length = 2
  Placement = pos=(-16,13,-21) rot=(0,0,1;0rad)
  Width = 15
FEATURE [Part::Cylinder] Cylinder2171  label="Válec2171"
  Angle = 360
  AttacherType = Attacher::AttachEngine3D
  Height = 20
  Placement = pos=(0,28,21) rot=(0,1,0;1.5708rad)
  Radius = 1.5
FEATURE [Part::Cylinder] Cylinder2180  label="Válec2180"
  Angle = 360
  AttacherType = Attacher::AttachEngine3D
  Height = 7
  Placement = pos=(-14,28,21) rot=(0,1,0;1.5708rad)
  Radius = 3
FEATURE [Part::Cylinder] Cylinder2185  label="Válec2185"
  Angle = 360
  AttacherType = Attacher::AttachEngine3D
  Height = 19
  Placement = pos=(42,0,10) rot=(0,1,0;1.5708rad)
  Radius = 40
FEATURE [Part::Cylinder] Cylinder2170  label="Válec2170"
  Angle = 360
  AttacherType = Attacher::AttachEngine3D
  Height = 20
  Placement = pos=(-22,28,-39) rot=(0,1,0;1.5708rad)
  Radius = 1.5
FEATURE [Part::Compound] Compound966
  Links = -> [Cylinder2158,Cylinder2170,Cylinder2167]
  Placement = pos=(0,8,0) rot=(0,0,1;0rad)
FEATURE [Part::Cylinder] Cylinder2173  label="Válec2173"
  Angle = 360
  AttacherType = Attacher::AttachEngine3D
  Height = 32
  Placement = pos=(42,0,10) rot=(0,1,0;1.5708rad)
  Radius = 60
FEATURE [Part::Cut] Cut793
  Base = -> Cylinder2173
  Tool = -> Cylinder2174
FEATURE [Part::Cylinder] Cylinder2176  label="Válec2176"
  Angle = 360
  AttacherType = Attacher::AttachEngine3D
  Height = 16
  Placement = pos=(-20,18,-14) rot=(0,1,0;1.5708rad)
  Radius = 1
FEATURE [Part::Cylinder] Cylinder2181  label="Válec2181"
  Angle = 360
  AttacherType = Attacher::AttachEngine3D
  Height = 7
  Placement = pos=(9,28,21) rot=(0,1,0;1.5708rad)
  Radius = 3
FEATURE [Part::Box] Box833  label="Krychle832"
  AttacherType = Attacher::AttachEngine3D
  Height = 51
  Length = 8
  Placement = pos=(6,13,-21) rot=(0,0,1;0rad)
  Width = 28
FEATURE [Part::Compound] Compound970
  Links = -> [Box834,Box833]
FEATURE [Part::Cut] Cut789
  Base = -> Compound970
  Tool = -> Compound972
FEATURE [Part::Cut] Cut786
  Base = -> Cut789
  Tool = -> Compound965
FEATURE [Part::Cut] Cut790
  Base = -> Cut786
  Tool = -> Compound967
FEATURE [Part::Cut] Cut787
  Base = -> Cut790
  Tool = -> Compound969
FEATURE [Part::Cut] Cut788  label="gearovina_mini_fixoloh005"
  Base = -> Cut787
  Tool = -> Compound964
FEATURE [Part::Box] Box835  label="Krychle834"
  AttacherType = Attacher::AttachEngine3D
  Height = 51
  Length = 12
  Placement = pos=(-6,26,-21) rot=(0,0,1;0rad)
  Width = 4
FEATURE [Part::Cylinder] Cylinder2172  label="Válec2172"
  Angle = 360
  AttacherType = Attacher::AttachEngine3D
  Height = 20
  Placement = pos=(0,28,-9) rot=(0,1,0;1.5708rad)
  Radius = 1.5
FEATURE [Part::Compound] Compound968
  Links = -> [Cylinder2172,Cylinder2166,Cylinder2171]
  Placement = pos=(0,8,0) rot=(0,0,1;0rad)
FEATURE [Part::Cut] Cut784
  Base = -> Cut788
  Tool = -> Compound968
FEATURE [Part::Cut] Cut791
  Base = -> Cut784
  Tool = -> Compound966
FEATURE [Part::Cut] Cut785
  Base = -> Cut791
  Tool = -> Compound963
FEATURE [Part::Cut] Cut783  label="gearovina_mini_fixoloh_zkrato008"
  Base = -> Cut785
  Tool = -> Compound962
FEATURE [Part::Compound] Compound971  label="gearovina_mini_fixoloh_zkrato007"
  Links = -> [Cut783,Box835]
  Placement = pos=(87,-21,10) rot=(0.57735,-0.57735,-0.57735;4.18879rad)
FEATURE [Part::Cut] Cut792
  Base = -> Compound971
  Tool = -> Cut793
FEATURE [Part::Cylinder] Cylinder2182  label="Válec2182"
  Angle = 360
  AttacherType = Attacher::AttachEngine3D
  Height = 7
  Placement = pos=(9,28,-9) rot=(0,1,0;1.5708rad)
  Radius = 3
FEATURE [Part::Cylinder] Cylinder2179  label="Válec2179"
  Angle = 360
  AttacherType = Attacher::AttachEngine3D
  Height = 7
  Placement = pos=(9,28,-39) rot=(0,1,0;1.5708rad)
  Radius = 3
FEATURE [Part::Compound] Compound975
  Links = -> [Cylinder2182,Cylinder2179,Cylinder2181]
  Placement = pos=(0,8,0) rot=(0,0,1;0rad)
FEATURE [Part::Cylinder] Cylinder2175  label="Válec2175"
  Angle = 360
  AttacherType = Attacher::AttachEngine3D
  Height = 16
  Placement = pos=(4,18,-14) rot=(0,1,0;1.5708rad)
  Radius = 1
FEATURE [Part::Compound] Compound973
  Links = -> [Cylinder2176,Cylinder2175]
  Placement = pos=(83,-53,10) rot=(0,1,0;1.5708rad)
FEATURE [Part::Cut] Cut794
  Base = -> Compound961
  Tool = -> Compound973
FEATURE [Part::Cylinder] Cylinder2177  label="Válec2177"
  Angle = 360
  AttacherType = Attacher::AttachEngine3D
  Height = 25
  Placement = pos=(87,-17,10) rot=(1,0,0;1.5708rad)
  Radius = 21
FEATURE [Part::Cut] Cut795
  Base = -> Cut794
  Tool = -> Cylinder2177
FEATURE [Part::Chamfer] Chamfer059
  Base = -> Cut795
  Edges = 1 edges r=4.6: [Edge8]
FEATURE [Part::Chamfer] Chamfer058
  Base = -> Chamfer059
  Edges = 1 edges r=4.6: [Edge25]
FEATURE [Part::Chamfer] Chamfer063
  Base = -> Chamfer058
  Edges = 1 edges r=1.9: [Edge22]
FEATURE [Part::Chamfer] Chamfer062
  Base = -> Chamfer063
  Edges = 1 edges r=1.9: [Edge37]
FEATURE [Part::Cylinder] Cylinder2183  label="Válec2183"
  Angle = 360
  AttacherType = Attacher::AttachEngine3D
  Height = 7
  Placement = pos=(-14,28,-39) rot=(0,1,0;1.5708rad)
  Radius = 3
FEATURE [Part::Compound] Compound976
  Links = -> [Cylinder2178,Cylinder2183,Cylinder2180]
  Placement = pos=(-2,8,0) rot=(0,0,1;0rad)
FEATURE [Part::Compound] Compound977
  Links = -> [Compound975,Compound976]
  Placement = pos=(87,-9,10) rot=(0.57735,-0.57735,0.57735;2.0944rad)
FEATURE [Part::Box] Box836  label="Krychle835"
  AttacherType = Attacher::AttachEngine3D
  Height = 25
  Length = 2
  Placement = pos=(14,13,-21) rot=(0,0,1;0rad)
  Width = 15
FEATURE [Part::Compound] Compound974
  Links = -> [Box837,Box836]
  Placement = pos=(33,-38,10) rot=(0.57735,0.57735,-0.57735;2.0944rad)
FEATURE [Part::Chamfer] Chamfer060
  Base = -> Compound974
  Edges = 1 edges r=1.9: [Edge20]
FEATURE [Part::Chamfer] Chamfer061
  Base = -> Chamfer060
  Edges = 1 edges r=1.9: [Edge19]
FEATURE [Part::Cut] Cut796
  Base = -> Chamfer061
  Tool = -> Compound977
FEATURE [Part::Cylinder] Cylinder2184  label="Válec2184"
  Angle = 360
  AttacherType = Attacher::AttachEngine3D
  Height = 19
  Placement = pos=(42,0,10) rot=(0,1,0;1.5708rad)
  Radius = 60
FEATURE [Part::Cut] Cut797
  Base = -> Cylinder2184
  Tool = -> Cylinder2185
FEATURE [Part::Cut] Cut798
  Base = -> Cut796
  Tool = -> Cut797
FEATURE [Part::Compound] Compound978  label="gearovina_mini_fixoloh_revised"
  Links = -> [Chamfer062,Cut798,Cut792]
  Placement = pos=(104,-160,20) rot=(0,1,0;3.14159rad)
FEATURE [Part::Box] Box838  label="Krychle837"
  AttacherType = Attacher::AttachEngine3D
  Height = 2
  Length = 6
  Placement = pos=(48,-3,7) rot=(0,0,1;0rad)
  Width = 6
FEATURE [Part::Cylinder] Cylinder2186  label="Válec2186"
  Angle = 360
  AttacherType = Attacher::AttachEngine3D
  Height = 20
  Placement = pos=(28,16,-3) rot=(0,1,0;1.5708rad)
  Radius = 1.5
FEATURE [Part::Cylinder] Cylinder2187  label="Válec2187"
  Angle = 360
  AttacherType = Attacher::AttachEngine3D
  Height = 3
  Placement = pos=(35,21,22) rot=(0,1,0;1.5708rad)
  Radius = 3
FEATURE [Part::Cylinder] Cylinder2188  label="Válec2188"
  Angle = 360
  AttacherType = Attacher::AttachEngine3D
  Height = 20
  Placement = pos=(28,-16,-3) rot=(0,1,0;1.5708rad)
  Radius = 1.5
FEATURE [Part::Box] Box839  label="Krychle838"
  AttacherType = Attacher::AttachEngine3D
  Height = 2
  Length = 6
  Placement = pos=(48,-33,7) rot=(0,0,1;0rad)
  Width = 6
FEATURE [Part::Cylinder] Cylinder2189  label="Válec2189"
  Angle = 360
  AttacherType = Attacher::AttachEngine3D
  Height = 3
  Placement = pos=(35,-37,19) rot=(0,1,0;1.5708rad)
  Radius = 3
FEATURE [Part::Box] Box840  label="Krychle839"
  AttacherType = Attacher::AttachEngine3D
  Height = 80
  Length = 12
  Placement = pos=(-6,25,-48) rot=(0,0,1;0rad)
  Width = 8
FEATURE [Part::Cylinder] Cylinder2190  label="Válec2190"
  Angle = 360
  AttacherType = Attacher::AttachEngine3D
  Height = 20
  Placement = pos=(26,37,19) rot=(0,1,0;1.5708rad)
  Radius = 1.5
FEATURE [Part::Cylinder] Cylinder2191  label="Válec2191"
  Angle = 360
  AttacherType = Attacher::AttachEngine3D
  Height = 3
  Placement = pos=(35,16,-3) rot=(0,1,0;1.5708rad)
  Radius = 3
FEATURE [Part::Cylinder] Cylinder395  label="Válec395"
  Angle = 360
  AttacherType = Attacher::AttachEngine3D
  Height = 20
  Placement = pos=(31,21,22) rot=(0,1,0;1.5708rad)
  Radius = 1.5
FEATURE [Part::Box] Box841  label="Krychle840"
  AttacherType = Attacher::AttachEngine3D
  Height = 80
  Length = 31
  Placement = pos=(-16,33,-48) rot=(0,0,1;0rad)
  Width = 6
FEATURE [Part::Compound] Compound979
  Links = -> [Box840,Box841]
  Placement = pos=(79,-8,10) rot=(0.57735,-0.57735,0.57735;2.0944rad)
FEATURE [Part::Cylinder] Cylinder2192  label="Válec2192"
  Angle = 360
  AttacherType = Attacher::AttachEngine3D
  Height = 3
  Placement = pos=(35,-21,22) rot=(0,1,0;1.5708rad)
  Radius = 3
FEATURE [Part::Cylinder] Cylinder2193  label="Válec2193"
  Angle = 360
  AttacherType = Attacher::AttachEngine3D
  Height = 3
  Placement = pos=(35,-16,-3) rot=(0,1,0;1.5708rad)
  Radius = 3
FEATURE [Part::Cylinder] Cylinder2194  label="Válec2194"
  Angle = 360
  AttacherType = Attacher::AttachEngine3D
  Height = 20
  Placement = pos=(26,-37,19) rot=(0,1,0;1.5708rad)
  Radius = 1.5
FEATURE [Part::Cylinder] Cylinder2195  label="Válec2195"
  Angle = 360
  AttacherType = Attacher::AttachEngine3D
  Height = 30
  Placement = pos=(51,-30,0) rot=(0,0,1;0rad)
  Radius = 1.5
FEATURE [Part::Cylinder] Cylinder2196  label="Válec2196"
  Angle = 360
  AttacherType = Attacher::AttachEngine3D
  Height = 3
  Placement = pos=(35,37,19) rot=(0,1,0;1.5708rad)
  Radius = 3
FEATURE [Part::Compound] Compound981
  Links = -> [Cylinder2191,Cylinder2193,Cylinder2196,Cylinder2187,Cylinder2192,Cylinder2189]
  Placement = pos=(8,0,0) rot=(0,0,1;0rad)
FEATURE [Part::Cylinder] Cylinder2197  label="Válec2197"
  Angle = 360
  AttacherType = Attacher::AttachEngine3D
  Height = 30
  Placement = pos=(51,0,0) rot=(0,0,1;0rad)
  Radius = 1.5
FEATURE [Part::Cylinder] Cylinder2198  label="Válec2198"
  Angle = 360
  AttacherType = Attacher::AttachEngine3D
  Height = 30
  Placement = pos=(51,30,0) rot=(0,0,1;0rad)
  Radius = 1.5
FEATURE [Part::Compound] Compound983
  Links = -> [Cylinder2195,Cylinder2197,Cylinder2198]
FEATURE [Part::Cylinder] Cylinder2199  label="Válec2199"
  Angle = 360
  AttacherType = Attacher::AttachEngine3D
  Height = 20
  Placement = pos=(31,-21,22) rot=(0,1,0;1.5708rad)
  Radius = 1.5
FEATURE [Part::Compound] Compound982
  Links = -> [Cylinder2186,Cylinder2188,Cylinder2190,Cylinder395,Cylinder2199,Cylinder2194]
  Placement = pos=(8,0,0) rot=(0,0,1;0rad)
FEATURE [Part::Cut] Cut801
  Base = -> Compound979
  Tool = -> Compound982
FEATURE [Part::Cut] Cut800
  Base = -> Cut801
  Tool = -> Compound981
FEATURE [Part::Cut] Cut799
  Base = -> Cut800
  Tool = -> Compound983
FEATURE [Part::Box] Box842  label="Krychle841"
  AttacherType = Attacher::AttachEngine3D
  Height = 2
  Length = 6
  Placement = pos=(48,-33,11) rot=(0,0,1;0rad)
  Width = 6
FEATURE [Part::Box] Box843  label="Krychle842"
  AttacherType = Attacher::AttachEngine3D
  Height = 2
  Length = 6
  Placement = pos=(48,-3,11) rot=(0,0,1;0rad)
  Width = 6
FEATURE [Part::Box] Box844  label="Krychle843"
  AttacherType = Attacher::AttachEngine3D
  Height = 2
  Length = 6
  Placement = pos=(48,27,11) rot=(0,0,1;0rad)
  Width = 6
FEATURE [Part::Box] Box845  label="Krychle844"
  AttacherType = Attacher::AttachEngine3D
  Height = 2
  Length = 6
  Placement = pos=(48,27,7) rot=(0,0,1;0rad)
  Width = 6
FEATURE [Part::Compound] Compound980
  Links = -> [Box838,Box843,Box842,Box839,Box844,Box845]
FEATURE [Part::Cut] Cut802  label="jointovina_micro_adapto001"
  Base = -> Cut799
  Placement = pos=(110,-160,0) rot=(0,0,1;3.14159rad)
  Tool = -> Compound980
FEATURE [Part::Cylinder] Cylinder2200  label="Válec2200"
  Angle = 360
  AttacherType = Attacher::AttachEngine3D
  Height = 10
  Placement = pos=(17,-98,44) rot=(1,0,0;1.5708rad)
  Radius = 2
FEATURE [Part::Cut] Cut803
  Base = -> Cut315
  Tool = -> Cylinder2200
FEATURE [Part::Cylinder] Cylinder2201  label="Válec2201"
  Angle = 360
  AttacherType = Attacher::AttachEngine3D
  Height = 10
  Placement = pos=(17,-98,44) rot=(1,0,0;1.5708rad)
  Radius = 2
FEATURE [Part::Cut] Cut804
  Base = -> Cut317
  Placement = pos=(0,-2,0) rot=(0,0,1;0rad)
  Tool = -> Cylinder2201
FEATURE [Part::Box] Box846  label="Krychle845"
  AttacherType = Attacher::AttachEngine3D
  Height = 10
  Length = 8
  Placement = pos=(56,-151,-6) rot=(0,0,1;0rad)
  Width = 59
FEATURE [Part::Box] Box847  label="Krychle846"
  AttacherType = Attacher::AttachEngine3D
  Height = 9
  Length = 8
  Placement = pos=(56,-151,16) rot=(0,0,1;0rad)
  Width = 59
FEATURE [Part::Cylinder] Cylinder2202  label="Válec2202"
  Angle = 360
  AttacherType = Attacher::AttachEngine3D
  Height = 28
  Placement = pos=(17,-92,10) rot=(1,0,0;1.5708rad)
  Radius = 34.5
FEATURE [Part::Torus] Torus004  label="Anuloid004"
  Angle1 = -180
  Angle2 = 180
  Angle3 = 360
  AttacherType = Attacher::AttachEngine3D
  Placement = pos=(17,-98,10) rot=(1,0,0;1.5708rad)
  Radius1 = 34
  Radius2 = 2
FEATURE [Part::Box] Box848  label="Krychle847"
  AttacherType = Attacher::AttachEngine3D
  Height = 28
  Length = 3
  Placement = pos=(44,-110,-4) rot=(0,0,1;0rad)
  Width = 6
FEATURE [Part::Box] Box849  label="Krychle848"
  AttacherType = Attacher::AttachEngine3D
  Height = 28
  Length = 2
  Placement = pos=(-12,-112,-4) rot=(0,0,1;0rad)
  Width = 8
FEATURE [Part::FeaturePython] Tube035  # WARN: FeaturePython — macro-defined, semantics opaque (R4)
  AttacherType = Attacher::AttachEngine3D
  Height = 2
  InnerRadius = 31
  OuterRadius = 39
  Placement = pos=(17,-103,10) rot=(1,0,0;1.5708rad)
FEATURE [Part::Box] Box850  label="Krychle849"
  AttacherType = Attacher::AttachEngine3D
  Height = 28
  Length = 2
  Placement = pos=(-14.1,-111,-4) rot=(0,0,1;0rad)
  Width = 7
FEATURE [Part::Box] Box851  label="Krychle850"
  AttacherType = Attacher::AttachEngine3D
  Height = 30
  Length = 4
  Placement = pos=(-16.1,-105,-5) rot=(0,0,1;0rad)
  Width = 2
FEATURE [Part::Box] Box852  label="Krychle851"
  AttacherType = Attacher::AttachEngine3D
  Height = 28.2
  Length = 2.2
  Placement = pos=(-12.1,-111,-4.1) rot=(0,0,1;0rad)
  Width = 10
FEATURE [Part::Cut] Cut807
  Base = -> Tube035
  Tool = -> Box852
FEATURE [Part::Compound] Compound985
  Links = -> [Box851,Cut807]
FEATURE [Part::Cylinder] Cylinder2203  label="Válec2203"
  Angle = 360
  AttacherType = Attacher::AttachEngine3D
  Height = 20
  Placement = pos=(-17,-108,2) rot=(0,1,0;1.5708rad)
  Radius = 1
FEATURE [Part::Cylinder] Cylinder2204  label="Válec2204"
  Angle = 360
  AttacherType = Attacher::AttachEngine3D
  Height = 20
  Placement = pos=(-17,-108,18) rot=(0,1,0;1.5708rad)
  Radius = 1
FEATURE [Part::Compound] Compound986
  Links = -> [Cylinder2203,Cylinder2204]
FEATURE [Part::Box] Box853  label="Krychle852"
  AttacherType = Attacher::AttachEngine3D
  Height = 28.2
  Length = 2.2
  Placement = pos=(43.9,-111,-4.1) rot=(0,0,1;0rad)
  Width = 10
FEATURE [Part::Box] Box854  label="Krychle853"
  AttacherType = Attacher::AttachEngine3D
  Height = 30
  Length = 4
  Placement = pos=(-16.1,-105,-5) rot=(0,0,1;0rad)
  Width = 1
FEATURE [Part::Box] Box855  label="Krychle854"
  AttacherType = Attacher::AttachEngine3D
  Height = 28
  Length = 2
  Placement = pos=(46.1,-111,-4) rot=(0,0,1;0rad)
  Width = 7
FEATURE [Part::Box] Box856  label="Krychle855"
  AttacherType = Attacher::AttachEngine3D
  Height = 30
  Length = 4
  Placement = pos=(46.1,-105,-5) rot=(0,0,1;0rad)
  Width = 2
FEATURE [Part::Cylinder] Cylinder2205  label="Válec2205"
  Angle = 360
  AttacherType = Attacher::AttachEngine3D
  Height = 20
  Placement = pos=(32,-108,2) rot=(0,1,0;1.5708rad)
  Radius = 1
FEATURE [Part::Cylinder] Cylinder2206  label="Válec2206"
  Angle = 360
  AttacherType = Attacher::AttachEngine3D
  Height = 20
  Placement = pos=(32,-108,18) rot=(0,1,0;1.5708rad)
  Radius = 1
FEATURE [Part::Compound] Compound988
  Links = -> [Cylinder2205,Cylinder2206]
FEATURE [Part::Cut] Cut809
  Base = -> Box855
  Tool = -> Compound988
FEATURE [Part::Cut] Cut810
  Base = -> Compound985
  Tool = -> Box853
FEATURE [Part::Box] Box857  label="Krychle856"
  AttacherType = Attacher::AttachEngine3D
  Height = 28
  Length = 2
  Placement = pos=(44,-112,-4) rot=(0,0,1;0rad)
  Width = 8
FEATURE [Part::Cut] Cut811
  Base = -> Box850
  Tool = -> Compound986
FEATURE [Part::Chamfer] Chamfer067
  Base = -> Cut811
  Edges = 2 edges r=1.5: [Edge2,Edge3]
FEATURE [Part::Chamfer] Chamfer068
  Base = -> Cut809
  Edges = 2 edges r=1.5: [Edge11,Edge13]
FEATURE [Part::Chamfer] Chamfer069
  Base = -> Cut811
  Edges = 2 edges r=1.5: [Edge2,Edge3]
FEATURE [Part::Compound] Compound989
  Links = -> [Chamfer069,Chamfer068,Cut810]
FEATURE [Part::Compound] Compound990  label="wrist_halo_cover"
  Links = -> [Box856,Compound989]
  Placement = pos=(0,-3,0) rot=(0,0,1;0rad)
FEATURE [Part::Cylinder] Cylinder2207  label="Válec2207"
  Angle = 360
  AttacherType = Attacher::AttachEngine3D
  Height = 32
  Placement = pos=(59,-130,-6) rot=(0,0,1;0rad)
  Radius = 1.5
FEATURE [Part::Cylinder] Cylinder2208  label="Válec2208"
  Angle = 360
  AttacherType = Attacher::AttachEngine3D
  Height = 32
  Placement = pos=(59,-144,-6) rot=(0,0,1;0rad)
  Radius = 1.5
FEATURE [Part::Cylinder] Cylinder2209  label="Válec2209"
  Angle = 360
  AttacherType = Attacher::AttachEngine3D
  Height = 4
  Placement = pos=(59,-130,-8) rot=(0,0,1;0rad)
  Radius = 3
FEATURE [Part::Cylinder] Cylinder2210  label="Válec2210"
  Angle = 360
  AttacherType = Attacher::AttachEngine3D
  Height = 4
  Placement = pos=(59,-144,-8) rot=(0,0,1;0rad)
  Radius = 3
FEATURE [Part::Cylinder] Cylinder2211  label="Válec2211"
  Angle = 360
  AttacherType = Attacher::AttachEngine3D
  Height = 4
  Placement = pos=(59,-144,24) rot=(0,0,1;0rad)
  Radius = 3
FEATURE [Part::Cylinder] Cylinder2212  label="Válec2212"
  Angle = 360
  AttacherType = Attacher::AttachEngine3D
  Height = 4
  Placement = pos=(59,-130,24) rot=(0,0,1;0rad)
  Radius = 3
FEATURE [Part::Compound] Compound991
  Links = -> [Cylinder2211,Cylinder2212]
FEATURE [Part::Compound] Compound992
  Links = -> [Cylinder2209,Cylinder2210]
FEATURE [Part::Compound] Compound993
  Links = -> [Cylinder2207,Cylinder2208]
FEATURE [Part::FeaturePython] Tube036  # WARN: FeaturePython — macro-defined, semantics opaque (R4)
  AttacherType = Attacher::AttachEngine3D
  Height = 13
  InnerRadius = 31
  OuterRadius = 38.5
  Placement = pos=(17,-105.5,10) rot=(1,0,0;1.5708rad)
FEATURE [Part::Compound] Compound994  label="wrist_halo_inner2"
  Links = -> [Box849,Box857,Cut803]
  Placement = pos=(0,-2,0) rot=(0,0,1;0rad)
FEATURE [Part::Compound] Compound995  label="wrist_halo_inner003"
  Links = -> [Cut316,Compound994]
FEATURE [Part::FeaturePython] Tube037  # WARN: FeaturePython — macro-defined, semantics opaque (R4)
  AttacherType = Attacher::AttachEngine3D
  Height = 0.5
  InnerRadius = 34.5
  OuterRadius = 39
  Placement = pos=(17,-93.5,10) rot=(1,0,0;1.5708rad)
FEATURE [Part::FeaturePython] Tube038  # WARN: FeaturePython — macro-defined, semantics opaque (R4)
  AttacherType = Attacher::AttachEngine3D
  Height = 1.5
  InnerRadius = 31
  OuterRadius = 39
  Placement = pos=(17,-92,10) rot=(1,0,0;1.5708rad)
FEATURE [Part::Compound] Compound996
  Links = -> [Tube038,Tube037]
FEATURE [Part::Torus] Torus005  label="Anuloid005"
  Angle1 = -180
  Angle2 = 180
  Angle3 = 360
  AttacherType = Attacher::AttachEngine3D
  Placement = pos=(17,-100,10) rot=(1,0,0;1.5708rad)
  Radius1 = 34
  Radius2 = 2
FEATURE [Part::Cylinder] Cylinder2213  label="Válec2213"
  Angle = 360
  AttacherType = Attacher::AttachEngine3D
  Height = 40
  Placement = pos=(60,-86,21) rot=(1,0,0;1.5708rad)
  Radius = 1.5
FEATURE [Part::Torus] Torus006  label="Anuloid006"
  Angle1 = -180
  Angle2 = 180
  Angle3 = 360
  AttacherType = Attacher::AttachEngine3D
  Placement = pos=(17,-100,10) rot=(1,0,0;1.5708rad)
  Radius1 = 34
  Radius2 = 2
FEATURE [Part::Torus] Torus007  label="Anuloid007"
  Angle1 = -180
  Angle2 = 180
  Angle3 = 360
  AttacherType = Attacher::AttachEngine3D
  Placement = pos=(17,-98,10) rot=(1,0,0;1.5708rad)
  Radius1 = 34
  Radius2 = 2
FEATURE [Part::FeaturePython] Tube039  # WARN: FeaturePython — macro-defined, semantics opaque (R4)
  AttacherType = Attacher::AttachEngine3D
  Height = 13
  InnerRadius = 31
  OuterRadius = 38.5
  Placement = pos=(17,-105.5,10) rot=(1,0,0;1.5708rad)
FEATURE [Part::Cylinder] Cylinder2214  label="Válec2214"
  Angle = 360
  AttacherType = Attacher::AttachEngine3D
  Height = 32
  Placement = pos=(53,-144,-6) rot=(0,0,1;0rad)
  Radius = 1.5
FEATURE [Part::Box] Box858  label="Krychle857"
  AttacherType = Attacher::AttachEngine3D
  Height = 8
  Length = 8
  Placement = pos=(50,-151,-4) rot=(0,0,1;0rad)
  Width = 59
FEATURE [Part::Cylinder] Cylinder2215  label="Válec2215"
  Angle = 360
  AttacherType = Attacher::AttachEngine3D
  Height = 28
  Placement = pos=(17,-92,10) rot=(1,0,0;1.5708rad)
  Radius = 34.5
FEATURE [Part::Box] Box859  label="Krychle858"
  AttacherType = Attacher::AttachEngine3D
  Height = 8
  Length = 8
  Placement = pos=(50,-151,16) rot=(0,0,1;0rad)
  Width = 59
FEATURE [Part::Compound] Compound997
  Links = -> [Box858,Box859]
FEATURE [Part::Cut] Cut820
  Base = -> Compound997
  Tool = -> Torus007
FEATURE [Part::Cut] Cut821
  Base = -> Cut820
  Tool = -> Cylinder2215
FEATURE [Part::Chamfer] Chamfer072
  Base = -> Cut821
  Edges = 2 edges r=4: [Edge26,Edge53]
FEATURE [Part::Chamfer] Chamfer074
  Base = -> Chamfer072
  Edges = 1 edges r=0.9: [Edge28]
FEATURE [Part::Chamfer] Chamfer073
  Base = -> Chamfer074
  Edges = 1 edges r=0.9: [Edge59]
FEATURE [Part::Cylinder] Cylinder2216  label="Válec2216"
  Angle = 360
  AttacherType = Attacher::AttachEngine3D
  Height = 32
  Placement = pos=(53,-128,-6) rot=(0,0,1;0rad)
  Radius = 1.5
FEATURE [Part::Compound] Compound998
  Links = -> [Cylinder2216,Cylinder2214]
FEATURE [Part::Cylinder] Cylinder2217  label="Válec2217"
  Angle = 360
  AttacherType = Attacher::AttachEngine3D
  Height = 4
  Placement = pos=(53,-144,20) rot=(0,0,1;0rad)
  Radius = 3
FEATURE [Part::Cylinder] Cylinder2218  label="Válec2218"
  Angle = 360
  AttacherType = Attacher::AttachEngine3D
  Height = 4
  Placement = pos=(53,-128,-4) rot=(0,0,1;0rad)
  Radius = 3
FEATURE [Part::Cylinder] Cylinder2219  label="Válec2219"
  Angle = 360
  AttacherType = Attacher::AttachEngine3D
  Height = 4
  Placement = pos=(53,-128,20) rot=(0,0,1;0rad)
  Radius = 3
FEATURE [Part::Compound] Compound999
  Links = -> [Cylinder2217,Cylinder2219]
FEATURE [Part::Cut] Cut822
  Base = -> Chamfer073
  Tool = -> Compound999
FEATURE [Part::Cylinder] Cylinder2220  label="Válec2220"
  Angle = 360
  AttacherType = Attacher::AttachEngine3D
  Height = 4
  Placement = pos=(53,-144,-4) rot=(0,0,1;0rad)
  Radius = 3
FEATURE [Part::Compound] Compound1000
  Links = -> [Cylinder2218,Cylinder2220]
FEATURE [Part::Cut] Cut817
  Base = -> Cut822
  Tool = -> Compound1000
FEATURE [Part::Cut] Cut819
  Base = -> Cut817
  Tool = -> Compound998
FEATURE [Part::Cut] Cut823
  Base = -> Cut819
  Tool = -> Tube039
FEATURE [Part::Chamfer] Chamfer076
  Base = -> Cut823
  Edges = 1 edges r=5: [Edge94]
FEATURE [Part::Chamfer] Chamfer075
  Base = -> Chamfer076
  Edges = 1 edges r=5: [Edge67]
FEATURE [Part::Cut] Cut818  label="stary_drzak"
  Base = -> Chamfer075
  Tool = -> Torus006
FEATURE [Part::Cylinder] Cylinder2221  label="Válec2221"
  Angle = 360
  AttacherType = Attacher::AttachEngine3D
  Height = 40
  Placement = pos=(60,-86,-1) rot=(1,0,0;1.5708rad)
  Radius = 1.5
FEATURE [Part::Cylinder] Cylinder2222  label="Válec2222"
  Angle = 360
  AttacherType = Attacher::AttachEngine3D
  Height = 6
  Placement = pos=(60,-86,21) rot=(1,0,0;1.5708rad)
  Radius = 3
FEATURE [Part::Cylinder] Cylinder2223  label="Válec2223"
  Angle = 360
  AttacherType = Attacher::AttachEngine3D
  Height = 6
  Placement = pos=(60,-86,-1) rot=(1,0,0;1.5708rad)
  Radius = 3
FEATURE [Part::Box] Box860  label="Krychle859"
  AttacherType = Attacher::AttachEngine3D
  Height = 10
  Length = 6
  Placement = pos=(50,-105.5,-6) rot=(0,0,1;0rad)
  Width = 13.5
FEATURE [Part::Box] Box861  label="Krychle860"
  AttacherType = Attacher::AttachEngine3D
  Height = 9
  Length = 6
  Placement = pos=(50,-105.5,16) rot=(0,0,1;0rad)
  Width = 13.5
FEATURE [Part::FeaturePython] Tube040  # WARN: FeaturePython — macro-defined, semantics opaque (R4)
  AttacherType = Attacher::AttachEngine3D
  Height = 13.5
  InnerRadius = 31
  OuterRadius = 39
  Placement = pos=(17,-92,10) rot=(1,0,0;1.5708rad)
FEATURE [Part::Compound] Compound1001
  Links = -> [Box861,Box860]
FEATURE [Part::Cut] Cut824
  Base = -> Compound1001
  Tool = -> Tube040
FEATURE [Part::Chamfer] Chamfer077
  Base = -> Box846
  Edges = 1 edges r=6: [Edge7]
FEATURE [Part::Chamfer] Chamfer078
  Base = -> Box847
  Edges = 1 edges r=6: [Edge7]
FEATURE [Part::Compound] Compound1002
  Links = -> [Cylinder2223,Cylinder2222]
  Placement = pos=(0,-6,0) rot=(0,0,1;0rad)
FEATURE [Part::Compound] Compound1003
  Links = -> [Chamfer078,Chamfer077]
FEATURE [Part::Cut] Cut825
  Base = -> Compound1003
  Tool = -> Compound1002
FEATURE [Part::Compound] Compound1004
  Links = -> [Cylinder2221,Cylinder2213]
FEATURE [Part::Cut] Cut826
  Base = -> Cut825
  Tool = -> Compound1004
FEATURE [Part::Cut] Cut827
  Base = -> Cut826
  Tool = -> Compound993
FEATURE [Part::Cut] Cut828
  Base = -> Cut827
  Tool = -> Compound992
FEATURE [Part::Cut] Cut829
  Base = -> Cut828
  Tool = -> Compound991
FEATURE [Part::Compound] Compound1005
  Links = -> [Cut804,Compound996]
FEATURE [Part::Compound] Compound1006  label="wrist_halo_outer3"
  Links = -> [Cut824,Cut829,Compound1005]
FEATURE [Part::Cylinder] Cylinder2224  label="Válec2224"
  Angle = 360
  AttacherType = Attacher::AttachEngine3D
  Height = 20
  Placement = pos=(-17,-108,2) rot=(0,1,0;1.5708rad)
  Radius = 1
FEATURE [Part::Cylinder] Cylinder2225  label="Válec2225"
  Angle = 360
  AttacherType = Attacher::AttachEngine3D
  Height = 20
  Placement = pos=(-17,-108,18) rot=(0,1,0;1.5708rad)
  Radius = 1
FEATURE [Part::Compound] Compound1008
  Links = -> [Cylinder2224,Cylinder2225]
  Placement = pos=(0,-3,0) rot=(0,0,1;0rad)
FEATURE [Part::Cylinder] Cylinder2226  label="Válec2226"
  Angle = 360
  AttacherType = Attacher::AttachEngine3D
  Height = 20
  Placement = pos=(32,-108,2) rot=(0,1,0;1.5708rad)
  Radius = 1
FEATURE [Part::Cylinder] Cylinder2227  label="Válec2227"
  Angle = 360
  AttacherType = Attacher::AttachEngine3D
  Height = 20
  Placement = pos=(32,-108,18) rot=(0,1,0;1.5708rad)
  Radius = 1
FEATURE [Part::Compound] Compound1007
  Links = -> [Cylinder2226,Cylinder2227]
  Placement = pos=(0,-3,0) rot=(0,0,1;0rad)
FEATURE [Part::Cylinder] Cylinder2228  label="Válec2228"
  Angle = 360
  AttacherType = Attacher::AttachEngine3D
  Height = 20
  Placement = pos=(32,-108,18) rot=(0,1,0;1.5708rad)
  Radius = 1
FEATURE [Part::Cylinder] Cylinder2229  label="Válec2229"
  Angle = 360
  AttacherType = Attacher::AttachEngine3D
  Height = 20
  Placement = pos=(-17,-108,18) rot=(0,1,0;1.5708rad)
  Radius = 1
FEATURE [Part::Cylinder] Cylinder2230  label="Válec2230"
  Angle = 360
  AttacherType = Attacher::AttachEngine3D
  Height = 20
  Placement = pos=(32,-108,2) rot=(0,1,0;1.5708rad)
  Radius = 1
FEATURE [Part::Cylinder] Cylinder2231  label="Válec2231"
  Angle = 360
  AttacherType = Attacher::AttachEngine3D
  Height = 20
  Placement = pos=(-17,-108,2) rot=(0,1,0;1.5708rad)
  Radius = 1
FEATURE [Part::Compound] Compound1009
  Links = -> [Cylinder2230,Cylinder2228]
  Placement = pos=(0,-3,0) rot=(0,0,1;0rad)
FEATURE [Part::Compound] Compound1010
  Links = -> [Cylinder2231,Cylinder2229]
  Placement = pos=(0,-3,0) rot=(0,0,1;0rad)
FEATURE [Part::Compound] Compound1011
  Links = -> [Compound1007,Compound1008]
FEATURE [Part::Cut] Cut830  label="wrist_halo_inner"
  Base = -> Compound995
  Tool = -> Compound1011
FEATURE [Part::Compound] Compound1012
  Links = -> [Compound1009,Compound1010]
FEATURE [Part::Cylinder] Cylinder2232  label="Válec2232"
  Angle = 360
  AttacherType = Attacher::AttachEngine3D
  Height = 20
  Placement = pos=(32,-108,2) rot=(0,1,0;1.5708rad)
  Radius = 1
FEATURE [Part::Cylinder] Cylinder2233  label="Válec2233"
  Angle = 360
  AttacherType = Attacher::AttachEngine3D
  Height = 20
  Placement = pos=(-17,-108,2) rot=(0,1,0;1.5708rad)
  Radius = 1
FEATURE [Part::Cylinder] Cylinder2234  label="Válec2234"
  Angle = 360
  AttacherType = Attacher::AttachEngine3D
  Height = 20
  Placement = pos=(32,-108,18) rot=(0,1,0;1.5708rad)
  Radius = 1
FEATURE [Part::Cylinder] Cylinder2235  label="Válec2235"
  Angle = 360
  AttacherType = Attacher::AttachEngine3D
  Height = 20
  Placement = pos=(-17,-108,18) rot=(0,1,0;1.5708rad)
  Radius = 1
FEATURE [Part::Compound] Compound1014
  Links = -> [Cylinder2232,Cylinder2234]
  Placement = pos=(0,-3,0) rot=(0,0,1;0rad)
FEATURE [Part::Compound] Compound1015
  Links = -> [Cylinder2233,Cylinder2235]
  Placement = pos=(0,-3,0) rot=(0,0,1;0rad)
FEATURE [Part::Compound] Compound1013
  Links = -> [Compound1014,Compound1015]
FEATURE [Part::Cut] Cut831
  Base = -> Chamfer050
  Tool = -> Compound1012
FEATURE [Part::Box] Box862  label="Krychle861"
  AttacherType = Attacher::AttachEngine3D
  Height = 4
  Length = 4
  Placement = pos=(-7,-113,16) rot=(0,0,1;0rad)
  Width = 4
FEATURE [Part::Box] Box863  label="Krychle862"
  AttacherType = Attacher::AttachEngine3D
  Height = 4
  Length = 4
  Placement = pos=(-7,-113,0) rot=(0,0,1;0rad)
  Width = 4
FEATURE [Part::Box] Box864  label="Krychle863"
  AttacherType = Attacher::AttachEngine3D
  Height = 4
  Length = 4
  Placement = pos=(37,-113,16) rot=(0,0,1;0rad)
  Width = 4
FEATURE [Part::Box] Box865  label="Krychle864"
  AttacherType = Attacher::AttachEngine3D
  Height = 4
  Length = 4
  Placement = pos=(37,-113,0) rot=(0,0,1;0rad)
  Width = 4
FEATURE [Part::Compound] Compound1016
  Links = -> [Box862,Box863,Box864,Box865]
FEATURE [Part::Cut] Cut832
  Base = -> Cut831
  Tool = -> Compound1016
FEATURE [Part::Box] Box866  label="Krychle865"
  AttacherType = Attacher::AttachEngine3D
  Height = 12
  Length = 11
  Placement = pos=(53,-105.5,4) rot=(0,0,1;0rad)
  Width = 13.5
FEATURE [Part::FeaturePython] Tube041  # WARN: FeaturePython — macro-defined, semantics opaque (R4)
  AttacherType = Attacher::AttachEngine3D
  Height = 13.5
  InnerRadius = 31
  OuterRadius = 39
  Placement = pos=(17,-92,10) rot=(1,0,0;1.5708rad)
FEATURE [Part::Cut] Cut833
  Base = -> Box866
  Tool = -> Tube041
FEATURE [Part::Chamfer] Chamfer079
  Base = -> Cut833
  Edges = 1 edges r=6: [Edge10]
FEATURE [Part::Cylinder] Cylinder2236  label="Válec2236"
  Angle = 360
  AttacherType = Attacher::AttachEngine3D
  Height = 16
  Placement = pos=(64,-92,10) rot=(1,0,0;1.5708rad)
  Radius = 6
FEATURE [Part::Cut] Cut834
  Base = -> Chamfer079
  Tool = -> Cylinder2236
FEATURE [Part::Compound] Compound1017  label="wrist_halo_outer"
  Links = -> [Compound1006,Cut834]
FEATURE [Mesh::Feature] Mesh025  label="wrist_halo_outer (Meshed)"
FEATURE [Part::Compound] Compound1018  label="wrist_moto_hold"
  Links = -> [Cut832,Cut297]
FEATURE [Part::Box] Box867  label="Krychle866"
  AttacherType = Attacher::AttachEngine3D
  Height = 6
  Length = 6
  Placement = pos=(0,-131,0) rot=(0,0,1;0rad)
  Width = 39
FEATURE [Part::Box] Box868  label="Krychle867"
  AttacherType = Attacher::AttachEngine3D
  Height = 6
  Length = 2
  Placement = pos=(-1,-138,-2) rot=(0,0,1;0rad)
  Width = 6
FEATURE [Part::Box] Box869  label="Krychle868"
  AttacherType = Attacher::AttachEngine3D
  Height = 6
  Length = 2
  Placement = pos=(-1,-138,16) rot=(0,0,1;0rad)
  Width = 6
FEATURE [Part::Box] Box870  label="Krychle869"
  AttacherType = Attacher::AttachEngine3D
  Height = 6
  Length = 2
  Placement = pos=(33,-138,-2) rot=(0,0,1;0rad)
  Width = 6
FEATURE [Part::Box] Box871  label="Krychle870"
  AttacherType = Attacher::AttachEngine3D
  Height = 6
  Length = 2
  Placement = pos=(33,-138,16) rot=(0,0,1;0rad)
  Width = 6
FEATURE [Part::Cylinder] Cylinder2237  label="Válec2237"
  Angle = 360
  AttacherType = Attacher::AttachEngine3D
  Height = 3
  Placement = pos=(8.41904,-20.3253,34) rot=(0,0,1;3.53429rad)
  Radius = 3
FEATURE [Part::Cylinder] Cylinder2238  label="Válec2238"
  Angle = 360
  AttacherType = Attacher::AttachEngine3D
  Height = 60
  Placement = pos=(20.3253,8.41904,34) rot=(0,0,-1;1.1781rad)
  Radius = 1.5
FEATURE [Part::Cylinder] Cylinder2239  label="Válec2239"
  Angle = 360
  AttacherType = Attacher::AttachEngine3D
  Height = 6
  Placement = pos=(0,0,39) rot=(0,0,1;0rad)
  Radius = 30
FEATURE [Part::Cylinder] Cylinder2240  label="Válec2240"
  Angle = 360
  AttacherType = Attacher::AttachEngine3D
  Height = 60
  Placement = pos=(-8.41904,20.3253,34) rot=(0,0,1;0.392699rad)
  Radius = 1.5
FEATURE [Part::Cylinder] Cylinder2241  label="Válec2241"
  Angle = 360
  AttacherType = Attacher::AttachEngine3D
  Height = 3
  Placement = pos=(-20.3253,-8.41904,34) rot=(0,0,1;1.96349rad)
  Radius = 3
FEATURE [Part::Cylinder] Cylinder2242  label="Válec2242"
  Angle = 360
  AttacherType = Attacher::AttachEngine3D
  Height = 60
  Placement = pos=(-20.3253,-8.41904,34) rot=(0,0,1;1.96349rad)
  Radius = 1.5
FEATURE [Part::Cylinder] Cylinder2243  label="Válec2243"
  Angle = 360
  AttacherType = Attacher::AttachEngine3D
  Height = 3
  Placement = pos=(-8.41904,20.3253,34) rot=(0,0,1;0.392699rad)
  Radius = 3
FEATURE [Part::Cylinder] Cylinder2244  label="Válec2244"
  Angle = 360
  AttacherType = Attacher::AttachEngine3D
  Height = 60
  Placement = pos=(8.41904,-20.3253,34) rot=(0,0,1;3.53429rad)
  Radius = 1.5
FEATURE [Part::Box] Box872  label="Krychle871"
  AttacherType = Attacher::AttachEngine3D
  Height = 20
  Length = 10
  Placement = pos=(-35,-38.15,45) rot=(0,0,1;0rad)
  Width = 80
FEATURE [Part::Cylinder] Cylinder2245  label="Válec2245"
  Angle = 360
  AttacherType = Attacher::AttachEngine3D
  Height = 3
  Placement = pos=(20.3253,8.41904,34) rot=(0,0,-1;1.1781rad)
  Radius = 3
FEATURE [Part::Box] Box873  label="Krychle872"
  AttacherType = Attacher::AttachEngine3D
  Height = 20
  Length = 10
  Placement = pos=(25,-38.15,45) rot=(0,0,1;0rad)
  Width = 80
FEATURE [Part::Compound] Compound1019
  Links = -> [Cylinder2240,Cylinder2242,Cylinder2244,Cylinder2238]
  Placement = pos=(0,0,0) rot=(0,0,1;0.392699rad)
FEATURE [Part::Compound] Compound1020
  Links = -> [Cylinder2243,Cylinder2241,Cylinder2237,Cylinder2245]
  Placement = pos=(0,0,8) rot=(0,0,1;0.392699rad)
FEATURE [Part::Cut] Cut836
  Base = -> Cylinder2239
  Placement = pos=(0,0,3) rot=(0,0,1;0rad)
  Tool = -> Compound1020
FEATURE [Part::Cut] Cut837
  Base = -> Cut836
  Tool = -> Compound1019
FEATURE [Part::Compound] Compound1021
  Links = -> [Box872,Box873]
  Placement = pos=(0,0,-8) rot=(0,0,1;0rad)
FEATURE [Part::Cut] Cut835
  Base = -> Cut837
  Tool = -> Compound1021
FEATURE [Part::Cylinder] Cylinder2246  label="Válec2246"
  Angle = 360
  AttacherType = Attacher::AttachEngine3D
  Height = 20
  Placement = pos=(0,0,37) rot=(0,0,1;0rad)
  Radius = 16
FEATURE [Part::Cut] Cut838
  Base = -> Cut835
  Placement = pos=(17,-180,10) rot=(-1,0,0;1.5708rad)
  Tool = -> Cylinder2246
FEATURE [Part::Box] Box874  label="Krychle873"
  AttacherType = Attacher::AttachEngine3D
  Height = 32.2
  Length = 5.85
  Placement = pos=(-10,-138,-6.1) rot=(0,0,1;0rad)
  Width = 60
FEATURE [Part::Box] Box875  label="Krychle874"
  AttacherType = Attacher::AttachEngine3D
  Height = 32.2
  Length = 5.85
  Placement = pos=(38.15,-138,-6.1) rot=(0,0,1;0rad)
  Width = 60
FEATURE [Part::Compound] Compound1022
  Links = -> [Box874,Box875]
FEATURE [Part::Cut] Cut839
  Base = -> Cut838
  Tool = -> Compound1022
FEATURE [Part::Compound] Compound1023
  Links = -> [Box868,Box869,Box870,Box871]
FEATURE [Part::Cut] Cut840  label="wrist_actuator_ring2"
  Base = -> Cut839
  Tool = -> Compound1023
FEATURE [Part::Cylinder] Cylinder2247  label="Válec2247"
  Angle = 360
  AttacherType = Attacher::AttachEngine3D
  Height = 16
  Placement = pos=(14,9,64) rot=(0,1,0;1.5708rad)
  Radius = 1.5
FEATURE [Part::Cylinder] Cylinder2248  label="Válec2248"
  Angle = 360
  AttacherType = Attacher::AttachEngine3D
  Height = 16
  Placement = pos=(14,-9,64) rot=(0,1,0;1.5708rad)
  Radius = 1.5
FEATURE [Part::Cylinder] Cylinder2249  label="Válec2249"
  Angle = 360
  AttacherType = Attacher::AttachEngine3D
  Height = 16
  Placement = pos=(-24,9,64) rot=(0,1,0;1.5708rad)
  Radius = 1.5
FEATURE [Part::Cylinder] Cylinder2250  label="Válec2250"
  Angle = 360
  AttacherType = Attacher::AttachEngine3D
  Height = 16
  Placement = pos=(-24,-9,64) rot=(0,1,0;1.5708rad)
  Radius = 1.5
FEATURE [Part::Compound] Compound1024
  Links = -> [Cylinder2249,Cylinder2250,Cylinder2247,Cylinder2248]
  Placement = pos=(14,-71,10) rot=(1,0,0;1.5708rad)
FEATURE [Part::Cut] Cut841  label="wrist_actuator_ring"
  Base = -> Cut840
  Tool = -> Compound1024
FEATURE [Mesh::Feature] Mesh026  label="wrist_halo_inner (Meshed)"
FEATURE [Mesh::Feature] Mesh027  label="wrist_halo_outer (Meshed)001"
